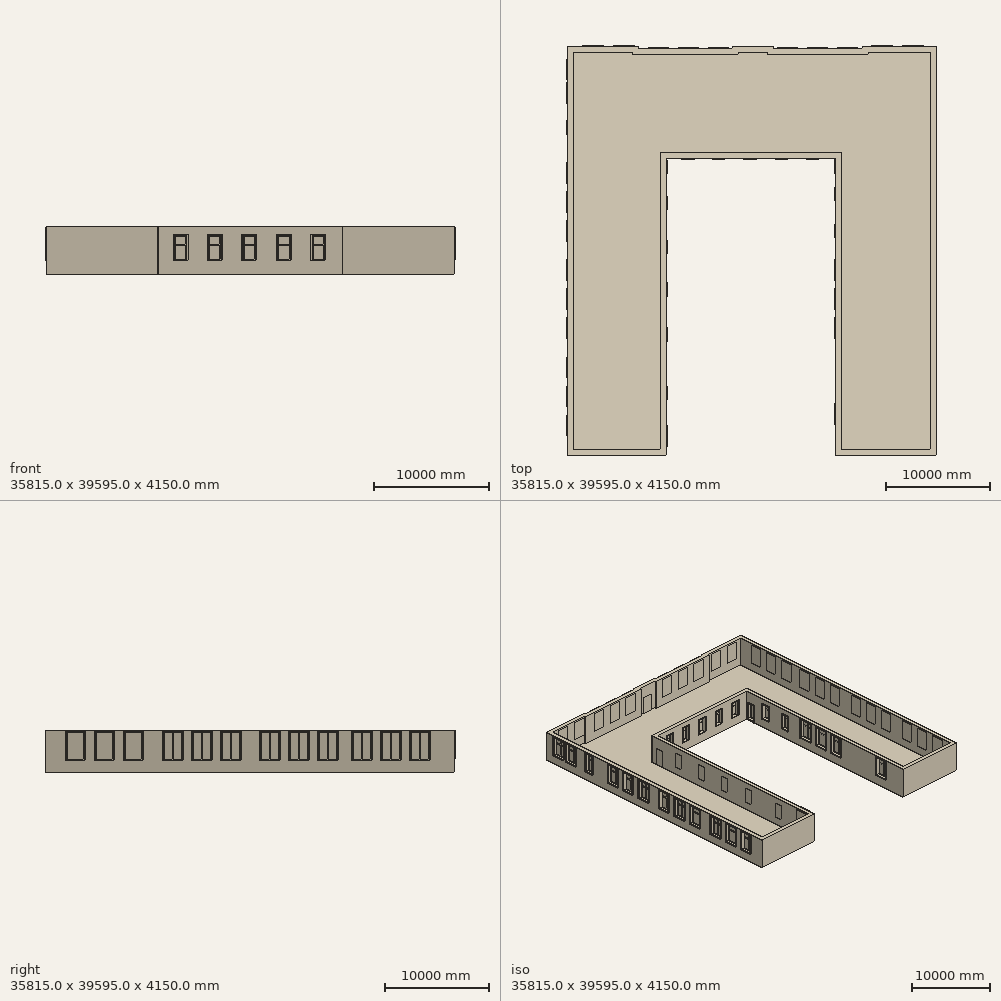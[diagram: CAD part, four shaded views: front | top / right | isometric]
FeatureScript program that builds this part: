
annotation { "Feature Type Name" : "Feature", "Feature Type Description" : "" }
export const myFeature = defineFeature(function(context is Context, id is Id, definition is map)
    precondition{}
    {
        {
            var Q0;
            Q0=qCreatedBy(makeId("Top.planeOp"),FACE);
            var sketch = newSketch(context, id + "F0", { "sketchPlane" : qUnion([Q0])});
            skLineSegment(sketch, "E0", {"start": v(0, 0) * mm, "end": v(0, 39360) * mm});
            skLineSegment(sketch, "E1", {"start": v(0, 39360) * mm, "end": v(-7000, 39360) * mm});
            skLineSegment(sketch, "E2", {"start": v(-7000, 39360) * mm, "end": v(-7000, 39160) * mm});
            skLineSegment(sketch, "E3", {"start": v(-7000, 39160) * mm, "end": v(-15730, 39160) * mm});
            skLineSegment(sketch, "E4", {"start": v(-15730, 39160) * mm, "end": v(-15730, 39360) * mm});
            skLineSegment(sketch, "E5", {"start": v(-15730, 39360) * mm, "end": v(-19480, 39360) * mm});
            skLineSegment(sketch, "E6", {"start": v(-19480, 39360) * mm, "end": v(-19480, 39160) * mm});
            skLineSegment(sketch, "E7", {"start": v(-19480, 39160) * mm, "end": v(-28730, 39160) * mm});
            skLineSegment(sketch, "E8", {"start": v(-28730, 39160) * mm, "end": v(-28730, 39360) * mm});
            skLineSegment(sketch, "E9", {"start": v(-28730, 39360) * mm, "end": v(-35480, 39360) * mm});
            skLineSegment(sketch, "E10", {"start": v(-35480, 39360) * mm, "end": v(-35480, 0) * mm});
            skLineSegment(sketch, "E11", {"start": v(-35480, 0) * mm, "end": v(-26000, 0) * mm});
            skLineSegment(sketch, "E12", {"start": v(-26000, 0) * mm, "end": v(-26000, 28660) * mm});
            skLineSegment(sketch, "E13", {"start": v(-26000, 28660) * mm, "end": v(-9600, 28660) * mm});
            skLineSegment(sketch, "E14", {"start": v(-9600, 28660) * mm, "end": v(-9600, 0) * mm});
            skLineSegment(sketch, "E15", {"start": v(-9600, 0) * mm, "end": v(0, 0) * mm});
            skLineSegment(sketch, "E16.0", {"start": v(-500, 500) * mm, "end": v(-500, 38860) * mm});
            skLineSegment(sketch, "E16.1", {"start": v(-9100, 500) * mm, "end": v(-500, 500) * mm});
            skLineSegment(sketch, "E16.2", {"start": v(-9100, 29160) * mm, "end": v(-9100, 500) * mm});
            skLineSegment(sketch, "E16.3", {"start": v(-26500, 29160) * mm, "end": v(-9100, 29160) * mm});
            skLineSegment(sketch, "E16.4", {"start": v(-26500, 500) * mm, "end": v(-26500, 29160) * mm});
            skLineSegment(sketch, "E16.5", {"start": v(-16230, 38860) * mm, "end": v(-18980, 38860) * mm});
            skLineSegment(sketch, "E16.6", {"start": v(-16230, 38660) * mm, "end": v(-16230, 38860) * mm});
            skLineSegment(sketch, "E16.7", {"start": v(-6500, 38660) * mm, "end": v(-16230, 38660) * mm});
            skLineSegment(sketch, "E16.8", {"start": v(-6500, 38860) * mm, "end": v(-6500, 38660) * mm});
            skLineSegment(sketch, "E16.9", {"start": v(-18980, 38860) * mm, "end": v(-18980, 38660) * mm});
            skLineSegment(sketch, "E16.10", {"start": v(-18980, 38660) * mm, "end": v(-29230, 38660) * mm});
            skLineSegment(sketch, "E16.11", {"start": v(-29230, 38660) * mm, "end": v(-29230, 38860) * mm});
            skLineSegment(sketch, "E16.12", {"start": v(-29230, 38860) * mm, "end": v(-34980, 38860) * mm});
            skLineSegment(sketch, "E16.13", {"start": v(-34980, 38860) * mm, "end": v(-34980, 500) * mm});
            skLineSegment(sketch, "E16.14", {"start": v(-500, 38860) * mm, "end": v(-6500, 38860) * mm});
            skLineSegment(sketch, "E16.15", {"start": v(-34980, 500) * mm, "end": v(-26500, 500) * mm});
            skLineSegment(sketch, "E17.0", {"start": v(-28640, 39250) * mm, "end": v(-28640, 39450) * mm});
            skLineSegment(sketch, "E17.1", {"start": v(-19570, 39250) * mm, "end": v(-28640, 39250) * mm});
            skLineSegment(sketch, "E17.2", {"start": v(-19570, 39450) * mm, "end": v(-19570, 39250) * mm});
            skLineSegment(sketch, "E17.3", {"start": v(-15640, 39450) * mm, "end": v(-19570, 39450) * mm});
            skLineSegment(sketch, "E17.4", {"start": v(-15640, 39250) * mm, "end": v(-15640, 39450) * mm});
            skLineSegment(sketch, "E17.5", {"start": v(-25910, 28570) * mm, "end": v(-9690, 28570) * mm});
            skLineSegment(sketch, "E17.6", {"start": v(-25910, -90) * mm, "end": v(-25910, 28570) * mm});
            skLineSegment(sketch, "E17.7", {"start": v(-35570, -90) * mm, "end": v(-25910, -90) * mm});
            skLineSegment(sketch, "E17.8", {"start": v(-35570, 39450) * mm, "end": v(-35570, -90) * mm});
            skLineSegment(sketch, "E17.9", {"start": v(-9690, 28570) * mm, "end": v(-9690, -90) * mm});
            skLineSegment(sketch, "E17.10", {"start": v(-9690, -90) * mm, "end": v(90, -90) * mm});
            skLineSegment(sketch, "E17.11", {"start": v(90, -90) * mm, "end": v(90, 39450) * mm});
            skLineSegment(sketch, "E17.12", {"start": v(90, 39450) * mm, "end": v(-7090, 39450) * mm});
            skLineSegment(sketch, "E17.13", {"start": v(-7090, 39450) * mm, "end": v(-7090, 39250) * mm});
            skLineSegment(sketch, "E17.14", {"start": v(-28640, 39450) * mm, "end": v(-35570, 39450) * mm});
            skLineSegment(sketch, "E17.15", {"start": v(-7090, 39250) * mm, "end": v(-15640, 39250) * mm});
            skSolve(sketch);
        }
        {
            var Q0;
            Q0=qSketchRegion(id+"F0",true);
            var Q1;
            Q1=makeQuery(id+"F0.imprint","IMPRINT",FACE,{"disambiguationData":[TD([[makeQuery(id+"F0.imprint","IMPRINT",EDGE,{"derivedFrom":sQuery(id+"F0.wireOp",EDGE,"E0")}),1.0]])]});
            extrude(context, id + "F1", {"entities" : qUnion([Q0, Q1]), "depth" : 4000 * mm, "offsetDistance" : 25 * mm});
        }
        {
            var Q0;
            Q0=makeQuery(id+"F1.opExtrude","CAP_FACE",FACE,{"disambiguationData":[OSD([sQuery(id+"F0.wireOp",EDGE,"E16.0"),sQuery(id+"F0.wireOp",EDGE,"E16.1"),sQuery(id+"F0.wireOp",EDGE,"E16.2"),sQuery(id+"F0.wireOp",EDGE,"E16.3"),sQuery(id+"F0.wireOp",EDGE,"E16.4"),sQuery(id+"F0.wireOp",EDGE,"E16.5"),sQuery(id+"F0.wireOp",EDGE,"E16.6"),sQuery(id+"F0.wireOp",EDGE,"E16.7"),sQuery(id+"F0.wireOp",EDGE,"E16.8"),sQuery(id+"F0.wireOp",EDGE,"E16.9"),sQuery(id+"F0.wireOp",EDGE,"E16.10"),sQuery(id+"F0.wireOp",EDGE,"E16.11"),sQuery(id+"F0.wireOp",EDGE,"E16.12"),sQuery(id+"F0.wireOp",EDGE,"E16.13"),sQuery(id+"F0.wireOp",EDGE,"E16.14"),sQuery(id+"F0.wireOp",EDGE,"E16.15"),sQuery(id+"F0.wireOp",EDGE,"E17.0"),sQuery(id+"F0.wireOp",EDGE,"E17.1"),sQuery(id+"F0.wireOp",EDGE,"E17.2"),sQuery(id+"F0.wireOp",EDGE,"E17.3"),sQuery(id+"F0.wireOp",EDGE,"E17.4"),sQuery(id+"F0.wireOp",EDGE,"E17.5"),sQuery(id+"F0.wireOp",EDGE,"E17.6"),sQuery(id+"F0.wireOp",EDGE,"E17.7"),sQuery(id+"F0.wireOp",EDGE,"E17.8"),sQuery(id+"F0.wireOp",EDGE,"E17.9"),sQuery(id+"F0.wireOp",EDGE,"E17.10"),sQuery(id+"F0.wireOp",EDGE,"E17.11"),sQuery(id+"F0.wireOp",EDGE,"E17.12"),sQuery(id+"F0.wireOp",EDGE,"E17.13"),sQuery(id+"F0.wireOp",EDGE,"E17.14"),sQuery(id+"F0.wireOp",EDGE,"E17.15")])],"isStart":false});
            var sketch = newSketch(context, id + "F2", { "sketchPlane" : qUnion([Q0])});
            skLineSegment(sketch, "E18.0.0", {"start": v(-9690, 28570) * mm, "end": v(-9690, -90) * mm});
            skLineSegment(sketch, "E18.0.1", {"start": v(-9690, -90) * mm, "end": v(90, -90) * mm});
            skLineSegment(sketch, "E18.0.2", {"start": v(90, -90) * mm, "end": v(90, 39450) * mm});
            skLineSegment(sketch, "E18.0.3", {"start": v(90, 39450) * mm, "end": v(-7090, 39450) * mm});
            skLineSegment(sketch, "E18.0.4", {"start": v(-7090, 39450) * mm, "end": v(-7090, 39250) * mm});
            skLineSegment(sketch, "E18.0.5", {"start": v(-7090, 39250) * mm, "end": v(-15640, 39250) * mm});
            skLineSegment(sketch, "E18.0.6", {"start": v(-15640, 39250) * mm, "end": v(-15640, 39450) * mm});
            skLineSegment(sketch, "E18.0.7", {"start": v(-15640, 39450) * mm, "end": v(-19570, 39450) * mm});
            skLineSegment(sketch, "E18.0.8", {"start": v(-19570, 39450) * mm, "end": v(-19570, 39250) * mm});
            skLineSegment(sketch, "E18.0.9", {"start": v(-19570, 39250) * mm, "end": v(-28640, 39250) * mm});
            skLineSegment(sketch, "E18.0.10", {"start": v(-28640, 39250) * mm, "end": v(-28640, 39450) * mm});
            skLineSegment(sketch, "E18.0.11", {"start": v(-28640, 39450) * mm, "end": v(-35570, 39450) * mm});
            skLineSegment(sketch, "E18.0.12", {"start": v(-35570, 39450) * mm, "end": v(-35570, -90) * mm});
            skLineSegment(sketch, "E18.0.13", {"start": v(-35570, -90) * mm, "end": v(-25910, -90) * mm});
            skLineSegment(sketch, "E18.0.14", {"start": v(-25910, -90) * mm, "end": v(-25910, 28570) * mm});
            skLineSegment(sketch, "E18.0.15", {"start": v(-25910, 28570) * mm, "end": v(-9690, 28570) * mm});
            skLineSegment(sketch, "E19.0", {"start": v(-19560, 39440) * mm, "end": v(-19560, 39240) * mm});
            skLineSegment(sketch, "E19.1", {"start": v(-15650, 39440) * mm, "end": v(-19560, 39440) * mm});
            skLineSegment(sketch, "E19.2", {"start": v(-15650, 39240) * mm, "end": v(-15650, 39440) * mm});
            skLineSegment(sketch, "E19.3", {"start": v(-7080, 39240) * mm, "end": v(-15650, 39240) * mm});
            skLineSegment(sketch, "E19.4", {"start": v(-7080, 39440) * mm, "end": v(-7080, 39240) * mm});
            skLineSegment(sketch, "E19.5", {"start": v(-35560, -80) * mm, "end": v(-25920, -80) * mm});
            skLineSegment(sketch, "E19.6", {"start": v(-35560, 39440) * mm, "end": v(-35560, -80) * mm});
            skLineSegment(sketch, "E19.7", {"start": v(-28650, 39440) * mm, "end": v(-35560, 39440) * mm});
            skLineSegment(sketch, "E19.8", {"start": v(-28650, 39240) * mm, "end": v(-28650, 39440) * mm});
            skLineSegment(sketch, "E19.9", {"start": v(-25920, -80) * mm, "end": v(-25920, 28580) * mm});
            skLineSegment(sketch, "E19.10", {"start": v(-25920, 28580) * mm, "end": v(-9680, 28580) * mm});
            skLineSegment(sketch, "E19.11", {"start": v(-9680, 28580) * mm, "end": v(-9680, -80) * mm});
            skLineSegment(sketch, "E19.12", {"start": v(-9680, -80) * mm, "end": v(80, -80) * mm});
            skLineSegment(sketch, "E19.13", {"start": v(80, -80) * mm, "end": v(80, 39440) * mm});
            skLineSegment(sketch, "E19.14", {"start": v(-19560, 39240) * mm, "end": v(-28650, 39240) * mm});
            skLineSegment(sketch, "E19.15", {"start": v(80, 39440) * mm, "end": v(-7080, 39440) * mm});
            skSolve(sketch);
        }
        {
            var Q0;
            Q0=qSketchRegion(id+"F2",true);
            var Q1;
            Q1=makeQuery(id+"F1.opExtrude","CAP_VERTEX",VERTEX,{"disambiguationData":[OSD([sQuery(id+"F0.wireOp",EDGE,"E17.8"),sQuery(id+"F0.wireOp",EDGE,"E17.14")])],"isStart":true});
            extrude(context, id + "F3", {"entities" : qUnion([Q0]), "operationType" : NewBodyOperationType.REMOVE, "endBound" : BoundingType.UP_TO_VERTEX, "oppositeDirection" : true, "depth" : 25 * mm, "endBoundEntityVertex" : qUnion([Q1]), "offsetDistance" : 25 * mm});
        }
        {
            var Q0;
            Q0=makeQuery(id+"F1.opExtrude","CAP_FACE",FACE,{"disambiguationData":[OSD([sQuery(id+"F0.wireOp",EDGE,"E0"),sQuery(id+"F0.wireOp",EDGE,"E1"),sQuery(id+"F0.wireOp",EDGE,"E2"),sQuery(id+"F0.wireOp",EDGE,"E3"),sQuery(id+"F0.wireOp",EDGE,"E4"),sQuery(id+"F0.wireOp",EDGE,"E5"),sQuery(id+"F0.wireOp",EDGE,"E6"),sQuery(id+"F0.wireOp",EDGE,"E7"),sQuery(id+"F0.wireOp",EDGE,"E8"),sQuery(id+"F0.wireOp",EDGE,"E9"),sQuery(id+"F0.wireOp",EDGE,"E10"),sQuery(id+"F0.wireOp",EDGE,"E11"),sQuery(id+"F0.wireOp",EDGE,"E12"),sQuery(id+"F0.wireOp",EDGE,"E13"),sQuery(id+"F0.wireOp",EDGE,"E14"),sQuery(id+"F0.wireOp",EDGE,"E15"),sQuery(id+"F0.wireOp",EDGE,"E16.0"),sQuery(id+"F0.wireOp",EDGE,"E16.1"),sQuery(id+"F0.wireOp",EDGE,"E16.2"),sQuery(id+"F0.wireOp",EDGE,"E16.3"),sQuery(id+"F0.wireOp",EDGE,"E16.4"),sQuery(id+"F0.wireOp",EDGE,"E16.5"),sQuery(id+"F0.wireOp",EDGE,"E16.6"),sQuery(id+"F0.wireOp",EDGE,"E16.7"),sQuery(id+"F0.wireOp",EDGE,"E16.8"),sQuery(id+"F0.wireOp",EDGE,"E16.9"),sQuery(id+"F0.wireOp",EDGE,"E16.10"),sQuery(id+"F0.wireOp",EDGE,"E16.11"),sQuery(id+"F0.wireOp",EDGE,"E16.12"),sQuery(id+"F0.wireOp",EDGE,"E16.13"),sQuery(id+"F0.wireOp",EDGE,"E16.14"),sQuery(id+"F0.wireOp",EDGE,"E16.15")])],"isStart":true});
            var sketch = newSketch(context, id + "F4", { "sketchPlane" : qUnion([Q0])});
            skLineSegment(sketch, "E20", {"start": v(-35560, -39440) * mm, "end": v(-35560, 80) * mm});
            skLineSegment(sketch, "E21", {"start": v(-15650, -39440) * mm, "end": v(-19560, -39440) * mm});
            skLineSegment(sketch, "E22", {"start": v(-19560, -39440) * mm, "end": v(-19560, -39240) * mm});
            skLineSegment(sketch, "E23", {"start": v(-19560, -39240) * mm, "end": v(-28650, -39240) * mm});
            skLineSegment(sketch, "E24", {"start": v(-28650, -39240) * mm, "end": v(-28650, -39440) * mm});
            skLineSegment(sketch, "E25", {"start": v(-28650, -39440) * mm, "end": v(-35560, -39440) * mm});
            skLineSegment(sketch, "E26.0", {"start": v(-15650, -39240) * mm, "end": v(-15650, -39440) * mm});
            skLineSegment(sketch, "E27.0", {"start": v(-7080, -39240) * mm, "end": v(-15650, -39240) * mm});
            skLineSegment(sketch, "E28.0", {"start": v(-7080, -39440) * mm, "end": v(-7080, -39240) * mm});
            skLineSegment(sketch, "E29.0", {"start": v(80, -39440) * mm, "end": v(-7080, -39440) * mm});
            skLineSegment(sketch, "E30.0", {"start": v(80, 80) * mm, "end": v(80, -39440) * mm});
            skLineSegment(sketch, "E31.0", {"start": v(-9680, 80) * mm, "end": v(80, 80) * mm});
            skLineSegment(sketch, "E32.0", {"start": v(-9680, -28580) * mm, "end": v(-9680, 80) * mm});
            skLineSegment(sketch, "E33.0", {"start": v(-25920, -28580) * mm, "end": v(-9680, -28580) * mm});
            skLineSegment(sketch, "E34.0", {"start": v(-25920, 80) * mm, "end": v(-25920, -28580) * mm});
            skLineSegment(sketch, "E35.0", {"start": v(-35560, 80) * mm, "end": v(-25920, 80) * mm});
            skSolve(sketch);
        }
        {
            var Q0;
            {var subQ0=makeQuery(id+"F1.opExtrude","CAP_EDGE",EDGE,{"disambiguationData":[OSD([sQuery(id+"F0.wireOp",EDGE,"E16.10")])],"isStart":true});Q0=makeQuery(id+"F4.imprint","IMPRINT",FACE,{"disambiguationData":[TD([[makeQuery(id+"F4.imprint","IMPRINT",EDGE,{"derivedFrom":subQ0}),-1.0]])]});}
            var Q1;
            {var subQ8=sQuery(id+"F4.wireOp",EDGE,"E20");Q1=makeQuery(id+"F4.imprint","IMPRINT",FACE,{"disambiguationData":[TD([[makeQuery(id+"F4.imprint","IMPRINT",EDGE,{"derivedFrom":subQ8}),-1.0]])]});}
            var Q2;
            {var subQ5=sQuery(id+"F4.wireOp",EDGE,"WrZoUcTY-9wdJ-lOnS-oAZQ-S74aqCpjquS9");var subQ6=makeQuery(id+"F4.imprint","INTERSECT",VERTEX,{"derivedFrom":[makeQuery(id+"F1.opExtrude","CAP_EDGE",EDGE,{"disambiguationData":[OSD([sQuery(id+"F0.wireOp",EDGE,"E12")])],"isStart":true}),subQ5]});Q2=makeQuery(id+"F4.imprint","IMPRINT",FACE,{"disambiguationData":[TD([[makeQuery(id+"F4.imprint","IMPRINT",EDGE,{"disambiguationData":[TD([[subQ6,1.0]])],"derivedFrom":subQ5}),-1.0]])]});}
            extrude(context, id + "F5", {"entities" : qUnion([Q0, Q1, Q2]), "operationType" : NewBodyOperationType.ADD, "depth" : 150 * mm, "offsetDistance" : 25 * mm});
        }
        {
            var Q0;
            Q0=makeQuery(id+"F5.boolean.opBoolean","MERGE",FACE,{"derivedFrom":[makeQuery(id+"F1.opExtrude","SWEPT_FACE",FACE,{"disambiguationData":[OSD([sQuery(id+"F0.wireOp",EDGE,"E7")])]}),makeQuery(id+"F5.opExtrude","SWEPT_FACE",FACE,{"disambiguationData":[OSD([sQuery(id+"F4.wireOp",EDGE,"E23")])]})]});
            var sketch = newSketch(context, id + "F6", { "sketchPlane" : qUnion([Q0])});
            skLineSegment(sketch, "E36.bottom", {"start": v(20080, 3800) * mm, "end": v(21780, 3800) * mm});
            skLineSegment(sketch, "E36.top", {"start": v(20080, 1200) * mm, "end": v(21780, 1200) * mm});
            skLineSegment(sketch, "E36.left", {"start": v(20080, 3800) * mm, "end": v(20080, 1200) * mm});
            skLineSegment(sketch, "E36.right", {"start": v(21780, 3800) * mm, "end": v(21780, 1200) * mm});
            skLineSegment(sketch, "E37.bottom", {"start": v(22980, 3800) * mm, "end": v(24680, 3800) * mm});
            skLineSegment(sketch, "E37.top", {"start": v(22980, 1200) * mm, "end": v(24680, 1200) * mm});
            skLineSegment(sketch, "E37.left", {"start": v(22980, 3800) * mm, "end": v(22980, 1200) * mm});
            skLineSegment(sketch, "E37.right", {"start": v(24680, 3800) * mm, "end": v(24680, 1200) * mm});
            skLineSegment(sketch, "E38.bottom", {"start": v(25880, 3800) * mm, "end": v(27580, 3800) * mm});
            skLineSegment(sketch, "E38.top", {"start": v(25880, 1200) * mm, "end": v(27580, 1200) * mm});
            skLineSegment(sketch, "E38.left", {"start": v(25880, 3800) * mm, "end": v(25880, 1200) * mm});
            skLineSegment(sketch, "E38.right", {"start": v(27580, 3800) * mm, "end": v(27580, 1200) * mm});
            skLineSegment(sketch, "E39", {"start": v(17605, -150) * mm, "end": v(17605, 3306.36) * mm, "construction": true});
            skLineSegment(sketch, "E40.MirrorCS", {"start": v(15130, 3800) * mm, "end": v(15130, 1200) * mm});
            skLineSegment(sketch, "E41.MirrorCS", {"start": v(7630, 3800) * mm, "end": v(7630, 1200) * mm});
            skLineSegment(sketch, "E42.MirrorCS", {"start": v(10530, 3800) * mm, "end": v(10530, 1200) * mm});
            skLineSegment(sketch, "E43.MirrorCS", {"start": v(9330, 3800) * mm, "end": v(9330, 1200) * mm});
            skLineSegment(sketch, "E44.MirrorCS", {"start": v(9330, 3800) * mm, "end": v(7630, 3800) * mm});
            skLineSegment(sketch, "E45.MirrorCS", {"start": v(12230, 3800) * mm, "end": v(12230, 1200) * mm});
            skLineSegment(sketch, "E46.MirrorCS", {"start": v(12230, 1200) * mm, "end": v(10530, 1200) * mm});
            skLineSegment(sketch, "E47.MirrorCS", {"start": v(15130, 3800) * mm, "end": v(13430, 3800) * mm});
            skLineSegment(sketch, "E48.MirrorCS", {"start": v(15130, 1200) * mm, "end": v(13430, 1200) * mm});
            skLineSegment(sketch, "E49.MirrorCS", {"start": v(9330, 1200) * mm, "end": v(7630, 1200) * mm});
            skLineSegment(sketch, "E50.MirrorCS", {"start": v(13430, 3800) * mm, "end": v(13430, 1200) * mm});
            skLineSegment(sketch, "E51.MirrorCS", {"start": v(12230, 3800) * mm, "end": v(10530, 3800) * mm});
            skSolve(sketch);
        }
        {
            var Q0;
            Q0=qSketchRegion(id+"F6",true);
            extrude(context, id + "F7", {"entities" : qUnion([Q0]), "operationType" : NewBodyOperationType.REMOVE, "oppositeDirection" : true, "depth" : 590 * mm, "offsetDistance" : 25 * mm});
        }
        {
            var Q0;
            Q0=makeQuery(id+"F1.opExtrude","SWEPT_FACE",FACE,{"disambiguationData":[OSD([sQuery(id+"F0.wireOp",EDGE,"E16.10")])]});
            var sketch = newSketch(context, id + "F8", { "sketchPlane" : qUnion([Q0])});
            skLineSegment(sketch, "E52.0", {"start": v(-20080, 3800) * mm, "end": v(-21780, 3800) * mm});
            skLineSegment(sketch, "E53.0", {"start": v(-20080, 3800) * mm, "end": v(-20080, 1200) * mm});
            skLineSegment(sketch, "E54.0", {"start": v(-20080, 1200) * mm, "end": v(-21780, 1200) * mm});
            skLineSegment(sketch, "E55.0", {"start": v(-21780, 3800) * mm, "end": v(-21780, 1200) * mm});
            skLineSegment(sketch, "E56.0", {"start": v(-22980, 3800) * mm, "end": v(-22980, 1200) * mm});
            skLineSegment(sketch, "E57.0", {"start": v(-22980, 3800) * mm, "end": v(-24680, 3800) * mm});
            skLineSegment(sketch, "E58.0", {"start": v(-24680, 3800) * mm, "end": v(-24680, 1200) * mm});
            skLineSegment(sketch, "E59.0", {"start": v(-22980, 1200) * mm, "end": v(-24680, 1200) * mm});
            skLineSegment(sketch, "E60.0", {"start": v(-25880, 3800) * mm, "end": v(-27580, 3800) * mm});
            skLineSegment(sketch, "E61.0", {"start": v(-27580, 3800) * mm, "end": v(-27580, 1200) * mm});
            skLineSegment(sketch, "E62.0", {"start": v(-25880, 1200) * mm, "end": v(-27580, 1200) * mm});
            skLineSegment(sketch, "E63.0", {"start": v(-25880, 3800) * mm, "end": v(-25880, 1200) * mm});
            skLineSegment(sketch, "E64.0", {"start": v(-9330, 1200) * mm, "end": v(-7630, 1200) * mm});
            skLineSegment(sketch, "E65.0", {"start": v(-7630, 3800) * mm, "end": v(-7630, 1200) * mm});
            skLineSegment(sketch, "E66.0", {"start": v(-9330, 3800) * mm, "end": v(-7630, 3800) * mm});
            skLineSegment(sketch, "E67.0", {"start": v(-9330, 3800) * mm, "end": v(-9330, 1200) * mm});
            skLineSegment(sketch, "E68.0", {"start": v(-12230, 1200) * mm, "end": v(-10530, 1200) * mm});
            skLineSegment(sketch, "E69.0", {"start": v(-10530, 3800) * mm, "end": v(-10530, 1200) * mm});
            skLineSegment(sketch, "E70.0", {"start": v(-12230, 3800) * mm, "end": v(-10530, 3800) * mm});
            skLineSegment(sketch, "E71.0", {"start": v(-12230, 3800) * mm, "end": v(-12230, 1200) * mm});
            skLineSegment(sketch, "E72.0", {"start": v(-15130, 1200) * mm, "end": v(-13430, 1200) * mm});
            skLineSegment(sketch, "E73.0", {"start": v(-13430, 3800) * mm, "end": v(-13430, 1200) * mm});
            skLineSegment(sketch, "E74.0", {"start": v(-15130, 3800) * mm, "end": v(-13430, 3800) * mm});
            skLineSegment(sketch, "E75.0", {"start": v(-15130, 3800) * mm, "end": v(-15130, 1200) * mm});
            skSolve(sketch);
        }
        {
            var Q0;
            Q0=qSketchRegion(id+"F8",true);
            extrude(context, id + "F9", {"entities" : qUnion([Q0]), "oppositeDirection" : true, "depth" : 5 * mm, "offsetDistance" : 25 * mm});
        }
        {
            var Q0;
            Q0=makeQuery(id+"F9.opExtrude","CAP_FACE",FACE,{"disambiguationData":[OSD([sQuery(id+"F8.wireOp",EDGE,"E60.0"),sQuery(id+"F8.wireOp",EDGE,"E61.0"),sQuery(id+"F8.wireOp",EDGE,"E62.0"),sQuery(id+"F8.wireOp",EDGE,"E63.0")])],"isStart":false});
            var sketch = newSketch(context, id + "F10", { "sketchPlane" : qUnion([Q0])});
            skLineSegment(sketch, "E76.0.0", {"start": v(9330, 3800) * mm, "end": v(7630, 3800) * mm});
            skLineSegment(sketch, "E76.0.1", {"start": v(7630, 3800) * mm, "end": v(7630, 1200) * mm});
            skLineSegment(sketch, "E76.0.2", {"start": v(7630, 1200) * mm, "end": v(9330, 1200) * mm});
            skLineSegment(sketch, "E76.0.3", {"start": v(9330, 1200) * mm, "end": v(9330, 3800) * mm});
            skLineSegment(sketch, "E77", {"start": v(8480, 3800) * mm, "end": v(8480, 1200) * mm, "construction": true});
            skLineSegment(sketch, "E78.bottom", {"start": v(7680, 2850) * mm, "end": v(8442.5, 2850) * mm});
            skLineSegment(sketch, "E78.top", {"start": v(7680, 1250) * mm, "end": v(8442.5, 1250) * mm});
            skLineSegment(sketch, "E78.left", {"start": v(7680, 2850) * mm, "end": v(7680, 1250) * mm});
            skLineSegment(sketch, "E78.right", {"start": v(8442.5, 2850) * mm, "end": v(8442.5, 1250) * mm});
            skLineSegment(sketch, "E79.bottom", {"start": v(7680, 2900) * mm, "end": v(8442.5, 2900) * mm});
            skLineSegment(sketch, "E79.top", {"start": v(7680, 3750) * mm, "end": v(8442.5, 3750) * mm});
            skLineSegment(sketch, "E79.left", {"start": v(7680, 2900) * mm, "end": v(7680, 3750) * mm});
            skLineSegment(sketch, "E79.right", {"start": v(8442.5, 2900) * mm, "end": v(8442.5, 3750) * mm});
            skLineSegment(sketch, "E80.MirrorCS", {"start": v(9280, 3750) * mm, "end": v(8517.5, 3750) * mm});
            skLineSegment(sketch, "E81.MirrorCS", {"start": v(9280, 2900) * mm, "end": v(9280, 3750) * mm});
            skLineSegment(sketch, "E82.MirrorCS", {"start": v(8517.5, 2900) * mm, "end": v(8517.5, 3750) * mm});
            skLineSegment(sketch, "E83.MirrorCS", {"start": v(9280, 2900) * mm, "end": v(8517.5, 2900) * mm});
            skLineSegment(sketch, "E84.MirrorCS", {"start": v(9280, 2850) * mm, "end": v(8517.5, 2850) * mm});
            skLineSegment(sketch, "E85.MirrorCS", {"start": v(8517.5, 2850) * mm, "end": v(8517.5, 1250) * mm});
            skLineSegment(sketch, "E86.MirrorCS", {"start": v(9280, 2850) * mm, "end": v(9280, 1250) * mm});
            skLineSegment(sketch, "E87.MirrorCS", {"start": v(9280, 1250) * mm, "end": v(8517.5, 1250) * mm});
            skLineSegment(sketch, "E88.0.0", {"start": v(12229.64, 3800) * mm, "end": v(10529.64, 3800) * mm});
            skLineSegment(sketch, "E88.0.1", {"start": v(10529.64, 3800) * mm, "end": v(10529.64, 1200) * mm});
            skLineSegment(sketch, "E88.0.2", {"start": v(10529.64, 1200) * mm, "end": v(12229.64, 1200) * mm});
            skLineSegment(sketch, "E88.0.3", {"start": v(12229.64, 1200) * mm, "end": v(12229.64, 3800) * mm});
            skLineSegment(sketch, "E89", {"start": v(11379.64, 3800) * mm, "end": v(11379.64, 1200) * mm, "construction": true});
            skLineSegment(sketch, "E90.bottom", {"start": v(10579.64, 2850) * mm, "end": v(11342.14, 2850) * mm});
            skLineSegment(sketch, "E90.top", {"start": v(10579.64, 1250) * mm, "end": v(11342.14, 1250) * mm});
            skLineSegment(sketch, "E90.left", {"start": v(10579.64, 2850) * mm, "end": v(10579.64, 1250) * mm});
            skLineSegment(sketch, "E90.right", {"start": v(11342.14, 2850) * mm, "end": v(11342.14, 1250) * mm});
            skLineSegment(sketch, "E91.bottom", {"start": v(10579.64, 2900) * mm, "end": v(11342.14, 2900) * mm});
            skLineSegment(sketch, "E91.top", {"start": v(10579.64, 3750) * mm, "end": v(11342.14, 3750) * mm});
            skLineSegment(sketch, "E91.left", {"start": v(10579.64, 2900) * mm, "end": v(10579.64, 3750) * mm});
            skLineSegment(sketch, "E91.right", {"start": v(11342.14, 2900) * mm, "end": v(11342.14, 3750) * mm});
            skLineSegment(sketch, "E92.MirrorCS", {"start": v(12179.64, 3750) * mm, "end": v(11417.14, 3750) * mm});
            skLineSegment(sketch, "E93.MirrorCS", {"start": v(12179.64, 2900) * mm, "end": v(12179.64, 3750) * mm});
            skLineSegment(sketch, "E94.MirrorCS", {"start": v(11417.14, 2900) * mm, "end": v(11417.14, 3750) * mm});
            skLineSegment(sketch, "E95.MirrorCS", {"start": v(12179.64, 2900) * mm, "end": v(11417.14, 2900) * mm});
            skLineSegment(sketch, "E96.MirrorCS", {"start": v(12179.64, 2850) * mm, "end": v(11417.14, 2850) * mm});
            skLineSegment(sketch, "E97.MirrorCS", {"start": v(11417.14, 2850) * mm, "end": v(11417.14, 1250) * mm});
            skLineSegment(sketch, "E98.MirrorCS", {"start": v(12179.64, 2850) * mm, "end": v(12179.64, 1250) * mm});
            skLineSegment(sketch, "E99.MirrorCS", {"start": v(12179.64, 1250) * mm, "end": v(11417.14, 1250) * mm});
            skLineSegment(sketch, "E100", {"start": v(17605, -150) * mm, "end": v(17605, 2939.63) * mm, "construction": true});
            skLineSegment(sketch, "E101.MirrorCS", {"start": v(24680.36, 1200) * mm, "end": v(22980.36, 1200) * mm});
            skLineSegment(sketch, "E102.MirrorCS", {"start": v(26767.5, 2900) * mm, "end": v(26767.5, 3750) * mm});
            skLineSegment(sketch, "E103.MirrorCS", {"start": v(23867.86, 2900) * mm, "end": v(23867.86, 3750) * mm});
            skLineSegment(sketch, "E104.MirrorCS", {"start": v(26767.5, 2850) * mm, "end": v(26767.5, 1250) * mm});
            skLineSegment(sketch, "E105.MirrorCS", {"start": v(27580, 1200) * mm, "end": v(25880, 1200) * mm});
            skLineSegment(sketch, "E106.MirrorCS", {"start": v(23867.86, 2850) * mm, "end": v(23867.86, 1250) * mm});
            skLineSegment(sketch, "E107.MirrorCS", {"start": v(23030.36, 1250) * mm, "end": v(23792.86, 1250) * mm});
            skLineSegment(sketch, "E108.MirrorCS", {"start": v(27530, 2850) * mm, "end": v(27530, 1250) * mm});
            skLineSegment(sketch, "E109.MirrorCS", {"start": v(27530, 1250) * mm, "end": v(26767.5, 1250) * mm});
            skLineSegment(sketch, "E110.MirrorCS", {"start": v(23030.36, 2850) * mm, "end": v(23792.86, 2850) * mm});
            skLineSegment(sketch, "E111.MirrorCS", {"start": v(24630.36, 3750) * mm, "end": v(23867.86, 3750) * mm});
            skLineSegment(sketch, "E112.MirrorCS", {"start": v(22980.36, 3800) * mm, "end": v(24680.36, 3800) * mm});
            skLineSegment(sketch, "E113.MirrorCS", {"start": v(23030.36, 2900) * mm, "end": v(23792.86, 2900) * mm});
            skLineSegment(sketch, "E114.MirrorCS", {"start": v(27530, 3750) * mm, "end": v(26767.5, 3750) * mm});
            skLineSegment(sketch, "E115.MirrorCS", {"start": v(22980.36, 1200) * mm, "end": v(22980.36, 3800) * mm});
            skLineSegment(sketch, "E116.MirrorCS", {"start": v(27530, 2850) * mm, "end": v(26767.5, 2850) * mm});
            skLineSegment(sketch, "E117.MirrorCS", {"start": v(23030.36, 2850) * mm, "end": v(23030.36, 1250) * mm});
            skLineSegment(sketch, "E118.MirrorCS", {"start": v(23792.86, 2900) * mm, "end": v(23792.86, 3750) * mm});
            skLineSegment(sketch, "E119.MirrorCS", {"start": v(23830.36, 3800) * mm, "end": v(23830.36, 1200) * mm, "construction": true});
            skLineSegment(sketch, "E120.MirrorCS", {"start": v(26692.5, 2850) * mm, "end": v(26692.5, 1250) * mm});
            skLineSegment(sketch, "E121.MirrorCS", {"start": v(24630.36, 1250) * mm, "end": v(23867.86, 1250) * mm});
            skLineSegment(sketch, "E122.MirrorCS", {"start": v(25930, 2850) * mm, "end": v(25930, 1250) * mm});
            skLineSegment(sketch, "E123.MirrorCS", {"start": v(26692.5, 2900) * mm, "end": v(26692.5, 3750) * mm});
            skLineSegment(sketch, "E124.MirrorCS", {"start": v(27580, 3800) * mm, "end": v(27580, 1200) * mm});
            skLineSegment(sketch, "E125.MirrorCS", {"start": v(25930, 2900) * mm, "end": v(25930, 3750) * mm});
            skLineSegment(sketch, "E126.MirrorCS", {"start": v(25880, 1200) * mm, "end": v(25880, 3800) * mm});
            skLineSegment(sketch, "E127.MirrorCS", {"start": v(23030.36, 2900) * mm, "end": v(23030.36, 3750) * mm});
            skLineSegment(sketch, "E128.MirrorCS", {"start": v(25930, 2900) * mm, "end": v(26692.5, 2900) * mm});
            skLineSegment(sketch, "E129.MirrorCS", {"start": v(25930, 3750) * mm, "end": v(26692.5, 3750) * mm});
            skLineSegment(sketch, "E130.MirrorCS", {"start": v(25930, 2850) * mm, "end": v(26692.5, 2850) * mm});
            skLineSegment(sketch, "E131.MirrorCS", {"start": v(23792.86, 2850) * mm, "end": v(23792.86, 1250) * mm});
            skLineSegment(sketch, "E132.MirrorCS", {"start": v(23030.36, 3750) * mm, "end": v(23792.86, 3750) * mm});
            skLineSegment(sketch, "E133.MirrorCS", {"start": v(24630.36, 2850) * mm, "end": v(23867.86, 2850) * mm});
            skLineSegment(sketch, "E134.MirrorCS", {"start": v(24630.36, 2850) * mm, "end": v(24630.36, 1250) * mm});
            skLineSegment(sketch, "E135.MirrorCS", {"start": v(27530, 2900) * mm, "end": v(26767.5, 2900) * mm});
            skLineSegment(sketch, "E136.MirrorCS", {"start": v(25930, 1250) * mm, "end": v(26692.5, 1250) * mm});
            skLineSegment(sketch, "E137.MirrorCS", {"start": v(25880, 3800) * mm, "end": v(27580, 3800) * mm});
            skLineSegment(sketch, "E138.MirrorCS", {"start": v(24630.36, 2900) * mm, "end": v(23867.86, 2900) * mm});
            skLineSegment(sketch, "E139.MirrorCS", {"start": v(26730, 3800) * mm, "end": v(26730, 1200) * mm, "construction": true});
            skLineSegment(sketch, "E140.MirrorCS", {"start": v(27530, 2900) * mm, "end": v(27530, 3750) * mm});
            skLineSegment(sketch, "E141.MirrorCS", {"start": v(24630.36, 2900) * mm, "end": v(24630.36, 3750) * mm});
            skLineSegment(sketch, "E142.MirrorCS", {"start": v(24680.36, 3800) * mm, "end": v(24680.36, 1200) * mm});
            skPoint(sketch, "E143", {"position": v(20080, 1200) * mm});
            skPoint(sketch, "E144", {"position": v(13430, 1200) * mm});
            skLineSegment(sketch, "E145.0.0", {"start": v(15130, 3800) * mm, "end": v(13430, 3800) * mm});
            skLineSegment(sketch, "E145.0.1", {"start": v(13430, 3800) * mm, "end": v(13430, 1200) * mm});
            skLineSegment(sketch, "E145.0.2", {"start": v(13430, 1200) * mm, "end": v(15130, 1200) * mm});
            skLineSegment(sketch, "E145.0.3", {"start": v(15130, 1200) * mm, "end": v(15130, 3800) * mm});
            skLineSegment(sketch, "E146", {"start": v(14280, 3800) * mm, "end": v(14280, 1200) * mm, "construction": true});
            skLineSegment(sketch, "E147.bottom", {"start": v(13480, 2850) * mm, "end": v(14242.5, 2850) * mm});
            skLineSegment(sketch, "E147.top", {"start": v(13480, 1250) * mm, "end": v(14242.5, 1250) * mm});
            skLineSegment(sketch, "E147.left", {"start": v(13480, 2850) * mm, "end": v(13480, 1250) * mm});
            skLineSegment(sketch, "E147.right", {"start": v(14242.5, 2850) * mm, "end": v(14242.5, 1250) * mm});
            skLineSegment(sketch, "E148.bottom", {"start": v(13480, 2900) * mm, "end": v(14242.5, 2900) * mm});
            skLineSegment(sketch, "E148.top", {"start": v(13480, 3750) * mm, "end": v(14242.5, 3750) * mm});
            skLineSegment(sketch, "E148.left", {"start": v(13480, 2900) * mm, "end": v(13480, 3750) * mm});
            skLineSegment(sketch, "E148.right", {"start": v(14242.5, 2900) * mm, "end": v(14242.5, 3750) * mm});
            skLineSegment(sketch, "E149.MirrorCS", {"start": v(15080, 3750) * mm, "end": v(14317.5, 3750) * mm});
            skLineSegment(sketch, "E150.MirrorCS", {"start": v(15080, 2900) * mm, "end": v(15080, 3750) * mm});
            skLineSegment(sketch, "E151.MirrorCS", {"start": v(14317.5, 2900) * mm, "end": v(14317.5, 3750) * mm});
            skLineSegment(sketch, "E152.MirrorCS", {"start": v(15080, 2900) * mm, "end": v(14317.5, 2900) * mm});
            skLineSegment(sketch, "E153.MirrorCS", {"start": v(15080, 2850) * mm, "end": v(14317.5, 2850) * mm});
            skLineSegment(sketch, "E154.MirrorCS", {"start": v(14317.5, 2850) * mm, "end": v(14317.5, 1250) * mm});
            skLineSegment(sketch, "E155.MirrorCS", {"start": v(15080, 2850) * mm, "end": v(15080, 1250) * mm});
            skLineSegment(sketch, "E156.MirrorCS", {"start": v(15080, 1250) * mm, "end": v(14317.5, 1250) * mm});
            skLineSegment(sketch, "E157.0.0", {"start": v(21780, 3800) * mm, "end": v(20080, 3800) * mm});
            skLineSegment(sketch, "E157.0.1", {"start": v(20080, 3800) * mm, "end": v(20080, 1200) * mm});
            skLineSegment(sketch, "E157.0.2", {"start": v(20080, 1200) * mm, "end": v(21780, 1200) * mm});
            skLineSegment(sketch, "E157.0.3", {"start": v(21780, 1200) * mm, "end": v(21780, 3800) * mm});
            skLineSegment(sketch, "E158", {"start": v(20930, 3800) * mm, "end": v(20930, 1200) * mm, "construction": true});
            skLineSegment(sketch, "E159.bottom", {"start": v(20130, 2850) * mm, "end": v(20892.5, 2850) * mm});
            skLineSegment(sketch, "E159.top", {"start": v(20130, 1250) * mm, "end": v(20892.5, 1250) * mm});
            skLineSegment(sketch, "E159.left", {"start": v(20130, 2850) * mm, "end": v(20130, 1250) * mm});
            skLineSegment(sketch, "E159.right", {"start": v(20892.5, 2850) * mm, "end": v(20892.5, 1250) * mm});
            skLineSegment(sketch, "E160.bottom", {"start": v(20130, 2900) * mm, "end": v(20892.5, 2900) * mm});
            skLineSegment(sketch, "E160.top", {"start": v(20130, 3750) * mm, "end": v(20892.5, 3750) * mm});
            skLineSegment(sketch, "E160.left", {"start": v(20130, 2900) * mm, "end": v(20130, 3750) * mm});
            skLineSegment(sketch, "E160.right", {"start": v(20892.5, 2900) * mm, "end": v(20892.5, 3750) * mm});
            skLineSegment(sketch, "E161.MirrorCS", {"start": v(21730, 3750) * mm, "end": v(20967.5, 3750) * mm});
            skLineSegment(sketch, "E162.MirrorCS", {"start": v(21730, 2900) * mm, "end": v(21730, 3750) * mm});
            skLineSegment(sketch, "E163.MirrorCS", {"start": v(20967.5, 2900) * mm, "end": v(20967.5, 3750) * mm});
            skLineSegment(sketch, "E164.MirrorCS", {"start": v(21730, 2900) * mm, "end": v(20967.5, 2900) * mm});
            skLineSegment(sketch, "E165.MirrorCS", {"start": v(21730, 2850) * mm, "end": v(20967.5, 2850) * mm});
            skLineSegment(sketch, "E166.MirrorCS", {"start": v(20967.5, 2850) * mm, "end": v(20967.5, 1250) * mm});
            skLineSegment(sketch, "E167.MirrorCS", {"start": v(21730, 2850) * mm, "end": v(21730, 1250) * mm});
            skLineSegment(sketch, "E168.MirrorCS", {"start": v(21730, 1250) * mm, "end": v(20967.5, 1250) * mm});
            skSolve(sketch);
        }
        {
            var Q0;
            Q0=qSketchRegion(id+"F10",true);
            extrude(context, id + "F11", {"entities" : qUnion([Q0]), "depth" : 50 * mm, "offsetDistance" : 25 * mm});
        }
        {
            var Q0;
            Q0=makeQuery(id+"F5.boolean.opBoolean","MERGE",FACE,{"derivedFrom":[makeQuery(id+"F3.boolean.opBoolean","COPY",FACE,{"derivedFrom":makeQuery(id+"F3.opExtrude","SWEPT_FACE",FACE,{"disambiguationData":[OSD([sQuery(id+"F2.wireOp",EDGE,"E19.15")])]})}),makeQuery(id+"F5.opExtrude","SWEPT_FACE",FACE,{"disambiguationData":[OSD([sQuery(id+"F4.wireOp",EDGE,"E29.0")])]})]});
            var sketch = newSketch(context, id + "F12", { "sketchPlane" : qUnion([Q0])});
            skLineSegment(sketch, "E169.bottom", {"start": v(1280, 3800) * mm, "end": v(2980, 3800) * mm});
            skLineSegment(sketch, "E169.top", {"start": v(1280, 1200) * mm, "end": v(2980, 1200) * mm});
            skLineSegment(sketch, "E169.left", {"start": v(1280, 3800) * mm, "end": v(1280, 1200) * mm});
            skLineSegment(sketch, "E169.right", {"start": v(2980, 3800) * mm, "end": v(2980, 1200) * mm});
            skLineSegment(sketch, "E170.bottom", {"start": v(4280, 3800) * mm, "end": v(5980, 3800) * mm});
            skLineSegment(sketch, "E170.top", {"start": v(4280, 1200) * mm, "end": v(5980, 1200) * mm});
            skLineSegment(sketch, "E170.left", {"start": v(4280, 3800) * mm, "end": v(4280, 1200) * mm});
            skLineSegment(sketch, "E170.right", {"start": v(5980, 3800) * mm, "end": v(5980, 1200) * mm});
            skLineSegment(sketch, "E171", {"start": v(17605, -150) * mm, "end": v(17605, 2178.63) * mm, "construction": true});
            skLineSegment(sketch, "E172.MirrorCS", {"start": v(33930, 1200) * mm, "end": v(32230, 1200) * mm});
            skLineSegment(sketch, "E173.MirrorCS", {"start": v(33930, 3800) * mm, "end": v(32230, 3800) * mm});
            skLineSegment(sketch, "E174.MirrorCS", {"start": v(33930, 3800) * mm, "end": v(33930, 1200) * mm});
            skLineSegment(sketch, "E175.MirrorCS", {"start": v(32230, 3800) * mm, "end": v(32230, 1200) * mm});
            skLineSegment(sketch, "E176.MirrorCS", {"start": v(30930, 3800) * mm, "end": v(29230, 3800) * mm});
            skLineSegment(sketch, "E177.MirrorCS", {"start": v(30930, 1200) * mm, "end": v(29230, 1200) * mm});
            skLineSegment(sketch, "E178.MirrorCS", {"start": v(30930, 3800) * mm, "end": v(30930, 1200) * mm});
            skLineSegment(sketch, "E179.MirrorCS", {"start": v(29230, 3800) * mm, "end": v(29230, 1200) * mm});
            skSolve(sketch);
        }
        {
            var Q0;
            Q0 = qSketchRegion(id + "F12", true);
            extrude(context, id + "F13", {"entities" : qUnion([Q0]), "operationType" : NewBodyOperationType.REMOVE, "oppositeDirection" : true, "depth" : 600 * mm, "offsetDistance" : 25 * mm});
        }
        {
            var Q0;
            Q0=makeQuery(id+"F1.opExtrude","SWEPT_FACE",FACE,{"disambiguationData":[OSD([sQuery(id+"F0.wireOp",EDGE,"E16.12")])]});
            var sketch = newSketch(context, id + "F14", { "sketchPlane" : qUnion([Q0])});
            skLineSegment(sketch, "E180.0", {"start": v(-1280, 3800) * mm, "end": v(-2980, 3800) * mm});
            skLineSegment(sketch, "E180.1", {"start": v(-1280, 1200) * mm, "end": v(-2980, 1200) * mm});
            skLineSegment(sketch, "E180.2", {"start": v(-1280, 3800) * mm, "end": v(-1280, 1200) * mm});
            skLineSegment(sketch, "E180.3", {"start": v(-2980, 3800) * mm, "end": v(-2980, 1200) * mm});
            skLineSegment(sketch, "E180.4", {"start": v(-4280, 3800) * mm, "end": v(-5980, 3800) * mm});
            skLineSegment(sketch, "E180.5", {"start": v(-4280, 1200) * mm, "end": v(-5980, 1200) * mm});
            skLineSegment(sketch, "E180.6", {"start": v(-4280, 3800) * mm, "end": v(-4280, 1200) * mm});
            skLineSegment(sketch, "E180.7", {"start": v(-5980, 3800) * mm, "end": v(-5980, 1200) * mm});
            skLineSegment(sketch, "E180.8", {"start": v(-17605, -150) * mm, "end": v(-17605, 2178.63) * mm});
            skLineSegment(sketch, "E180.9", {"start": v(-33930, 1200) * mm, "end": v(-32230, 1200) * mm});
            skLineSegment(sketch, "E180.10", {"start": v(-33930, 3800) * mm, "end": v(-32230, 3800) * mm});
            skLineSegment(sketch, "E180.11", {"start": v(-33930, 3800) * mm, "end": v(-33930, 1200) * mm});
            skLineSegment(sketch, "E180.12", {"start": v(-32230, 3800) * mm, "end": v(-32230, 1200) * mm});
            skLineSegment(sketch, "E180.13", {"start": v(-30930, 3800) * mm, "end": v(-29230, 3800) * mm});
            skLineSegment(sketch, "E180.14", {"start": v(-30930, 1200) * mm, "end": v(-29230, 1200) * mm});
            skLineSegment(sketch, "E180.15", {"start": v(-30930, 3800) * mm, "end": v(-30930, 1200) * mm});
            skLineSegment(sketch, "E180.16", {"start": v(-29230, 3800) * mm, "end": v(-29230, 1200) * mm});
            skSolve(sketch);
        }
        {
            var Q0;
            Q0 = qSketchRegion(id + "F14", true);
            extrude(context, id + "F15", {"entities" : qUnion([Q0]), "oppositeDirection" : true, "depth" : 100 * mm, "offsetDistance" : 25 * mm});
        }
        {
            var Q0;
            Q0=makeQuery(id+"F15.opExtrude","CAP_FACE",FACE,{"disambiguationData":[OSD([sQuery(id+"F14.wireOp",EDGE,"E180.0"),sQuery(id+"F14.wireOp",EDGE,"E180.1"),sQuery(id+"F14.wireOp",EDGE,"E180.2"),sQuery(id+"F14.wireOp",EDGE,"E180.3")])],"isStart":false});
            var sketch = newSketch(context, id + "F16", { "sketchPlane" : qUnion([Q0])});
            skPoint(sketch, "E181", {"position": v(1280, 1200) * mm});
            skPoint(sketch, "E182", {"position": v(4280, 1200) * mm});
            skPoint(sketch, "E183", {"position": v(29230, 1200) * mm});
            skPoint(sketch, "E184", {"position": v(32230, 1200) * mm});
            skLineSegment(sketch, "E185.0.0", {"start": v(2980, 3800) * mm, "end": v(1280, 3800) * mm});
            skLineSegment(sketch, "E185.0.1", {"start": v(1280, 3800) * mm, "end": v(1280, 1200) * mm});
            skLineSegment(sketch, "E185.0.2", {"start": v(1280, 1200) * mm, "end": v(2980, 1200) * mm});
            skLineSegment(sketch, "E185.0.3", {"start": v(2980, 1200) * mm, "end": v(2980, 3800) * mm});
            skLineSegment(sketch, "E186", {"start": v(2130, 3800) * mm, "end": v(2130, 1200) * mm, "construction": true});
            skLineSegment(sketch, "E187.bottom", {"start": v(1330, 2850) * mm, "end": v(2092.5, 2850) * mm});
            skLineSegment(sketch, "E187.top", {"start": v(1330, 1250) * mm, "end": v(2092.5, 1250) * mm});
            skLineSegment(sketch, "E187.left", {"start": v(1330, 2850) * mm, "end": v(1330, 1250) * mm});
            skLineSegment(sketch, "E187.right", {"start": v(2092.5, 2850) * mm, "end": v(2092.5, 1250) * mm});
            skLineSegment(sketch, "E188.bottom", {"start": v(1330, 2900) * mm, "end": v(2092.5, 2900) * mm});
            skLineSegment(sketch, "E188.top", {"start": v(1330, 3750) * mm, "end": v(2092.5, 3750) * mm});
            skLineSegment(sketch, "E188.left", {"start": v(1330, 2900) * mm, "end": v(1330, 3750) * mm});
            skLineSegment(sketch, "E188.right", {"start": v(2092.5, 2900) * mm, "end": v(2092.5, 3750) * mm});
            skLineSegment(sketch, "E189.MirrorCS", {"start": v(2930, 3750) * mm, "end": v(2167.5, 3750) * mm});
            skLineSegment(sketch, "E190.MirrorCS", {"start": v(2930, 2900) * mm, "end": v(2930, 3750) * mm});
            skLineSegment(sketch, "E191.MirrorCS", {"start": v(2167.5, 2900) * mm, "end": v(2167.5, 3750) * mm});
            skLineSegment(sketch, "E192.MirrorCS", {"start": v(2930, 2900) * mm, "end": v(2167.5, 2900) * mm});
            skLineSegment(sketch, "E193.MirrorCS", {"start": v(2930, 2850) * mm, "end": v(2167.5, 2850) * mm});
            skLineSegment(sketch, "E194.MirrorCS", {"start": v(2167.5, 2850) * mm, "end": v(2167.5, 1250) * mm});
            skLineSegment(sketch, "E195.MirrorCS", {"start": v(2930, 2850) * mm, "end": v(2930, 1250) * mm});
            skLineSegment(sketch, "E196.MirrorCS", {"start": v(2930, 1250) * mm, "end": v(2167.5, 1250) * mm});
            skLineSegment(sketch, "E197.0.0", {"start": v(5980, 3800) * mm, "end": v(4280, 3800) * mm});
            skLineSegment(sketch, "E197.0.1", {"start": v(4280, 3800) * mm, "end": v(4280, 1200) * mm});
            skLineSegment(sketch, "E197.0.2", {"start": v(4280, 1200) * mm, "end": v(5980, 1200) * mm});
            skLineSegment(sketch, "E197.0.3", {"start": v(5980, 1200) * mm, "end": v(5980, 3800) * mm});
            skLineSegment(sketch, "E198", {"start": v(5130, 3800) * mm, "end": v(5130, 1200) * mm, "construction": true});
            skLineSegment(sketch, "E199.bottom", {"start": v(4330, 2850) * mm, "end": v(5092.5, 2850) * mm});
            skLineSegment(sketch, "E199.top", {"start": v(4330, 1250) * mm, "end": v(5092.5, 1250) * mm});
            skLineSegment(sketch, "E199.left", {"start": v(4330, 2850) * mm, "end": v(4330, 1250) * mm});
            skLineSegment(sketch, "E199.right", {"start": v(5092.5, 2850) * mm, "end": v(5092.5, 1250) * mm});
            skLineSegment(sketch, "E200.bottom", {"start": v(4330, 2900) * mm, "end": v(5092.5, 2900) * mm});
            skLineSegment(sketch, "E200.top", {"start": v(4330, 3750) * mm, "end": v(5092.5, 3750) * mm});
            skLineSegment(sketch, "E200.left", {"start": v(4330, 2900) * mm, "end": v(4330, 3750) * mm});
            skLineSegment(sketch, "E200.right", {"start": v(5092.5, 2900) * mm, "end": v(5092.5, 3750) * mm});
            skLineSegment(sketch, "E201.MirrorCS", {"start": v(5930, 3750) * mm, "end": v(5167.5, 3750) * mm});
            skLineSegment(sketch, "E202.MirrorCS", {"start": v(5930, 2900) * mm, "end": v(5930, 3750) * mm});
            skLineSegment(sketch, "E203.MirrorCS", {"start": v(5167.5, 2900) * mm, "end": v(5167.5, 3750) * mm});
            skLineSegment(sketch, "E204.MirrorCS", {"start": v(5930, 2900) * mm, "end": v(5167.5, 2900) * mm});
            skLineSegment(sketch, "E205.MirrorCS", {"start": v(5930, 2850) * mm, "end": v(5167.5, 2850) * mm});
            skLineSegment(sketch, "E206.MirrorCS", {"start": v(5167.5, 2850) * mm, "end": v(5167.5, 1250) * mm});
            skLineSegment(sketch, "E207.MirrorCS", {"start": v(5930, 2850) * mm, "end": v(5930, 1250) * mm});
            skLineSegment(sketch, "E208.MirrorCS", {"start": v(5930, 1250) * mm, "end": v(5167.5, 1250) * mm});
            skLineSegment(sketch, "E209.0.0", {"start": v(30930, 3800) * mm, "end": v(29230, 3800) * mm});
            skLineSegment(sketch, "E209.0.1", {"start": v(29230, 3800) * mm, "end": v(29230, 1200) * mm});
            skLineSegment(sketch, "E209.0.2", {"start": v(29230, 1200) * mm, "end": v(30930, 1200) * mm});
            skLineSegment(sketch, "E209.0.3", {"start": v(30930, 1200) * mm, "end": v(30930, 3800) * mm});
            skLineSegment(sketch, "E210", {"start": v(30080, 3800) * mm, "end": v(30080, 1200) * mm, "construction": true});
            skLineSegment(sketch, "E211.bottom", {"start": v(29280, 2850) * mm, "end": v(30042.5, 2850) * mm});
            skLineSegment(sketch, "E211.top", {"start": v(29280, 1250) * mm, "end": v(30042.5, 1250) * mm});
            skLineSegment(sketch, "E211.left", {"start": v(29280, 2850) * mm, "end": v(29280, 1250) * mm});
            skLineSegment(sketch, "E211.right", {"start": v(30042.5, 2850) * mm, "end": v(30042.5, 1250) * mm});
            skLineSegment(sketch, "E212.bottom", {"start": v(29280, 2900) * mm, "end": v(30042.5, 2900) * mm});
            skLineSegment(sketch, "E212.top", {"start": v(29280, 3750) * mm, "end": v(30042.5, 3750) * mm});
            skLineSegment(sketch, "E212.left", {"start": v(29280, 2900) * mm, "end": v(29280, 3750) * mm});
            skLineSegment(sketch, "E212.right", {"start": v(30042.5, 2900) * mm, "end": v(30042.5, 3750) * mm});
            skLineSegment(sketch, "E213.MirrorCS", {"start": v(30880, 3750) * mm, "end": v(30117.5, 3750) * mm});
            skLineSegment(sketch, "E214.MirrorCS", {"start": v(30880, 2900) * mm, "end": v(30880, 3750) * mm});
            skLineSegment(sketch, "E215.MirrorCS", {"start": v(30117.5, 2900) * mm, "end": v(30117.5, 3750) * mm});
            skLineSegment(sketch, "E216.MirrorCS", {"start": v(30880, 2900) * mm, "end": v(30117.5, 2900) * mm});
            skLineSegment(sketch, "E217.MirrorCS", {"start": v(30880, 2850) * mm, "end": v(30117.5, 2850) * mm});
            skLineSegment(sketch, "E218.MirrorCS", {"start": v(30117.5, 2850) * mm, "end": v(30117.5, 1250) * mm});
            skLineSegment(sketch, "E219.MirrorCS", {"start": v(30880, 2850) * mm, "end": v(30880, 1250) * mm});
            skLineSegment(sketch, "E220.MirrorCS", {"start": v(30880, 1250) * mm, "end": v(30117.5, 1250) * mm});
            skLineSegment(sketch, "E221.0.0", {"start": v(33930, 3800) * mm, "end": v(32230, 3800) * mm});
            skLineSegment(sketch, "E221.0.1", {"start": v(32230, 3800) * mm, "end": v(32230, 1200) * mm});
            skLineSegment(sketch, "E221.0.2", {"start": v(32230, 1200) * mm, "end": v(33930, 1200) * mm});
            skLineSegment(sketch, "E221.0.3", {"start": v(33930, 1200) * mm, "end": v(33930, 3800) * mm});
            skLineSegment(sketch, "E222", {"start": v(33080, 3800) * mm, "end": v(33080, 1200) * mm, "construction": true});
            skLineSegment(sketch, "E223.bottom", {"start": v(32280, 2850) * mm, "end": v(33042.5, 2850) * mm});
            skLineSegment(sketch, "E223.top", {"start": v(32280, 1250) * mm, "end": v(33042.5, 1250) * mm});
            skLineSegment(sketch, "E223.left", {"start": v(32280, 2850) * mm, "end": v(32280, 1250) * mm});
            skLineSegment(sketch, "E223.right", {"start": v(33042.5, 2850) * mm, "end": v(33042.5, 1250) * mm});
            skLineSegment(sketch, "E224.bottom", {"start": v(32280, 2900) * mm, "end": v(33042.5, 2900) * mm});
            skLineSegment(sketch, "E224.top", {"start": v(32280, 3750) * mm, "end": v(33042.5, 3750) * mm});
            skLineSegment(sketch, "E224.left", {"start": v(32280, 2900) * mm, "end": v(32280, 3750) * mm});
            skLineSegment(sketch, "E224.right", {"start": v(33042.5, 2900) * mm, "end": v(33042.5, 3750) * mm});
            skLineSegment(sketch, "E225.MirrorCS", {"start": v(33880, 3750) * mm, "end": v(33117.5, 3750) * mm});
            skLineSegment(sketch, "E226.MirrorCS", {"start": v(33880, 2900) * mm, "end": v(33880, 3750) * mm});
            skLineSegment(sketch, "E227.MirrorCS", {"start": v(33117.5, 2900) * mm, "end": v(33117.5, 3750) * mm});
            skLineSegment(sketch, "E228.MirrorCS", {"start": v(33880, 2900) * mm, "end": v(33117.5, 2900) * mm});
            skLineSegment(sketch, "E229.MirrorCS", {"start": v(33880, 2850) * mm, "end": v(33117.5, 2850) * mm});
            skLineSegment(sketch, "E230.MirrorCS", {"start": v(33117.5, 2850) * mm, "end": v(33117.5, 1250) * mm});
            skLineSegment(sketch, "E231.MirrorCS", {"start": v(33880, 2850) * mm, "end": v(33880, 1250) * mm});
            skLineSegment(sketch, "E232.MirrorCS", {"start": v(33880, 1250) * mm, "end": v(33117.5, 1250) * mm});
            skSolve(sketch);
        }
        {
            var Q0;
            Q0 = qSketchRegion(id + "F16", true);
            extrude(context, id + "F17", {"entities" : qUnion([Q0]), "depth" : 50 * mm, "offsetDistance" : 25 * mm});
        }
        {
            var Q0;
            Q0=makeQuery(id+"F5.boolean.opBoolean","MERGE",FACE,{"derivedFrom":[makeQuery(id+"F1.opExtrude","SWEPT_FACE",FACE,{"disambiguationData":[OSD([sQuery(id+"F0.wireOp",EDGE,"E17.8")])]}),makeQuery(id+"F5.opExtrude","SWEPT_FACE",FACE,{"disambiguationData":[OSD([sQuery(id+"F4.wireOp",EDGE,"E20")])]})]});
            var sketch = newSketch(context, id + "F18", { "sketchPlane" : qUnion([Q0])});
            skLineSegment(sketch, "E233.bottom", {"start": v(-38060, 3800) * mm, "end": v(-36360, 3800) * mm});
            skLineSegment(sketch, "E233.top", {"start": v(-38060, 1100) * mm, "end": v(-36360, 1100) * mm});
            skLineSegment(sketch, "E233.left", {"start": v(-38060, 3800) * mm, "end": v(-38060, 1100) * mm});
            skLineSegment(sketch, "E233.right", {"start": v(-36360, 3800) * mm, "end": v(-36360, 1100) * mm});
            skLineSegment(sketch, "E234.bottom", {"start": v(-35760, 3800) * mm, "end": v(-34060, 3800) * mm});
            skLineSegment(sketch, "E234.top", {"start": v(-35760, 1100) * mm, "end": v(-34060, 1100) * mm});
            skLineSegment(sketch, "E234.left", {"start": v(-35760, 3800) * mm, "end": v(-35760, 1100) * mm});
            skLineSegment(sketch, "E234.right", {"start": v(-34060, 3800) * mm, "end": v(-34060, 1100) * mm});
            skLineSegment(sketch, "E235.bottom", {"start": v(-32160, 3800) * mm, "end": v(-30460, 3800) * mm});
            skLineSegment(sketch, "E235.top", {"start": v(-32160, 1100) * mm, "end": v(-30460, 1100) * mm});
            skLineSegment(sketch, "E235.left", {"start": v(-32160, 3800) * mm, "end": v(-32160, 1100) * mm});
            skLineSegment(sketch, "E235.right", {"start": v(-30460, 3800) * mm, "end": v(-30460, 1100) * mm});
            skLineSegment(sketch, "E236.bottom", {"start": v(-28060, 3800) * mm, "end": v(-26360, 3800) * mm});
            skLineSegment(sketch, "E236.top", {"start": v(-28060, 1100) * mm, "end": v(-26360, 1100) * mm});
            skLineSegment(sketch, "E236.left", {"start": v(-28060, 3800) * mm, "end": v(-28060, 1100) * mm});
            skLineSegment(sketch, "E236.right", {"start": v(-26360, 3800) * mm, "end": v(-26360, 1100) * mm});
            skLineSegment(sketch, "E237.bottom", {"start": v(-25260, 3800) * mm, "end": v(-23560, 3800) * mm});
            skLineSegment(sketch, "E237.top", {"start": v(-25260, 1100) * mm, "end": v(-23560, 1100) * mm});
            skLineSegment(sketch, "E237.left", {"start": v(-25260, 3800) * mm, "end": v(-25260, 1100) * mm});
            skLineSegment(sketch, "E237.right", {"start": v(-23560, 3800) * mm, "end": v(-23560, 1100) * mm});
            skLineSegment(sketch, "E238.bottom", {"start": v(-22460, 3800) * mm, "end": v(-20760, 3800) * mm});
            skLineSegment(sketch, "E238.top", {"start": v(-22460, 1100) * mm, "end": v(-20760, 1100) * mm});
            skLineSegment(sketch, "E238.left", {"start": v(-22460, 3800) * mm, "end": v(-22460, 1100) * mm});
            skLineSegment(sketch, "E238.right", {"start": v(-20760, 3800) * mm, "end": v(-20760, 1100) * mm});
            skLineSegment(sketch, "E239.1.0.0", {"start": v(-13060, 3800) * mm, "end": v(-11360, 3800) * mm});
            skLineSegment(sketch, "E239.1.0.1", {"start": v(-11360, 3800) * mm, "end": v(-11360, 1100) * mm});
            skLineSegment(sketch, "E239.1.0.2", {"start": v(-15860, 3800) * mm, "end": v(-15860, 1100) * mm});
            skLineSegment(sketch, "E239.1.0.3", {"start": v(-15860, 3800) * mm, "end": v(-14160, 3800) * mm});
            skLineSegment(sketch, "E239.1.0.4", {"start": v(-18660, 3800) * mm, "end": v(-16960, 3800) * mm});
            skLineSegment(sketch, "E239.1.0.5", {"start": v(-18660, 3800) * mm, "end": v(-18660, 1100) * mm});
            skLineSegment(sketch, "E239.1.0.6", {"start": v(-13060, 3800) * mm, "end": v(-13060, 1100) * mm});
            skLineSegment(sketch, "E239.1.0.7", {"start": v(-18660, 1100) * mm, "end": v(-16960, 1100) * mm});
            skLineSegment(sketch, "E239.1.0.8", {"start": v(-15860, 1100) * mm, "end": v(-14160, 1100) * mm});
            skLineSegment(sketch, "E239.1.0.9", {"start": v(-14160, 3800) * mm, "end": v(-14160, 1100) * mm});
            skLineSegment(sketch, "E239.1.0.10", {"start": v(-13060, 1100) * mm, "end": v(-11360, 1100) * mm});
            skLineSegment(sketch, "E239.1.0.11", {"start": v(-16960, 3800) * mm, "end": v(-16960, 1100) * mm});
            skLineSegment(sketch, "E239.2.0.0", {"start": v(-3660, 3800) * mm, "end": v(-1960, 3800) * mm});
            skLineSegment(sketch, "E239.2.0.1", {"start": v(-1960, 3800) * mm, "end": v(-1960, 1100) * mm});
            skLineSegment(sketch, "E239.2.0.2", {"start": v(-6460, 3800) * mm, "end": v(-6460, 1100) * mm});
            skLineSegment(sketch, "E239.2.0.3", {"start": v(-6460, 3800) * mm, "end": v(-4760, 3800) * mm});
            skLineSegment(sketch, "E239.2.0.4", {"start": v(-9260, 3800) * mm, "end": v(-7560, 3800) * mm});
            skLineSegment(sketch, "E239.2.0.5", {"start": v(-9260, 3800) * mm, "end": v(-9260, 1100) * mm});
            skLineSegment(sketch, "E239.2.0.6", {"start": v(-3660, 3800) * mm, "end": v(-3660, 1100) * mm});
            skLineSegment(sketch, "E239.2.0.7", {"start": v(-9260, 1100) * mm, "end": v(-7560, 1100) * mm});
            skLineSegment(sketch, "E239.2.0.8", {"start": v(-6460, 1100) * mm, "end": v(-4760, 1100) * mm});
            skLineSegment(sketch, "E239.2.0.9", {"start": v(-4760, 3800) * mm, "end": v(-4760, 1100) * mm});
            skLineSegment(sketch, "E239.2.0.10", {"start": v(-3660, 1100) * mm, "end": v(-1960, 1100) * mm});
            skLineSegment(sketch, "E239.2.0.11", {"start": v(-7560, 3800) * mm, "end": v(-7560, 1100) * mm});
            skLineSegment(sketch, "E239.direction1", {"start": v(-28060, 1100) * mm, "end": v(-18660, 1100) * mm, "construction": true});
            skSolve(sketch);
        }
        {
            var Q0;
            Q0=qSketchRegion(id+"F18",true);
            extrude(context, id + "F19", {"entities" : qUnion([Q0]), "operationType" : NewBodyOperationType.REMOVE, "oppositeDirection" : true, "depth" : 650 * mm, "offsetDistance" : 25 * mm});
        }
        {
            var Q0;
            Q0=makeQuery(id+"F5.boolean.opBoolean","MERGE",FACE,{"derivedFrom":[makeQuery(id+"F3.boolean.opBoolean","COPY",FACE,{"derivedFrom":makeQuery(id+"F3.opExtrude","SWEPT_FACE",FACE,{"disambiguationData":[OSD([sQuery(id+"F2.wireOp",EDGE,"E19.6")])]})}),makeQuery(id+"F5.opExtrude","SWEPT_FACE",FACE,{"disambiguationData":[OSD([sQuery(id+"F4.wireOp",EDGE,"E20")])]})]});
            var sketch = newSketch(context, id + "F20", { "sketchPlane" : qUnion([Q0])});
            skLineSegment(sketch, "E240.bottom", {"start": v(-31060, 3800) * mm, "end": v(-30460, 3800) * mm});
            skLineSegment(sketch, "E240.top", {"start": v(-31060, 1100) * mm, "end": v(-30460, 1100) * mm});
            skLineSegment(sketch, "E240.left", {"start": v(-31060, 3800) * mm, "end": v(-31060, 1100) * mm});
            skLineSegment(sketch, "E240.right", {"start": v(-30460, 3800) * mm, "end": v(-30460, 1100) * mm});
            skSolve(sketch);
        }
        {
            var Q0;
            Q0 = qSketchRegion(id + "F20", true);
            var Q1;
            Q1=makeQuery(id+"F1.opExtrude","SWEPT_FACE",FACE,{"disambiguationData":[OSD([sQuery(id+"F0.wireOp",EDGE,"E16.13")])]});
            extrude(context, id + "F21", {"entities" : qUnion([Q0]), "operationType" : NewBodyOperationType.ADD, "endBound" : BoundingType.UP_TO_SURFACE, "oppositeDirection" : true, "depth" : 25 * mm, "endBoundEntityFace" : qUnion([Q1]), "offsetDistance" : 25 * mm});
        }
        {
            var Q0;
            Q0=makeQuery(id+"F5.boolean.opBoolean","MERGE",FACE,{"derivedFrom":[makeQuery(id+"F3.boolean.opBoolean","COPY",FACE,{"derivedFrom":makeQuery(id+"F3.opExtrude","SWEPT_FACE",FACE,{"disambiguationData":[OSD([sQuery(id+"F2.wireOp",EDGE,"E19.13")])]})}),makeQuery(id+"F5.opExtrude","SWEPT_FACE",FACE,{"disambiguationData":[OSD([sQuery(id+"F4.wireOp",EDGE,"E30.0")])]})]});
            var sketch = newSketch(context, id + "F22", { "sketchPlane" : qUnion([Q0])});
            skLineSegment(sketch, "E241.12", {"start": v(28060, 3800) * mm, "end": v(26360, 3800) * mm});
            skLineSegment(sketch, "E241.13", {"start": v(28060, 1100) * mm, "end": v(26360, 1100) * mm});
            skLineSegment(sketch, "E241.14", {"start": v(28060, 3800) * mm, "end": v(28060, 1100) * mm});
            skLineSegment(sketch, "E241.15", {"start": v(26360, 3800) * mm, "end": v(26360, 1100) * mm});
            skLineSegment(sketch, "E241.16", {"start": v(25260, 3800) * mm, "end": v(23560, 3800) * mm});
            skLineSegment(sketch, "E241.17", {"start": v(25260, 1100) * mm, "end": v(23560, 1100) * mm});
            skLineSegment(sketch, "E241.18", {"start": v(25260, 3800) * mm, "end": v(25260, 1100) * mm});
            skLineSegment(sketch, "E241.19", {"start": v(23560, 3800) * mm, "end": v(23560, 1100) * mm});
            skLineSegment(sketch, "E241.20", {"start": v(22460, 3800) * mm, "end": v(20760, 3800) * mm});
            skLineSegment(sketch, "E241.21", {"start": v(22460, 1100) * mm, "end": v(20760, 1100) * mm});
            skLineSegment(sketch, "E241.22", {"start": v(22460, 3800) * mm, "end": v(22460, 1100) * mm});
            skLineSegment(sketch, "E241.23", {"start": v(20760, 3800) * mm, "end": v(20760, 1100) * mm});
            skLineSegment(sketch, "E241.24", {"start": v(13060, 3800) * mm, "end": v(11360, 3800) * mm});
            skLineSegment(sketch, "E241.25", {"start": v(11360, 3800) * mm, "end": v(11360, 1100) * mm});
            skLineSegment(sketch, "E241.26", {"start": v(15860, 3800) * mm, "end": v(15860, 1100) * mm});
            skLineSegment(sketch, "E241.27", {"start": v(15860, 3800) * mm, "end": v(14160, 3800) * mm});
            skLineSegment(sketch, "E241.28", {"start": v(18660, 3800) * mm, "end": v(16960, 3800) * mm});
            skLineSegment(sketch, "E241.29", {"start": v(18660, 3800) * mm, "end": v(18660, 1100) * mm});
            skLineSegment(sketch, "E241.30", {"start": v(13060, 3800) * mm, "end": v(13060, 1100) * mm});
            skLineSegment(sketch, "E241.31", {"start": v(18660, 1100) * mm, "end": v(16960, 1100) * mm});
            skLineSegment(sketch, "E241.32", {"start": v(15860, 1100) * mm, "end": v(14160, 1100) * mm});
            skLineSegment(sketch, "E241.33", {"start": v(14160, 3800) * mm, "end": v(14160, 1100) * mm});
            skLineSegment(sketch, "E241.34", {"start": v(13060, 1100) * mm, "end": v(11360, 1100) * mm});
            skLineSegment(sketch, "E241.35", {"start": v(16960, 3800) * mm, "end": v(16960, 1100) * mm});
            skLineSegment(sketch, "E241.36", {"start": v(3660, 3800) * mm, "end": v(1960, 3800) * mm});
            skLineSegment(sketch, "E241.37", {"start": v(1960, 3800) * mm, "end": v(1960, 1100) * mm});
            skLineSegment(sketch, "E241.38", {"start": v(6460, 3800) * mm, "end": v(6460, 1100) * mm});
            skLineSegment(sketch, "E241.39", {"start": v(6460, 3800) * mm, "end": v(4760, 3800) * mm});
            skLineSegment(sketch, "E241.40", {"start": v(9260, 3800) * mm, "end": v(7560, 3800) * mm});
            skLineSegment(sketch, "E241.41", {"start": v(9260, 3800) * mm, "end": v(9260, 1100) * mm});
            skLineSegment(sketch, "E241.42", {"start": v(3660, 3800) * mm, "end": v(3660, 1100) * mm});
            skLineSegment(sketch, "E241.43", {"start": v(9260, 1100) * mm, "end": v(7560, 1100) * mm});
            skLineSegment(sketch, "E241.44", {"start": v(6460, 1100) * mm, "end": v(4760, 1100) * mm});
            skLineSegment(sketch, "E241.45", {"start": v(4760, 3800) * mm, "end": v(4760, 1100) * mm});
            skLineSegment(sketch, "E241.46", {"start": v(3660, 1100) * mm, "end": v(1960, 1100) * mm});
            skLineSegment(sketch, "E241.47", {"start": v(7560, 3800) * mm, "end": v(7560, 1100) * mm});
            skLineSegment(sketch, "E241.48", {"start": v(28060, 1100) * mm, "end": v(18660, 1100) * mm});
            skLineSegment(sketch, "E242.bottom", {"start": v(29660, 3800) * mm, "end": v(31360, 3800) * mm});
            skLineSegment(sketch, "E242.top", {"start": v(29660, 1100) * mm, "end": v(31360, 1100) * mm});
            skLineSegment(sketch, "E242.left", {"start": v(29660, 3800) * mm, "end": v(29660, 1100) * mm});
            skLineSegment(sketch, "E242.right", {"start": v(31360, 3800) * mm, "end": v(31360, 1100) * mm});
            skLineSegment(sketch, "E243.bottom", {"start": v(32460, 3800) * mm, "end": v(34160, 3800) * mm});
            skLineSegment(sketch, "E243.top", {"start": v(32460, 1100) * mm, "end": v(34160, 1100) * mm});
            skLineSegment(sketch, "E243.left", {"start": v(32460, 3800) * mm, "end": v(32460, 1100) * mm});
            skLineSegment(sketch, "E243.right", {"start": v(34160, 3800) * mm, "end": v(34160, 1100) * mm});
            skLineSegment(sketch, "E244.bottom", {"start": v(35260, 3800) * mm, "end": v(36960, 3800) * mm});
            skLineSegment(sketch, "E244.top", {"start": v(35260, 1100) * mm, "end": v(36960, 1100) * mm});
            skLineSegment(sketch, "E244.left", {"start": v(35260, 3800) * mm, "end": v(35260, 1100) * mm});
            skLineSegment(sketch, "E244.right", {"start": v(36960, 3800) * mm, "end": v(36960, 1100) * mm});
            skSolve(sketch);
        }
        {
            var Q0;
            Q0=qSketchRegion(id+"F22",true);
            extrude(context, id + "F23", {"entities" : qUnion([Q0]), "operationType" : NewBodyOperationType.REMOVE, "oppositeDirection" : true, "depth" : 600 * mm, "offsetDistance" : 25 * mm});
        }
        {
            var Q0;
            {var subQ18=sQuery(id+"F0.wireOp",EDGE,"E16.13");var subQ28=sQuery(id+"F0.wireOp",EDGE,"E16.3");Q0=makeQuery(id+"FMK1u3Q9oKXTw7Y_1.boolean.opBoolean","SPLIT",FACE,{"disambiguationData":[TD([makeQuery(id+"F1.opExtrude","SWEPT_FACE",FACE,{"disambiguationData":[OSD([subQ28])]})])],"derivedFrom":makeQuery(id+"F1.opExtrude","SWEPT_FACE",FACE,{"disambiguationData":[OSD([subQ18])]})});}
            var sketch = newSketch(context, id + "F24", { "sketchPlane" : qUnion([Q0])});
            skLineSegment(sketch, "E245.0", {"start": v(38060, 3800) * mm, "end": v(36360, 3800) * mm});
            skLineSegment(sketch, "E245.1", {"start": v(38060, 1100) * mm, "end": v(36360, 1100) * mm});
            skLineSegment(sketch, "E245.2", {"start": v(38060, 3800) * mm, "end": v(38060, 1100) * mm});
            skLineSegment(sketch, "E245.3", {"start": v(36360, 3800) * mm, "end": v(36360, 1100) * mm});
            skLineSegment(sketch, "E245.4", {"start": v(35760, 3800) * mm, "end": v(34060, 3800) * mm});
            skLineSegment(sketch, "E245.5", {"start": v(35760, 1100) * mm, "end": v(34060, 1100) * mm});
            skLineSegment(sketch, "E245.6", {"start": v(35760, 3800) * mm, "end": v(35760, 1100) * mm});
            skLineSegment(sketch, "E245.7", {"start": v(34060, 3800) * mm, "end": v(34060, 1100) * mm});
            skLineSegment(sketch, "E245.12", {"start": v(28060, 3800) * mm, "end": v(26360, 3800) * mm});
            skLineSegment(sketch, "E245.13", {"start": v(28060, 1100) * mm, "end": v(26360, 1100) * mm});
            skLineSegment(sketch, "E245.14", {"start": v(28060, 3800) * mm, "end": v(28060, 1100) * mm});
            skLineSegment(sketch, "E245.15", {"start": v(26360, 3800) * mm, "end": v(26360, 1100) * mm});
            skLineSegment(sketch, "E245.16", {"start": v(25260, 3800) * mm, "end": v(23560, 3800) * mm});
            skLineSegment(sketch, "E245.17", {"start": v(25260, 1100) * mm, "end": v(23560, 1100) * mm});
            skLineSegment(sketch, "E245.18", {"start": v(25260, 3800) * mm, "end": v(25260, 1100) * mm});
            skLineSegment(sketch, "E245.19", {"start": v(23560, 3800) * mm, "end": v(23560, 1100) * mm});
            skLineSegment(sketch, "E245.20", {"start": v(22460, 3800) * mm, "end": v(20760, 3800) * mm});
            skLineSegment(sketch, "E245.21", {"start": v(22460, 1100) * mm, "end": v(20760, 1100) * mm});
            skLineSegment(sketch, "E245.22", {"start": v(22460, 3800) * mm, "end": v(22460, 1100) * mm});
            skLineSegment(sketch, "E245.23", {"start": v(20760, 3800) * mm, "end": v(20760, 1100) * mm});
            skLineSegment(sketch, "E245.24", {"start": v(13060, 3800) * mm, "end": v(11360, 3800) * mm});
            skLineSegment(sketch, "E245.25", {"start": v(11360, 3800) * mm, "end": v(11360, 1100) * mm});
            skLineSegment(sketch, "E245.26", {"start": v(15860, 3800) * mm, "end": v(15860, 1100) * mm});
            skLineSegment(sketch, "E245.27", {"start": v(15860, 3800) * mm, "end": v(14160, 3800) * mm});
            skLineSegment(sketch, "E245.28", {"start": v(18660, 3800) * mm, "end": v(16960, 3800) * mm});
            skLineSegment(sketch, "E245.29", {"start": v(18660, 3800) * mm, "end": v(18660, 1100) * mm});
            skLineSegment(sketch, "E245.30", {"start": v(13060, 3800) * mm, "end": v(13060, 1100) * mm});
            skLineSegment(sketch, "E245.31", {"start": v(18660, 1100) * mm, "end": v(16960, 1100) * mm});
            skLineSegment(sketch, "E245.32", {"start": v(15860, 1100) * mm, "end": v(14160, 1100) * mm});
            skLineSegment(sketch, "E245.33", {"start": v(14160, 3800) * mm, "end": v(14160, 1100) * mm});
            skLineSegment(sketch, "E245.34", {"start": v(13060, 1100) * mm, "end": v(11360, 1100) * mm});
            skLineSegment(sketch, "E245.35", {"start": v(16960, 3800) * mm, "end": v(16960, 1100) * mm});
            skLineSegment(sketch, "E245.36", {"start": v(3660, 3800) * mm, "end": v(1960, 3800) * mm});
            skLineSegment(sketch, "E245.37", {"start": v(1960, 3800) * mm, "end": v(1960, 1100) * mm});
            skLineSegment(sketch, "E245.38", {"start": v(6460, 3800) * mm, "end": v(6460, 1100) * mm});
            skLineSegment(sketch, "E245.39", {"start": v(6460, 3800) * mm, "end": v(4760, 3800) * mm});
            skLineSegment(sketch, "E245.40", {"start": v(9260, 3800) * mm, "end": v(7560, 3800) * mm});
            skLineSegment(sketch, "E245.41", {"start": v(9260, 3800) * mm, "end": v(9260, 1100) * mm});
            skLineSegment(sketch, "E245.42", {"start": v(3660, 3800) * mm, "end": v(3660, 1100) * mm});
            skLineSegment(sketch, "E245.43", {"start": v(9260, 1100) * mm, "end": v(7560, 1100) * mm});
            skLineSegment(sketch, "E245.44", {"start": v(6460, 1100) * mm, "end": v(4760, 1100) * mm});
            skLineSegment(sketch, "E245.45", {"start": v(4760, 3800) * mm, "end": v(4760, 1100) * mm});
            skLineSegment(sketch, "E245.46", {"start": v(3660, 1100) * mm, "end": v(1960, 1100) * mm});
            skLineSegment(sketch, "E245.47", {"start": v(7560, 3800) * mm, "end": v(7560, 1100) * mm});
            skLineSegment(sketch, "E245.48", {"start": v(28060, 1100) * mm, "end": v(18660, 1100) * mm});
            skLineSegment(sketch, "E246.0", {"start": v(31060, 3800) * mm, "end": v(32160, 3800) * mm});
            skLineSegment(sketch, "E247.0", {"start": v(31060, 3800) * mm, "end": v(31060, 1100) * mm});
            skLineSegment(sketch, "E248.0", {"start": v(31060, 1100) * mm, "end": v(32160, 1100) * mm});
            skLineSegment(sketch, "E249.0", {"start": v(32160, 1100) * mm, "end": v(32160, 3800) * mm});
            skSolve(sketch);
        }
        {
            var Q0;
            Q0=qSketchRegion(id+"F24",true);
            extrude(context, id + "F25", {"entities" : qUnion([Q0]), "oppositeDirection" : true, "depth" : 100 * mm, "offsetDistance" : 25 * mm});
        }
        {
            var Q0;
            Q0=makeQuery(id+"F1.opExtrude","SWEPT_FACE",FACE,{"disambiguationData":[OSD([sQuery(id+"F0.wireOp",EDGE,"E16.0")])]});
            var sketch = newSketch(context, id + "F26", { "sketchPlane" : qUnion([Q0])});
            skLineSegment(sketch, "E250.0", {"start": v(-28060, 3800) * mm, "end": v(-26360, 3800) * mm});
            skLineSegment(sketch, "E250.1", {"start": v(-28060, 1100) * mm, "end": v(-26360, 1100) * mm});
            skLineSegment(sketch, "E250.2", {"start": v(-28060, 3800) * mm, "end": v(-28060, 1100) * mm});
            skLineSegment(sketch, "E250.3", {"start": v(-26360, 3800) * mm, "end": v(-26360, 1100) * mm});
            skLineSegment(sketch, "E250.4", {"start": v(-25260, 3800) * mm, "end": v(-23560, 3800) * mm});
            skLineSegment(sketch, "E250.5", {"start": v(-25260, 1100) * mm, "end": v(-23560, 1100) * mm});
            skLineSegment(sketch, "E250.6", {"start": v(-25260, 3800) * mm, "end": v(-25260, 1100) * mm});
            skLineSegment(sketch, "E250.7", {"start": v(-23560, 3800) * mm, "end": v(-23560, 1100) * mm});
            skLineSegment(sketch, "E250.8", {"start": v(-22460, 3800) * mm, "end": v(-20760, 3800) * mm});
            skLineSegment(sketch, "E250.9", {"start": v(-22460, 1100) * mm, "end": v(-20760, 1100) * mm});
            skLineSegment(sketch, "E250.10", {"start": v(-22460, 3800) * mm, "end": v(-22460, 1100) * mm});
            skLineSegment(sketch, "E250.11", {"start": v(-20760, 3800) * mm, "end": v(-20760, 1100) * mm});
            skLineSegment(sketch, "E250.12", {"start": v(-13060, 3800) * mm, "end": v(-11360, 3800) * mm});
            skLineSegment(sketch, "E250.13", {"start": v(-11360, 3800) * mm, "end": v(-11360, 1100) * mm});
            skLineSegment(sketch, "E250.14", {"start": v(-15860, 3800) * mm, "end": v(-15860, 1100) * mm});
            skLineSegment(sketch, "E250.15", {"start": v(-15860, 3800) * mm, "end": v(-14160, 3800) * mm});
            skLineSegment(sketch, "E250.16", {"start": v(-18660, 3800) * mm, "end": v(-16960, 3800) * mm});
            skLineSegment(sketch, "E250.17", {"start": v(-18660, 3800) * mm, "end": v(-18660, 1100) * mm});
            skLineSegment(sketch, "E250.18", {"start": v(-13060, 3800) * mm, "end": v(-13060, 1100) * mm});
            skLineSegment(sketch, "E250.19", {"start": v(-18660, 1100) * mm, "end": v(-16960, 1100) * mm});
            skLineSegment(sketch, "E250.20", {"start": v(-15860, 1100) * mm, "end": v(-14160, 1100) * mm});
            skLineSegment(sketch, "E250.21", {"start": v(-14160, 3800) * mm, "end": v(-14160, 1100) * mm});
            skLineSegment(sketch, "E250.22", {"start": v(-13060, 1100) * mm, "end": v(-11360, 1100) * mm});
            skLineSegment(sketch, "E250.23", {"start": v(-16960, 3800) * mm, "end": v(-16960, 1100) * mm});
            skLineSegment(sketch, "E250.24", {"start": v(-3660, 3800) * mm, "end": v(-1960, 3800) * mm});
            skLineSegment(sketch, "E250.25", {"start": v(-1960, 3800) * mm, "end": v(-1960, 1100) * mm});
            skLineSegment(sketch, "E250.26", {"start": v(-6460, 3800) * mm, "end": v(-6460, 1100) * mm});
            skLineSegment(sketch, "E250.27", {"start": v(-6460, 3800) * mm, "end": v(-4760, 3800) * mm});
            skLineSegment(sketch, "E250.28", {"start": v(-9260, 3800) * mm, "end": v(-7560, 3800) * mm});
            skLineSegment(sketch, "E250.29", {"start": v(-9260, 3800) * mm, "end": v(-9260, 1100) * mm});
            skLineSegment(sketch, "E250.30", {"start": v(-3660, 3800) * mm, "end": v(-3660, 1100) * mm});
            skLineSegment(sketch, "E250.31", {"start": v(-9260, 1100) * mm, "end": v(-7560, 1100) * mm});
            skLineSegment(sketch, "E250.32", {"start": v(-6460, 1100) * mm, "end": v(-4760, 1100) * mm});
            skLineSegment(sketch, "E250.33", {"start": v(-4760, 3800) * mm, "end": v(-4760, 1100) * mm});
            skLineSegment(sketch, "E250.34", {"start": v(-3660, 1100) * mm, "end": v(-1960, 1100) * mm});
            skLineSegment(sketch, "E250.35", {"start": v(-7560, 3800) * mm, "end": v(-7560, 1100) * mm});
            skLineSegment(sketch, "E250.36", {"start": v(-28060, 1100) * mm, "end": v(-18660, 1100) * mm});
            skLineSegment(sketch, "E250.37", {"start": v(-29660, 3800) * mm, "end": v(-31360, 3800) * mm});
            skLineSegment(sketch, "E250.38", {"start": v(-29660, 1100) * mm, "end": v(-31360, 1100) * mm});
            skLineSegment(sketch, "E250.39", {"start": v(-29660, 3800) * mm, "end": v(-29660, 1100) * mm});
            skLineSegment(sketch, "E250.40", {"start": v(-31360, 3800) * mm, "end": v(-31360, 1100) * mm});
            skLineSegment(sketch, "E250.41", {"start": v(-32460, 3800) * mm, "end": v(-34160, 3800) * mm});
            skLineSegment(sketch, "E250.42", {"start": v(-32460, 1100) * mm, "end": v(-34160, 1100) * mm});
            skLineSegment(sketch, "E250.43", {"start": v(-32460, 3800) * mm, "end": v(-32460, 1100) * mm});
            skLineSegment(sketch, "E250.44", {"start": v(-34160, 3800) * mm, "end": v(-34160, 1100) * mm});
            skLineSegment(sketch, "E250.45", {"start": v(-35260, 3800) * mm, "end": v(-36960, 3800) * mm});
            skLineSegment(sketch, "E250.46", {"start": v(-35260, 1100) * mm, "end": v(-36960, 1100) * mm});
            skLineSegment(sketch, "E250.47", {"start": v(-35260, 3800) * mm, "end": v(-35260, 1100) * mm});
            skLineSegment(sketch, "E250.48", {"start": v(-36960, 3800) * mm, "end": v(-36960, 1100) * mm});
            skSolve(sketch);
        }
        {
            var Q0;
            Q0=qSketchRegion(id+"F26",true);
            extrude(context, id + "F27", {"entities" : qUnion([Q0]), "oppositeDirection" : true, "depth" : 100 * mm, "offsetDistance" : 25 * mm});
        }
        {
            var Q0;
            Q0=makeQuery(id+"F25.opExtrude","CAP_FACE",FACE,{"disambiguationData":[OSD([sQuery(id+"F24.wireOp",EDGE,"E245.0"),sQuery(id+"F24.wireOp",EDGE,"E245.1"),sQuery(id+"F24.wireOp",EDGE,"E245.2"),sQuery(id+"F24.wireOp",EDGE,"E245.3")])],"isStart":false});
            var sketch = newSketch(context, id + "F28", { "sketchPlane" : qUnion([Q0])});
            skLineSegment(sketch, "E251.0.0", {"start": v(-38060, 1100) * mm, "end": v(-36360, 1100) * mm});
            skLineSegment(sketch, "E251.0.1", {"start": v(-36360, 1100) * mm, "end": v(-36360, 3800) * mm});
            skLineSegment(sketch, "E251.0.2", {"start": v(-36360, 3800) * mm, "end": v(-38060, 3800) * mm});
            skLineSegment(sketch, "E251.0.3", {"start": v(-38060, 3800) * mm, "end": v(-38060, 1100) * mm});
            skLineSegment(sketch, "E252", {"start": v(-37210, 1100) * mm, "end": v(-37210, 3800) * mm, "construction": true});
            skLineSegment(sketch, "E253.bottom", {"start": v(-38010, 2750) * mm, "end": v(-37247.5, 2750) * mm});
            skLineSegment(sketch, "E253.top", {"start": v(-38010, 1150) * mm, "end": v(-37247.5, 1150) * mm});
            skLineSegment(sketch, "E253.left", {"start": v(-38010, 2750) * mm, "end": v(-38010, 1150) * mm});
            skLineSegment(sketch, "E253.right", {"start": v(-37247.5, 2750) * mm, "end": v(-37247.5, 1150) * mm});
            skLineSegment(sketch, "E254.bottom", {"start": v(-38010, 2800) * mm, "end": v(-37247.5, 2800) * mm});
            skLineSegment(sketch, "E254.top", {"start": v(-38010, 3750) * mm, "end": v(-37247.5, 3750) * mm});
            skLineSegment(sketch, "E254.left", {"start": v(-38010, 2800) * mm, "end": v(-38010, 3750) * mm});
            skLineSegment(sketch, "E254.right", {"start": v(-37247.5, 2800) * mm, "end": v(-37247.5, 3750) * mm});
            skLineSegment(sketch, "E255.MirrorCS", {"start": v(-36410, 3750) * mm, "end": v(-37172.5, 3750) * mm});
            skLineSegment(sketch, "E256.MirrorCS", {"start": v(-37172.5, 2800) * mm, "end": v(-37172.5, 3750) * mm});
            skLineSegment(sketch, "E257.MirrorCS", {"start": v(-36410, 2800) * mm, "end": v(-37172.5, 2800) * mm});
            skLineSegment(sketch, "E258.MirrorCS", {"start": v(-36410, 2800) * mm, "end": v(-36410, 3750) * mm});
            skLineSegment(sketch, "E259.MirrorCS", {"start": v(-36410, 2750) * mm, "end": v(-37172.5, 2750) * mm});
            skLineSegment(sketch, "E260.MirrorCS", {"start": v(-37172.5, 2750) * mm, "end": v(-37172.5, 1150) * mm});
            skLineSegment(sketch, "E261.MirrorCS", {"start": v(-36410, 1150) * mm, "end": v(-37172.5, 1150) * mm});
            skLineSegment(sketch, "E262.MirrorCS", {"start": v(-36410, 2750) * mm, "end": v(-36410, 1150) * mm});
            skPoint(sketch, "E263", {"position": v(-35760, 1100) * mm});
            skPoint(sketch, "E264", {"position": v(-32160, 1100) * mm});
            skLineSegment(sketch, "E265.0.0", {"start": v(-35760, 1100) * mm, "end": v(-34060, 1100) * mm});
            skLineSegment(sketch, "E265.0.1", {"start": v(-34060, 1100) * mm, "end": v(-34060, 3800) * mm});
            skLineSegment(sketch, "E265.0.2", {"start": v(-34060, 3800) * mm, "end": v(-35760, 3800) * mm});
            skLineSegment(sketch, "E265.0.3", {"start": v(-35760, 3800) * mm, "end": v(-35760, 1100) * mm});
            skLineSegment(sketch, "E266", {"start": v(-34910, 1100) * mm, "end": v(-34910, 3700) * mm, "construction": true});
            skLineSegment(sketch, "E267.bottom", {"start": v(-35710, 2750) * mm, "end": v(-34947.5, 2750) * mm});
            skLineSegment(sketch, "E267.top", {"start": v(-35710, 1150) * mm, "end": v(-34947.5, 1150) * mm});
            skLineSegment(sketch, "E267.left", {"start": v(-35710, 2750) * mm, "end": v(-35710, 1150) * mm});
            skLineSegment(sketch, "E267.right", {"start": v(-34947.5, 2750) * mm, "end": v(-34947.5, 1150) * mm});
            skLineSegment(sketch, "E268.bottom", {"start": v(-35710, 2800) * mm, "end": v(-34947.5, 2800) * mm});
            skLineSegment(sketch, "E268.top", {"start": v(-35710, 3750) * mm, "end": v(-34947.5, 3750) * mm});
            skLineSegment(sketch, "E268.left", {"start": v(-35710, 2800) * mm, "end": v(-35710, 3750) * mm});
            skLineSegment(sketch, "E268.right", {"start": v(-34947.5, 2800) * mm, "end": v(-34947.5, 3750) * mm});
            skLineSegment(sketch, "E269.MirrorCS", {"start": v(-34110, 3750) * mm, "end": v(-34872.5, 3750) * mm});
            skLineSegment(sketch, "E270.MirrorCS", {"start": v(-34872.5, 2800) * mm, "end": v(-34872.5, 3750) * mm});
            skLineSegment(sketch, "E271.MirrorCS", {"start": v(-34110, 2800) * mm, "end": v(-34872.5, 2800) * mm});
            skLineSegment(sketch, "E272.MirrorCS", {"start": v(-34110, 2800) * mm, "end": v(-34110, 3750) * mm});
            skLineSegment(sketch, "E273.MirrorCS", {"start": v(-34110, 2750) * mm, "end": v(-34872.5, 2750) * mm});
            skLineSegment(sketch, "E274.MirrorCS", {"start": v(-34872.5, 2750) * mm, "end": v(-34872.5, 1150) * mm});
            skLineSegment(sketch, "E275.MirrorCS", {"start": v(-34110, 1150) * mm, "end": v(-34872.5, 1150) * mm});
            skLineSegment(sketch, "E276.MirrorCS", {"start": v(-34110, 2750) * mm, "end": v(-34110, 1150) * mm});
            skLineSegment(sketch, "E277.0.0", {"start": v(-32160, 1100) * mm, "end": v(-31060, 1100) * mm});
            skLineSegment(sketch, "E277.0.2", {"start": v(-31060, 3800) * mm, "end": v(-32160, 3800) * mm});
            skLineSegment(sketch, "E277.0.3", {"start": v(-32160, 3800) * mm, "end": v(-32160, 1100) * mm});
            skLineSegment(sketch, "E278.bottom", {"start": v(-32110, 2750) * mm, "end": v(-31110, 2750) * mm});
            skLineSegment(sketch, "E278.top", {"start": v(-32110, 1150) * mm, "end": v(-31110, 1150) * mm});
            skLineSegment(sketch, "E278.left", {"start": v(-32110, 2750) * mm, "end": v(-32110, 1150) * mm});
            skLineSegment(sketch, "E278.right", {"start": v(-31110, 2750) * mm, "end": v(-31110, 1150) * mm});
            skLineSegment(sketch, "E279.bottom", {"start": v(-32110, 2800) * mm, "end": v(-31110, 2800) * mm});
            skLineSegment(sketch, "E279.top", {"start": v(-32110, 3750) * mm, "end": v(-31110, 3750) * mm});
            skLineSegment(sketch, "E279.left", {"start": v(-32110, 2800) * mm, "end": v(-32110, 3750) * mm});
            skLineSegment(sketch, "E279.right", {"start": v(-31110, 2800) * mm, "end": v(-31110, 3750) * mm});
            skPoint(sketch, "E280", {"position": v(-28060, 1200) * mm});
            skPoint(sketch, "E281", {"position": v(-25260, 1200) * mm});
            skPoint(sketch, "E282", {"position": v(-22460, 1200) * mm});
            skLineSegment(sketch, "E283.0.0", {"start": v(-28060, 1100) * mm, "end": v(-26363.5, 1100) * mm});
            skLineSegment(sketch, "E283.0.1", {"start": v(-26363.5, 1100) * mm, "end": v(-26363.5, 3800) * mm});
            skLineSegment(sketch, "E283.0.2", {"start": v(-26363.5, 3800) * mm, "end": v(-28060, 3800) * mm});
            skLineSegment(sketch, "E283.0.3", {"start": v(-28060, 3800) * mm, "end": v(-28060, 1100) * mm});
            skLineSegment(sketch, "E284", {"start": v(-27211.75, 1100) * mm, "end": v(-27211.75, 3700) * mm, "construction": true});
            skLineSegment(sketch, "E285.bottom", {"start": v(-28010, 2750) * mm, "end": v(-27249.25, 2750) * mm});
            skLineSegment(sketch, "E285.top", {"start": v(-28010, 1150) * mm, "end": v(-27249.25, 1150) * mm});
            skLineSegment(sketch, "E285.left", {"start": v(-28010, 2750) * mm, "end": v(-28010, 1150) * mm});
            skLineSegment(sketch, "E285.right", {"start": v(-27249.25, 2750) * mm, "end": v(-27249.25, 1150) * mm});
            skLineSegment(sketch, "E286.bottom", {"start": v(-28010, 2800) * mm, "end": v(-27249.25, 2800) * mm});
            skLineSegment(sketch, "E286.top", {"start": v(-28010, 3750) * mm, "end": v(-27249.25, 3750) * mm});
            skLineSegment(sketch, "E286.left", {"start": v(-28010, 2800) * mm, "end": v(-28010, 3750) * mm});
            skLineSegment(sketch, "E286.right", {"start": v(-27249.25, 2800) * mm, "end": v(-27249.25, 3750) * mm});
            skLineSegment(sketch, "E287.MirrorCS", {"start": v(-26413.5, 3750) * mm, "end": v(-27174.25, 3750) * mm});
            skLineSegment(sketch, "E288.MirrorCS", {"start": v(-27174.25, 2800) * mm, "end": v(-27174.25, 3750) * mm});
            skLineSegment(sketch, "E289.MirrorCS", {"start": v(-26413.5, 2800) * mm, "end": v(-27174.25, 2800) * mm});
            skLineSegment(sketch, "E290.MirrorCS", {"start": v(-26413.5, 2800) * mm, "end": v(-26413.5, 3750) * mm});
            skLineSegment(sketch, "E291.MirrorCS", {"start": v(-26413.5, 2750) * mm, "end": v(-27174.25, 2750) * mm});
            skLineSegment(sketch, "E292.MirrorCS", {"start": v(-27174.25, 2750) * mm, "end": v(-27174.25, 1150) * mm});
            skLineSegment(sketch, "E293.MirrorCS", {"start": v(-26413.5, 1150) * mm, "end": v(-27174.25, 1150) * mm});
            skLineSegment(sketch, "E294.MirrorCS", {"start": v(-26413.5, 2750) * mm, "end": v(-26413.5, 1150) * mm});
            skLineSegment(sketch, "E295.0.0", {"start": v(-25260, 1100) * mm, "end": v(-23562.14, 1100) * mm});
            skLineSegment(sketch, "E295.0.1", {"start": v(-23562.14, 1100) * mm, "end": v(-23562.14, 3800) * mm});
            skLineSegment(sketch, "E295.0.2", {"start": v(-23562.14, 3800) * mm, "end": v(-25260, 3800) * mm});
            skLineSegment(sketch, "E295.0.3", {"start": v(-25260, 3800) * mm, "end": v(-25260, 1100) * mm});
            skLineSegment(sketch, "E296", {"start": v(-24411.07, 1100) * mm, "end": v(-24411.07, 3700) * mm, "construction": true});
            skLineSegment(sketch, "E297.bottom", {"start": v(-25210, 2750) * mm, "end": v(-24448.57, 2750) * mm});
            skLineSegment(sketch, "E297.top", {"start": v(-25210, 1150) * mm, "end": v(-24448.57, 1150) * mm});
            skLineSegment(sketch, "E297.left", {"start": v(-25210, 2750) * mm, "end": v(-25210, 1150) * mm});
            skLineSegment(sketch, "E297.right", {"start": v(-24448.57, 2750) * mm, "end": v(-24448.57, 1150) * mm});
            skLineSegment(sketch, "E298.bottom", {"start": v(-25210, 2800) * mm, "end": v(-24448.57, 2800) * mm});
            skLineSegment(sketch, "E298.top", {"start": v(-25210, 3750) * mm, "end": v(-24448.57, 3750) * mm});
            skLineSegment(sketch, "E298.left", {"start": v(-25210, 2800) * mm, "end": v(-25210, 3750) * mm});
            skLineSegment(sketch, "E298.right", {"start": v(-24448.57, 2800) * mm, "end": v(-24448.57, 3750) * mm});
            skLineSegment(sketch, "E299.MirrorCS", {"start": v(-23612.14, 3750) * mm, "end": v(-24373.57, 3750) * mm});
            skLineSegment(sketch, "E300.MirrorCS", {"start": v(-24373.57, 2800) * mm, "end": v(-24373.57, 3750) * mm});
            skLineSegment(sketch, "E301.MirrorCS", {"start": v(-23612.14, 2800) * mm, "end": v(-24373.57, 2800) * mm});
            skLineSegment(sketch, "E302.MirrorCS", {"start": v(-23612.14, 2800) * mm, "end": v(-23612.14, 3750) * mm});
            skLineSegment(sketch, "E303.MirrorCS", {"start": v(-23612.14, 2750) * mm, "end": v(-24373.57, 2750) * mm});
            skLineSegment(sketch, "E304.MirrorCS", {"start": v(-24373.57, 2750) * mm, "end": v(-24373.57, 1150) * mm});
            skLineSegment(sketch, "E305.MirrorCS", {"start": v(-23612.14, 1150) * mm, "end": v(-24373.57, 1150) * mm});
            skLineSegment(sketch, "E306.MirrorCS", {"start": v(-23612.14, 2750) * mm, "end": v(-23612.14, 1150) * mm});
            skLineSegment(sketch, "E307.0.0", {"start": v(-22460, 1100) * mm, "end": v(-20761.44, 1100) * mm});
            skLineSegment(sketch, "E307.0.1", {"start": v(-20761.44, 1100) * mm, "end": v(-20761.44, 3800) * mm});
            skLineSegment(sketch, "E307.0.2", {"start": v(-20761.44, 3800) * mm, "end": v(-22460, 3800) * mm});
            skLineSegment(sketch, "E307.0.3", {"start": v(-22460, 3800) * mm, "end": v(-22460, 1100) * mm});
            skLineSegment(sketch, "E308", {"start": v(-21610.72, 1100) * mm, "end": v(-21610.72, 3700) * mm, "construction": true});
            skLineSegment(sketch, "E309.bottom", {"start": v(-22410, 2750) * mm, "end": v(-21648.22, 2750) * mm});
            skLineSegment(sketch, "E309.top", {"start": v(-22410, 1150) * mm, "end": v(-21648.22, 1150) * mm});
            skLineSegment(sketch, "E309.left", {"start": v(-22410, 2750) * mm, "end": v(-22410, 1150) * mm});
            skLineSegment(sketch, "E309.right", {"start": v(-21648.22, 2750) * mm, "end": v(-21648.22, 1150) * mm});
            skLineSegment(sketch, "E310.bottom", {"start": v(-22410, 2800) * mm, "end": v(-21648.22, 2800) * mm});
            skLineSegment(sketch, "E310.top", {"start": v(-22410, 3750) * mm, "end": v(-21648.22, 3750) * mm});
            skLineSegment(sketch, "E310.left", {"start": v(-22410, 2800) * mm, "end": v(-22410, 3750) * mm});
            skLineSegment(sketch, "E310.right", {"start": v(-21648.22, 2800) * mm, "end": v(-21648.22, 3750) * mm});
            skLineSegment(sketch, "E311.MirrorCS", {"start": v(-20811.44, 3750) * mm, "end": v(-21573.22, 3750) * mm});
            skLineSegment(sketch, "E312.MirrorCS", {"start": v(-21573.22, 2800) * mm, "end": v(-21573.22, 3750) * mm});
            skLineSegment(sketch, "E313.MirrorCS", {"start": v(-20811.44, 2800) * mm, "end": v(-21573.22, 2800) * mm});
            skLineSegment(sketch, "E314.MirrorCS", {"start": v(-20811.44, 2800) * mm, "end": v(-20811.44, 3750) * mm});
            skLineSegment(sketch, "E315.MirrorCS", {"start": v(-20811.44, 2750) * mm, "end": v(-21573.22, 2750) * mm});
            skLineSegment(sketch, "E316.MirrorCS", {"start": v(-21573.22, 2750) * mm, "end": v(-21573.22, 1150) * mm});
            skLineSegment(sketch, "E317.MirrorCS", {"start": v(-20811.44, 1150) * mm, "end": v(-21573.22, 1150) * mm});
            skLineSegment(sketch, "E318.MirrorCS", {"start": v(-20811.44, 2750) * mm, "end": v(-20811.44, 1150) * mm});
            skLineSegment(sketch, "E319.1.0.0", {"start": v(-15810, 2800) * mm, "end": v(-15048.57, 2800) * mm});
            skLineSegment(sketch, "E319.1.0.1", {"start": v(-18610, 2800) * mm, "end": v(-18610, 3750) * mm});
            skLineSegment(sketch, "E319.1.0.2", {"start": v(-11411.44, 2800) * mm, "end": v(-11411.44, 3750) * mm});
            skLineSegment(sketch, "E319.1.0.3", {"start": v(-15810, 2750) * mm, "end": v(-15048.57, 2750) * mm});
            skLineSegment(sketch, "E319.1.0.4", {"start": v(-18610, 3750) * mm, "end": v(-17849.25, 3750) * mm});
            skLineSegment(sketch, "E319.1.0.5", {"start": v(-17013.5, 2750) * mm, "end": v(-17013.5, 1150) * mm});
            skLineSegment(sketch, "E319.1.0.6", {"start": v(-14212.14, 2800) * mm, "end": v(-14973.57, 2800) * mm});
            skLineSegment(sketch, "E319.1.0.7", {"start": v(-18610, 2800) * mm, "end": v(-17849.25, 2800) * mm});
            skLineSegment(sketch, "E319.1.0.8", {"start": v(-13060, 1100) * mm, "end": v(-11361.44, 1100) * mm});
            skPoint(sketch, "E319.1.0.9", {"position": v(-18660, 1200) * mm});
            skLineSegment(sketch, "E319.1.0.10", {"start": v(-13010, 2800) * mm, "end": v(-12248.22, 2800) * mm});
            skLineSegment(sketch, "E319.1.0.11", {"start": v(-13010, 1150) * mm, "end": v(-12248.22, 1150) * mm});
            skLineSegment(sketch, "E319.1.0.12", {"start": v(-18660, 1100) * mm, "end": v(-16963.5, 1100) * mm});
            skLineSegment(sketch, "E319.1.0.13", {"start": v(-17013.5, 2750) * mm, "end": v(-17774.25, 2750) * mm});
            skLineSegment(sketch, "E319.1.0.14", {"start": v(-13010, 2750) * mm, "end": v(-13010, 1150) * mm});
            skLineSegment(sketch, "E319.1.0.15", {"start": v(-18610, 1150) * mm, "end": v(-17849.25, 1150) * mm});
            skLineSegment(sketch, "E319.1.0.16", {"start": v(-15048.57, 2750) * mm, "end": v(-15048.57, 1150) * mm});
            skLineSegment(sketch, "E319.1.0.17", {"start": v(-16963.5, 1100) * mm, "end": v(-16963.5, 3800) * mm});
            skLineSegment(sketch, "E319.1.0.18", {"start": v(-13010, 2750) * mm, "end": v(-12248.22, 2750) * mm});
            skLineSegment(sketch, "E319.1.0.19", {"start": v(-17013.5, 2800) * mm, "end": v(-17774.25, 2800) * mm});
            skLineSegment(sketch, "E319.1.0.20", {"start": v(-15048.57, 2800) * mm, "end": v(-15048.57, 3750) * mm});
            skPoint(sketch, "E319.1.0.21", {"position": v(-15860, 1200) * mm});
            skLineSegment(sketch, "E319.1.0.22", {"start": v(-15810, 2800) * mm, "end": v(-15810, 3750) * mm});
            skLineSegment(sketch, "E319.1.0.23", {"start": v(-11411.44, 2750) * mm, "end": v(-11411.44, 1150) * mm});
            skLineSegment(sketch, "E319.1.0.24", {"start": v(-15810, 2750) * mm, "end": v(-15810, 1150) * mm});
            skLineSegment(sketch, "E319.1.0.25", {"start": v(-11361.44, 3800) * mm, "end": v(-13060, 3800) * mm});
            skLineSegment(sketch, "E319.1.0.26", {"start": v(-17013.5, 1150) * mm, "end": v(-17774.25, 1150) * mm});
            skLineSegment(sketch, "E319.1.0.27", {"start": v(-18610, 2750) * mm, "end": v(-17849.25, 2750) * mm});
            skLineSegment(sketch, "E319.1.0.28", {"start": v(-17013.5, 3750) * mm, "end": v(-17774.25, 3750) * mm});
            skLineSegment(sketch, "E319.1.0.29", {"start": v(-17811.75, 1100) * mm, "end": v(-17811.75, 3700) * mm, "construction": true});
            skLineSegment(sketch, "E319.1.0.30", {"start": v(-14162.14, 1100) * mm, "end": v(-14162.14, 3800) * mm});
            skLineSegment(sketch, "E319.1.0.31", {"start": v(-11411.44, 1150) * mm, "end": v(-12173.22, 1150) * mm});
            skLineSegment(sketch, "E319.1.0.32", {"start": v(-17013.5, 2800) * mm, "end": v(-17013.5, 3750) * mm});
            skPoint(sketch, "E319.1.0.33", {"position": v(-13060, 1200) * mm});
            skLineSegment(sketch, "E319.1.0.34", {"start": v(-13010, 2800) * mm, "end": v(-13010, 3750) * mm});
            skLineSegment(sketch, "E319.1.0.35", {"start": v(-18660, 3800) * mm, "end": v(-18660, 1100) * mm});
            skLineSegment(sketch, "E319.1.0.36", {"start": v(-12210.72, 1100) * mm, "end": v(-12210.72, 3700) * mm, "construction": true});
            skLineSegment(sketch, "E319.1.0.37", {"start": v(-11411.44, 2750) * mm, "end": v(-12173.22, 2750) * mm});
            skLineSegment(sketch, "E319.1.0.38", {"start": v(-15810, 3750) * mm, "end": v(-15048.57, 3750) * mm});
            skLineSegment(sketch, "E319.1.0.39", {"start": v(-15860, 1100) * mm, "end": v(-14162.14, 1100) * mm});
            skLineSegment(sketch, "E319.1.0.40", {"start": v(-13060, 3800) * mm, "end": v(-13060, 1100) * mm});
            skLineSegment(sketch, "E319.1.0.41", {"start": v(-11411.44, 2800) * mm, "end": v(-12173.22, 2800) * mm});
            skLineSegment(sketch, "E319.1.0.42", {"start": v(-14212.14, 1150) * mm, "end": v(-14973.57, 1150) * mm});
            skLineSegment(sketch, "E319.1.0.43", {"start": v(-14162.14, 3800) * mm, "end": v(-15860, 3800) * mm});
            skLineSegment(sketch, "E319.1.0.44", {"start": v(-14212.14, 2750) * mm, "end": v(-14212.14, 1150) * mm});
            skLineSegment(sketch, "E319.1.0.45", {"start": v(-14212.14, 2750) * mm, "end": v(-14973.57, 2750) * mm});
            skLineSegment(sketch, "E319.1.0.46", {"start": v(-11361.44, 1100) * mm, "end": v(-11361.44, 3800) * mm});
            skLineSegment(sketch, "E319.1.0.47", {"start": v(-18610, 2750) * mm, "end": v(-18610, 1150) * mm});
            skLineSegment(sketch, "E319.1.0.48", {"start": v(-15011.07, 1100) * mm, "end": v(-15011.07, 3700) * mm, "construction": true});
            skLineSegment(sketch, "E319.1.0.49", {"start": v(-13010, 3750) * mm, "end": v(-12248.22, 3750) * mm});
            skLineSegment(sketch, "E319.1.0.50", {"start": v(-11411.44, 3750) * mm, "end": v(-12173.22, 3750) * mm});
            skLineSegment(sketch, "E319.1.0.51", {"start": v(-14212.14, 3750) * mm, "end": v(-14973.57, 3750) * mm});
            skLineSegment(sketch, "E319.1.0.52", {"start": v(-16963.5, 3800) * mm, "end": v(-18660, 3800) * mm});
            skLineSegment(sketch, "E319.1.0.53", {"start": v(-14973.57, 2800) * mm, "end": v(-14973.57, 3750) * mm});
            skLineSegment(sketch, "E319.1.0.54", {"start": v(-15810, 1150) * mm, "end": v(-15048.57, 1150) * mm});
            skLineSegment(sketch, "E319.1.0.55", {"start": v(-12173.22, 2750) * mm, "end": v(-12173.22, 1150) * mm});
            skLineSegment(sketch, "E319.1.0.56", {"start": v(-14212.14, 2800) * mm, "end": v(-14212.14, 3750) * mm});
            skLineSegment(sketch, "E319.1.0.57", {"start": v(-15860, 3800) * mm, "end": v(-15860, 1100) * mm});
            skLineSegment(sketch, "E319.1.0.58", {"start": v(-17849.25, 2750) * mm, "end": v(-17849.25, 1150) * mm});
            skLineSegment(sketch, "E319.1.0.59", {"start": v(-12173.22, 2800) * mm, "end": v(-12173.22, 3750) * mm});
            skLineSegment(sketch, "E319.1.0.60", {"start": v(-14973.57, 2750) * mm, "end": v(-14973.57, 1150) * mm});
            skLineSegment(sketch, "E319.1.0.61", {"start": v(-17849.25, 2800) * mm, "end": v(-17849.25, 3750) * mm});
            skLineSegment(sketch, "E319.1.0.62", {"start": v(-17774.25, 2800) * mm, "end": v(-17774.25, 3750) * mm});
            skLineSegment(sketch, "E319.1.0.63", {"start": v(-12248.22, 2800) * mm, "end": v(-12248.22, 3750) * mm});
            skLineSegment(sketch, "E319.1.0.64", {"start": v(-17774.25, 2750) * mm, "end": v(-17774.25, 1150) * mm});
            skLineSegment(sketch, "E319.1.0.65", {"start": v(-12248.22, 2750) * mm, "end": v(-12248.22, 1150) * mm});
            skLineSegment(sketch, "E319.2.0.0", {"start": v(-6410, 2800) * mm, "end": v(-5648.57, 2800) * mm});
            skLineSegment(sketch, "E319.2.0.1", {"start": v(-9210, 2800) * mm, "end": v(-9210, 3750) * mm});
            skLineSegment(sketch, "E319.2.0.2", {"start": v(-2011.44, 2800) * mm, "end": v(-2011.44, 3750) * mm});
            skLineSegment(sketch, "E319.2.0.3", {"start": v(-6410, 2750) * mm, "end": v(-5648.57, 2750) * mm});
            skLineSegment(sketch, "E319.2.0.4", {"start": v(-9210, 3750) * mm, "end": v(-8449.25, 3750) * mm});
            skLineSegment(sketch, "E319.2.0.5", {"start": v(-7613.5, 2750) * mm, "end": v(-7613.5, 1150) * mm});
            skLineSegment(sketch, "E319.2.0.6", {"start": v(-4812.14, 2800) * mm, "end": v(-5573.57, 2800) * mm});
            skLineSegment(sketch, "E319.2.0.7", {"start": v(-9210, 2800) * mm, "end": v(-8449.25, 2800) * mm});
            skLineSegment(sketch, "E319.2.0.8", {"start": v(-3660, 1100) * mm, "end": v(-1961.44, 1100) * mm});
            skPoint(sketch, "E319.2.0.9", {"position": v(-9260, 1200) * mm});
            skLineSegment(sketch, "E319.2.0.10", {"start": v(-3610, 2800) * mm, "end": v(-2848.22, 2800) * mm});
            skLineSegment(sketch, "E319.2.0.11", {"start": v(-3610, 1150) * mm, "end": v(-2848.22, 1150) * mm});
            skLineSegment(sketch, "E319.2.0.12", {"start": v(-9260, 1100) * mm, "end": v(-7563.5, 1100) * mm});
            skLineSegment(sketch, "E319.2.0.13", {"start": v(-7613.5, 2750) * mm, "end": v(-8374.25, 2750) * mm});
            skLineSegment(sketch, "E319.2.0.14", {"start": v(-3610, 2750) * mm, "end": v(-3610, 1150) * mm});
            skLineSegment(sketch, "E319.2.0.15", {"start": v(-9210, 1150) * mm, "end": v(-8449.25, 1150) * mm});
            skLineSegment(sketch, "E319.2.0.16", {"start": v(-5648.57, 2750) * mm, "end": v(-5648.57, 1150) * mm});
            skLineSegment(sketch, "E319.2.0.17", {"start": v(-7563.5, 1100) * mm, "end": v(-7563.5, 3800) * mm});
            skLineSegment(sketch, "E319.2.0.18", {"start": v(-3610, 2750) * mm, "end": v(-2848.22, 2750) * mm});
            skLineSegment(sketch, "E319.2.0.19", {"start": v(-7613.5, 2800) * mm, "end": v(-8374.25, 2800) * mm});
            skLineSegment(sketch, "E319.2.0.20", {"start": v(-5648.57, 2800) * mm, "end": v(-5648.57, 3750) * mm});
            skPoint(sketch, "E319.2.0.21", {"position": v(-6460, 1200) * mm});
            skLineSegment(sketch, "E319.2.0.22", {"start": v(-6410, 2800) * mm, "end": v(-6410, 3750) * mm});
            skLineSegment(sketch, "E319.2.0.23", {"start": v(-2011.44, 2750) * mm, "end": v(-2011.44, 1150) * mm});
            skLineSegment(sketch, "E319.2.0.24", {"start": v(-6410, 2750) * mm, "end": v(-6410, 1150) * mm});
            skLineSegment(sketch, "E319.2.0.25", {"start": v(-1961.44, 3800) * mm, "end": v(-3660, 3800) * mm});
            skLineSegment(sketch, "E319.2.0.26", {"start": v(-7613.5, 1150) * mm, "end": v(-8374.25, 1150) * mm});
            skLineSegment(sketch, "E319.2.0.27", {"start": v(-9210, 2750) * mm, "end": v(-8449.25, 2750) * mm});
            skLineSegment(sketch, "E319.2.0.28", {"start": v(-7613.5, 3750) * mm, "end": v(-8374.25, 3750) * mm});
            skLineSegment(sketch, "E319.2.0.29", {"start": v(-8411.75, 1100) * mm, "end": v(-8411.75, 3700) * mm, "construction": true});
            skLineSegment(sketch, "E319.2.0.30", {"start": v(-4762.14, 1100) * mm, "end": v(-4762.14, 3800) * mm});
            skLineSegment(sketch, "E319.2.0.31", {"start": v(-2011.44, 1150) * mm, "end": v(-2773.22, 1150) * mm});
            skLineSegment(sketch, "E319.2.0.32", {"start": v(-7613.5, 2800) * mm, "end": v(-7613.5, 3750) * mm});
            skPoint(sketch, "E319.2.0.33", {"position": v(-3660, 1200) * mm});
            skLineSegment(sketch, "E319.2.0.34", {"start": v(-3610, 2800) * mm, "end": v(-3610, 3750) * mm});
            skLineSegment(sketch, "E319.2.0.35", {"start": v(-9260, 3800) * mm, "end": v(-9260, 1100) * mm});
            skLineSegment(sketch, "E319.2.0.36", {"start": v(-2810.72, 1100) * mm, "end": v(-2810.72, 3700) * mm, "construction": true});
            skLineSegment(sketch, "E319.2.0.37", {"start": v(-2011.44, 2750) * mm, "end": v(-2773.22, 2750) * mm});
            skLineSegment(sketch, "E319.2.0.38", {"start": v(-6410, 3750) * mm, "end": v(-5648.57, 3750) * mm});
            skLineSegment(sketch, "E319.2.0.39", {"start": v(-6460, 1100) * mm, "end": v(-4762.14, 1100) * mm});
            skLineSegment(sketch, "E319.2.0.40", {"start": v(-3660, 3800) * mm, "end": v(-3660, 1100) * mm});
            skLineSegment(sketch, "E319.2.0.41", {"start": v(-2011.44, 2800) * mm, "end": v(-2773.22, 2800) * mm});
            skLineSegment(sketch, "E319.2.0.42", {"start": v(-4812.14, 1150) * mm, "end": v(-5573.57, 1150) * mm});
            skLineSegment(sketch, "E319.2.0.43", {"start": v(-4762.14, 3800) * mm, "end": v(-6460, 3800) * mm});
            skLineSegment(sketch, "E319.2.0.44", {"start": v(-4812.14, 2750) * mm, "end": v(-4812.14, 1150) * mm});
            skLineSegment(sketch, "E319.2.0.45", {"start": v(-4812.14, 2750) * mm, "end": v(-5573.57, 2750) * mm});
            skLineSegment(sketch, "E319.2.0.46", {"start": v(-1961.44, 1100) * mm, "end": v(-1961.44, 3800) * mm});
            skLineSegment(sketch, "E319.2.0.47", {"start": v(-9210, 2750) * mm, "end": v(-9210, 1150) * mm});
            skLineSegment(sketch, "E319.2.0.48", {"start": v(-5611.07, 1100) * mm, "end": v(-5611.07, 3700) * mm, "construction": true});
            skLineSegment(sketch, "E319.2.0.49", {"start": v(-3610, 3750) * mm, "end": v(-2848.22, 3750) * mm});
            skLineSegment(sketch, "E319.2.0.50", {"start": v(-2011.44, 3750) * mm, "end": v(-2773.22, 3750) * mm});
            skLineSegment(sketch, "E319.2.0.51", {"start": v(-4812.14, 3750) * mm, "end": v(-5573.57, 3750) * mm});
            skLineSegment(sketch, "E319.2.0.52", {"start": v(-7563.5, 3800) * mm, "end": v(-9260, 3800) * mm});
            skLineSegment(sketch, "E319.2.0.53", {"start": v(-5573.57, 2800) * mm, "end": v(-5573.57, 3750) * mm});
            skLineSegment(sketch, "E319.2.0.54", {"start": v(-6410, 1150) * mm, "end": v(-5648.57, 1150) * mm});
            skLineSegment(sketch, "E319.2.0.55", {"start": v(-2773.22, 2750) * mm, "end": v(-2773.22, 1150) * mm});
            skLineSegment(sketch, "E319.2.0.56", {"start": v(-4812.14, 2800) * mm, "end": v(-4812.14, 3750) * mm});
            skLineSegment(sketch, "E319.2.0.57", {"start": v(-6460, 3800) * mm, "end": v(-6460, 1100) * mm});
            skLineSegment(sketch, "E319.2.0.58", {"start": v(-8449.25, 2750) * mm, "end": v(-8449.25, 1150) * mm});
            skLineSegment(sketch, "E319.2.0.59", {"start": v(-2773.22, 2800) * mm, "end": v(-2773.22, 3750) * mm});
            skLineSegment(sketch, "E319.2.0.60", {"start": v(-5573.57, 2750) * mm, "end": v(-5573.57, 1150) * mm});
            skLineSegment(sketch, "E319.2.0.61", {"start": v(-8449.25, 2800) * mm, "end": v(-8449.25, 3750) * mm});
            skLineSegment(sketch, "E319.2.0.62", {"start": v(-8374.25, 2800) * mm, "end": v(-8374.25, 3750) * mm});
            skLineSegment(sketch, "E319.2.0.63", {"start": v(-2848.22, 2800) * mm, "end": v(-2848.22, 3750) * mm});
            skLineSegment(sketch, "E319.2.0.64", {"start": v(-8374.25, 2750) * mm, "end": v(-8374.25, 1150) * mm});
            skLineSegment(sketch, "E319.2.0.65", {"start": v(-2848.22, 2750) * mm, "end": v(-2848.22, 1150) * mm});
            skLineSegment(sketch, "E319.direction1", {"start": v(-28060, 1200) * mm, "end": v(-18660, 1200) * mm, "construction": true});
            skLineSegment(sketch, "E320.0", {"start": v(-31060, 3800) * mm, "end": v(-31060, 1100) * mm});
            skSolve(sketch);
        }
        {
            var Q0;
            Q0=qSketchRegion(id+"F28",true);
            extrude(context, id + "F29", {"entities" : qUnion([Q0]), "depth" : 50 * mm, "offsetDistance" : 25 * mm});
        }
        {
            var Q0;
            Q0=makeQuery(id+"F27.opExtrude","CAP_FACE",FACE,{"disambiguationData":[OSD([sQuery(id+"F26.wireOp",EDGE,"E250.24"),sQuery(id+"F26.wireOp",EDGE,"E250.25"),sQuery(id+"F26.wireOp",EDGE,"E250.30"),sQuery(id+"F26.wireOp",EDGE,"E250.34")])],"isStart":false});
            var sketch = newSketch(context, id + "F30", { "sketchPlane" : qUnion([Q0])});
            skPoint(sketch, "E321.65", {"position": v(28060, 1200) * mm});
            skPoint(sketch, "E321.66", {"position": v(25260, 1200) * mm});
            skPoint(sketch, "E321.67", {"position": v(22460, 1200) * mm});
            skLineSegment(sketch, "E321.68", {"start": v(28060, 1100) * mm, "end": v(26363.5, 1100) * mm});
            skLineSegment(sketch, "E321.69", {"start": v(26363.5, 1100) * mm, "end": v(26363.5, 3800) * mm});
            skLineSegment(sketch, "E321.70", {"start": v(26363.5, 3800) * mm, "end": v(28060, 3800) * mm});
            skLineSegment(sketch, "E321.71", {"start": v(28060, 3800) * mm, "end": v(28060, 1100) * mm});
            skLineSegment(sketch, "E321.72", {"start": v(27211.75, 1100) * mm, "end": v(27211.75, 3700) * mm});
            skLineSegment(sketch, "E321.73", {"start": v(28010, 2750) * mm, "end": v(27249.25, 2750) * mm});
            skLineSegment(sketch, "E321.74", {"start": v(28010, 1150) * mm, "end": v(27249.25, 1150) * mm});
            skLineSegment(sketch, "E321.75", {"start": v(28010, 2750) * mm, "end": v(28010, 1150) * mm});
            skLineSegment(sketch, "E321.76", {"start": v(27249.25, 2750) * mm, "end": v(27249.25, 1150) * mm});
            skLineSegment(sketch, "E321.77", {"start": v(28010, 2800) * mm, "end": v(27249.25, 2800) * mm});
            skLineSegment(sketch, "E321.78", {"start": v(28010, 3750) * mm, "end": v(27249.25, 3750) * mm});
            skLineSegment(sketch, "E321.79", {"start": v(28010, 2800) * mm, "end": v(28010, 3750) * mm});
            skLineSegment(sketch, "E321.80", {"start": v(27249.25, 2800) * mm, "end": v(27249.25, 3750) * mm});
            skLineSegment(sketch, "E321.81", {"start": v(26413.5, 3750) * mm, "end": v(27174.25, 3750) * mm});
            skLineSegment(sketch, "E321.82", {"start": v(27174.25, 2800) * mm, "end": v(27174.25, 3750) * mm});
            skLineSegment(sketch, "E321.83", {"start": v(26413.5, 2800) * mm, "end": v(27174.25, 2800) * mm});
            skLineSegment(sketch, "E321.84", {"start": v(26413.5, 2800) * mm, "end": v(26413.5, 3750) * mm});
            skLineSegment(sketch, "E321.85", {"start": v(26413.5, 2750) * mm, "end": v(27174.25, 2750) * mm});
            skLineSegment(sketch, "E321.86", {"start": v(27174.25, 2750) * mm, "end": v(27174.25, 1150) * mm});
            skLineSegment(sketch, "E321.87", {"start": v(26413.5, 1150) * mm, "end": v(27174.25, 1150) * mm});
            skLineSegment(sketch, "E321.88", {"start": v(26413.5, 2750) * mm, "end": v(26413.5, 1150) * mm});
            skLineSegment(sketch, "E321.89", {"start": v(25260, 1100) * mm, "end": v(23562.14, 1100) * mm});
            skLineSegment(sketch, "E321.90", {"start": v(23562.14, 1100) * mm, "end": v(23562.14, 3800) * mm});
            skLineSegment(sketch, "E321.91", {"start": v(23562.14, 3800) * mm, "end": v(25260, 3800) * mm});
            skLineSegment(sketch, "E321.92", {"start": v(25260, 3800) * mm, "end": v(25260, 1100) * mm});
            skLineSegment(sketch, "E321.93", {"start": v(24411.07, 1100) * mm, "end": v(24411.07, 3700) * mm});
            skLineSegment(sketch, "E321.94", {"start": v(25210, 2750) * mm, "end": v(24448.57, 2750) * mm});
            skLineSegment(sketch, "E321.95", {"start": v(25210, 1150) * mm, "end": v(24448.57, 1150) * mm});
            skLineSegment(sketch, "E321.96", {"start": v(25210, 2750) * mm, "end": v(25210, 1150) * mm});
            skLineSegment(sketch, "E321.97", {"start": v(24448.57, 2750) * mm, "end": v(24448.57, 1150) * mm});
            skLineSegment(sketch, "E321.98", {"start": v(25210, 2800) * mm, "end": v(24448.57, 2800) * mm});
            skLineSegment(sketch, "E321.99", {"start": v(25210, 3750) * mm, "end": v(24448.57, 3750) * mm});
            skLineSegment(sketch, "E321.100", {"start": v(25210, 2800) * mm, "end": v(25210, 3750) * mm});
            skLineSegment(sketch, "E321.101", {"start": v(24448.57, 2800) * mm, "end": v(24448.57, 3750) * mm});
            skLineSegment(sketch, "E321.102", {"start": v(23612.14, 3750) * mm, "end": v(24373.57, 3750) * mm});
            skLineSegment(sketch, "E321.103", {"start": v(24373.57, 2800) * mm, "end": v(24373.57, 3750) * mm});
            skLineSegment(sketch, "E321.104", {"start": v(23612.14, 2800) * mm, "end": v(24373.57, 2800) * mm});
            skLineSegment(sketch, "E321.105", {"start": v(23612.14, 2800) * mm, "end": v(23612.14, 3750) * mm});
            skLineSegment(sketch, "E321.106", {"start": v(23612.14, 2750) * mm, "end": v(24373.57, 2750) * mm});
            skLineSegment(sketch, "E321.107", {"start": v(24373.57, 2750) * mm, "end": v(24373.57, 1150) * mm});
            skLineSegment(sketch, "E321.108", {"start": v(23612.14, 1150) * mm, "end": v(24373.57, 1150) * mm});
            skLineSegment(sketch, "E321.109", {"start": v(23612.14, 2750) * mm, "end": v(23612.14, 1150) * mm});
            skLineSegment(sketch, "E321.110", {"start": v(22460, 1100) * mm, "end": v(20761.44, 1100) * mm});
            skLineSegment(sketch, "E321.111", {"start": v(20761.44, 1100) * mm, "end": v(20761.44, 3800) * mm});
            skLineSegment(sketch, "E321.112", {"start": v(20761.44, 3800) * mm, "end": v(22460, 3800) * mm});
            skLineSegment(sketch, "E321.113", {"start": v(22460, 3800) * mm, "end": v(22460, 1100) * mm});
            skLineSegment(sketch, "E321.114", {"start": v(21610.72, 1100) * mm, "end": v(21610.72, 3700) * mm});
            skLineSegment(sketch, "E321.115", {"start": v(22410, 2750) * mm, "end": v(21648.22, 2750) * mm});
            skLineSegment(sketch, "E321.116", {"start": v(22410, 1150) * mm, "end": v(21648.22, 1150) * mm});
            skLineSegment(sketch, "E321.117", {"start": v(22410, 2750) * mm, "end": v(22410, 1150) * mm});
            skLineSegment(sketch, "E321.118", {"start": v(21648.22, 2750) * mm, "end": v(21648.22, 1150) * mm});
            skLineSegment(sketch, "E321.119", {"start": v(22410, 2800) * mm, "end": v(21648.22, 2800) * mm});
            skLineSegment(sketch, "E321.120", {"start": v(22410, 3750) * mm, "end": v(21648.22, 3750) * mm});
            skLineSegment(sketch, "E321.121", {"start": v(22410, 2800) * mm, "end": v(22410, 3750) * mm});
            skLineSegment(sketch, "E321.122", {"start": v(21648.22, 2800) * mm, "end": v(21648.22, 3750) * mm});
            skLineSegment(sketch, "E321.123", {"start": v(20811.44, 3750) * mm, "end": v(21573.22, 3750) * mm});
            skLineSegment(sketch, "E321.124", {"start": v(21573.22, 2800) * mm, "end": v(21573.22, 3750) * mm});
            skLineSegment(sketch, "E321.125", {"start": v(20811.44, 2800) * mm, "end": v(21573.22, 2800) * mm});
            skLineSegment(sketch, "E321.126", {"start": v(20811.44, 2800) * mm, "end": v(20811.44, 3750) * mm});
            skLineSegment(sketch, "E321.127", {"start": v(20811.44, 2750) * mm, "end": v(21573.22, 2750) * mm});
            skLineSegment(sketch, "E321.128", {"start": v(21573.22, 2750) * mm, "end": v(21573.22, 1150) * mm});
            skLineSegment(sketch, "E321.129", {"start": v(20811.44, 1150) * mm, "end": v(21573.22, 1150) * mm});
            skLineSegment(sketch, "E321.130", {"start": v(20811.44, 2750) * mm, "end": v(20811.44, 1150) * mm});
            skLineSegment(sketch, "E321.131", {"start": v(15810, 2800) * mm, "end": v(15048.57, 2800) * mm});
            skLineSegment(sketch, "E321.132", {"start": v(18610, 2800) * mm, "end": v(18610, 3750) * mm});
            skLineSegment(sketch, "E321.133", {"start": v(11411.44, 2800) * mm, "end": v(11411.44, 3750) * mm});
            skLineSegment(sketch, "E321.134", {"start": v(15810, 2750) * mm, "end": v(15048.57, 2750) * mm});
            skLineSegment(sketch, "E321.135", {"start": v(18610, 3750) * mm, "end": v(17849.25, 3750) * mm});
            skLineSegment(sketch, "E321.136", {"start": v(17013.5, 2750) * mm, "end": v(17013.5, 1150) * mm});
            skLineSegment(sketch, "E321.137", {"start": v(14212.14, 2800) * mm, "end": v(14973.57, 2800) * mm});
            skLineSegment(sketch, "E321.138", {"start": v(18610, 2800) * mm, "end": v(17849.25, 2800) * mm});
            skLineSegment(sketch, "E321.139", {"start": v(13060, 1100) * mm, "end": v(11361.44, 1100) * mm});
            skPoint(sketch, "E321.140", {"position": v(18660, 1200) * mm});
            skLineSegment(sketch, "E321.141", {"start": v(13010, 2800) * mm, "end": v(12248.22, 2800) * mm});
            skLineSegment(sketch, "E321.142", {"start": v(13010, 1150) * mm, "end": v(12248.22, 1150) * mm});
            skLineSegment(sketch, "E321.143", {"start": v(18660, 1100) * mm, "end": v(16963.5, 1100) * mm});
            skLineSegment(sketch, "E321.144", {"start": v(17013.5, 2750) * mm, "end": v(17774.25, 2750) * mm});
            skLineSegment(sketch, "E321.145", {"start": v(13010, 2750) * mm, "end": v(13010, 1150) * mm});
            skLineSegment(sketch, "E321.146", {"start": v(18610, 1150) * mm, "end": v(17849.25, 1150) * mm});
            skLineSegment(sketch, "E321.147", {"start": v(15048.57, 2750) * mm, "end": v(15048.57, 1150) * mm});
            skLineSegment(sketch, "E321.148", {"start": v(16963.5, 1100) * mm, "end": v(16963.5, 3800) * mm});
            skLineSegment(sketch, "E321.149", {"start": v(13010, 2750) * mm, "end": v(12248.22, 2750) * mm});
            skLineSegment(sketch, "E321.150", {"start": v(17013.5, 2800) * mm, "end": v(17774.25, 2800) * mm});
            skLineSegment(sketch, "E321.151", {"start": v(15048.57, 2800) * mm, "end": v(15048.57, 3750) * mm});
            skPoint(sketch, "E321.152", {"position": v(15860, 1200) * mm});
            skLineSegment(sketch, "E321.153", {"start": v(15810, 2800) * mm, "end": v(15810, 3750) * mm});
            skLineSegment(sketch, "E321.154", {"start": v(11411.44, 2750) * mm, "end": v(11411.44, 1150) * mm});
            skLineSegment(sketch, "E321.155", {"start": v(15810, 2750) * mm, "end": v(15810, 1150) * mm});
            skLineSegment(sketch, "E321.156", {"start": v(11361.44, 3800) * mm, "end": v(13060, 3800) * mm});
            skLineSegment(sketch, "E321.157", {"start": v(17013.5, 1150) * mm, "end": v(17774.25, 1150) * mm});
            skLineSegment(sketch, "E321.158", {"start": v(18610, 2750) * mm, "end": v(17849.25, 2750) * mm});
            skLineSegment(sketch, "E321.159", {"start": v(17013.5, 3750) * mm, "end": v(17774.25, 3750) * mm});
            skLineSegment(sketch, "E321.160", {"start": v(17811.75, 1100) * mm, "end": v(17811.75, 3700) * mm});
            skLineSegment(sketch, "E321.161", {"start": v(14162.14, 1100) * mm, "end": v(14162.14, 3800) * mm});
            skLineSegment(sketch, "E321.162", {"start": v(11411.44, 1150) * mm, "end": v(12173.22, 1150) * mm});
            skLineSegment(sketch, "E321.163", {"start": v(17013.5, 2800) * mm, "end": v(17013.5, 3750) * mm});
            skPoint(sketch, "E321.164", {"position": v(13060, 1200) * mm});
            skLineSegment(sketch, "E321.165", {"start": v(13010, 2800) * mm, "end": v(13010, 3750) * mm});
            skLineSegment(sketch, "E321.166", {"start": v(18660, 3800) * mm, "end": v(18660, 1100) * mm});
            skLineSegment(sketch, "E321.167", {"start": v(12210.72, 1100) * mm, "end": v(12210.72, 3700) * mm});
            skLineSegment(sketch, "E321.168", {"start": v(11411.44, 2750) * mm, "end": v(12173.22, 2750) * mm});
            skLineSegment(sketch, "E321.169", {"start": v(15810, 3750) * mm, "end": v(15048.57, 3750) * mm});
            skLineSegment(sketch, "E321.170", {"start": v(15860, 1100) * mm, "end": v(14162.14, 1100) * mm});
            skLineSegment(sketch, "E321.171", {"start": v(13060, 3800) * mm, "end": v(13060, 1100) * mm});
            skLineSegment(sketch, "E321.172", {"start": v(11411.44, 2800) * mm, "end": v(12173.22, 2800) * mm});
            skLineSegment(sketch, "E321.173", {"start": v(14212.14, 1150) * mm, "end": v(14973.57, 1150) * mm});
            skLineSegment(sketch, "E321.174", {"start": v(14162.14, 3800) * mm, "end": v(15860, 3800) * mm});
            skLineSegment(sketch, "E321.175", {"start": v(14212.14, 2750) * mm, "end": v(14212.14, 1150) * mm});
            skLineSegment(sketch, "E321.176", {"start": v(14212.14, 2750) * mm, "end": v(14973.57, 2750) * mm});
            skLineSegment(sketch, "E321.177", {"start": v(11361.44, 1100) * mm, "end": v(11361.44, 3800) * mm});
            skLineSegment(sketch, "E321.178", {"start": v(18610, 2750) * mm, "end": v(18610, 1150) * mm});
            skLineSegment(sketch, "E321.179", {"start": v(15011.07, 1100) * mm, "end": v(15011.07, 3700) * mm});
            skLineSegment(sketch, "E321.180", {"start": v(13010, 3750) * mm, "end": v(12248.22, 3750) * mm});
            skLineSegment(sketch, "E321.181", {"start": v(11411.44, 3750) * mm, "end": v(12173.22, 3750) * mm});
            skLineSegment(sketch, "E321.182", {"start": v(14212.14, 3750) * mm, "end": v(14973.57, 3750) * mm});
            skLineSegment(sketch, "E321.183", {"start": v(16963.5, 3800) * mm, "end": v(18660, 3800) * mm});
            skLineSegment(sketch, "E321.184", {"start": v(14973.57, 2800) * mm, "end": v(14973.57, 3750) * mm});
            skLineSegment(sketch, "E321.185", {"start": v(15810, 1150) * mm, "end": v(15048.57, 1150) * mm});
            skLineSegment(sketch, "E321.186", {"start": v(12173.22, 2750) * mm, "end": v(12173.22, 1150) * mm});
            skLineSegment(sketch, "E321.187", {"start": v(14212.14, 2800) * mm, "end": v(14212.14, 3750) * mm});
            skLineSegment(sketch, "E321.188", {"start": v(15860, 3800) * mm, "end": v(15860, 1100) * mm});
            skLineSegment(sketch, "E321.189", {"start": v(17849.25, 2750) * mm, "end": v(17849.25, 1150) * mm});
            skLineSegment(sketch, "E321.190", {"start": v(12173.22, 2800) * mm, "end": v(12173.22, 3750) * mm});
            skLineSegment(sketch, "E321.191", {"start": v(14973.57, 2750) * mm, "end": v(14973.57, 1150) * mm});
            skLineSegment(sketch, "E321.192", {"start": v(17849.25, 2800) * mm, "end": v(17849.25, 3750) * mm});
            skLineSegment(sketch, "E321.193", {"start": v(17774.25, 2800) * mm, "end": v(17774.25, 3750) * mm});
            skLineSegment(sketch, "E321.194", {"start": v(12248.22, 2800) * mm, "end": v(12248.22, 3750) * mm});
            skLineSegment(sketch, "E321.195", {"start": v(17774.25, 2750) * mm, "end": v(17774.25, 1150) * mm});
            skLineSegment(sketch, "E321.196", {"start": v(12248.22, 2750) * mm, "end": v(12248.22, 1150) * mm});
            skLineSegment(sketch, "E321.197", {"start": v(6410, 2800) * mm, "end": v(5648.57, 2800) * mm});
            skLineSegment(sketch, "E321.198", {"start": v(9210, 2800) * mm, "end": v(9210, 3750) * mm});
            skLineSegment(sketch, "E321.199", {"start": v(2011.44, 2800) * mm, "end": v(2011.44, 3750) * mm});
            skLineSegment(sketch, "E321.200", {"start": v(6410, 2750) * mm, "end": v(5648.57, 2750) * mm});
            skLineSegment(sketch, "E321.201", {"start": v(9210, 3750) * mm, "end": v(8449.25, 3750) * mm});
            skLineSegment(sketch, "E321.202", {"start": v(7613.5, 2750) * mm, "end": v(7613.5, 1150) * mm});
            skLineSegment(sketch, "E321.203", {"start": v(4812.14, 2800) * mm, "end": v(5573.57, 2800) * mm});
            skLineSegment(sketch, "E321.204", {"start": v(9210, 2800) * mm, "end": v(8449.25, 2800) * mm});
            skLineSegment(sketch, "E321.205", {"start": v(3660, 1100) * mm, "end": v(1961.44, 1100) * mm});
            skPoint(sketch, "E321.206", {"position": v(9260, 1200) * mm});
            skLineSegment(sketch, "E321.207", {"start": v(3610, 2800) * mm, "end": v(2848.22, 2800) * mm});
            skLineSegment(sketch, "E321.208", {"start": v(3610, 1150) * mm, "end": v(2848.22, 1150) * mm});
            skLineSegment(sketch, "E321.209", {"start": v(9260, 1100) * mm, "end": v(7563.5, 1100) * mm});
            skLineSegment(sketch, "E321.210", {"start": v(7613.5, 2750) * mm, "end": v(8374.25, 2750) * mm});
            skLineSegment(sketch, "E321.211", {"start": v(3610, 2750) * mm, "end": v(3610, 1150) * mm});
            skLineSegment(sketch, "E321.212", {"start": v(9210, 1150) * mm, "end": v(8449.25, 1150) * mm});
            skLineSegment(sketch, "E321.213", {"start": v(5648.57, 2750) * mm, "end": v(5648.57, 1150) * mm});
            skLineSegment(sketch, "E321.214", {"start": v(7563.5, 1100) * mm, "end": v(7563.5, 3800) * mm});
            skLineSegment(sketch, "E321.215", {"start": v(3610, 2750) * mm, "end": v(2848.22, 2750) * mm});
            skLineSegment(sketch, "E321.216", {"start": v(7613.5, 2800) * mm, "end": v(8374.25, 2800) * mm});
            skLineSegment(sketch, "E321.217", {"start": v(5648.57, 2800) * mm, "end": v(5648.57, 3750) * mm});
            skPoint(sketch, "E321.218", {"position": v(6460, 1200) * mm});
            skLineSegment(sketch, "E321.219", {"start": v(6410, 2800) * mm, "end": v(6410, 3750) * mm});
            skLineSegment(sketch, "E321.220", {"start": v(2011.44, 2750) * mm, "end": v(2011.44, 1150) * mm});
            skLineSegment(sketch, "E321.221", {"start": v(6410, 2750) * mm, "end": v(6410, 1150) * mm});
            skLineSegment(sketch, "E321.222", {"start": v(1961.44, 3800) * mm, "end": v(3660, 3800) * mm});
            skLineSegment(sketch, "E321.223", {"start": v(7613.5, 1150) * mm, "end": v(8374.25, 1150) * mm});
            skLineSegment(sketch, "E321.224", {"start": v(9210, 2750) * mm, "end": v(8449.25, 2750) * mm});
            skLineSegment(sketch, "E321.225", {"start": v(7613.5, 3750) * mm, "end": v(8374.25, 3750) * mm});
            skLineSegment(sketch, "E321.226", {"start": v(8411.75, 1100) * mm, "end": v(8411.75, 3700) * mm});
            skLineSegment(sketch, "E321.227", {"start": v(4762.14, 1100) * mm, "end": v(4762.14, 3800) * mm});
            skLineSegment(sketch, "E321.228", {"start": v(2011.44, 1150) * mm, "end": v(2773.22, 1150) * mm});
            skLineSegment(sketch, "E321.229", {"start": v(7613.5, 2800) * mm, "end": v(7613.5, 3750) * mm});
            skPoint(sketch, "E321.230", {"position": v(3660, 1200) * mm});
            skLineSegment(sketch, "E321.231", {"start": v(3610, 2800) * mm, "end": v(3610, 3750) * mm});
            skLineSegment(sketch, "E321.232", {"start": v(9260, 3800) * mm, "end": v(9260, 1100) * mm});
            skLineSegment(sketch, "E321.233", {"start": v(2810.72, 1100) * mm, "end": v(2810.72, 3700) * mm});
            skLineSegment(sketch, "E321.234", {"start": v(2011.44, 2750) * mm, "end": v(2773.22, 2750) * mm});
            skLineSegment(sketch, "E321.235", {"start": v(6410, 3750) * mm, "end": v(5648.57, 3750) * mm});
            skLineSegment(sketch, "E321.236", {"start": v(6460, 1100) * mm, "end": v(4762.14, 1100) * mm});
            skLineSegment(sketch, "E321.237", {"start": v(3660, 3800) * mm, "end": v(3660, 1100) * mm});
            skLineSegment(sketch, "E321.238", {"start": v(2011.44, 2800) * mm, "end": v(2773.22, 2800) * mm});
            skLineSegment(sketch, "E321.239", {"start": v(4812.14, 1150) * mm, "end": v(5573.57, 1150) * mm});
            skLineSegment(sketch, "E321.240", {"start": v(4762.14, 3800) * mm, "end": v(6460, 3800) * mm});
            skLineSegment(sketch, "E321.241", {"start": v(4812.14, 2750) * mm, "end": v(4812.14, 1150) * mm});
            skLineSegment(sketch, "E321.242", {"start": v(4812.14, 2750) * mm, "end": v(5573.57, 2750) * mm});
            skLineSegment(sketch, "E321.243", {"start": v(1961.44, 1100) * mm, "end": v(1961.44, 3800) * mm});
            skLineSegment(sketch, "E321.244", {"start": v(9210, 2750) * mm, "end": v(9210, 1150) * mm});
            skLineSegment(sketch, "E321.245", {"start": v(5611.07, 1100) * mm, "end": v(5611.07, 3700) * mm});
            skLineSegment(sketch, "E321.246", {"start": v(3610, 3750) * mm, "end": v(2848.22, 3750) * mm});
            skLineSegment(sketch, "E321.247", {"start": v(2011.44, 3750) * mm, "end": v(2773.22, 3750) * mm});
            skLineSegment(sketch, "E321.248", {"start": v(4812.14, 3750) * mm, "end": v(5573.57, 3750) * mm});
            skLineSegment(sketch, "E321.249", {"start": v(7563.5, 3800) * mm, "end": v(9260, 3800) * mm});
            skLineSegment(sketch, "E321.250", {"start": v(5573.57, 2800) * mm, "end": v(5573.57, 3750) * mm});
            skLineSegment(sketch, "E321.251", {"start": v(6410, 1150) * mm, "end": v(5648.57, 1150) * mm});
            skLineSegment(sketch, "E321.252", {"start": v(2773.22, 2750) * mm, "end": v(2773.22, 1150) * mm});
            skLineSegment(sketch, "E321.253", {"start": v(4812.14, 2800) * mm, "end": v(4812.14, 3750) * mm});
            skLineSegment(sketch, "E321.254", {"start": v(6460, 3800) * mm, "end": v(6460, 1100) * mm});
            skLineSegment(sketch, "E321.255", {"start": v(8449.25, 2750) * mm, "end": v(8449.25, 1150) * mm});
            skLineSegment(sketch, "E321.256", {"start": v(2773.22, 2800) * mm, "end": v(2773.22, 3750) * mm});
            skLineSegment(sketch, "E321.257", {"start": v(5573.57, 2750) * mm, "end": v(5573.57, 1150) * mm});
            skLineSegment(sketch, "E321.258", {"start": v(8449.25, 2800) * mm, "end": v(8449.25, 3750) * mm});
            skLineSegment(sketch, "E321.259", {"start": v(8374.25, 2800) * mm, "end": v(8374.25, 3750) * mm});
            skLineSegment(sketch, "E321.260", {"start": v(2848.22, 2800) * mm, "end": v(2848.22, 3750) * mm});
            skLineSegment(sketch, "E321.261", {"start": v(8374.25, 2750) * mm, "end": v(8374.25, 1150) * mm});
            skLineSegment(sketch, "E321.262", {"start": v(2848.22, 2750) * mm, "end": v(2848.22, 1150) * mm});
            skPoint(sketch, "E322", {"position": v(29660, 1100) * mm});
            skPoint(sketch, "E323", {"position": v(32460, 1100) * mm});
            skPoint(sketch, "E324", {"position": v(35260, 1100) * mm});
            skPoint(sketch, "E325.65", {"position": v(31356.5, 1200) * mm});
            skLineSegment(sketch, "E325.68", {"start": v(31356.5, 1100) * mm, "end": v(29660, 1100) * mm});
            skLineSegment(sketch, "E325.69", {"start": v(29660, 1100) * mm, "end": v(29660, 3800) * mm});
            skLineSegment(sketch, "E325.70", {"start": v(29660, 3800) * mm, "end": v(31356.5, 3800) * mm});
            skLineSegment(sketch, "E325.71", {"start": v(31356.5, 3800) * mm, "end": v(31356.5, 1100) * mm});
            skLineSegment(sketch, "E325.72", {"start": v(30508.25, 1100) * mm, "end": v(30508.25, 3700) * mm});
            skLineSegment(sketch, "E325.73", {"start": v(31306.5, 2750) * mm, "end": v(30545.75, 2750) * mm});
            skLineSegment(sketch, "E325.74", {"start": v(31306.5, 1150) * mm, "end": v(30545.75, 1150) * mm});
            skLineSegment(sketch, "E325.75", {"start": v(31306.5, 2750) * mm, "end": v(31306.5, 1150) * mm});
            skLineSegment(sketch, "E325.76", {"start": v(30545.75, 2750) * mm, "end": v(30545.75, 1150) * mm});
            skLineSegment(sketch, "E325.77", {"start": v(31306.5, 2800) * mm, "end": v(30545.75, 2800) * mm});
            skLineSegment(sketch, "E325.78", {"start": v(31306.5, 3750) * mm, "end": v(30545.75, 3750) * mm});
            skLineSegment(sketch, "E325.79", {"start": v(31306.5, 2800) * mm, "end": v(31306.5, 3750) * mm});
            skLineSegment(sketch, "E325.80", {"start": v(30545.75, 2800) * mm, "end": v(30545.75, 3750) * mm});
            skLineSegment(sketch, "E325.81", {"start": v(29710, 3750) * mm, "end": v(30470.75, 3750) * mm});
            skLineSegment(sketch, "E325.82", {"start": v(30470.75, 2800) * mm, "end": v(30470.75, 3750) * mm});
            skLineSegment(sketch, "E325.83", {"start": v(29710, 2800) * mm, "end": v(30470.75, 2800) * mm});
            skLineSegment(sketch, "E325.84", {"start": v(29710, 2800) * mm, "end": v(29710, 3750) * mm});
            skLineSegment(sketch, "E325.85", {"start": v(29710, 2750) * mm, "end": v(30470.75, 2750) * mm});
            skLineSegment(sketch, "E325.86", {"start": v(30470.75, 2750) * mm, "end": v(30470.75, 1150) * mm});
            skLineSegment(sketch, "E325.87", {"start": v(29710, 1150) * mm, "end": v(30470.75, 1150) * mm});
            skLineSegment(sketch, "E325.88", {"start": v(29710, 2750) * mm, "end": v(29710, 1150) * mm});
            skPoint(sketch, "E326.65", {"position": v(34156.5, 1200) * mm});
            skLineSegment(sketch, "E326.68", {"start": v(34156.5, 1100) * mm, "end": v(32460, 1100) * mm});
            skLineSegment(sketch, "E326.69", {"start": v(32460, 1100) * mm, "end": v(32460, 3800) * mm});
            skLineSegment(sketch, "E326.70", {"start": v(32460, 3800) * mm, "end": v(34156.5, 3800) * mm});
            skLineSegment(sketch, "E326.71", {"start": v(34156.5, 3800) * mm, "end": v(34156.5, 1100) * mm});
            skLineSegment(sketch, "E326.72", {"start": v(33308.24, 1100) * mm, "end": v(33308.24, 3700) * mm});
            skLineSegment(sketch, "E326.73", {"start": v(34106.5, 2750) * mm, "end": v(33345.74, 2750) * mm});
            skLineSegment(sketch, "E326.74", {"start": v(34106.5, 1150) * mm, "end": v(33345.74, 1150) * mm});
            skLineSegment(sketch, "E326.75", {"start": v(34106.5, 2750) * mm, "end": v(34106.5, 1150) * mm});
            skLineSegment(sketch, "E326.76", {"start": v(33345.74, 2750) * mm, "end": v(33345.74, 1150) * mm});
            skLineSegment(sketch, "E326.77", {"start": v(34106.5, 2800) * mm, "end": v(33345.74, 2800) * mm});
            skLineSegment(sketch, "E326.78", {"start": v(34106.5, 3750) * mm, "end": v(33345.74, 3750) * mm});
            skLineSegment(sketch, "E326.79", {"start": v(34106.5, 2800) * mm, "end": v(34106.5, 3750) * mm});
            skLineSegment(sketch, "E326.80", {"start": v(33345.74, 2800) * mm, "end": v(33345.74, 3750) * mm});
            skLineSegment(sketch, "E326.81", {"start": v(32510, 3750) * mm, "end": v(33270.74, 3750) * mm});
            skLineSegment(sketch, "E326.82", {"start": v(33270.74, 2800) * mm, "end": v(33270.74, 3750) * mm});
            skLineSegment(sketch, "E326.83", {"start": v(32510, 2800) * mm, "end": v(33270.74, 2800) * mm});
            skLineSegment(sketch, "E326.84", {"start": v(32510, 2800) * mm, "end": v(32510, 3750) * mm});
            skLineSegment(sketch, "E326.85", {"start": v(32510, 2750) * mm, "end": v(33270.74, 2750) * mm});
            skLineSegment(sketch, "E326.86", {"start": v(33270.74, 2750) * mm, "end": v(33270.74, 1150) * mm});
            skLineSegment(sketch, "E326.87", {"start": v(32510, 1150) * mm, "end": v(33270.74, 1150) * mm});
            skLineSegment(sketch, "E326.88", {"start": v(32510, 2750) * mm, "end": v(32510, 1150) * mm});
            skPoint(sketch, "E327.65", {"position": v(36956.5, 1200) * mm});
            skLineSegment(sketch, "E327.68", {"start": v(36956.49, 1100) * mm, "end": v(35260, 1100) * mm});
            skLineSegment(sketch, "E327.69", {"start": v(35260, 1100) * mm, "end": v(35260, 3800) * mm});
            skLineSegment(sketch, "E327.70", {"start": v(35260, 3800) * mm, "end": v(36956.49, 3800) * mm});
            skLineSegment(sketch, "E327.71", {"start": v(36956.49, 3800) * mm, "end": v(36956.49, 1100) * mm});
            skLineSegment(sketch, "E327.72", {"start": v(36108.24, 1100) * mm, "end": v(36108.24, 3700) * mm});
            skLineSegment(sketch, "E327.73", {"start": v(36906.49, 2750) * mm, "end": v(36145.74, 2750) * mm});
            skLineSegment(sketch, "E327.74", {"start": v(36906.49, 1150) * mm, "end": v(36145.74, 1150) * mm});
            skLineSegment(sketch, "E327.75", {"start": v(36906.49, 2750) * mm, "end": v(36906.49, 1150) * mm});
            skLineSegment(sketch, "E327.76", {"start": v(36145.74, 2750) * mm, "end": v(36145.74, 1150) * mm});
            skLineSegment(sketch, "E327.77", {"start": v(36906.49, 2800) * mm, "end": v(36145.74, 2800) * mm});
            skLineSegment(sketch, "E327.78", {"start": v(36906.49, 3750) * mm, "end": v(36145.74, 3750) * mm});
            skLineSegment(sketch, "E327.79", {"start": v(36906.49, 2800) * mm, "end": v(36906.49, 3750) * mm});
            skLineSegment(sketch, "E327.80", {"start": v(36145.74, 2800) * mm, "end": v(36145.74, 3750) * mm});
            skLineSegment(sketch, "E327.81", {"start": v(35310, 3750) * mm, "end": v(36070.74, 3750) * mm});
            skLineSegment(sketch, "E327.82", {"start": v(36070.74, 2800) * mm, "end": v(36070.74, 3750) * mm});
            skLineSegment(sketch, "E327.83", {"start": v(35310, 2800) * mm, "end": v(36070.74, 2800) * mm});
            skLineSegment(sketch, "E327.84", {"start": v(35310, 2800) * mm, "end": v(35310, 3750) * mm});
            skLineSegment(sketch, "E327.85", {"start": v(35310, 2750) * mm, "end": v(36070.74, 2750) * mm});
            skLineSegment(sketch, "E327.86", {"start": v(36070.74, 2750) * mm, "end": v(36070.74, 1150) * mm});
            skLineSegment(sketch, "E327.87", {"start": v(35310, 1150) * mm, "end": v(36070.74, 1150) * mm});
            skLineSegment(sketch, "E327.88", {"start": v(35310, 2750) * mm, "end": v(35310, 1150) * mm});
            skSolve(sketch);
        }
        {
            var Q0;
            Q0=qSketchRegion(id+"F30",true);
            extrude(context, id + "F31", {"entities" : qUnion([Q0]), "depth" : 50 * mm, "offsetDistance" : 25 * mm});
        }
        {
            var Q0;
            Q0=makeQuery(id+"F5.boolean.opBoolean","MERGE",FACE,{"derivedFrom":[makeQuery(id+"F3.boolean.opBoolean","COPY",FACE,{"derivedFrom":makeQuery(id+"F3.opExtrude","SWEPT_FACE",FACE,{"disambiguationData":[OSD([sQuery(id+"F2.wireOp",EDGE,"E19.9")])]})}),makeQuery(id+"F5.opExtrude","SWEPT_FACE",FACE,{"disambiguationData":[OSD([sQuery(id+"F4.wireOp",EDGE,"E34.0")])]})]});
            var sketch = newSketch(context, id + "F32", { "sketchPlane" : qUnion([Q0])});
            skLineSegment(sketch, "E328.bottom", {"start": v(27160, 2400) * mm, "end": v(28260, 2400) * mm});
            skLineSegment(sketch, "E328.top", {"start": v(27160, 0) * mm, "end": v(28260, 0) * mm});
            skLineSegment(sketch, "E328.left", {"start": v(27160, 2400) * mm, "end": v(27160, 0) * mm});
            skLineSegment(sketch, "E328.right", {"start": v(28260, 2400) * mm, "end": v(28260, 0) * mm});
            skLineSegment(sketch, "E329.bottom", {"start": v(23730, 3200) * mm, "end": v(24830, 3200) * mm});
            skLineSegment(sketch, "E329.top", {"start": v(23730, 1100) * mm, "end": v(24830, 1100) * mm});
            skLineSegment(sketch, "E329.left", {"start": v(23730, 3200) * mm, "end": v(23730, 1100) * mm});
            skLineSegment(sketch, "E329.right", {"start": v(24830, 3200) * mm, "end": v(24830, 1100) * mm});
            skLineSegment(sketch, "E330.bottom", {"start": v(20560, 3200) * mm, "end": v(19460, 3200) * mm});
            skLineSegment(sketch, "E330.top", {"start": v(20560, 1100) * mm, "end": v(19460, 1100) * mm});
            skLineSegment(sketch, "E330.left", {"start": v(20560, 3200) * mm, "end": v(20560, 1100) * mm});
            skLineSegment(sketch, "E330.right", {"start": v(19460, 3200) * mm, "end": v(19460, 1100) * mm});
            skLineSegment(sketch, "E331.bottom", {"start": v(16460, 3200) * mm, "end": v(15360, 3200) * mm});
            skLineSegment(sketch, "E331.top", {"start": v(16460, 1100) * mm, "end": v(15360, 1100) * mm});
            skLineSegment(sketch, "E331.left", {"start": v(16460, 3200) * mm, "end": v(16460, 1100) * mm});
            skLineSegment(sketch, "E331.right", {"start": v(15360, 3200) * mm, "end": v(15360, 1100) * mm});
            skLineSegment(sketch, "E332.bottom", {"start": v(12110, 3200) * mm, "end": v(11010, 3200) * mm});
            skLineSegment(sketch, "E332.top", {"start": v(12110, 1100) * mm, "end": v(11010, 1100) * mm});
            skLineSegment(sketch, "E332.left", {"start": v(12110, 3200) * mm, "end": v(12110, 1100) * mm});
            skLineSegment(sketch, "E332.right", {"start": v(11010, 3200) * mm, "end": v(11010, 1100) * mm});
            skLineSegment(sketch, "E333.bottom", {"start": v(6480, 3200) * mm, "end": v(5380, 3200) * mm});
            skLineSegment(sketch, "E333.top", {"start": v(6480, 1100) * mm, "end": v(5380, 1100) * mm});
            skLineSegment(sketch, "E333.left", {"start": v(6480, 3200) * mm, "end": v(6480, 1100) * mm});
            skLineSegment(sketch, "E333.right", {"start": v(5380, 3200) * mm, "end": v(5380, 1100) * mm});
            skLineSegment(sketch, "E334.bottom", {"start": v(860, 3800) * mm, "end": v(2660, 3800) * mm});
            skLineSegment(sketch, "E334.top", {"start": v(860, 1200) * mm, "end": v(2660, 1200) * mm});
            skLineSegment(sketch, "E334.left", {"start": v(860, 3800) * mm, "end": v(860, 1200) * mm});
            skLineSegment(sketch, "E334.right", {"start": v(2660, 3800) * mm, "end": v(2660, 1200) * mm});
            skSolve(sketch);
        }
        {
            var Q0;
            Q0=qSketchRegion(id+"F32",true);
            extrude(context, id + "F33", {"entities" : qUnion([Q0]), "operationType" : NewBodyOperationType.REMOVE, "oppositeDirection" : true, "depth" : 600 * mm, "offsetDistance" : 25 * mm});
        }
        {
            var Q0;
            Q0=makeQuery(id+"F1.opExtrude","SWEPT_FACE",FACE,{"disambiguationData":[OSD([sQuery(id+"F0.wireOp",EDGE,"E16.4")])]});
            var sketch = newSketch(context, id + "F34", { "sketchPlane" : qUnion([Q0])});
            skLineSegment(sketch, "E335.0", {"start": v(-27160, 2400) * mm, "end": v(-28260, 2400) * mm});
            skLineSegment(sketch, "E335.1", {"start": v(-27160, 0) * mm, "end": v(-28260, 0) * mm});
            skLineSegment(sketch, "E335.2", {"start": v(-27160, 2400) * mm, "end": v(-27160, 0) * mm});
            skLineSegment(sketch, "E335.3", {"start": v(-28260, 2400) * mm, "end": v(-28260, 0) * mm});
            skLineSegment(sketch, "E335.4", {"start": v(-23730, 3200) * mm, "end": v(-24830, 3200) * mm});
            skLineSegment(sketch, "E335.5", {"start": v(-23730, 1100) * mm, "end": v(-24830, 1100) * mm});
            skLineSegment(sketch, "E335.6", {"start": v(-23730, 3200) * mm, "end": v(-23730, 1100) * mm});
            skLineSegment(sketch, "E335.7", {"start": v(-24830, 3200) * mm, "end": v(-24830, 1100) * mm});
            skLineSegment(sketch, "E335.8", {"start": v(-20560, 3200) * mm, "end": v(-19460, 3200) * mm});
            skLineSegment(sketch, "E335.9", {"start": v(-20560, 1100) * mm, "end": v(-19460, 1100) * mm});
            skLineSegment(sketch, "E335.10", {"start": v(-20560, 3200) * mm, "end": v(-20560, 1100) * mm});
            skLineSegment(sketch, "E335.11", {"start": v(-19460, 3200) * mm, "end": v(-19460, 1100) * mm});
            skLineSegment(sketch, "E335.12", {"start": v(-16460, 3200) * mm, "end": v(-15360, 3200) * mm});
            skLineSegment(sketch, "E335.13", {"start": v(-16460, 1100) * mm, "end": v(-15360, 1100) * mm});
            skLineSegment(sketch, "E335.14", {"start": v(-16460, 3200) * mm, "end": v(-16460, 1100) * mm});
            skLineSegment(sketch, "E335.15", {"start": v(-15360, 3200) * mm, "end": v(-15360, 1100) * mm});
            skLineSegment(sketch, "E335.16", {"start": v(-12110, 3200) * mm, "end": v(-11010, 3200) * mm});
            skLineSegment(sketch, "E335.17", {"start": v(-12110, 1100) * mm, "end": v(-11010, 1100) * mm});
            skLineSegment(sketch, "E335.18", {"start": v(-12110, 3200) * mm, "end": v(-12110, 1100) * mm});
            skLineSegment(sketch, "E335.19", {"start": v(-11010, 3200) * mm, "end": v(-11010, 1100) * mm});
            skLineSegment(sketch, "E335.20", {"start": v(-6480, 3200) * mm, "end": v(-5380, 3200) * mm});
            skLineSegment(sketch, "E335.21", {"start": v(-6480, 1100) * mm, "end": v(-5380, 1100) * mm});
            skLineSegment(sketch, "E335.22", {"start": v(-6480, 3200) * mm, "end": v(-6480, 1100) * mm});
            skLineSegment(sketch, "E335.23", {"start": v(-5380, 3200) * mm, "end": v(-5380, 1100) * mm});
            skLineSegment(sketch, "E335.24", {"start": v(-860, 3800) * mm, "end": v(-2660, 3800) * mm});
            skLineSegment(sketch, "E335.25", {"start": v(-860, 1200) * mm, "end": v(-2660, 1200) * mm});
            skLineSegment(sketch, "E335.26", {"start": v(-860, 3800) * mm, "end": v(-860, 1200) * mm});
            skLineSegment(sketch, "E335.27", {"start": v(-2660, 3800) * mm, "end": v(-2660, 1200) * mm});
            skSolve(sketch);
        }
        {
            var Q0;
            Q0=qSketchRegion(id+"F34",true);
            extrude(context, id + "F35", {"entities" : qUnion([Q0]), "oppositeDirection" : true, "depth" : 100 * mm, "offsetDistance" : 25 * mm});
        }
        {
            var Q0;
            Q0=makeQuery(id+"F35.opExtrude","CAP_FACE",FACE,{"disambiguationData":[OSD([sQuery(id+"F34.wireOp",EDGE,"E335.0"),sQuery(id+"F34.wireOp",EDGE,"E335.1"),sQuery(id+"F34.wireOp",EDGE,"E335.2"),sQuery(id+"F34.wireOp",EDGE,"E335.3")])],"isStart":false});
            var sketch = newSketch(context, id + "F36", { "sketchPlane" : qUnion([Q0])});
            skLineSegment(sketch, "E336.0.0", {"start": v(27160, 0) * mm, "end": v(28260, 0) * mm});
            skLineSegment(sketch, "E336.0.1", {"start": v(28260, 0) * mm, "end": v(28260, 2400) * mm});
            skLineSegment(sketch, "E336.0.2", {"start": v(28260, 2400) * mm, "end": v(27160, 2400) * mm});
            skLineSegment(sketch, "E336.0.3", {"start": v(27160, 2400) * mm, "end": v(27160, 0) * mm});
            skLineSegment(sketch, "E337.0.0", {"start": v(860, 1200) * mm, "end": v(2660, 1200) * mm});
            skLineSegment(sketch, "E337.0.1", {"start": v(2660, 1200) * mm, "end": v(2660, 3800) * mm});
            skLineSegment(sketch, "E337.0.2", {"start": v(2660, 3800) * mm, "end": v(860, 3800) * mm});
            skLineSegment(sketch, "E337.0.3", {"start": v(860, 3800) * mm, "end": v(860, 1200) * mm});
            skLineSegment(sketch, "E338.0.0", {"start": v(5380, 1100) * mm, "end": v(6480, 1100) * mm});
            skLineSegment(sketch, "E338.0.1", {"start": v(6480, 1100) * mm, "end": v(6480, 3200) * mm});
            skLineSegment(sketch, "E338.0.2", {"start": v(6480, 3200) * mm, "end": v(5380, 3200) * mm});
            skLineSegment(sketch, "E338.0.3", {"start": v(5380, 3200) * mm, "end": v(5380, 1100) * mm});
            skLineSegment(sketch, "E339", {"start": v(1760, 3800) * mm, "end": v(1760, 1200) * mm, "construction": true});
            skLineSegment(sketch, "E340.bottom", {"start": v(910, 2850) * mm, "end": v(1722.5, 2850) * mm});
            skLineSegment(sketch, "E340.top", {"start": v(910, 1250) * mm, "end": v(1722.5, 1250) * mm});
            skLineSegment(sketch, "E340.left", {"start": v(910, 2850) * mm, "end": v(910, 1250) * mm});
            skLineSegment(sketch, "E340.right", {"start": v(1722.5, 2850) * mm, "end": v(1722.5, 1250) * mm});
            skLineSegment(sketch, "E341.bottom", {"start": v(910, 2900) * mm, "end": v(1722.5, 2900) * mm});
            skLineSegment(sketch, "E341.top", {"start": v(910, 3750) * mm, "end": v(1722.5, 3750) * mm});
            skLineSegment(sketch, "E341.left", {"start": v(910, 2900) * mm, "end": v(910, 3750) * mm});
            skLineSegment(sketch, "E341.right", {"start": v(1722.5, 2900) * mm, "end": v(1722.5, 3750) * mm});
            skLineSegment(sketch, "E342.MirrorCS", {"start": v(2610, 2850) * mm, "end": v(1797.5, 2850) * mm});
            skLineSegment(sketch, "E343.MirrorCS", {"start": v(1797.5, 2850) * mm, "end": v(1797.5, 1250) * mm});
            skLineSegment(sketch, "E344.MirrorCS", {"start": v(2610, 2850) * mm, "end": v(2610, 1250) * mm});
            skLineSegment(sketch, "E345.MirrorCS", {"start": v(2610, 1250) * mm, "end": v(1797.5, 1250) * mm});
            skLineSegment(sketch, "E346.MirrorCS", {"start": v(2610, 2900) * mm, "end": v(1797.5, 2900) * mm});
            skLineSegment(sketch, "E347.MirrorCS", {"start": v(1797.5, 2900) * mm, "end": v(1797.5, 3750) * mm});
            skLineSegment(sketch, "E348.MirrorCS", {"start": v(2610, 2900) * mm, "end": v(2610, 3750) * mm});
            skLineSegment(sketch, "E349.MirrorCS", {"start": v(2610, 3750) * mm, "end": v(1797.5, 3750) * mm});
            skLineSegment(sketch, "E350.0", {"start": v(27210, 2350) * mm, "end": v(27210, 50) * mm});
            skLineSegment(sketch, "E350.1", {"start": v(28210, 2350) * mm, "end": v(27210, 2350) * mm});
            skLineSegment(sketch, "E350.2", {"start": v(28210, 50) * mm, "end": v(28210, 2350) * mm});
            skLineSegment(sketch, "E350.3", {"start": v(27210, 50) * mm, "end": v(28210, 50) * mm});
            skLineSegment(sketch, "E351.bottom", {"start": v(5430, 2400) * mm, "end": v(6430, 2400) * mm});
            skLineSegment(sketch, "E351.top", {"start": v(5430, 1150) * mm, "end": v(6430, 1150) * mm});
            skLineSegment(sketch, "E351.left", {"start": v(5430, 2400) * mm, "end": v(5430, 1150) * mm});
            skLineSegment(sketch, "E351.right", {"start": v(6430, 2400) * mm, "end": v(6430, 1150) * mm});
            skLineSegment(sketch, "E352.bottom", {"start": v(5430, 2450) * mm, "end": v(6430, 2450) * mm});
            skLineSegment(sketch, "E352.top", {"start": v(5430, 3150) * mm, "end": v(6430, 3150) * mm});
            skLineSegment(sketch, "E352.left", {"start": v(5430, 2450) * mm, "end": v(5430, 3150) * mm});
            skLineSegment(sketch, "E352.right", {"start": v(6430, 2450) * mm, "end": v(6430, 3150) * mm});
            skPoint(sketch, "E353", {"position": v(10690, 1100) * mm});
            skPoint(sketch, "E354", {"position": v(15160, 1100) * mm});
            skPoint(sketch, "E355", {"position": v(19360, 1100) * mm});
            skPoint(sketch, "E356", {"position": v(23730, 1100) * mm});
            skLineSegment(sketch, "E357.0.0", {"start": v(11010, 1100) * mm, "end": v(12110, 1100) * mm});
            skLineSegment(sketch, "E357.0.1", {"start": v(12110, 1100) * mm, "end": v(12110, 3200) * mm});
            skLineSegment(sketch, "E357.0.2", {"start": v(12110, 3200) * mm, "end": v(11010, 3200) * mm});
            skLineSegment(sketch, "E357.0.3", {"start": v(11010, 3200) * mm, "end": v(11010, 1100) * mm});
            skLineSegment(sketch, "E358.bottom", {"start": v(11060, 2400) * mm, "end": v(12060, 2400) * mm});
            skLineSegment(sketch, "E358.top", {"start": v(11060, 1150) * mm, "end": v(12060, 1150) * mm});
            skLineSegment(sketch, "E358.left", {"start": v(11060, 2400) * mm, "end": v(11060, 1150) * mm});
            skLineSegment(sketch, "E358.right", {"start": v(12060, 2400) * mm, "end": v(12060, 1150) * mm});
            skLineSegment(sketch, "E359.bottom", {"start": v(11060, 2450) * mm, "end": v(12060, 2450) * mm});
            skLineSegment(sketch, "E359.top", {"start": v(11060, 3150) * mm, "end": v(12060, 3150) * mm});
            skLineSegment(sketch, "E359.left", {"start": v(11060, 2450) * mm, "end": v(11060, 3150) * mm});
            skLineSegment(sketch, "E359.right", {"start": v(12060, 2450) * mm, "end": v(12060, 3150) * mm});
            skLineSegment(sketch, "E360.0.0", {"start": v(15360, 1100) * mm, "end": v(16460, 1100) * mm});
            skLineSegment(sketch, "E360.0.1", {"start": v(16460, 1100) * mm, "end": v(16460, 3200) * mm});
            skLineSegment(sketch, "E360.0.2", {"start": v(16460, 3200) * mm, "end": v(15360, 3200) * mm});
            skLineSegment(sketch, "E360.0.3", {"start": v(15360, 3200) * mm, "end": v(15360, 1100) * mm});
            skLineSegment(sketch, "E361.bottom", {"start": v(15410, 2400) * mm, "end": v(16410, 2400) * mm});
            skLineSegment(sketch, "E361.top", {"start": v(15410, 1150) * mm, "end": v(16410, 1150) * mm});
            skLineSegment(sketch, "E361.left", {"start": v(15410, 2400) * mm, "end": v(15410, 1150) * mm});
            skLineSegment(sketch, "E361.right", {"start": v(16410, 2400) * mm, "end": v(16410, 1150) * mm});
            skLineSegment(sketch, "E362.bottom", {"start": v(15410, 2450) * mm, "end": v(16410, 2450) * mm});
            skLineSegment(sketch, "E362.top", {"start": v(15410, 3150) * mm, "end": v(16410, 3150) * mm});
            skLineSegment(sketch, "E362.left", {"start": v(15410, 2450) * mm, "end": v(15410, 3150) * mm});
            skLineSegment(sketch, "E362.right", {"start": v(16410, 2450) * mm, "end": v(16410, 3150) * mm});
            skLineSegment(sketch, "E363.0.0", {"start": v(19460, 1100) * mm, "end": v(20560, 1100) * mm});
            skLineSegment(sketch, "E363.0.1", {"start": v(20560, 1100) * mm, "end": v(20560, 3200) * mm});
            skLineSegment(sketch, "E363.0.2", {"start": v(20560, 3200) * mm, "end": v(19460, 3200) * mm});
            skLineSegment(sketch, "E363.0.3", {"start": v(19460, 3200) * mm, "end": v(19460, 1100) * mm});
            skLineSegment(sketch, "E364.bottom", {"start": v(19510, 2400) * mm, "end": v(20510, 2400) * mm});
            skLineSegment(sketch, "E364.top", {"start": v(19510, 1150) * mm, "end": v(20510, 1150) * mm});
            skLineSegment(sketch, "E364.left", {"start": v(19510, 2400) * mm, "end": v(19510, 1150) * mm});
            skLineSegment(sketch, "E364.right", {"start": v(20510, 2400) * mm, "end": v(20510, 1150) * mm});
            skLineSegment(sketch, "E365.bottom", {"start": v(19510, 2450) * mm, "end": v(20510, 2450) * mm});
            skLineSegment(sketch, "E365.top", {"start": v(19510, 3150) * mm, "end": v(20510, 3150) * mm});
            skLineSegment(sketch, "E365.left", {"start": v(19510, 2450) * mm, "end": v(19510, 3150) * mm});
            skLineSegment(sketch, "E365.right", {"start": v(20510, 2450) * mm, "end": v(20510, 3150) * mm});
            skLineSegment(sketch, "E366.0.0", {"start": v(23730, 1100) * mm, "end": v(24830, 1100) * mm});
            skLineSegment(sketch, "E366.0.1", {"start": v(24830, 1100) * mm, "end": v(24830, 3200) * mm});
            skLineSegment(sketch, "E366.0.2", {"start": v(24830, 3200) * mm, "end": v(23730, 3200) * mm});
            skLineSegment(sketch, "E366.0.3", {"start": v(23730, 3200) * mm, "end": v(23730, 1100) * mm});
            skLineSegment(sketch, "E367.bottom", {"start": v(23780, 2400) * mm, "end": v(24780, 2400) * mm});
            skLineSegment(sketch, "E367.top", {"start": v(23780, 1150) * mm, "end": v(24780, 1150) * mm});
            skLineSegment(sketch, "E367.left", {"start": v(23780, 2400) * mm, "end": v(23780, 1150) * mm});
            skLineSegment(sketch, "E367.right", {"start": v(24780, 2400) * mm, "end": v(24780, 1150) * mm});
            skLineSegment(sketch, "E368.bottom", {"start": v(23780, 2450) * mm, "end": v(24780, 2450) * mm});
            skLineSegment(sketch, "E368.top", {"start": v(23780, 3150) * mm, "end": v(24780, 3150) * mm});
            skLineSegment(sketch, "E368.left", {"start": v(23780, 2450) * mm, "end": v(23780, 3150) * mm});
            skLineSegment(sketch, "E368.right", {"start": v(24780, 2450) * mm, "end": v(24780, 3150) * mm});
            skSolve(sketch);
        }
        {
            var Q0;
            Q0=qSketchRegion(id+"F36",true);
            extrude(context, id + "F37", {"entities" : qUnion([Q0]), "depth" : 50 * mm, "offsetDistance" : 25 * mm});
        }
        {
            var Q0;
            Q0=makeQuery(id+"F5.boolean.opBoolean","MERGE",FACE,{"derivedFrom":[makeQuery(id+"F3.boolean.opBoolean","COPY",FACE,{"derivedFrom":makeQuery(id+"F3.opExtrude","SWEPT_FACE",FACE,{"disambiguationData":[OSD([sQuery(id+"F2.wireOp",EDGE,"E19.10")])]})}),makeQuery(id+"F5.opExtrude","SWEPT_FACE",FACE,{"disambiguationData":[OSD([sQuery(id+"F4.wireOp",EDGE,"E33.0")])]})]});
            var sketch = newSketch(context, id + "F38", { "sketchPlane" : qUnion([Q0])});
            skLineSegment(sketch, "E369.bottom", {"start": v(-24350, 3200) * mm, "end": v(-23350, 3200) * mm});
            skLineSegment(sketch, "E369.top", {"start": v(-24350, 1100) * mm, "end": v(-23350, 1100) * mm});
            skLineSegment(sketch, "E369.left", {"start": v(-24350, 3200) * mm, "end": v(-24350, 1100) * mm});
            skLineSegment(sketch, "E369.right", {"start": v(-23350, 3200) * mm, "end": v(-23350, 1100) * mm});
            skLineSegment(sketch, "E370.bottom", {"start": v(-21370, 3200) * mm, "end": v(-20370, 3200) * mm});
            skLineSegment(sketch, "E370.top", {"start": v(-21370, 1100) * mm, "end": v(-20370, 1100) * mm});
            skLineSegment(sketch, "E370.left", {"start": v(-21370, 3200) * mm, "end": v(-21370, 1100) * mm});
            skLineSegment(sketch, "E370.right", {"start": v(-20370, 3200) * mm, "end": v(-20370, 1100) * mm});
            skLineSegment(sketch, "E371.bottom", {"start": v(-18360, 3200) * mm, "end": v(-17360, 3200) * mm});
            skLineSegment(sketch, "E371.top", {"start": v(-18360, 1100) * mm, "end": v(-17360, 1100) * mm});
            skLineSegment(sketch, "E371.left", {"start": v(-18360, 3200) * mm, "end": v(-18360, 1100) * mm});
            skLineSegment(sketch, "E371.right", {"start": v(-17360, 3200) * mm, "end": v(-17360, 1100) * mm});
            skLineSegment(sketch, "E372.bottom", {"start": v(-15320, 3200) * mm, "end": v(-14320, 3200) * mm});
            skLineSegment(sketch, "E372.top", {"start": v(-15320, 1100) * mm, "end": v(-14320, 1100) * mm});
            skLineSegment(sketch, "E372.left", {"start": v(-15320, 3200) * mm, "end": v(-15320, 1100) * mm});
            skLineSegment(sketch, "E372.right", {"start": v(-14320, 3200) * mm, "end": v(-14320, 1100) * mm});
            skLineSegment(sketch, "E373.bottom", {"start": v(-12330, 3200) * mm, "end": v(-11330, 3200) * mm});
            skLineSegment(sketch, "E373.top", {"start": v(-12330, 1100) * mm, "end": v(-11330, 1100) * mm});
            skLineSegment(sketch, "E373.left", {"start": v(-12330, 3200) * mm, "end": v(-12330, 1100) * mm});
            skLineSegment(sketch, "E373.right", {"start": v(-11330, 3200) * mm, "end": v(-11330, 1100) * mm});
            skSolve(sketch);
        }
        {
            var Q0;
            Q0=qSketchRegion(id+"F38",true);
            extrude(context, id + "F39", {"entities" : qUnion([Q0]), "operationType" : NewBodyOperationType.REMOVE, "oppositeDirection" : true, "depth" : 600 * mm, "offsetDistance" : 25 * mm});
        }
        {
            var Q0;
            Q0=makeQuery(id+"F1.opExtrude","SWEPT_FACE",FACE,{"disambiguationData":[OSD([sQuery(id+"F0.wireOp",EDGE,"E16.3")])]});
            var sketch = newSketch(context, id + "F40", { "sketchPlane" : qUnion([Q0])});
            skLineSegment(sketch, "E374.0", {"start": v(24350, 3200) * mm, "end": v(23350, 3200) * mm});
            skLineSegment(sketch, "E374.1", {"start": v(24350, 1100) * mm, "end": v(23350, 1100) * mm});
            skLineSegment(sketch, "E374.2", {"start": v(24350, 3200) * mm, "end": v(24350, 1100) * mm});
            skLineSegment(sketch, "E374.3", {"start": v(23350, 3200) * mm, "end": v(23350, 1100) * mm});
            skLineSegment(sketch, "E374.4", {"start": v(21370, 3200) * mm, "end": v(20370, 3200) * mm});
            skLineSegment(sketch, "E374.5", {"start": v(21370, 1100) * mm, "end": v(20370, 1100) * mm});
            skLineSegment(sketch, "E374.6", {"start": v(21370, 3200) * mm, "end": v(21370, 1100) * mm});
            skLineSegment(sketch, "E374.7", {"start": v(20370, 3200) * mm, "end": v(20370, 1100) * mm});
            skLineSegment(sketch, "E374.8", {"start": v(18360, 3200) * mm, "end": v(17360, 3200) * mm});
            skLineSegment(sketch, "E374.9", {"start": v(18360, 1100) * mm, "end": v(17360, 1100) * mm});
            skLineSegment(sketch, "E374.10", {"start": v(18360, 3200) * mm, "end": v(18360, 1100) * mm});
            skLineSegment(sketch, "E374.11", {"start": v(17360, 3200) * mm, "end": v(17360, 1100) * mm});
            skLineSegment(sketch, "E374.12", {"start": v(15320, 3200) * mm, "end": v(14320, 3200) * mm});
            skLineSegment(sketch, "E374.13", {"start": v(15320, 1100) * mm, "end": v(14320, 1100) * mm});
            skLineSegment(sketch, "E374.14", {"start": v(15320, 3200) * mm, "end": v(15320, 1100) * mm});
            skLineSegment(sketch, "E374.15", {"start": v(14320, 3200) * mm, "end": v(14320, 1100) * mm});
            skLineSegment(sketch, "E374.16", {"start": v(12330, 3200) * mm, "end": v(11330, 3200) * mm});
            skLineSegment(sketch, "E374.17", {"start": v(12330, 1100) * mm, "end": v(11330, 1100) * mm});
            skLineSegment(sketch, "E374.18", {"start": v(12330, 3200) * mm, "end": v(12330, 1100) * mm});
            skLineSegment(sketch, "E374.19", {"start": v(11330, 3200) * mm, "end": v(11330, 1100) * mm});
            skSolve(sketch);
        }
        {
            var Q0;
            Q0=qSketchRegion(id+"F40",true);
            extrude(context, id + "F41", {"entities" : qUnion([Q0]), "oppositeDirection" : true, "depth" : 100 * mm, "offsetDistance" : 25 * mm});
        }
        {
            var Q0;
            Q0=makeQuery(id+"F41.opExtrude","CAP_FACE",FACE,{"disambiguationData":[OSD([sQuery(id+"F40.wireOp",EDGE,"E374.0"),sQuery(id+"F40.wireOp",EDGE,"E374.1"),sQuery(id+"F40.wireOp",EDGE,"E374.2"),sQuery(id+"F40.wireOp",EDGE,"E374.3")])],"isStart":false});
            var sketch = newSketch(context, id + "F42", { "sketchPlane" : qUnion([Q0])});
            skLineSegment(sketch, "E375.0.0", {"start": v(-24350, 1100) * mm, "end": v(-23350, 1100) * mm});
            skLineSegment(sketch, "E375.0.1", {"start": v(-23350, 1100) * mm, "end": v(-23350, 3200) * mm});
            skLineSegment(sketch, "E375.0.2", {"start": v(-23350, 3200) * mm, "end": v(-24350, 3200) * mm});
            skLineSegment(sketch, "E375.0.3", {"start": v(-24350, 3200) * mm, "end": v(-24350, 1100) * mm});
            skLineSegment(sketch, "E376.bottom", {"start": v(-24300, 2400) * mm, "end": v(-23400, 2400) * mm});
            skLineSegment(sketch, "E376.top", {"start": v(-24300, 1150) * mm, "end": v(-23400, 1150) * mm});
            skLineSegment(sketch, "E376.left", {"start": v(-24300, 2400) * mm, "end": v(-24300, 1150) * mm});
            skLineSegment(sketch, "E376.right", {"start": v(-23400, 2400) * mm, "end": v(-23400, 1150) * mm});
            skLineSegment(sketch, "E377.bottom", {"start": v(-24300, 2450) * mm, "end": v(-23400, 2450) * mm});
            skLineSegment(sketch, "E377.top", {"start": v(-24300, 3150) * mm, "end": v(-23400, 3150) * mm});
            skLineSegment(sketch, "E377.left", {"start": v(-24300, 2450) * mm, "end": v(-24300, 3150) * mm});
            skLineSegment(sketch, "E377.right", {"start": v(-23400, 2450) * mm, "end": v(-23400, 3150) * mm});
            skPoint(sketch, "E378", {"position": v(-24350, 1191.67) * mm});
            skPoint(sketch, "E379", {"position": v(-21370, 1100) * mm});
            skPoint(sketch, "E380", {"position": v(-18360, 1100) * mm});
            skPoint(sketch, "E381", {"position": v(-15320, 1100) * mm});
            skPoint(sketch, "E382", {"position": v(-12330, 1100) * mm});
            skLineSegment(sketch, "E383.0.0", {"start": v(-21370, 1100) * mm, "end": v(-20370, 1100) * mm});
            skLineSegment(sketch, "E383.0.1", {"start": v(-20370, 1100) * mm, "end": v(-20370, 3200) * mm});
            skLineSegment(sketch, "E383.0.2", {"start": v(-20370, 3200) * mm, "end": v(-21370, 3200) * mm});
            skLineSegment(sketch, "E383.0.3", {"start": v(-21370, 3200) * mm, "end": v(-21370, 1100) * mm});
            skLineSegment(sketch, "E384.bottom", {"start": v(-21320, 2400) * mm, "end": v(-20420, 2400) * mm});
            skLineSegment(sketch, "E384.top", {"start": v(-21320, 1150) * mm, "end": v(-20420, 1150) * mm});
            skLineSegment(sketch, "E384.left", {"start": v(-21320, 2400) * mm, "end": v(-21320, 1150) * mm});
            skLineSegment(sketch, "E384.right", {"start": v(-20420, 2400) * mm, "end": v(-20420, 1150) * mm});
            skLineSegment(sketch, "E385.bottom", {"start": v(-21320, 2450) * mm, "end": v(-20420, 2450) * mm});
            skLineSegment(sketch, "E385.top", {"start": v(-21320, 3150) * mm, "end": v(-20420, 3150) * mm});
            skLineSegment(sketch, "E385.left", {"start": v(-21320, 2450) * mm, "end": v(-21320, 3150) * mm});
            skLineSegment(sketch, "E385.right", {"start": v(-20420, 2450) * mm, "end": v(-20420, 3150) * mm});
            skLineSegment(sketch, "E386.0.0", {"start": v(-18360, 1100) * mm, "end": v(-17360, 1100) * mm});
            skLineSegment(sketch, "E386.0.1", {"start": v(-17360, 1100) * mm, "end": v(-17360, 3200) * mm});
            skLineSegment(sketch, "E386.0.2", {"start": v(-17360, 3200) * mm, "end": v(-18360, 3200) * mm});
            skLineSegment(sketch, "E386.0.3", {"start": v(-18360, 3200) * mm, "end": v(-18360, 1100) * mm});
            skLineSegment(sketch, "E387.bottom", {"start": v(-18310, 2400) * mm, "end": v(-17410, 2400) * mm});
            skLineSegment(sketch, "E387.top", {"start": v(-18310, 1150) * mm, "end": v(-17410, 1150) * mm});
            skLineSegment(sketch, "E387.left", {"start": v(-18310, 2400) * mm, "end": v(-18310, 1150) * mm});
            skLineSegment(sketch, "E387.right", {"start": v(-17410, 2400) * mm, "end": v(-17410, 1150) * mm});
            skLineSegment(sketch, "E388.bottom", {"start": v(-18310, 2450) * mm, "end": v(-17410, 2450) * mm});
            skLineSegment(sketch, "E388.top", {"start": v(-18310, 3150) * mm, "end": v(-17410, 3150) * mm});
            skLineSegment(sketch, "E388.left", {"start": v(-18310, 2450) * mm, "end": v(-18310, 3150) * mm});
            skLineSegment(sketch, "E388.right", {"start": v(-17410, 2450) * mm, "end": v(-17410, 3150) * mm});
            skLineSegment(sketch, "E389.0.0", {"start": v(-15320, 1100) * mm, "end": v(-14320, 1100) * mm});
            skLineSegment(sketch, "E389.0.1", {"start": v(-14320, 1100) * mm, "end": v(-14320, 3200) * mm});
            skLineSegment(sketch, "E389.0.2", {"start": v(-14320, 3200) * mm, "end": v(-15320, 3200) * mm});
            skLineSegment(sketch, "E389.0.3", {"start": v(-15320, 3200) * mm, "end": v(-15320, 1100) * mm});
            skLineSegment(sketch, "E390.bottom", {"start": v(-15270, 2400) * mm, "end": v(-14370, 2400) * mm});
            skLineSegment(sketch, "E390.top", {"start": v(-15270, 1150) * mm, "end": v(-14370, 1150) * mm});
            skLineSegment(sketch, "E390.left", {"start": v(-15270, 2400) * mm, "end": v(-15270, 1150) * mm});
            skLineSegment(sketch, "E390.right", {"start": v(-14370, 2400) * mm, "end": v(-14370, 1150) * mm});
            skLineSegment(sketch, "E391.bottom", {"start": v(-15270, 2450) * mm, "end": v(-14370, 2450) * mm});
            skLineSegment(sketch, "E391.top", {"start": v(-15270, 3150) * mm, "end": v(-14370, 3150) * mm});
            skLineSegment(sketch, "E391.left", {"start": v(-15270, 2450) * mm, "end": v(-15270, 3150) * mm});
            skLineSegment(sketch, "E391.right", {"start": v(-14370, 2450) * mm, "end": v(-14370, 3150) * mm});
            skLineSegment(sketch, "E392.0.0", {"start": v(-12330, 1100) * mm, "end": v(-11330, 1100) * mm});
            skLineSegment(sketch, "E392.0.1", {"start": v(-11330, 1100) * mm, "end": v(-11330, 3200) * mm});
            skLineSegment(sketch, "E392.0.2", {"start": v(-11330, 3200) * mm, "end": v(-12330, 3200) * mm});
            skLineSegment(sketch, "E392.0.3", {"start": v(-12330, 3200) * mm, "end": v(-12330, 1100) * mm});
            skLineSegment(sketch, "E393.bottom", {"start": v(-12280, 2400) * mm, "end": v(-11380, 2400) * mm});
            skLineSegment(sketch, "E393.top", {"start": v(-12280, 1150) * mm, "end": v(-11380, 1150) * mm});
            skLineSegment(sketch, "E393.left", {"start": v(-12280, 2400) * mm, "end": v(-12280, 1150) * mm});
            skLineSegment(sketch, "E393.right", {"start": v(-11380, 2400) * mm, "end": v(-11380, 1150) * mm});
            skLineSegment(sketch, "E394.bottom", {"start": v(-12280, 2450) * mm, "end": v(-11380, 2450) * mm});
            skLineSegment(sketch, "E394.top", {"start": v(-12280, 3150) * mm, "end": v(-11380, 3150) * mm});
            skLineSegment(sketch, "E394.left", {"start": v(-12280, 2450) * mm, "end": v(-12280, 3150) * mm});
            skLineSegment(sketch, "E394.right", {"start": v(-11380, 2450) * mm, "end": v(-11380, 3150) * mm});
            skSolve(sketch);
        }
        {
            var Q0;
            Q0=qSketchRegion(id+"F42",true);
            extrude(context, id + "F43", {"entities" : qUnion([Q0]), "depth" : 50 * mm, "offsetDistance" : 25 * mm});
        }
        {
            var Q0;
            Q0=makeQuery(id+"F5.boolean.opBoolean","MERGE",FACE,{"derivedFrom":[makeQuery(id+"F3.boolean.opBoolean","COPY",FACE,{"derivedFrom":makeQuery(id+"F3.opExtrude","SWEPT_FACE",FACE,{"disambiguationData":[OSD([sQuery(id+"F2.wireOp",EDGE,"E19.11")])]})}),makeQuery(id+"F5.opExtrude","SWEPT_FACE",FACE,{"disambiguationData":[OSD([sQuery(id+"F4.wireOp",EDGE,"E32.0")])]})]});
            var sketch = newSketch(context, id + "F44", { "sketchPlane" : qUnion([Q0])});
            skLineSegment(sketch, "E395.bottom", {"start": v(-28360, 2300) * mm, "end": v(-27260, 2300) * mm});
            skLineSegment(sketch, "E395.top", {"start": v(-28360, 0) * mm, "end": v(-27260, 0) * mm});
            skLineSegment(sketch, "E395.left", {"start": v(-28360, 2300) * mm, "end": v(-28360, 0) * mm});
            skLineSegment(sketch, "E395.right", {"start": v(-27260, 2300) * mm, "end": v(-27260, 0) * mm});
            skLineSegment(sketch, "E396.bottom", {"start": v(-25660, 3200) * mm, "end": v(-24660, 3200) * mm});
            skLineSegment(sketch, "E396.top", {"start": v(-25660, 1100) * mm, "end": v(-24660, 1100) * mm});
            skLineSegment(sketch, "E396.left", {"start": v(-25660, 3200) * mm, "end": v(-25660, 1100) * mm});
            skLineSegment(sketch, "E396.right", {"start": v(-24660, 3200) * mm, "end": v(-24660, 1100) * mm});
            skLineSegment(sketch, "E397.bottom", {"start": v(-22100, 3200) * mm, "end": v(-21100, 3200) * mm});
            skLineSegment(sketch, "E397.top", {"start": v(-22100, 1100) * mm, "end": v(-21100, 1100) * mm});
            skLineSegment(sketch, "E397.left", {"start": v(-22100, 3200) * mm, "end": v(-22100, 1100) * mm});
            skLineSegment(sketch, "E397.right", {"start": v(-21100, 3200) * mm, "end": v(-21100, 1100) * mm});
            skLineSegment(sketch, "E398.0", {"start": v(-16960, 3800) * mm, "end": v(-18660, 3800) * mm});
            skLineSegment(sketch, "E399.0", {"start": v(-16960, 1100) * mm, "end": v(-16960, 3800) * mm});
            skLineSegment(sketch, "E400.0", {"start": v(-16960, 1100) * mm, "end": v(-18660, 1100) * mm});
            skLineSegment(sketch, "E401.0", {"start": v(-18660, 1100) * mm, "end": v(-18660, 3800) * mm});
            skLineSegment(sketch, "E402.0", {"start": v(-14160, 3800) * mm, "end": v(-15860, 3800) * mm});
            skLineSegment(sketch, "E403.0", {"start": v(-14160, 1100) * mm, "end": v(-14160, 3800) * mm});
            skLineSegment(sketch, "E404.0", {"start": v(-14160, 1100) * mm, "end": v(-15860, 1100) * mm});
            skLineSegment(sketch, "E405.0", {"start": v(-15860, 1100) * mm, "end": v(-15860, 3800) * mm});
            skLineSegment(sketch, "E406.0", {"start": v(-11360, 3800) * mm, "end": v(-13060, 3800) * mm});
            skLineSegment(sketch, "E407.0", {"start": v(-11360, 1100) * mm, "end": v(-11360, 3800) * mm});
            skLineSegment(sketch, "E408.0", {"start": v(-11360, 1100) * mm, "end": v(-13060, 1100) * mm});
            skLineSegment(sketch, "E409.0", {"start": v(-13060, 1100) * mm, "end": v(-13060, 3800) * mm});
            skLineSegment(sketch, "E410.bottom", {"start": v(-4770, 3800) * mm, "end": v(-3070, 3800) * mm});
            skLineSegment(sketch, "E410.top", {"start": v(-4770, 1200) * mm, "end": v(-3070, 1200) * mm});
            skLineSegment(sketch, "E410.left", {"start": v(-4770, 3800) * mm, "end": v(-4770, 1200) * mm});
            skLineSegment(sketch, "E410.right", {"start": v(-3070, 3800) * mm, "end": v(-3070, 1200) * mm});
            skSolve(sketch);
        }
        {
            var Q0;
            Q0=qSketchRegion(id+"F44",true);
            extrude(context, id + "F45", {"entities" : qUnion([Q0]), "operationType" : NewBodyOperationType.REMOVE, "oppositeDirection" : true, "depth" : 600 * mm, "offsetDistance" : 25 * mm});
        }
        {
            var Q0;
            Q0=makeQuery(id+"F1.opExtrude","SWEPT_FACE",FACE,{"disambiguationData":[OSD([sQuery(id+"F0.wireOp",EDGE,"E16.2")])]});
            var sketch = newSketch(context, id + "F46", { "sketchPlane" : qUnion([Q0])});
            skLineSegment(sketch, "E411.0", {"start": v(28360, 2300) * mm, "end": v(27260, 2300) * mm});
            skLineSegment(sketch, "E411.1", {"start": v(28360, 0) * mm, "end": v(27260, 0) * mm});
            skLineSegment(sketch, "E411.2", {"start": v(28360, 2300) * mm, "end": v(28360, 0) * mm});
            skLineSegment(sketch, "E411.3", {"start": v(27260, 2300) * mm, "end": v(27260, 0) * mm});
            skLineSegment(sketch, "E411.4", {"start": v(25660, 3200) * mm, "end": v(24660, 3200) * mm});
            skLineSegment(sketch, "E411.5", {"start": v(25660, 1100) * mm, "end": v(24660, 1100) * mm});
            skLineSegment(sketch, "E411.6", {"start": v(25660, 3200) * mm, "end": v(25660, 1100) * mm});
            skLineSegment(sketch, "E411.7", {"start": v(24660, 3200) * mm, "end": v(24660, 1100) * mm});
            skLineSegment(sketch, "E411.8", {"start": v(22100, 3200) * mm, "end": v(21100, 3200) * mm});
            skLineSegment(sketch, "E411.9", {"start": v(22100, 1100) * mm, "end": v(21100, 1100) * mm});
            skLineSegment(sketch, "E411.10", {"start": v(22100, 3200) * mm, "end": v(22100, 1100) * mm});
            skLineSegment(sketch, "E411.11", {"start": v(21100, 3200) * mm, "end": v(21100, 1100) * mm});
            skLineSegment(sketch, "E411.12", {"start": v(16960, 3800) * mm, "end": v(18660, 3800) * mm});
            skLineSegment(sketch, "E411.13", {"start": v(16960, 1100) * mm, "end": v(16960, 3800) * mm});
            skLineSegment(sketch, "E411.14", {"start": v(16960, 1100) * mm, "end": v(18660, 1100) * mm});
            skLineSegment(sketch, "E411.15", {"start": v(18660, 1100) * mm, "end": v(18660, 3800) * mm});
            skLineSegment(sketch, "E411.16", {"start": v(14160, 3800) * mm, "end": v(15860, 3800) * mm});
            skLineSegment(sketch, "E411.17", {"start": v(14160, 1100) * mm, "end": v(14160, 3800) * mm});
            skLineSegment(sketch, "E411.18", {"start": v(14160, 1100) * mm, "end": v(15860, 1100) * mm});
            skLineSegment(sketch, "E411.19", {"start": v(15860, 1100) * mm, "end": v(15860, 3800) * mm});
            skLineSegment(sketch, "E411.20", {"start": v(11360, 3800) * mm, "end": v(13060, 3800) * mm});
            skLineSegment(sketch, "E411.21", {"start": v(11360, 1100) * mm, "end": v(11360, 3800) * mm});
            skLineSegment(sketch, "E411.22", {"start": v(11360, 1100) * mm, "end": v(13060, 1100) * mm});
            skLineSegment(sketch, "E411.23", {"start": v(13060, 1100) * mm, "end": v(13060, 3800) * mm});
            skLineSegment(sketch, "E411.28", {"start": v(4770, 3800) * mm, "end": v(3070, 3800) * mm});
            skLineSegment(sketch, "E411.29", {"start": v(4770, 1200) * mm, "end": v(3070, 1200) * mm});
            skLineSegment(sketch, "E411.30", {"start": v(4770, 3800) * mm, "end": v(4770, 1200) * mm});
            skLineSegment(sketch, "E411.31", {"start": v(3070, 3800) * mm, "end": v(3070, 1200) * mm});
            skSolve(sketch);
        }
        {
            var Q0;
            Q0=qSketchRegion(id+"F46",true);
            extrude(context, id + "F47", {"entities" : qUnion([Q0]), "oppositeDirection" : true, "depth" : 100 * mm, "offsetDistance" : 25 * mm});
        }
        {
            var Q0;
            Q0=makeQuery(id+"F47.opExtrude","CAP_FACE",FACE,{"disambiguationData":[OSD([sQuery(id+"F46.wireOp",EDGE,"E411.4"),sQuery(id+"F46.wireOp",EDGE,"E411.5"),sQuery(id+"F46.wireOp",EDGE,"E411.6"),sQuery(id+"F46.wireOp",EDGE,"E411.7")])],"isStart":false});
            var sketch = newSketch(context, id + "F48", { "sketchPlane" : qUnion([Q0])});
            skLineSegment(sketch, "E412.0.0", {"start": v(-25660, 1100) * mm, "end": v(-24660, 1100) * mm});
            skLineSegment(sketch, "E412.0.1", {"start": v(-24660, 1100) * mm, "end": v(-24660, 3200) * mm});
            skLineSegment(sketch, "E412.0.2", {"start": v(-24660, 3200) * mm, "end": v(-25660, 3200) * mm});
            skLineSegment(sketch, "E412.0.3", {"start": v(-25660, 3200) * mm, "end": v(-25660, 1100) * mm});
            skLineSegment(sketch, "E413.bottom", {"start": v(-25610, 2400) * mm, "end": v(-24710, 2400) * mm});
            skLineSegment(sketch, "E413.top", {"start": v(-25610, 1150) * mm, "end": v(-24710, 1150) * mm});
            skLineSegment(sketch, "E413.left", {"start": v(-25610, 2400) * mm, "end": v(-25610, 1150) * mm});
            skLineSegment(sketch, "E413.right", {"start": v(-24710, 2400) * mm, "end": v(-24710, 1150) * mm});
            skLineSegment(sketch, "E414.bottom", {"start": v(-25610, 2450) * mm, "end": v(-24710, 2450) * mm});
            skLineSegment(sketch, "E414.top", {"start": v(-25610, 3150) * mm, "end": v(-24710, 3150) * mm});
            skLineSegment(sketch, "E414.left", {"start": v(-25610, 2450) * mm, "end": v(-25610, 3150) * mm});
            skLineSegment(sketch, "E414.right", {"start": v(-24710, 2450) * mm, "end": v(-24710, 3150) * mm});
            skLineSegment(sketch, "E415.0.0", {"start": v(-22100, 1100) * mm, "end": v(-21100, 1100) * mm});
            skLineSegment(sketch, "E415.0.1", {"start": v(-21100, 1100) * mm, "end": v(-21100, 3200) * mm});
            skLineSegment(sketch, "E415.0.2", {"start": v(-21100, 3200) * mm, "end": v(-22100, 3200) * mm});
            skLineSegment(sketch, "E415.0.3", {"start": v(-22100, 3200) * mm, "end": v(-22100, 1100) * mm});
            skLineSegment(sketch, "E416.bottom", {"start": v(-22050, 2400) * mm, "end": v(-21150, 2400) * mm});
            skLineSegment(sketch, "E416.top", {"start": v(-22050, 1150) * mm, "end": v(-21150, 1150) * mm});
            skLineSegment(sketch, "E416.left", {"start": v(-22050, 2400) * mm, "end": v(-22050, 1150) * mm});
            skLineSegment(sketch, "E416.right", {"start": v(-21150, 2400) * mm, "end": v(-21150, 1150) * mm});
            skLineSegment(sketch, "E417.bottom", {"start": v(-22050, 2450) * mm, "end": v(-21150, 2450) * mm});
            skLineSegment(sketch, "E417.top", {"start": v(-22050, 3150) * mm, "end": v(-21150, 3150) * mm});
            skLineSegment(sketch, "E417.left", {"start": v(-22050, 2450) * mm, "end": v(-22050, 3150) * mm});
            skLineSegment(sketch, "E417.right", {"start": v(-21150, 2450) * mm, "end": v(-21150, 3150) * mm});
            skPoint(sketch, "E418", {"position": v(-22100, 1100) * mm});
            skLineSegment(sketch, "E419.0.0", {"start": v(-28360, 0) * mm, "end": v(-27260, 0) * mm});
            skLineSegment(sketch, "E419.0.1", {"start": v(-27260, 0) * mm, "end": v(-27260, 2300) * mm});
            skLineSegment(sketch, "E419.0.2", {"start": v(-27260, 2300) * mm, "end": v(-28360, 2300) * mm});
            skLineSegment(sketch, "E419.0.3", {"start": v(-28360, 2300) * mm, "end": v(-28360, 0) * mm});
            skLineSegment(sketch, "E420.0", {"start": v(-28310, 50) * mm, "end": v(-27310, 50) * mm});
            skLineSegment(sketch, "E420.1", {"start": v(-28310, 2250) * mm, "end": v(-28310, 50) * mm});
            skLineSegment(sketch, "E420.2", {"start": v(-27310, 2250) * mm, "end": v(-28310, 2250) * mm});
            skLineSegment(sketch, "E420.3", {"start": v(-27310, 50) * mm, "end": v(-27310, 2250) * mm});
            skPoint(sketch, "E421", {"position": v(-18660, 1100) * mm});
            skLineSegment(sketch, "E422.2.0.2", {"start": v(-17010, 2900) * mm, "end": v(-17010, 3750) * mm});
            skLineSegment(sketch, "E422.2.0.8", {"start": v(-18660, 1100) * mm, "end": v(-16960, 1100) * mm});
            skLineSegment(sketch, "E422.2.0.10", {"start": v(-18610, 2900) * mm, "end": v(-17847.5, 2900) * mm});
            skLineSegment(sketch, "E422.2.0.11", {"start": v(-18610, 1150) * mm, "end": v(-17847.5, 1150) * mm});
            skLineSegment(sketch, "E422.2.0.14", {"start": v(-18610, 2850) * mm, "end": v(-18610, 1150) * mm});
            skLineSegment(sketch, "E422.2.0.18", {"start": v(-18610, 2850) * mm, "end": v(-17847.5, 2850) * mm});
            skLineSegment(sketch, "E422.2.0.23", {"start": v(-17010, 2850) * mm, "end": v(-17010, 1150) * mm});
            skLineSegment(sketch, "E422.2.0.25", {"start": v(-16960, 3800) * mm, "end": v(-18660, 3800) * mm});
            skLineSegment(sketch, "E422.2.0.31", {"start": v(-17010, 1150) * mm, "end": v(-17772.5, 1150) * mm});
            skLineSegment(sketch, "E422.2.0.34", {"start": v(-18610, 2900) * mm, "end": v(-18610, 3750) * mm});
            skLineSegment(sketch, "E422.2.0.36", {"start": v(-17810, 1200) * mm, "end": v(-17810, 3800) * mm, "construction": true});
            skLineSegment(sketch, "E422.2.0.37", {"start": v(-17010, 2850) * mm, "end": v(-17772.5, 2850) * mm});
            skLineSegment(sketch, "E422.2.0.40", {"start": v(-18660, 3800) * mm, "end": v(-18660, 1100) * mm});
            skLineSegment(sketch, "E422.2.0.41", {"start": v(-17010, 2900) * mm, "end": v(-17772.5, 2900) * mm});
            skLineSegment(sketch, "E422.2.0.46", {"start": v(-16960, 1100) * mm, "end": v(-16960, 3800) * mm});
            skLineSegment(sketch, "E422.2.0.49", {"start": v(-18610, 3750) * mm, "end": v(-17847.5, 3750) * mm});
            skLineSegment(sketch, "E422.2.0.50", {"start": v(-17010, 3750) * mm, "end": v(-17772.5, 3750) * mm});
            skLineSegment(sketch, "E422.2.0.55", {"start": v(-17772.5, 2850) * mm, "end": v(-17772.5, 1150) * mm});
            skLineSegment(sketch, "E422.2.0.59", {"start": v(-17772.5, 2900) * mm, "end": v(-17772.5, 3750) * mm});
            skLineSegment(sketch, "E422.2.0.63", {"start": v(-17847.5, 2900) * mm, "end": v(-17847.5, 3750) * mm});
            skLineSegment(sketch, "E422.2.0.65", {"start": v(-17847.5, 2850) * mm, "end": v(-17847.5, 1150) * mm});
            skPoint(sketch, "E423", {"position": v(-4920, 1200) * mm});
            skLineSegment(sketch, "E424.2.0.2", {"start": v(-3120, 2900) * mm, "end": v(-3120, 3750) * mm});
            skLineSegment(sketch, "E424.2.0.8", {"start": v(-4770, 1200) * mm, "end": v(-3070, 1200) * mm});
            skLineSegment(sketch, "E424.2.0.10", {"start": v(-4720, 2900) * mm, "end": v(-3957.5, 2900) * mm});
            skLineSegment(sketch, "E424.2.0.11", {"start": v(-4720, 1250) * mm, "end": v(-3957.5, 1250) * mm});
            skLineSegment(sketch, "E424.2.0.14", {"start": v(-4720, 2850) * mm, "end": v(-4720, 1250) * mm});
            skLineSegment(sketch, "E424.2.0.18", {"start": v(-4720, 2850) * mm, "end": v(-3957.5, 2850) * mm});
            skLineSegment(sketch, "E424.2.0.23", {"start": v(-3120, 2850) * mm, "end": v(-3120, 1250) * mm});
            skLineSegment(sketch, "E424.2.0.25", {"start": v(-3070, 3800) * mm, "end": v(-4770, 3800) * mm});
            skLineSegment(sketch, "E424.2.0.31", {"start": v(-3120, 1250) * mm, "end": v(-3882.5, 1250) * mm});
            skPoint(sketch, "E424.2.0.33", {"position": v(-4770, 1100) * mm});
            skLineSegment(sketch, "E424.2.0.34", {"start": v(-4720, 2900) * mm, "end": v(-4720, 3750) * mm});
            skLineSegment(sketch, "E424.2.0.36", {"start": v(-3920, 1200) * mm, "end": v(-3920, 3800) * mm, "construction": true});
            skLineSegment(sketch, "E424.2.0.37", {"start": v(-3120, 2850) * mm, "end": v(-3882.5, 2850) * mm});
            skLineSegment(sketch, "E424.2.0.40", {"start": v(-4770, 3800) * mm, "end": v(-4770, 1200) * mm});
            skLineSegment(sketch, "E424.2.0.41", {"start": v(-3120, 2900) * mm, "end": v(-3882.5, 2900) * mm});
            skLineSegment(sketch, "E424.2.0.46", {"start": v(-3070, 1200) * mm, "end": v(-3070, 3800) * mm});
            skLineSegment(sketch, "E424.2.0.49", {"start": v(-4720, 3750) * mm, "end": v(-3957.5, 3750) * mm});
            skLineSegment(sketch, "E424.2.0.50", {"start": v(-3120, 3750) * mm, "end": v(-3882.5, 3750) * mm});
            skLineSegment(sketch, "E424.2.0.55", {"start": v(-3882.5, 2850) * mm, "end": v(-3882.5, 1250) * mm});
            skLineSegment(sketch, "E424.2.0.59", {"start": v(-3882.5, 2900) * mm, "end": v(-3882.5, 3750) * mm});
            skLineSegment(sketch, "E424.2.0.63", {"start": v(-3957.5, 2900) * mm, "end": v(-3957.5, 3750) * mm});
            skLineSegment(sketch, "E424.2.0.65", {"start": v(-3957.5, 2850) * mm, "end": v(-3957.5, 1250) * mm});
            skPoint(sketch, "E425", {"position": v(-15860, 1100) * mm});
            skPoint(sketch, "E426", {"position": v(-13060, 1100) * mm});
            skLineSegment(sketch, "E427.2.0.2", {"start": v(-14210, 2900) * mm, "end": v(-14210, 3750) * mm});
            skLineSegment(sketch, "E427.2.0.8", {"start": v(-15860, 1100) * mm, "end": v(-14160, 1100) * mm});
            skLineSegment(sketch, "E427.2.0.10", {"start": v(-15810, 2900) * mm, "end": v(-15047.5, 2900) * mm});
            skLineSegment(sketch, "E427.2.0.11", {"start": v(-15810, 1150) * mm, "end": v(-15047.5, 1150) * mm});
            skLineSegment(sketch, "E427.2.0.14", {"start": v(-15810, 2850) * mm, "end": v(-15810, 1150) * mm});
            skLineSegment(sketch, "E427.2.0.18", {"start": v(-15810, 2850) * mm, "end": v(-15047.5, 2850) * mm});
            skLineSegment(sketch, "E427.2.0.23", {"start": v(-14210, 2850) * mm, "end": v(-14210, 1150) * mm});
            skLineSegment(sketch, "E427.2.0.25", {"start": v(-14160, 3800) * mm, "end": v(-15860, 3800) * mm});
            skLineSegment(sketch, "E427.2.0.31", {"start": v(-14210, 1150) * mm, "end": v(-14972.5, 1150) * mm});
            skLineSegment(sketch, "E427.2.0.34", {"start": v(-15810, 2900) * mm, "end": v(-15810, 3750) * mm});
            skLineSegment(sketch, "E427.2.0.36", {"start": v(-15010, 1200) * mm, "end": v(-15010, 3800) * mm, "construction": true});
            skLineSegment(sketch, "E427.2.0.37", {"start": v(-14210, 2850) * mm, "end": v(-14972.5, 2850) * mm});
            skLineSegment(sketch, "E427.2.0.40", {"start": v(-15860, 3800) * mm, "end": v(-15860, 1100) * mm});
            skLineSegment(sketch, "E427.2.0.41", {"start": v(-14210, 2900) * mm, "end": v(-14972.5, 2900) * mm});
            skLineSegment(sketch, "E427.2.0.46", {"start": v(-14160, 1100) * mm, "end": v(-14160, 3800) * mm});
            skLineSegment(sketch, "E427.2.0.49", {"start": v(-15810, 3750) * mm, "end": v(-15047.5, 3750) * mm});
            skLineSegment(sketch, "E427.2.0.50", {"start": v(-14210, 3750) * mm, "end": v(-14972.5, 3750) * mm});
            skLineSegment(sketch, "E427.2.0.55", {"start": v(-14972.5, 2850) * mm, "end": v(-14972.5, 1150) * mm});
            skLineSegment(sketch, "E427.2.0.59", {"start": v(-14972.5, 2900) * mm, "end": v(-14972.5, 3750) * mm});
            skLineSegment(sketch, "E427.2.0.63", {"start": v(-15047.5, 2900) * mm, "end": v(-15047.5, 3750) * mm});
            skLineSegment(sketch, "E427.2.0.65", {"start": v(-15047.5, 2850) * mm, "end": v(-15047.5, 1150) * mm});
            skPoint(sketch, "E428", {"position": v(-13052.92, 1100) * mm});
            skLineSegment(sketch, "E429.2.0.2", {"start": v(-11410, 2900) * mm, "end": v(-11410, 3750) * mm});
            skLineSegment(sketch, "E429.2.0.8", {"start": v(-13060, 1100) * mm, "end": v(-11360, 1100) * mm});
            skLineSegment(sketch, "E429.2.0.10", {"start": v(-13010, 2900) * mm, "end": v(-12247.5, 2900) * mm});
            skLineSegment(sketch, "E429.2.0.11", {"start": v(-13010, 1150) * mm, "end": v(-12247.5, 1150) * mm});
            skLineSegment(sketch, "E429.2.0.14", {"start": v(-13010, 2850) * mm, "end": v(-13010, 1150) * mm});
            skLineSegment(sketch, "E429.2.0.18", {"start": v(-13010, 2850) * mm, "end": v(-12247.5, 2850) * mm});
            skLineSegment(sketch, "E429.2.0.23", {"start": v(-11410, 2850) * mm, "end": v(-11410, 1150) * mm});
            skLineSegment(sketch, "E429.2.0.25", {"start": v(-11360, 3800) * mm, "end": v(-13060, 3800) * mm});
            skLineSegment(sketch, "E429.2.0.31", {"start": v(-11410, 1150) * mm, "end": v(-12172.5, 1150) * mm});
            skLineSegment(sketch, "E429.2.0.34", {"start": v(-13010, 2900) * mm, "end": v(-13010, 3750) * mm});
            skLineSegment(sketch, "E429.2.0.36", {"start": v(-12210, 1200) * mm, "end": v(-12210, 3800) * mm, "construction": true});
            skLineSegment(sketch, "E429.2.0.40", {"start": v(-13060, 3800) * mm, "end": v(-13060, 1100) * mm});
            skLineSegment(sketch, "E429.2.0.41", {"start": v(-11410, 2900) * mm, "end": v(-12165.42, 2900) * mm});
            skLineSegment(sketch, "E429.2.0.46", {"start": v(-11360, 1100) * mm, "end": v(-11360, 3800) * mm});
            skLineSegment(sketch, "E429.2.0.49", {"start": v(-13010, 3750) * mm, "end": v(-12247.5, 3750) * mm});
            skLineSegment(sketch, "E429.2.0.50", {"start": v(-11410, 3750) * mm, "end": v(-12172.5, 3750) * mm});
            skLineSegment(sketch, "E429.2.0.55", {"start": v(-12172.5, 2850) * mm, "end": v(-12172.5, 1150) * mm});
            skLineSegment(sketch, "E429.2.0.59", {"start": v(-12165.42, 2900) * mm, "end": v(-12165.42, 3750) * mm});
            skLineSegment(sketch, "E429.2.0.63", {"start": v(-12247.5, 2900) * mm, "end": v(-12247.5, 3750) * mm});
            skLineSegment(sketch, "E429.2.0.65", {"start": v(-12247.5, 2850) * mm, "end": v(-12247.5, 1150) * mm});
            skLineSegment(sketch, "E430", {"start": v(-11410, 2850) * mm, "end": v(-12172.5, 2850) * mm});
            skSolve(sketch);
        }
        {
            var Q0;
            Q0=qSketchRegion(id+"F48",true);
            extrude(context, id + "F49", {"entities" : qUnion([Q0]), "depth" : 50 * mm, "offsetDistance" : 25 * mm});
        }
        {
            var Q0;
            Q0=makeQuery(id+"F5.boolean.opBoolean","MERGE",FACE,{"derivedFrom":[makeQuery(id+"F3.boolean.opBoolean","COPY",FACE,{"derivedFrom":makeQuery(id+"F3.opExtrude","SWEPT_FACE",FACE,{"disambiguationData":[OSD([sQuery(id+"F2.wireOp",EDGE,"E19.1")])]})}),makeQuery(id+"F5.opExtrude","SWEPT_FACE",FACE,{"disambiguationData":[OSD([sQuery(id+"F4.wireOp",EDGE,"E21")])]})]});
            var sketch = newSketch(context, id + "F50", { "sketchPlane" : qUnion([Q0])});
            skLineSegment(sketch, "E431.bottom", {"start": v(16840, -150) * mm, "end": v(18440, -150) * mm});
            skLineSegment(sketch, "E431.top", {"start": v(16840, 2370) * mm, "end": v(18440, 2370) * mm});
            skLineSegment(sketch, "E431.left", {"start": v(16840, -150) * mm, "end": v(16840, 2370) * mm});
            skLineSegment(sketch, "E431.right", {"start": v(18440, -150) * mm, "end": v(18440, 2370) * mm});
            skSolve(sketch);
        }
        {
            var Q0;
            Q0=qSketchRegion(id+"F50",true);
            extrude(context, id + "F51", {"entities" : qUnion([Q0]), "operationType" : NewBodyOperationType.REMOVE, "oppositeDirection" : true, "depth" : 600 * mm, "offsetDistance" : 25 * mm});
        }
        {
            var Q0;
            {var subQ26=sQuery(id+"F0.wireOp",EDGE,"E16.5");Q0=makeQuery(id+"F2hi8GqezRywkeN_40.boolean.opBoolean","SPLIT",FACE,{"disambiguationData":[TD([makeQuery(id+"F2x6o0qxNZTSrfC_40.boolean.opBoolean","COPY",FACE,{"derivedFrom":makeQuery(id+"F2x6o0qxNZTSrfC_40.opExtrude","SWEPT_FACE",FACE,{"disambiguationData":[OSD([sQuery(id+"F7vcSyRpF9JMD3K_40.wireOp",EDGE,"hXnOyaqm-xlU2-VTCc-7dql-qga7E96rzK4p.right")])]})})])],"derivedFrom":makeQuery(id+"F1.opExtrude","SWEPT_FACE",FACE,{"disambiguationData":[OSD([subQ26])]})});}
            var sketch = newSketch(context, id + "F52", { "sketchPlane" : qUnion([Q0])});
            skLineSegment(sketch, "E432.0", {"start": v(-16840, -150) * mm, "end": v(-16840, 2370) * mm});
            skLineSegment(sketch, "E433.0", {"start": v(-16840, 2370) * mm, "end": v(-18440, 2370) * mm});
            skLineSegment(sketch, "E434.0", {"start": v(-18440, -150) * mm, "end": v(-18440, 2370) * mm});
            skLineSegment(sketch, "E435.0", {"start": v(-16840, -150) * mm, "end": v(-18440, -150) * mm});
            skSolve(sketch);
        }
        {
            var Q0;
            Q0=qSketchRegion(id+"F52",true);
            extrude(context, id + "F53", {"entities" : qUnion([Q0]), "oppositeDirection" : true, "depth" : 200 * mm, "offsetDistance" : 25 * mm});
        }
        {
            var Q0;
            Q0=makeQuery(id+"F53.opExtrude","CAP_FACE",FACE,{"disambiguationData":[OSD([sQuery(id+"F52.wireOp",EDGE,"E432.0"),sQuery(id+"F52.wireOp",EDGE,"E433.0"),sQuery(id+"F52.wireOp",EDGE,"E434.0"),sQuery(id+"F52.wireOp",EDGE,"E435.0")])],"isStart":false});
            var sketch = newSketch(context, id + "F54", { "sketchPlane" : qUnion([Q0])});
            skLineSegment(sketch, "E436", {"start": v(17640, 2370) * mm, "end": v(17640, -150) * mm, "construction": true});
            skLineSegment(sketch, "E437.0.0", {"start": v(18440, 2370) * mm, "end": v(18440, -150) * mm});
            skLineSegment(sketch, "E437.0.6", {"start": v(16840, -150) * mm, "end": v(16840, 2370) * mm});
            skLineSegment(sketch, "E437.0.7", {"start": v(16840, 2370) * mm, "end": v(18440, 2370) * mm});
            skLineSegment(sketch, "E438", {"start": v(16890, -150) * mm, "end": v(16890, 1050) * mm});
            skLineSegment(sketch, "E439", {"start": v(16890, 1050) * mm, "end": v(17590, 1050) * mm});
            skLineSegment(sketch, "E440", {"start": v(17590, 1050) * mm, "end": v(17590, -150) * mm});
            skLineSegment(sketch, "E441", {"start": v(17590, -150) * mm, "end": v(17640, -150) * mm});
            skLineSegment(sketch, "E442", {"start": v(16890, -150) * mm, "end": v(16840, -150) * mm});
            skLineSegment(sketch, "E443", {"start": v(17640, 2320) * mm, "end": v(16890, 2320) * mm});
            skLineSegment(sketch, "E444", {"start": v(16890, 2320) * mm, "end": v(16890, 1100) * mm});
            skLineSegment(sketch, "E445", {"start": v(16890, 1100) * mm, "end": v(17640, 1100) * mm});
            skLineSegment(sketch, "E446.MirrorCS", {"start": v(17640, 2320) * mm, "end": v(18390, 2320) * mm});
            skLineSegment(sketch, "E447.MirrorCS", {"start": v(18390, 2320) * mm, "end": v(18390, 1100) * mm});
            skLineSegment(sketch, "E448.MirrorCS", {"start": v(18390, 1100) * mm, "end": v(17640, 1100) * mm});
            skLineSegment(sketch, "E449.MirrorCS", {"start": v(18390, 1050) * mm, "end": v(17690, 1050) * mm});
            skLineSegment(sketch, "E450.MirrorCS", {"start": v(17690, 1050) * mm, "end": v(17690, -150) * mm});
            skLineSegment(sketch, "E451.MirrorCS", {"start": v(18390, -150) * mm, "end": v(18390, 1050) * mm});
            skLineSegment(sketch, "E452.MirrorCS", {"start": v(18390, -150) * mm, "end": v(18440, -150) * mm});
            skLineSegment(sketch, "E453.MirrorCS", {"start": v(17690, -150) * mm, "end": v(17640, -150) * mm});
            skSolve(sketch);
        }
        {
            var Q0;
            Q0=qSketchRegion(id+"F54",true);
            extrude(context, id + "F55", {"entities" : qUnion([Q0]), "depth" : 50 * mm, "offsetDistance" : 25 * mm});
        }
        {
            var Q0;
            Q0=makeQuery(id+"F5.boolean.opBoolean","MERGE",FACE,{"derivedFrom":[makeQuery(id+"F3.boolean.opBoolean","COPY",FACE,{"derivedFrom":makeQuery(id+"F3.opExtrude","SWEPT_FACE",FACE,{"disambiguationData":[OSD([sQuery(id+"F2.wireOp",EDGE,"E19.3")])]})}),makeQuery(id+"F5.opExtrude","SWEPT_FACE",FACE,{"disambiguationData":[OSD([sQuery(id+"F4.wireOp",EDGE,"E27.0")])]})]});
            var sketch = newSketch(context, id + "F56", { "sketchPlane" : qUnion([Q0])});
            skLineSegment(sketch, "E454.0", {"start": v(9330, 3800) * mm, "end": v(7630, 3800) * mm});
            skLineSegment(sketch, "E455.0", {"start": v(9330, 3800) * mm, "end": v(9330, 1200) * mm});
            skLineSegment(sketch, "E456.0", {"start": v(7630, 3800) * mm, "end": v(7630, 1200) * mm});
            skLineSegment(sketch, "E457.0", {"start": v(9330, 1200) * mm, "end": v(7630, 1200) * mm});
            skLineSegment(sketch, "E458.bottom", {"start": v(7480, 3950) * mm, "end": v(9480, 3950) * mm});
            skLineSegment(sketch, "E458.top", {"start": v(7480, 1150) * mm, "end": v(9480, 1150) * mm});
            skLineSegment(sketch, "E458.left", {"start": v(7480, 3950) * mm, "end": v(7480, 1150) * mm});
            skLineSegment(sketch, "E458.right", {"start": v(9480, 3950) * mm, "end": v(9480, 1150) * mm});
            skLineSegment(sketch, "E459.0", {"start": v(12230, 3800) * mm, "end": v(10530, 3800) * mm});
            skLineSegment(sketch, "E460.0", {"start": v(12230, 3800) * mm, "end": v(12230, 1200) * mm});
            skLineSegment(sketch, "E461.0", {"start": v(10530, 3800) * mm, "end": v(10530, 1200) * mm});
            skLineSegment(sketch, "E462.0", {"start": v(12230, 1200) * mm, "end": v(10530, 1200) * mm});
            skLineSegment(sketch, "E463.bottom", {"start": v(10380, 3950) * mm, "end": v(12380, 3950) * mm});
            skLineSegment(sketch, "E463.top", {"start": v(10380, 1150) * mm, "end": v(12380, 1150) * mm});
            skLineSegment(sketch, "E463.left", {"start": v(10380, 3950) * mm, "end": v(10380, 1150) * mm});
            skLineSegment(sketch, "E463.right", {"start": v(12380, 3950) * mm, "end": v(12380, 1150) * mm});
            skLineSegment(sketch, "E464.0", {"start": v(15130, 3800) * mm, "end": v(13430, 3800) * mm});
            skLineSegment(sketch, "E465.0", {"start": v(15130, 3800) * mm, "end": v(15130, 1200) * mm});
            skLineSegment(sketch, "E466.0", {"start": v(13430, 3800) * mm, "end": v(13430, 1200) * mm});
            skLineSegment(sketch, "E467.0", {"start": v(15130, 1200) * mm, "end": v(13430, 1200) * mm});
            skLineSegment(sketch, "E468.bottom", {"start": v(13280, 3950) * mm, "end": v(15280, 3950) * mm});
            skLineSegment(sketch, "E468.top", {"start": v(13280, 1150) * mm, "end": v(15280, 1150) * mm});
            skLineSegment(sketch, "E468.left", {"start": v(13280, 3950) * mm, "end": v(13280, 1150) * mm});
            skLineSegment(sketch, "E468.right", {"start": v(15280, 3950) * mm, "end": v(15280, 1150) * mm});
            skLineSegment(sketch, "E469", {"start": v(17605, 4000) * mm, "end": v(17605, 2909.1) * mm, "construction": true});
            skLineSegment(sketch, "E470.MirrorCS", {"start": v(24830, 1150) * mm, "end": v(22830, 1150) * mm});
            skLineSegment(sketch, "E471.MirrorCS", {"start": v(25880, 1200) * mm, "end": v(27580, 1200) * mm});
            skLineSegment(sketch, "E472.MirrorCS", {"start": v(20080, 1200) * mm, "end": v(21780, 1200) * mm});
            skLineSegment(sketch, "E473.MirrorCS", {"start": v(27730, 1150) * mm, "end": v(25730, 1150) * mm});
            skLineSegment(sketch, "E474.MirrorCS", {"start": v(27730, 3950) * mm, "end": v(25730, 3950) * mm});
            skLineSegment(sketch, "E475.MirrorCS", {"start": v(22980, 3800) * mm, "end": v(24680, 3800) * mm});
            skLineSegment(sketch, "E476.MirrorCS", {"start": v(25730, 3950) * mm, "end": v(25730, 1150) * mm});
            skLineSegment(sketch, "E477.MirrorCS", {"start": v(21780, 3800) * mm, "end": v(21780, 1200) * mm});
            skLineSegment(sketch, "E478.MirrorCS", {"start": v(24680, 3800) * mm, "end": v(24680, 1200) * mm});
            skLineSegment(sketch, "E479.MirrorCS", {"start": v(21930, 3950) * mm, "end": v(19930, 3950) * mm});
            skLineSegment(sketch, "E480.MirrorCS", {"start": v(22830, 3950) * mm, "end": v(22830, 1150) * mm});
            skLineSegment(sketch, "E481.MirrorCS", {"start": v(24830, 3950) * mm, "end": v(24830, 1150) * mm});
            skLineSegment(sketch, "E482.MirrorCS", {"start": v(19930, 3950) * mm, "end": v(19930, 1150) * mm});
            skLineSegment(sketch, "E483.MirrorCS", {"start": v(25880, 3800) * mm, "end": v(25880, 1200) * mm});
            skLineSegment(sketch, "E484.MirrorCS", {"start": v(25880, 3800) * mm, "end": v(27580, 3800) * mm});
            skLineSegment(sketch, "E485.MirrorCS", {"start": v(21930, 1150) * mm, "end": v(19930, 1150) * mm});
            skLineSegment(sketch, "E486.MirrorCS", {"start": v(27580, 3800) * mm, "end": v(27580, 1200) * mm});
            skLineSegment(sketch, "E487.MirrorCS", {"start": v(24830, 3950) * mm, "end": v(22830, 3950) * mm});
            skLineSegment(sketch, "E488.MirrorCS", {"start": v(20080, 3800) * mm, "end": v(20080, 1200) * mm});
            skLineSegment(sketch, "E489.MirrorCS", {"start": v(22980, 1200) * mm, "end": v(24680, 1200) * mm});
            skLineSegment(sketch, "E490.MirrorCS", {"start": v(21930, 3950) * mm, "end": v(21930, 1150) * mm});
            skLineSegment(sketch, "E491.MirrorCS", {"start": v(20080, 3800) * mm, "end": v(21780, 3800) * mm});
            skLineSegment(sketch, "E492.MirrorCS", {"start": v(22980, 3800) * mm, "end": v(22980, 1200) * mm});
            skLineSegment(sketch, "E493.MirrorCS", {"start": v(27730, 3950) * mm, "end": v(27730, 1150) * mm});
            skSolve(sketch);
        }
        {
            var Q0;
            Q0=qSketchRegion(id+"F56",true);
            extrude(context, id + "F57", {"entities" : qUnion([Q0]), "depth" : 50 * mm, "offsetDistance" : 25 * mm});
        }
        {
            var Q0;
            Q0=makeQuery(id+"F5.boolean.opBoolean","MERGE",FACE,{"derivedFrom":[makeQuery(id+"F3.boolean.opBoolean","COPY",FACE,{"derivedFrom":makeQuery(id+"F3.opExtrude","SWEPT_FACE",FACE,{"disambiguationData":[OSD([sQuery(id+"F2.wireOp",EDGE,"E19.15")])]})}),makeQuery(id+"F5.opExtrude","SWEPT_FACE",FACE,{"disambiguationData":[OSD([sQuery(id+"F4.wireOp",EDGE,"E29.0")])]})]});
            var sketch = newSketch(context, id + "F58", { "sketchPlane" : qUnion([Q0])});
            skPoint(sketch, "E494", {"position": v(1280, 1200) * mm});
            skPoint(sketch, "E495", {"position": v(4280, 1200) * mm});
            skPoint(sketch, "E496", {"position": v(29230, 1200) * mm});
            skPoint(sketch, "E497", {"position": v(32230, 1200) * mm});
            skLineSegment(sketch, "E498.0", {"start": v(2980, 3800) * mm, "end": v(1280, 3800) * mm});
            skLineSegment(sketch, "E499.0", {"start": v(2980, 3800) * mm, "end": v(2980, 1200) * mm});
            skLineSegment(sketch, "E500.0", {"start": v(1280, 3800) * mm, "end": v(1280, 1200) * mm});
            skLineSegment(sketch, "E501.0", {"start": v(2980, 1200) * mm, "end": v(1280, 1200) * mm});
            skLineSegment(sketch, "E502.bottom", {"start": v(1130, 3950) * mm, "end": v(3130, 3950) * mm});
            skLineSegment(sketch, "E502.top", {"start": v(1130, 1150) * mm, "end": v(3130, 1150) * mm});
            skLineSegment(sketch, "E502.left", {"start": v(1130, 3950) * mm, "end": v(1130, 1150) * mm});
            skLineSegment(sketch, "E502.right", {"start": v(3130, 3950) * mm, "end": v(3130, 1150) * mm});
            skLineSegment(sketch, "E503.0", {"start": v(5980, 3800) * mm, "end": v(4280, 3800) * mm});
            skLineSegment(sketch, "E504.0", {"start": v(5980, 3800) * mm, "end": v(5980, 1200) * mm});
            skLineSegment(sketch, "E505.0", {"start": v(4280, 3800) * mm, "end": v(4280, 1200) * mm});
            skLineSegment(sketch, "E506.0", {"start": v(5980, 1200) * mm, "end": v(4280, 1200) * mm});
            skLineSegment(sketch, "E507.bottom", {"start": v(4130, 3950) * mm, "end": v(6130, 3950) * mm});
            skLineSegment(sketch, "E507.top", {"start": v(4130, 1150) * mm, "end": v(6130, 1150) * mm});
            skLineSegment(sketch, "E507.left", {"start": v(4130, 3950) * mm, "end": v(4130, 1150) * mm});
            skLineSegment(sketch, "E507.right", {"start": v(6130, 3950) * mm, "end": v(6130, 1150) * mm});
            skLineSegment(sketch, "E508.0", {"start": v(30930, 3800) * mm, "end": v(29230, 3800) * mm});
            skLineSegment(sketch, "E509.0", {"start": v(30930, 3800) * mm, "end": v(30930, 1200) * mm});
            skLineSegment(sketch, "E510.0", {"start": v(29230, 3800) * mm, "end": v(29230, 1200) * mm});
            skLineSegment(sketch, "E511.0", {"start": v(30930, 1200) * mm, "end": v(29230, 1200) * mm});
            skLineSegment(sketch, "E512.bottom", {"start": v(29080, 3950) * mm, "end": v(31080, 3950) * mm});
            skLineSegment(sketch, "E512.top", {"start": v(29080, 1150) * mm, "end": v(31080, 1150) * mm});
            skLineSegment(sketch, "E512.left", {"start": v(29080, 3950) * mm, "end": v(29080, 1150) * mm});
            skLineSegment(sketch, "E512.right", {"start": v(31080, 3950) * mm, "end": v(31080, 1150) * mm});
            skLineSegment(sketch, "E513.0", {"start": v(33930, 3800) * mm, "end": v(32230, 3800) * mm});
            skLineSegment(sketch, "E514.0", {"start": v(33930, 3800) * mm, "end": v(33930, 1200) * mm});
            skLineSegment(sketch, "E515.0", {"start": v(32230, 3800) * mm, "end": v(32230, 1200) * mm});
            skLineSegment(sketch, "E516.0", {"start": v(33930, 1200) * mm, "end": v(32230, 1200) * mm});
            skLineSegment(sketch, "E517.bottom", {"start": v(32080, 3950) * mm, "end": v(34080, 3950) * mm});
            skLineSegment(sketch, "E517.top", {"start": v(32080, 1150) * mm, "end": v(34080, 1150) * mm});
            skLineSegment(sketch, "E517.left", {"start": v(32080, 3950) * mm, "end": v(32080, 1150) * mm});
            skLineSegment(sketch, "E517.right", {"start": v(34080, 3950) * mm, "end": v(34080, 1150) * mm});
            skSolve(sketch);
        }
        {
            var Q0;
            Q0 = qSketchRegion(id + "F58", true);
            extrude(context, id + "F59", {"entities" : qUnion([Q0]), "depth" : 50 * mm, "offsetDistance" : 25 * mm});
        }
        {
            var Q0;
            Q0=makeQuery(id+"F57.opExtrude","CAP_FACE",FACE,{"disambiguationData":[OSD([sQuery(id+"F56.wireOp",EDGE,"E454.0"),sQuery(id+"F56.wireOp",EDGE,"E455.0"),sQuery(id+"F56.wireOp",EDGE,"E456.0"),sQuery(id+"F56.wireOp",EDGE,"E457.0"),sQuery(id+"F56.wireOp",EDGE,"E458.bottom"),sQuery(id+"F56.wireOp",EDGE,"E458.top"),sQuery(id+"F56.wireOp",EDGE,"E458.left"),sQuery(id+"F56.wireOp",EDGE,"E458.right")])],"isStart":false});
            var sketch = newSketch(context, id + "F60", { "sketchPlane" : qUnion([Q0])});
            skLineSegment(sketch, "E518.24", {"start": v(17605, 4000) * mm, "end": v(17605, 2909.1) * mm, "construction": true});
            skLineSegment(sketch, "E519.0", {"start": v(7480, 3950) * mm, "end": v(7480, 1150) * mm});
            skLineSegment(sketch, "E519.1", {"start": v(9480, 1150) * mm, "end": v(9480, 3950) * mm});
            skLineSegment(sketch, "E519.2", {"start": v(9480, 3950) * mm, "end": v(7480, 3950) * mm});
            skLineSegment(sketch, "E519.3", {"start": v(7580, 3850) * mm, "end": v(7580, 1150) * mm});
            skLineSegment(sketch, "E519.4", {"start": v(9380, 3850) * mm, "end": v(7580, 3850) * mm});
            skLineSegment(sketch, "E519.5", {"start": v(9380, 1150) * mm, "end": v(9380, 3850) * mm});
            skLineSegment(sketch, "E519.6", {"start": v(7480, 1150) * mm, "end": v(7580, 1150) * mm});
            skLineSegment(sketch, "E519.7", {"start": v(9380, 1150) * mm, "end": v(9480, 1150) * mm});
            skLineSegment(sketch, "E519.8", {"start": v(9480, 1150) * mm, "end": v(7480, 1150) * mm});
            skLineSegment(sketch, "E519.9", {"start": v(7630, 3800) * mm, "end": v(9330, 3800) * mm});
            skLineSegment(sketch, "E519.10", {"start": v(9330, 3800) * mm, "end": v(9330, 1200) * mm});
            skLineSegment(sketch, "E519.11", {"start": v(7480, 3950) * mm, "end": v(7480, 1150) * mm});
            skLineSegment(sketch, "E519.12", {"start": v(9480, 3950) * mm, "end": v(9480, 1150) * mm});
            skLineSegment(sketch, "E519.13", {"start": v(9480, 3950) * mm, "end": v(7480, 3950) * mm});
            skLineSegment(sketch, "E519.14", {"start": v(7630, 1200) * mm, "end": v(9330, 1200) * mm});
            skLineSegment(sketch, "E519.15", {"start": v(7630, 3800) * mm, "end": v(7630, 1200) * mm});
            skPoint(sketch, "E520", {"position": v(10380, 1150) * mm});
            skPoint(sketch, "E521", {"position": v(13280, 1150) * mm});
            skPoint(sketch, "E522", {"position": v(19930, 1150) * mm});
            skPoint(sketch, "E523", {"position": v(22830, 1150) * mm});
            skPoint(sketch, "E524", {"position": v(25730, 1150) * mm});
            skLineSegment(sketch, "E525.0", {"start": v(10380, 3950) * mm, "end": v(10380, 1150) * mm});
            skLineSegment(sketch, "E525.1", {"start": v(12380, 1150) * mm, "end": v(12380, 3950) * mm});
            skLineSegment(sketch, "E525.2", {"start": v(12380, 3950) * mm, "end": v(10380, 3950) * mm});
            skLineSegment(sketch, "E525.3", {"start": v(10480, 3850) * mm, "end": v(10480, 1150) * mm});
            skLineSegment(sketch, "E525.4", {"start": v(12280, 3850) * mm, "end": v(10480, 3850) * mm});
            skLineSegment(sketch, "E525.5", {"start": v(12280, 1150) * mm, "end": v(12280, 3850) * mm});
            skLineSegment(sketch, "E525.6", {"start": v(10380, 1150) * mm, "end": v(10480, 1150) * mm});
            skLineSegment(sketch, "E525.7", {"start": v(12280, 1150) * mm, "end": v(12380, 1150) * mm});
            skLineSegment(sketch, "E525.8", {"start": v(12380, 1150) * mm, "end": v(10380, 1150) * mm});
            skLineSegment(sketch, "E525.9", {"start": v(10530, 3800) * mm, "end": v(12230, 3800) * mm});
            skLineSegment(sketch, "E525.10", {"start": v(12230, 3800) * mm, "end": v(12230, 1200) * mm});
            skLineSegment(sketch, "E525.11", {"start": v(10380, 3950) * mm, "end": v(10380, 1150) * mm});
            skLineSegment(sketch, "E525.12", {"start": v(12380, 3950) * mm, "end": v(12380, 1150) * mm});
            skLineSegment(sketch, "E525.13", {"start": v(12380, 3950) * mm, "end": v(10380, 3950) * mm});
            skLineSegment(sketch, "E525.14", {"start": v(10530, 1200) * mm, "end": v(12230, 1200) * mm});
            skLineSegment(sketch, "E525.15", {"start": v(10530, 3800) * mm, "end": v(10530, 1200) * mm});
            skLineSegment(sketch, "E526.0", {"start": v(13280, 3950) * mm, "end": v(13280, 1150) * mm});
            skLineSegment(sketch, "E526.1", {"start": v(15280, 1150) * mm, "end": v(15280, 3950) * mm});
            skLineSegment(sketch, "E526.2", {"start": v(15280, 3950) * mm, "end": v(13280, 3950) * mm});
            skLineSegment(sketch, "E526.3", {"start": v(13380, 3850) * mm, "end": v(13380, 1150) * mm});
            skLineSegment(sketch, "E526.4", {"start": v(15180, 3850) * mm, "end": v(13380, 3850) * mm});
            skLineSegment(sketch, "E526.5", {"start": v(15180, 1150) * mm, "end": v(15180, 3850) * mm});
            skLineSegment(sketch, "E526.6", {"start": v(13280, 1150) * mm, "end": v(13380, 1150) * mm});
            skLineSegment(sketch, "E526.7", {"start": v(15180, 1150) * mm, "end": v(15280, 1150) * mm});
            skLineSegment(sketch, "E526.8", {"start": v(15280, 1150) * mm, "end": v(13280, 1150) * mm});
            skLineSegment(sketch, "E526.9", {"start": v(13430, 3800) * mm, "end": v(15130, 3800) * mm});
            skLineSegment(sketch, "E526.10", {"start": v(15130, 3800) * mm, "end": v(15130, 1200) * mm});
            skLineSegment(sketch, "E526.11", {"start": v(13280, 3950) * mm, "end": v(13280, 1150) * mm});
            skLineSegment(sketch, "E526.12", {"start": v(15280, 3950) * mm, "end": v(15280, 1150) * mm});
            skLineSegment(sketch, "E526.13", {"start": v(15280, 3950) * mm, "end": v(13280, 3950) * mm});
            skLineSegment(sketch, "E526.14", {"start": v(13430, 1200) * mm, "end": v(15130, 1200) * mm});
            skLineSegment(sketch, "E526.15", {"start": v(13430, 3800) * mm, "end": v(13430, 1200) * mm});
            skLineSegment(sketch, "E527.0", {"start": v(19930, 3950) * mm, "end": v(19930, 1150) * mm});
            skLineSegment(sketch, "E527.1", {"start": v(21930, 1150) * mm, "end": v(21930, 3950) * mm});
            skLineSegment(sketch, "E527.2", {"start": v(21930, 3950) * mm, "end": v(19930, 3950) * mm});
            skLineSegment(sketch, "E527.3", {"start": v(20030, 3850) * mm, "end": v(20030, 1150) * mm});
            skLineSegment(sketch, "E527.4", {"start": v(21830, 3850) * mm, "end": v(20030, 3850) * mm});
            skLineSegment(sketch, "E527.5", {"start": v(21830, 1150) * mm, "end": v(21830, 3850) * mm});
            skLineSegment(sketch, "E527.6", {"start": v(19930, 1150) * mm, "end": v(20030, 1150) * mm});
            skLineSegment(sketch, "E527.7", {"start": v(21830, 1150) * mm, "end": v(21930, 1150) * mm});
            skLineSegment(sketch, "E527.8", {"start": v(21930, 1150) * mm, "end": v(19930, 1150) * mm});
            skLineSegment(sketch, "E527.9", {"start": v(20080, 3800) * mm, "end": v(21780, 3800) * mm});
            skLineSegment(sketch, "E527.10", {"start": v(21780, 3800) * mm, "end": v(21780, 1200) * mm});
            skLineSegment(sketch, "E527.11", {"start": v(19930, 3950) * mm, "end": v(19930, 1150) * mm});
            skLineSegment(sketch, "E527.12", {"start": v(21930, 3950) * mm, "end": v(21930, 1150) * mm});
            skLineSegment(sketch, "E527.13", {"start": v(21930, 3950) * mm, "end": v(19930, 3950) * mm});
            skLineSegment(sketch, "E527.14", {"start": v(20080, 1200) * mm, "end": v(21780, 1200) * mm});
            skLineSegment(sketch, "E527.15", {"start": v(20080, 3800) * mm, "end": v(20080, 1200) * mm});
            skLineSegment(sketch, "E528.0", {"start": v(22830, 3950) * mm, "end": v(22830, 1150) * mm});
            skLineSegment(sketch, "E528.1", {"start": v(24830, 1150) * mm, "end": v(24830, 3950) * mm});
            skLineSegment(sketch, "E528.2", {"start": v(24830, 3950) * mm, "end": v(22830, 3950) * mm});
            skLineSegment(sketch, "E528.3", {"start": v(22930, 3850) * mm, "end": v(22930, 1150) * mm});
            skLineSegment(sketch, "E528.4", {"start": v(24730, 3850) * mm, "end": v(22930, 3850) * mm});
            skLineSegment(sketch, "E528.5", {"start": v(24730, 1150) * mm, "end": v(24730, 3850) * mm});
            skLineSegment(sketch, "E528.6", {"start": v(22830, 1150) * mm, "end": v(22930, 1150) * mm});
            skLineSegment(sketch, "E528.7", {"start": v(24730, 1150) * mm, "end": v(24830, 1150) * mm});
            skLineSegment(sketch, "E528.8", {"start": v(24830, 1150) * mm, "end": v(22830, 1150) * mm});
            skLineSegment(sketch, "E528.9", {"start": v(22980, 3800) * mm, "end": v(24680, 3800) * mm});
            skLineSegment(sketch, "E528.10", {"start": v(24680, 3800) * mm, "end": v(24680, 1200) * mm});
            skLineSegment(sketch, "E528.11", {"start": v(22830, 3950) * mm, "end": v(22830, 1150) * mm});
            skLineSegment(sketch, "E528.12", {"start": v(24830, 3950) * mm, "end": v(24830, 1150) * mm});
            skLineSegment(sketch, "E528.13", {"start": v(24830, 3950) * mm, "end": v(22830, 3950) * mm});
            skLineSegment(sketch, "E528.14", {"start": v(22980, 1200) * mm, "end": v(24680, 1200) * mm});
            skLineSegment(sketch, "E528.15", {"start": v(22980, 3800) * mm, "end": v(22980, 1200) * mm});
            skLineSegment(sketch, "E529.0", {"start": v(25730, 3950) * mm, "end": v(25730, 1150) * mm});
            skLineSegment(sketch, "E529.1", {"start": v(27730, 1150) * mm, "end": v(27730, 3950) * mm});
            skLineSegment(sketch, "E529.2", {"start": v(27730, 3950) * mm, "end": v(25730, 3950) * mm});
            skLineSegment(sketch, "E529.3", {"start": v(25830, 3850) * mm, "end": v(25830, 1150) * mm});
            skLineSegment(sketch, "E529.4", {"start": v(27630, 3850) * mm, "end": v(25830, 3850) * mm});
            skLineSegment(sketch, "E529.5", {"start": v(27630, 1150) * mm, "end": v(27630, 3850) * mm});
            skLineSegment(sketch, "E529.6", {"start": v(25730, 1150) * mm, "end": v(25830, 1150) * mm});
            skLineSegment(sketch, "E529.7", {"start": v(27630, 1150) * mm, "end": v(27730, 1150) * mm});
            skLineSegment(sketch, "E529.8", {"start": v(27730, 1150) * mm, "end": v(25730, 1150) * mm});
            skLineSegment(sketch, "E529.9", {"start": v(25880, 3800) * mm, "end": v(27580, 3800) * mm});
            skLineSegment(sketch, "E529.10", {"start": v(27580, 3800) * mm, "end": v(27580, 1200) * mm});
            skLineSegment(sketch, "E529.11", {"start": v(25730, 3950) * mm, "end": v(25730, 1150) * mm});
            skLineSegment(sketch, "E529.12", {"start": v(27730, 3950) * mm, "end": v(27730, 1150) * mm});
            skLineSegment(sketch, "E529.13", {"start": v(27730, 3950) * mm, "end": v(25730, 3950) * mm});
            skLineSegment(sketch, "E529.14", {"start": v(25880, 1200) * mm, "end": v(27580, 1200) * mm});
            skLineSegment(sketch, "E529.15", {"start": v(25880, 3800) * mm, "end": v(25880, 1200) * mm});
            skSolve(sketch);
        }
        {
            var Q0;
            {var subQ3=sQuery(id+"F60.wireOp",EDGE,"E519.1");Q0=makeQuery(id+"F60.imprint","IMPRINT",FACE,{"disambiguationData":[TD([[makeQuery(id+"F60.imprint","IMPRINT",EDGE,{"derivedFrom":subQ3}),1.0]])]});}
            var Q1;
            {var subQ2=sQuery(id+"F60.wireOp",EDGE,"E525.1");Q1=makeQuery(id+"F60.imprint","IMPRINT",FACE,{"disambiguationData":[TD([[makeQuery(id+"F60.imprint","IMPRINT",EDGE,{"derivedFrom":subQ2}),1.0]])]});}
            var Q2;
            {var subQ2=sQuery(id+"F60.wireOp",EDGE,"E526.1");Q2=makeQuery(id+"F60.imprint","IMPRINT",FACE,{"disambiguationData":[TD([[makeQuery(id+"F60.imprint","IMPRINT",EDGE,{"derivedFrom":subQ2}),1.0]])]});}
            var Q3;
            {var subQ2=sQuery(id+"F60.wireOp",EDGE,"E527.1");Q3=makeQuery(id+"F60.imprint","IMPRINT",FACE,{"disambiguationData":[TD([[makeQuery(id+"F60.imprint","IMPRINT",EDGE,{"derivedFrom":subQ2}),1.0]])]});}
            var Q4;
            {var subQ2=sQuery(id+"F60.wireOp",EDGE,"E528.1");Q4=makeQuery(id+"F60.imprint","IMPRINT",FACE,{"disambiguationData":[TD([[makeQuery(id+"F60.imprint","IMPRINT",EDGE,{"derivedFrom":subQ2}),1.0]])]});}
            var Q5;
            {var subQ2=sQuery(id+"F60.wireOp",EDGE,"E529.1");Q5=makeQuery(id+"F60.imprint","IMPRINT",FACE,{"disambiguationData":[TD([[makeQuery(id+"F60.imprint","IMPRINT",EDGE,{"derivedFrom":subQ2}),1.0]])]});}
            extrude(context, id + "F61", {"entities" : qUnion([Q0, Q1, Q2, Q3, Q4, Q5]), "operationType" : NewBodyOperationType.ADD, "depth" : 50 * mm, "offsetDistance" : 25 * mm});
        }
        {
            var Q0;
            Q0=makeQuery(id+"F59.opExtrude","CAP_FACE",FACE,{"disambiguationData":[OSD([sQuery(id+"F58.wireOp",EDGE,"E498.0"),sQuery(id+"F58.wireOp",EDGE,"E499.0"),sQuery(id+"F58.wireOp",EDGE,"E500.0"),sQuery(id+"F58.wireOp",EDGE,"E501.0"),sQuery(id+"F58.wireOp",EDGE,"E502.bottom"),sQuery(id+"F58.wireOp",EDGE,"E502.top"),sQuery(id+"F58.wireOp",EDGE,"E502.left"),sQuery(id+"F58.wireOp",EDGE,"E502.right")])],"isStart":false});
            var sketch = newSketch(context, id + "F62", { "sketchPlane" : qUnion([Q0])});
            skPoint(sketch, "E530", {"position": v(1130, 1150) * mm});
            skPoint(sketch, "E531", {"position": v(4130, 1150) * mm});
            skPoint(sketch, "E532", {"position": v(29080, 1150) * mm});
            skPoint(sketch, "E533", {"position": v(32080, 1150) * mm});
            skLineSegment(sketch, "E534.0", {"start": v(1130, 3950) * mm, "end": v(1130, 1150) * mm});
            skLineSegment(sketch, "E534.1", {"start": v(3130, 1150) * mm, "end": v(3130, 3950) * mm});
            skLineSegment(sketch, "E534.2", {"start": v(3130, 3950) * mm, "end": v(1130, 3950) * mm});
            skLineSegment(sketch, "E534.3", {"start": v(1230, 3850) * mm, "end": v(1230, 1150) * mm});
            skLineSegment(sketch, "E534.4", {"start": v(3030, 3850) * mm, "end": v(1230, 3850) * mm});
            skLineSegment(sketch, "E534.5", {"start": v(3030, 1150) * mm, "end": v(3030, 3850) * mm});
            skLineSegment(sketch, "E534.6", {"start": v(1130, 1150) * mm, "end": v(1230, 1150) * mm});
            skLineSegment(sketch, "E534.7", {"start": v(3030, 1150) * mm, "end": v(3130, 1150) * mm});
            skLineSegment(sketch, "E534.8", {"start": v(3130, 1150) * mm, "end": v(1130, 1150) * mm});
            skLineSegment(sketch, "E534.9", {"start": v(1280, 3800) * mm, "end": v(2980, 3800) * mm});
            skLineSegment(sketch, "E534.10", {"start": v(2980, 3800) * mm, "end": v(2980, 1200) * mm});
            skLineSegment(sketch, "E534.11", {"start": v(1130, 3950) * mm, "end": v(1130, 1150) * mm});
            skLineSegment(sketch, "E534.12", {"start": v(3130, 3950) * mm, "end": v(3130, 1150) * mm});
            skLineSegment(sketch, "E534.13", {"start": v(3130, 3950) * mm, "end": v(1130, 3950) * mm});
            skLineSegment(sketch, "E534.14", {"start": v(1280, 1200) * mm, "end": v(2980, 1200) * mm});
            skLineSegment(sketch, "E534.15", {"start": v(1280, 3800) * mm, "end": v(1280, 1200) * mm});
            skLineSegment(sketch, "E535.0", {"start": v(4130, 3950) * mm, "end": v(4130, 1150) * mm});
            skLineSegment(sketch, "E535.1", {"start": v(6130, 1150) * mm, "end": v(6130, 3950) * mm});
            skLineSegment(sketch, "E535.2", {"start": v(6130, 3950) * mm, "end": v(4130, 3950) * mm});
            skLineSegment(sketch, "E535.3", {"start": v(4230, 3850) * mm, "end": v(4230, 1150) * mm});
            skLineSegment(sketch, "E535.4", {"start": v(6030, 3850) * mm, "end": v(4230, 3850) * mm});
            skLineSegment(sketch, "E535.5", {"start": v(6030, 1150) * mm, "end": v(6030, 3850) * mm});
            skLineSegment(sketch, "E535.6", {"start": v(4130, 1150) * mm, "end": v(4230, 1150) * mm});
            skLineSegment(sketch, "E535.7", {"start": v(6030, 1150) * mm, "end": v(6130, 1150) * mm});
            skLineSegment(sketch, "E535.8", {"start": v(6130, 1150) * mm, "end": v(4130, 1150) * mm});
            skLineSegment(sketch, "E535.9", {"start": v(4280, 3800) * mm, "end": v(5980, 3800) * mm});
            skLineSegment(sketch, "E535.10", {"start": v(5980, 3800) * mm, "end": v(5980, 1200) * mm});
            skLineSegment(sketch, "E535.11", {"start": v(4130, 3950) * mm, "end": v(4130, 1150) * mm});
            skLineSegment(sketch, "E535.12", {"start": v(6130, 3950) * mm, "end": v(6130, 1150) * mm});
            skLineSegment(sketch, "E535.13", {"start": v(6130, 3950) * mm, "end": v(4130, 3950) * mm});
            skLineSegment(sketch, "E535.14", {"start": v(4280, 1200) * mm, "end": v(5980, 1200) * mm});
            skLineSegment(sketch, "E535.15", {"start": v(4280, 3800) * mm, "end": v(4280, 1200) * mm});
            skLineSegment(sketch, "E536.0", {"start": v(29080, 3950) * mm, "end": v(29080, 1150) * mm});
            skLineSegment(sketch, "E536.1", {"start": v(31080, 1150) * mm, "end": v(31080, 3950) * mm});
            skLineSegment(sketch, "E536.2", {"start": v(31080, 3950) * mm, "end": v(29080, 3950) * mm});
            skLineSegment(sketch, "E536.3", {"start": v(29180, 3850) * mm, "end": v(29180, 1150) * mm});
            skLineSegment(sketch, "E536.4", {"start": v(30980, 3850) * mm, "end": v(29180, 3850) * mm});
            skLineSegment(sketch, "E536.5", {"start": v(30980, 1150) * mm, "end": v(30980, 3850) * mm});
            skLineSegment(sketch, "E536.6", {"start": v(29080, 1150) * mm, "end": v(29180, 1150) * mm});
            skLineSegment(sketch, "E536.7", {"start": v(30980, 1150) * mm, "end": v(31080, 1150) * mm});
            skLineSegment(sketch, "E536.8", {"start": v(31080, 1150) * mm, "end": v(29080, 1150) * mm});
            skLineSegment(sketch, "E536.9", {"start": v(29230, 3800) * mm, "end": v(30930, 3800) * mm});
            skLineSegment(sketch, "E536.10", {"start": v(30930, 3800) * mm, "end": v(30930, 1200) * mm});
            skLineSegment(sketch, "E536.11", {"start": v(29080, 3950) * mm, "end": v(29080, 1150) * mm});
            skLineSegment(sketch, "E536.12", {"start": v(31080, 3950) * mm, "end": v(31080, 1150) * mm});
            skLineSegment(sketch, "E536.13", {"start": v(31080, 3950) * mm, "end": v(29080, 3950) * mm});
            skLineSegment(sketch, "E536.14", {"start": v(29230, 1200) * mm, "end": v(30930, 1200) * mm});
            skLineSegment(sketch, "E536.15", {"start": v(29230, 3800) * mm, "end": v(29230, 1200) * mm});
            skLineSegment(sketch, "E537.0", {"start": v(32080, 3950) * mm, "end": v(32080, 1150) * mm});
            skLineSegment(sketch, "E537.1", {"start": v(34080, 1150) * mm, "end": v(34080, 3950) * mm});
            skLineSegment(sketch, "E537.2", {"start": v(34080, 3950) * mm, "end": v(32080, 3950) * mm});
            skLineSegment(sketch, "E537.3", {"start": v(32180, 3850) * mm, "end": v(32180, 1150) * mm});
            skLineSegment(sketch, "E537.4", {"start": v(33980, 3850) * mm, "end": v(32180, 3850) * mm});
            skLineSegment(sketch, "E537.5", {"start": v(33980, 1150) * mm, "end": v(33980, 3850) * mm});
            skLineSegment(sketch, "E537.6", {"start": v(32080, 1150) * mm, "end": v(32180, 1150) * mm});
            skLineSegment(sketch, "E537.7", {"start": v(33980, 1150) * mm, "end": v(34080, 1150) * mm});
            skLineSegment(sketch, "E537.8", {"start": v(34080, 1150) * mm, "end": v(32080, 1150) * mm});
            skLineSegment(sketch, "E537.9", {"start": v(32230, 3800) * mm, "end": v(33930, 3800) * mm});
            skLineSegment(sketch, "E537.10", {"start": v(33930, 3800) * mm, "end": v(33930, 1200) * mm});
            skLineSegment(sketch, "E537.11", {"start": v(32080, 3950) * mm, "end": v(32080, 1150) * mm});
            skLineSegment(sketch, "E537.12", {"start": v(34080, 3950) * mm, "end": v(34080, 1150) * mm});
            skLineSegment(sketch, "E537.13", {"start": v(34080, 3950) * mm, "end": v(32080, 3950) * mm});
            skLineSegment(sketch, "E537.14", {"start": v(32230, 1200) * mm, "end": v(33930, 1200) * mm});
            skLineSegment(sketch, "E537.15", {"start": v(32230, 3800) * mm, "end": v(32230, 1200) * mm});
            skSolve(sketch);
        }
        {
            var Q0;
            {var subQ2=sQuery(id+"F62.wireOp",EDGE,"E537.1");Q0=makeQuery(id+"F62.imprint","IMPRINT",FACE,{"disambiguationData":[TD([[makeQuery(id+"F62.imprint","IMPRINT",EDGE,{"derivedFrom":subQ2}),1.0]])]});}
            var Q1;
            {var subQ2=sQuery(id+"F62.wireOp",EDGE,"E536.1");Q1=makeQuery(id+"F62.imprint","IMPRINT",FACE,{"disambiguationData":[TD([[makeQuery(id+"F62.imprint","IMPRINT",EDGE,{"derivedFrom":subQ2}),1.0]])]});}
            var Q2;
            {var subQ2=sQuery(id+"F62.wireOp",EDGE,"E534.3");Q2=makeQuery(id+"F62.imprint","IMPRINT",FACE,{"disambiguationData":[TD([[makeQuery(id+"F62.imprint","IMPRINT",EDGE,{"derivedFrom":subQ2}),-1.0]])]});}
            var Q3;
            {var subQ2=sQuery(id+"F62.wireOp",EDGE,"E535.1");Q3=makeQuery(id+"F62.imprint","IMPRINT",FACE,{"disambiguationData":[TD([[makeQuery(id+"F62.imprint","IMPRINT",EDGE,{"derivedFrom":subQ2}),1.0]])]});}
            extrude(context, id + "F63", {"entities" : qUnion([Q0, Q1, Q2, Q3]), "operationType" : NewBodyOperationType.ADD, "depth" : 25 * mm, "offsetDistance" : 25 * mm});
        }
        {
            var Q0;
            Q0=makeQuery(id+"F21.boolean.opBoolean","MERGE",FACE,{"derivedFrom":[makeQuery(id+"F5.boolean.opBoolean","MERGE",FACE,{"derivedFrom":[makeQuery(id+"F3.boolean.opBoolean","COPY",FACE,{"derivedFrom":makeQuery(id+"F3.opExtrude","SWEPT_FACE",FACE,{"disambiguationData":[OSD([sQuery(id+"F2.wireOp",EDGE,"E19.6")])]})}),makeQuery(id+"F5.opExtrude","SWEPT_FACE",FACE,{"disambiguationData":[OSD([sQuery(id+"F4.wireOp",EDGE,"E20")])]})]}),makeQuery(id+"F21.opExtrude","CAP_FACE",FACE,{"disambiguationData":[OSD([sQuery(id+"F20.wireOp",EDGE,"E240.bottom"),sQuery(id+"F20.wireOp",EDGE,"E240.top"),sQuery(id+"F20.wireOp",EDGE,"E240.left"),sQuery(id+"F20.wireOp",EDGE,"E240.right")])],"isStart":true})]});
            var sketch = newSketch(context, id + "F64", { "sketchPlane" : qUnion([Q0])});
            skPoint(sketch, "E538", {"position": v(-38060, 1100) * mm});
            skPoint(sketch, "E539", {"position": v(-35760, 1100) * mm});
            skPoint(sketch, "E540", {"position": v(-25260, 1100) * mm});
            skPoint(sketch, "E541", {"position": v(-22460, 1100) * mm});
            skPoint(sketch, "E542", {"position": v(-28060, 1100) * mm});
            skLineSegment(sketch, "E543.0", {"start": v(-38210, 3850) * mm, "end": v(-38210, 1050) * mm});
            skLineSegment(sketch, "E543.1", {"start": v(-36210, 1050) * mm, "end": v(-36210, 3850) * mm});
            skLineSegment(sketch, "E543.2", {"start": v(-36310, 3850) * mm, "end": v(-38110, 3850) * mm});
            skLineSegment(sketch, "E543.3", {"start": v(-38110, 3850) * mm, "end": v(-38110, 1050) * mm});
            skLineSegment(sketch, "E543.4", {"start": v(-36310, 3850) * mm, "end": v(-38110, 3850) * mm});
            skLineSegment(sketch, "E543.5", {"start": v(-36310, 1050) * mm, "end": v(-36310, 3850) * mm});
            skLineSegment(sketch, "E543.6", {"start": v(-38210, 1050) * mm, "end": v(-38110, 1050) * mm});
            skLineSegment(sketch, "E543.7", {"start": v(-36310, 1050) * mm, "end": v(-36210, 1050) * mm});
            skLineSegment(sketch, "E543.8", {"start": v(-36210, 1050) * mm, "end": v(-38210, 1050) * mm});
            skLineSegment(sketch, "E543.9", {"start": v(-38060, 3800) * mm, "end": v(-36360, 3800) * mm});
            skLineSegment(sketch, "E543.10", {"start": v(-36360, 3800) * mm, "end": v(-36360, 1100) * mm});
            skLineSegment(sketch, "E543.11", {"start": v(-38210, 3950) * mm, "end": v(-38210, 1050) * mm});
            skLineSegment(sketch, "E543.12", {"start": v(-36210, 3950) * mm, "end": v(-36210, 1050) * mm});
            skLineSegment(sketch, "E543.13", {"start": v(-36210, 3950) * mm, "end": v(-38210, 3950) * mm});
            skLineSegment(sketch, "E543.14", {"start": v(-38060, 1100) * mm, "end": v(-36360, 1100) * mm});
            skLineSegment(sketch, "E543.15", {"start": v(-38060, 3800) * mm, "end": v(-38060, 1100) * mm});
            skLineSegment(sketch, "E544.trimOffspring", {"start": v(-38210, 3850) * mm, "end": v(-38210, 3850) * mm});
            skLineSegment(sketch, "E545.0", {"start": v(-35910, 3850) * mm, "end": v(-35910, 1050) * mm});
            skLineSegment(sketch, "E545.1", {"start": v(-33910, 1050) * mm, "end": v(-33910, 3850) * mm});
            skLineSegment(sketch, "E545.2", {"start": v(-34010, 3850) * mm, "end": v(-35810, 3850) * mm});
            skLineSegment(sketch, "E545.3", {"start": v(-35810, 3850) * mm, "end": v(-35810, 1050) * mm});
            skLineSegment(sketch, "E545.4", {"start": v(-34010, 3850) * mm, "end": v(-35810, 3850) * mm});
            skLineSegment(sketch, "E545.5", {"start": v(-34010, 1050) * mm, "end": v(-34010, 3850) * mm});
            skLineSegment(sketch, "E545.6", {"start": v(-35910, 1050) * mm, "end": v(-35810, 1050) * mm});
            skLineSegment(sketch, "E545.7", {"start": v(-34010, 1050) * mm, "end": v(-33910, 1050) * mm});
            skLineSegment(sketch, "E545.8", {"start": v(-33910, 1050) * mm, "end": v(-35910, 1050) * mm});
            skLineSegment(sketch, "E545.9", {"start": v(-35760, 3800) * mm, "end": v(-34060, 3800) * mm});
            skLineSegment(sketch, "E545.10", {"start": v(-34060, 3800) * mm, "end": v(-34060, 1100) * mm});
            skLineSegment(sketch, "E545.11", {"start": v(-35910, 3950) * mm, "end": v(-35910, 1050) * mm});
            skLineSegment(sketch, "E545.12", {"start": v(-33910, 3950) * mm, "end": v(-33910, 1050) * mm});
            skLineSegment(sketch, "E545.13", {"start": v(-33910, 3950) * mm, "end": v(-35910, 3950) * mm});
            skLineSegment(sketch, "E545.14", {"start": v(-35760, 1100) * mm, "end": v(-34060, 1100) * mm});
            skLineSegment(sketch, "E545.15", {"start": v(-35760, 3800) * mm, "end": v(-35760, 1100) * mm});
            skLineSegment(sketch, "E546.trimOffspring", {"start": v(-35910, 3850) * mm, "end": v(-35910, 3850) * mm});
            skLineSegment(sketch, "E547.0", {"start": v(-28210, 3850) * mm, "end": v(-28210, 1050) * mm});
            skLineSegment(sketch, "E547.1", {"start": v(-26210, 1050) * mm, "end": v(-26210, 3850) * mm});
            skLineSegment(sketch, "E547.2", {"start": v(-26310, 3850) * mm, "end": v(-28110, 3850) * mm});
            skLineSegment(sketch, "E547.3", {"start": v(-28110, 3850) * mm, "end": v(-28110, 1050) * mm});
            skLineSegment(sketch, "E547.4", {"start": v(-26310, 3850) * mm, "end": v(-28110, 3850) * mm});
            skLineSegment(sketch, "E547.5", {"start": v(-26310, 1050) * mm, "end": v(-26310, 3850) * mm});
            skLineSegment(sketch, "E547.6", {"start": v(-28210, 1050) * mm, "end": v(-28110, 1050) * mm});
            skLineSegment(sketch, "E547.7", {"start": v(-26310, 1050) * mm, "end": v(-26210, 1050) * mm});
            skLineSegment(sketch, "E547.8", {"start": v(-26210, 1050) * mm, "end": v(-28210, 1050) * mm});
            skLineSegment(sketch, "E547.9", {"start": v(-28060, 3800) * mm, "end": v(-26360, 3800) * mm});
            skLineSegment(sketch, "E547.10", {"start": v(-26360, 3800) * mm, "end": v(-26360, 1100) * mm});
            skLineSegment(sketch, "E547.11", {"start": v(-28210, 3950) * mm, "end": v(-28210, 1050) * mm});
            skLineSegment(sketch, "E547.12", {"start": v(-26210, 3950) * mm, "end": v(-26210, 1050) * mm});
            skLineSegment(sketch, "E547.13", {"start": v(-26210, 3950) * mm, "end": v(-28210, 3950) * mm});
            skLineSegment(sketch, "E547.14", {"start": v(-28060, 1100) * mm, "end": v(-26360, 1100) * mm});
            skLineSegment(sketch, "E547.15", {"start": v(-28060, 3800) * mm, "end": v(-28060, 1100) * mm});
            skLineSegment(sketch, "E548.trimOffspring", {"start": v(-28210, 3850) * mm, "end": v(-28210, 3850) * mm});
            skLineSegment(sketch, "E549.0", {"start": v(-25410, 3850) * mm, "end": v(-25410, 1050) * mm});
            skLineSegment(sketch, "E549.1", {"start": v(-23410, 1050) * mm, "end": v(-23410, 3850) * mm});
            skLineSegment(sketch, "E549.2", {"start": v(-23510, 3850) * mm, "end": v(-25310, 3850) * mm});
            skLineSegment(sketch, "E549.3", {"start": v(-25310, 3850) * mm, "end": v(-25310, 1050) * mm});
            skLineSegment(sketch, "E549.4", {"start": v(-23510, 3850) * mm, "end": v(-25310, 3850) * mm});
            skLineSegment(sketch, "E549.5", {"start": v(-23510, 1050) * mm, "end": v(-23510, 3850) * mm});
            skLineSegment(sketch, "E549.6", {"start": v(-25410, 1050) * mm, "end": v(-25310, 1050) * mm});
            skLineSegment(sketch, "E549.7", {"start": v(-23510, 1050) * mm, "end": v(-23410, 1050) * mm});
            skLineSegment(sketch, "E549.8", {"start": v(-23410, 1050) * mm, "end": v(-25410, 1050) * mm});
            skLineSegment(sketch, "E549.9", {"start": v(-25260, 3800) * mm, "end": v(-23560, 3800) * mm});
            skLineSegment(sketch, "E549.10", {"start": v(-23560, 3800) * mm, "end": v(-23560, 1100) * mm});
            skLineSegment(sketch, "E549.11", {"start": v(-25410, 3950) * mm, "end": v(-25410, 1050) * mm});
            skLineSegment(sketch, "E549.12", {"start": v(-23410, 3950) * mm, "end": v(-23410, 1050) * mm});
            skLineSegment(sketch, "E549.13", {"start": v(-23410, 3950) * mm, "end": v(-25410, 3950) * mm});
            skLineSegment(sketch, "E549.14", {"start": v(-25260, 1100) * mm, "end": v(-23560, 1100) * mm});
            skLineSegment(sketch, "E549.15", {"start": v(-25260, 3800) * mm, "end": v(-25260, 1100) * mm});
            skLineSegment(sketch, "E550.trimOffspring", {"start": v(-25410, 3850) * mm, "end": v(-25410, 3850) * mm});
            skLineSegment(sketch, "E551.0", {"start": v(-22610, 3850) * mm, "end": v(-22610, 1050) * mm});
            skLineSegment(sketch, "E551.1", {"start": v(-20610, 1050) * mm, "end": v(-20610, 3850) * mm});
            skLineSegment(sketch, "E551.2", {"start": v(-20710, 3850) * mm, "end": v(-22510, 3850) * mm});
            skLineSegment(sketch, "E551.3", {"start": v(-22510, 3850) * mm, "end": v(-22510, 1050) * mm});
            skLineSegment(sketch, "E551.4", {"start": v(-20710, 3850) * mm, "end": v(-22510, 3850) * mm});
            skLineSegment(sketch, "E551.5", {"start": v(-20710, 1050) * mm, "end": v(-20710, 3850) * mm});
            skLineSegment(sketch, "E551.6", {"start": v(-22610, 1050) * mm, "end": v(-22510, 1050) * mm});
            skLineSegment(sketch, "E551.7", {"start": v(-20710, 1050) * mm, "end": v(-20610, 1050) * mm});
            skLineSegment(sketch, "E551.8", {"start": v(-20610, 1050) * mm, "end": v(-22610, 1050) * mm});
            skLineSegment(sketch, "E551.9", {"start": v(-22460, 3800) * mm, "end": v(-20760, 3800) * mm});
            skLineSegment(sketch, "E551.10", {"start": v(-20760, 3800) * mm, "end": v(-20760, 1100) * mm});
            skLineSegment(sketch, "E551.11", {"start": v(-22610, 3950) * mm, "end": v(-22610, 1050) * mm});
            skLineSegment(sketch, "E551.12", {"start": v(-20610, 3950) * mm, "end": v(-20610, 1050) * mm});
            skLineSegment(sketch, "E551.13", {"start": v(-20610, 3950) * mm, "end": v(-22610, 3950) * mm});
            skLineSegment(sketch, "E551.14", {"start": v(-22460, 1100) * mm, "end": v(-20760, 1100) * mm});
            skLineSegment(sketch, "E551.15", {"start": v(-22460, 3800) * mm, "end": v(-22460, 1100) * mm});
            skLineSegment(sketch, "E552.trimOffspring", {"start": v(-22610, 3850) * mm, "end": v(-22610, 3850) * mm});
            skLineSegment(sketch, "E553.1.0.0", {"start": v(-14010, 3950) * mm, "end": v(-16010, 3950) * mm});
            skPoint(sketch, "E553.1.0.1", {"position": v(-15860, 1100) * mm});
            skLineSegment(sketch, "E553.1.0.2", {"start": v(-18660, 1100) * mm, "end": v(-16960, 1100) * mm});
            skLineSegment(sketch, "E553.1.0.3", {"start": v(-13060, 1100) * mm, "end": v(-11360, 1100) * mm});
            skLineSegment(sketch, "E553.1.0.4", {"start": v(-15860, 3800) * mm, "end": v(-15860, 1100) * mm});
            skLineSegment(sketch, "E553.1.0.5", {"start": v(-11210, 3950) * mm, "end": v(-13210, 3950) * mm});
            skPoint(sketch, "E553.1.0.6", {"position": v(-18660, 1100) * mm});
            skLineSegment(sketch, "E553.1.0.7", {"start": v(-18660, 3800) * mm, "end": v(-16960, 3800) * mm});
            skLineSegment(sketch, "E553.1.0.8", {"start": v(-14010, 1050) * mm, "end": v(-16010, 1050) * mm});
            skLineSegment(sketch, "E553.1.0.9", {"start": v(-14160, 3800) * mm, "end": v(-14160, 1100) * mm});
            skLineSegment(sketch, "E553.1.0.10", {"start": v(-13060, 3800) * mm, "end": v(-11360, 3800) * mm});
            skLineSegment(sketch, "E553.1.0.11", {"start": v(-18810, 3950) * mm, "end": v(-18810, 1050) * mm});
            skLineSegment(sketch, "E553.1.0.12", {"start": v(-16810, 1050) * mm, "end": v(-18810, 1050) * mm});
            skPoint(sketch, "E553.1.0.13", {"position": v(-13060, 1100) * mm});
            skLineSegment(sketch, "E553.1.0.14", {"start": v(-18660, 3800) * mm, "end": v(-18660, 1100) * mm});
            skLineSegment(sketch, "E553.1.0.15", {"start": v(-16810, 3950) * mm, "end": v(-18810, 3950) * mm});
            skLineSegment(sketch, "E553.1.0.16", {"start": v(-11310, 3850) * mm, "end": v(-13110, 3850) * mm});
            skLineSegment(sketch, "E553.1.0.17", {"start": v(-14010, 3950) * mm, "end": v(-14010, 1050) * mm});
            skLineSegment(sketch, "E553.1.0.18", {"start": v(-13210, 3950) * mm, "end": v(-13210, 1050) * mm});
            skLineSegment(sketch, "E553.1.0.19", {"start": v(-16960, 3800) * mm, "end": v(-16960, 1100) * mm});
            skLineSegment(sketch, "E553.1.0.20", {"start": v(-13060, 3800) * mm, "end": v(-13060, 1100) * mm});
            skLineSegment(sketch, "E553.1.0.21", {"start": v(-15860, 3800) * mm, "end": v(-14160, 3800) * mm});
            skLineSegment(sketch, "E553.1.0.22", {"start": v(-14110, 3850) * mm, "end": v(-15910, 3850) * mm});
            skLineSegment(sketch, "E553.1.0.23", {"start": v(-18710, 3850) * mm, "end": v(-18710, 1050) * mm});
            skLineSegment(sketch, "E553.1.0.24", {"start": v(-16810, 3950) * mm, "end": v(-16810, 1050) * mm});
            skLineSegment(sketch, "E553.1.0.25", {"start": v(-16010, 3950) * mm, "end": v(-16010, 1050) * mm});
            skLineSegment(sketch, "E553.1.0.26", {"start": v(-11210, 1050) * mm, "end": v(-11210, 3850) * mm});
            skLineSegment(sketch, "E553.1.0.27", {"start": v(-11360, 3800) * mm, "end": v(-11360, 1100) * mm});
            skLineSegment(sketch, "E553.1.0.28", {"start": v(-16910, 3850) * mm, "end": v(-18710, 3850) * mm});
            skLineSegment(sketch, "E553.1.0.29", {"start": v(-15860, 1100) * mm, "end": v(-14160, 1100) * mm});
            skLineSegment(sketch, "E553.1.0.30", {"start": v(-11210, 1050) * mm, "end": v(-13210, 1050) * mm});
            skLineSegment(sketch, "E553.1.0.31", {"start": v(-11310, 1050) * mm, "end": v(-11310, 3850) * mm});
            skLineSegment(sketch, "E553.1.0.32", {"start": v(-13110, 3850) * mm, "end": v(-13110, 1050) * mm});
            skLineSegment(sketch, "E553.1.0.33", {"start": v(-14110, 3850) * mm, "end": v(-15910, 3850) * mm});
            skLineSegment(sketch, "E553.1.0.34", {"start": v(-16910, 1050) * mm, "end": v(-16910, 3850) * mm});
            skLineSegment(sketch, "E553.1.0.35", {"start": v(-11210, 3950) * mm, "end": v(-11210, 1050) * mm});
            skLineSegment(sketch, "E553.1.0.36", {"start": v(-14110, 1050) * mm, "end": v(-14110, 3850) * mm});
            skLineSegment(sketch, "E553.1.0.37", {"start": v(-11310, 3850) * mm, "end": v(-13110, 3850) * mm});
            skPoint(sketch, "E553.1.0.38", {"position": v(-15860, 1100) * mm});
            skLineSegment(sketch, "E553.1.0.39", {"start": v(-13210, 3850) * mm, "end": v(-13210, 1050) * mm});
            skLineSegment(sketch, "E553.1.0.40", {"start": v(-16910, 3850) * mm, "end": v(-18710, 3850) * mm});
            skLineSegment(sketch, "E553.1.0.41", {"start": v(-14010, 1050) * mm, "end": v(-14010, 3850) * mm});
            skLineSegment(sketch, "E553.1.0.42", {"start": v(-16810, 1050) * mm, "end": v(-16810, 3850) * mm});
            skLineSegment(sketch, "E553.1.0.43", {"start": v(-15910, 3850) * mm, "end": v(-15910, 1050) * mm});
            skPoint(sketch, "E553.1.0.44", {"position": v(-13060, 1100) * mm});
            skLineSegment(sketch, "E553.1.0.45", {"start": v(-18810, 3850) * mm, "end": v(-18810, 1050) * mm});
            skPoint(sketch, "E553.1.0.46", {"position": v(-18660, 1100) * mm});
            skLineSegment(sketch, "E553.1.0.47", {"start": v(-16010, 3850) * mm, "end": v(-16010, 1050) * mm});
            skLineSegment(sketch, "E553.1.0.48", {"start": v(-16910, 1050) * mm, "end": v(-16810, 1050) * mm});
            skLineSegment(sketch, "E553.1.0.49", {"start": v(-18810, 1050) * mm, "end": v(-18710, 1050) * mm});
            skLineSegment(sketch, "E553.1.0.50", {"start": v(-11310, 1050) * mm, "end": v(-11210, 1050) * mm});
            skLineSegment(sketch, "E553.1.0.51", {"start": v(-13210, 3850) * mm, "end": v(-13210, 3850) * mm});
            skLineSegment(sketch, "E553.1.0.52", {"start": v(-14110, 1050) * mm, "end": v(-14010, 1050) * mm});
            skLineSegment(sketch, "E553.1.0.53", {"start": v(-18810, 3850) * mm, "end": v(-18810, 3850) * mm});
            skLineSegment(sketch, "E553.1.0.54", {"start": v(-13210, 1050) * mm, "end": v(-13110, 1050) * mm});
            skLineSegment(sketch, "E553.1.0.55", {"start": v(-16010, 3850) * mm, "end": v(-16010, 3850) * mm});
            skLineSegment(sketch, "E553.1.0.56", {"start": v(-16010, 1050) * mm, "end": v(-15910, 1050) * mm});
            skLineSegment(sketch, "E553.2.0.0", {"start": v(-4610, 3950) * mm, "end": v(-6610, 3950) * mm});
            skPoint(sketch, "E553.2.0.1", {"position": v(-6460, 1100) * mm});
            skLineSegment(sketch, "E553.2.0.2", {"start": v(-9260, 1100) * mm, "end": v(-7560, 1100) * mm});
            skLineSegment(sketch, "E553.2.0.3", {"start": v(-3660, 1100) * mm, "end": v(-1960, 1100) * mm});
            skLineSegment(sketch, "E553.2.0.4", {"start": v(-6460, 3800) * mm, "end": v(-6460, 1100) * mm});
            skLineSegment(sketch, "E553.2.0.5", {"start": v(-1810, 3950) * mm, "end": v(-3810, 3950) * mm});
            skPoint(sketch, "E553.2.0.6", {"position": v(-9260, 1100) * mm});
            skLineSegment(sketch, "E553.2.0.7", {"start": v(-9260, 3800) * mm, "end": v(-7560, 3800) * mm});
            skLineSegment(sketch, "E553.2.0.8", {"start": v(-4610, 1050) * mm, "end": v(-6610, 1050) * mm});
            skLineSegment(sketch, "E553.2.0.9", {"start": v(-4760, 3800) * mm, "end": v(-4760, 1100) * mm});
            skLineSegment(sketch, "E553.2.0.10", {"start": v(-3660, 3800) * mm, "end": v(-1960, 3800) * mm});
            skLineSegment(sketch, "E553.2.0.11", {"start": v(-9410, 3950) * mm, "end": v(-9410, 1050) * mm});
            skLineSegment(sketch, "E553.2.0.12", {"start": v(-7410, 1050) * mm, "end": v(-9410, 1050) * mm});
            skPoint(sketch, "E553.2.0.13", {"position": v(-3660, 1100) * mm});
            skLineSegment(sketch, "E553.2.0.14", {"start": v(-9260, 3800) * mm, "end": v(-9260, 1100) * mm});
            skLineSegment(sketch, "E553.2.0.15", {"start": v(-7410, 3950) * mm, "end": v(-9410, 3950) * mm});
            skLineSegment(sketch, "E553.2.0.16", {"start": v(-1910, 3850) * mm, "end": v(-3710, 3850) * mm});
            skLineSegment(sketch, "E553.2.0.17", {"start": v(-4610, 3950) * mm, "end": v(-4610, 1050) * mm});
            skLineSegment(sketch, "E553.2.0.18", {"start": v(-3810, 3950) * mm, "end": v(-3810, 1050) * mm});
            skLineSegment(sketch, "E553.2.0.19", {"start": v(-7560, 3800) * mm, "end": v(-7560, 1100) * mm});
            skLineSegment(sketch, "E553.2.0.20", {"start": v(-3660, 3800) * mm, "end": v(-3660, 1100) * mm});
            skLineSegment(sketch, "E553.2.0.21", {"start": v(-6460, 3800) * mm, "end": v(-4760, 3800) * mm});
            skLineSegment(sketch, "E553.2.0.22", {"start": v(-4710, 3850) * mm, "end": v(-6510, 3850) * mm});
            skLineSegment(sketch, "E553.2.0.23", {"start": v(-9310, 3850) * mm, "end": v(-9310, 1050) * mm});
            skLineSegment(sketch, "E553.2.0.24", {"start": v(-7410, 3950) * mm, "end": v(-7410, 1050) * mm});
            skLineSegment(sketch, "E553.2.0.25", {"start": v(-6610, 3950) * mm, "end": v(-6610, 1050) * mm});
            skLineSegment(sketch, "E553.2.0.26", {"start": v(-1810, 1050) * mm, "end": v(-1810, 3850) * mm});
            skLineSegment(sketch, "E553.2.0.27", {"start": v(-1960, 3800) * mm, "end": v(-1960, 1100) * mm});
            skLineSegment(sketch, "E553.2.0.28", {"start": v(-7510, 3850) * mm, "end": v(-9310, 3850) * mm});
            skLineSegment(sketch, "E553.2.0.29", {"start": v(-6460, 1100) * mm, "end": v(-4760, 1100) * mm});
            skLineSegment(sketch, "E553.2.0.30", {"start": v(-1810, 1050) * mm, "end": v(-3810, 1050) * mm});
            skLineSegment(sketch, "E553.2.0.31", {"start": v(-1910, 1050) * mm, "end": v(-1910, 3850) * mm});
            skLineSegment(sketch, "E553.2.0.32", {"start": v(-3710, 3850) * mm, "end": v(-3710, 1050) * mm});
            skLineSegment(sketch, "E553.2.0.33", {"start": v(-4710, 3850) * mm, "end": v(-6510, 3850) * mm});
            skLineSegment(sketch, "E553.2.0.34", {"start": v(-7510, 1050) * mm, "end": v(-7510, 3850) * mm});
            skLineSegment(sketch, "E553.2.0.35", {"start": v(-1810, 3950) * mm, "end": v(-1810, 1050) * mm});
            skLineSegment(sketch, "E553.2.0.36", {"start": v(-4710, 1050) * mm, "end": v(-4710, 3850) * mm});
            skLineSegment(sketch, "E553.2.0.37", {"start": v(-1910, 3850) * mm, "end": v(-3710, 3850) * mm});
            skPoint(sketch, "E553.2.0.38", {"position": v(-6460, 1100) * mm});
            skLineSegment(sketch, "E553.2.0.39", {"start": v(-3810, 3850) * mm, "end": v(-3810, 1050) * mm});
            skLineSegment(sketch, "E553.2.0.40", {"start": v(-7510, 3850) * mm, "end": v(-9310, 3850) * mm});
            skLineSegment(sketch, "E553.2.0.41", {"start": v(-4610, 1050) * mm, "end": v(-4610, 3850) * mm});
            skLineSegment(sketch, "E553.2.0.42", {"start": v(-7410, 1050) * mm, "end": v(-7410, 3850) * mm});
            skLineSegment(sketch, "E553.2.0.43", {"start": v(-6510, 3850) * mm, "end": v(-6510, 1050) * mm});
            skPoint(sketch, "E553.2.0.44", {"position": v(-3660, 1100) * mm});
            skLineSegment(sketch, "E553.2.0.45", {"start": v(-9410, 3850) * mm, "end": v(-9410, 1050) * mm});
            skPoint(sketch, "E553.2.0.46", {"position": v(-9260, 1100) * mm});
            skLineSegment(sketch, "E553.2.0.47", {"start": v(-6610, 3850) * mm, "end": v(-6610, 1050) * mm});
            skLineSegment(sketch, "E553.2.0.48", {"start": v(-7510, 1050) * mm, "end": v(-7410, 1050) * mm});
            skLineSegment(sketch, "E553.2.0.49", {"start": v(-9410, 1050) * mm, "end": v(-9310, 1050) * mm});
            skLineSegment(sketch, "E553.2.0.50", {"start": v(-1910, 1050) * mm, "end": v(-1810, 1050) * mm});
            skLineSegment(sketch, "E553.2.0.51", {"start": v(-3810, 3850) * mm, "end": v(-3810, 3850) * mm});
            skLineSegment(sketch, "E553.2.0.52", {"start": v(-4710, 1050) * mm, "end": v(-4610, 1050) * mm});
            skLineSegment(sketch, "E553.2.0.53", {"start": v(-9410, 3850) * mm, "end": v(-9410, 3850) * mm});
            skLineSegment(sketch, "E553.2.0.54", {"start": v(-3810, 1050) * mm, "end": v(-3710, 1050) * mm});
            skLineSegment(sketch, "E553.2.0.55", {"start": v(-6610, 3850) * mm, "end": v(-6610, 3850) * mm});
            skLineSegment(sketch, "E553.2.0.56", {"start": v(-6610, 1050) * mm, "end": v(-6510, 1050) * mm});
            skLineSegment(sketch, "E553.direction1", {"start": v(-28210, 1050) * mm, "end": v(-18810, 1050) * mm, "construction": true});
            skLineSegment(sketch, "E554.0.0", {"start": v(-31060, 1100) * mm, "end": v(-31060, 3800) * mm});
            skLineSegment(sketch, "E554.0.2", {"start": v(-32160, 3800) * mm, "end": v(-32160, 1100) * mm});
            skLineSegment(sketch, "E554.0.3", {"start": v(-32160, 1100) * mm, "end": v(-31060, 1100) * mm});
            skLineSegment(sketch, "E555.bottom", {"start": v(-32310, 3950) * mm, "end": v(-30910, 3950) * mm});
            skLineSegment(sketch, "E555.top", {"start": v(-32310, 1050) * mm, "end": v(-30910, 1050) * mm});
            skLineSegment(sketch, "E555.left", {"start": v(-32310, 3950) * mm, "end": v(-32310, 1050) * mm});
            skLineSegment(sketch, "E555.right", {"start": v(-30910, 3950) * mm, "end": v(-30910, 1050) * mm});
            skLineSegment(sketch, "E556", {"start": v(-32210, 1050) * mm, "end": v(-32210, 3850) * mm});
            skLineSegment(sketch, "E557", {"start": v(-32210, 3850) * mm, "end": v(-31010, 3850) * mm});
            skLineSegment(sketch, "E558", {"start": v(-31010, 3850) * mm, "end": v(-31010, 1050) * mm});
            skLineSegment(sketch, "E559", {"start": v(-32160, 3800) * mm, "end": v(-31060, 3800) * mm});
            skSolve(sketch);
        }
        {
            var Q0;
            {var subQ11=sQuery(id+"F64.wireOp",EDGE,"E543.3");Q0=makeQuery(id+"F64.imprint","IMPRINT",FACE,{"disambiguationData":[TD([[makeQuery(id+"F64.imprint","IMPRINT",EDGE,{"derivedFrom":subQ11}),1.0]])]});}
            var Q1;
            {var subQ5=sQuery(id+"F64.wireOp",EDGE,"E543.3");Q1=makeQuery(id+"F64.imprint","IMPRINT",FACE,{"disambiguationData":[TD([[makeQuery(id+"F64.imprint","IMPRINT",EDGE,{"derivedFrom":subQ5}),-1.0]])]});}
            var Q2;
            {var subQ5=sQuery(id+"F64.wireOp",EDGE,"E545.3");Q2=makeQuery(id+"F64.imprint","IMPRINT",FACE,{"disambiguationData":[TD([[makeQuery(id+"F64.imprint","IMPRINT",EDGE,{"derivedFrom":subQ5}),-1.0]])]});}
            var Q3;
            {var subQ10=sQuery(id+"F64.wireOp",EDGE,"E545.3");Q3=makeQuery(id+"F64.imprint","IMPRINT",FACE,{"disambiguationData":[TD([[makeQuery(id+"F64.imprint","IMPRINT",EDGE,{"derivedFrom":subQ10}),1.0]])]});}
            var Q4;
            Q4=makeQuery(id+"F64.imprint","IMPRINT",FACE,{"disambiguationData":[TD([[makeQuery(id+"F64.imprint","IMPRINT",EDGE,{"derivedFrom":sQuery(id+"F64.wireOp",EDGE,"E555.bottom")}),-1.0]])]});
            var Q5;
            Q5=makeQuery(id+"F64.imprint","IMPRINT",FACE,{"disambiguationData":[TD([[makeQuery(id+"F64.imprint","IMPRINT",EDGE,{"derivedFrom":sQuery(id+"F64.wireOp",EDGE,"E554.0.0")}),1.0]])]});
            var Q6;
            {var subQ7=sQuery(id+"F64.wireOp",EDGE,"E547.3");Q6=makeQuery(id+"F64.imprint","IMPRINT",FACE,{"disambiguationData":[TD([[makeQuery(id+"F64.imprint","IMPRINT",EDGE,{"derivedFrom":subQ7}),-1.0]])]});}
            var Q7;
            {var subQ14=sQuery(id+"F64.wireOp",EDGE,"E547.3");Q7=makeQuery(id+"F64.imprint","IMPRINT",FACE,{"disambiguationData":[TD([[makeQuery(id+"F64.imprint","IMPRINT",EDGE,{"derivedFrom":subQ14}),1.0]])]});}
            var Q8;
            {var subQ7=sQuery(id+"F64.wireOp",EDGE,"E549.3");Q8=makeQuery(id+"F64.imprint","IMPRINT",FACE,{"disambiguationData":[TD([[makeQuery(id+"F64.imprint","IMPRINT",EDGE,{"derivedFrom":subQ7}),-1.0]])]});}
            var Q9;
            {var subQ13=sQuery(id+"F64.wireOp",EDGE,"E549.3");Q9=makeQuery(id+"F64.imprint","IMPRINT",FACE,{"disambiguationData":[TD([[makeQuery(id+"F64.imprint","IMPRINT",EDGE,{"derivedFrom":subQ13}),1.0]])]});}
            var Q10;
            {var subQ7=sQuery(id+"F64.wireOp",EDGE,"E551.3");Q10=makeQuery(id+"F64.imprint","IMPRINT",FACE,{"disambiguationData":[TD([[makeQuery(id+"F64.imprint","IMPRINT",EDGE,{"derivedFrom":subQ7}),-1.0]])]});}
            var Q11;
            {var subQ18=sQuery(id+"F64.wireOp",EDGE,"E551.3");Q11=makeQuery(id+"F64.imprint","IMPRINT",FACE,{"disambiguationData":[TD([[makeQuery(id+"F64.imprint","IMPRINT",EDGE,{"derivedFrom":subQ18}),1.0]])]});}
            var Q12;
            {var subQ3=sQuery(id+"F64.wireOp",EDGE,"E553.1.0.15");Q12=makeQuery(id+"F64.imprint","IMPRINT",FACE,{"disambiguationData":[TD([[makeQuery(id+"F64.imprint","IMPRINT",EDGE,{"derivedFrom":subQ3}),1.0]])]});}
            var Q13;
            {var subQ5=sQuery(id+"F64.wireOp",EDGE,"E553.1.0.23");Q13=makeQuery(id+"F64.imprint","IMPRINT",FACE,{"disambiguationData":[TD([[makeQuery(id+"F64.imprint","IMPRINT",EDGE,{"derivedFrom":subQ5}),1.0]])]});}
            var Q14;
            {var subQ1=sQuery(id+"F64.wireOp",EDGE,"E553.1.0.0");Q14=makeQuery(id+"F64.imprint","IMPRINT",FACE,{"disambiguationData":[TD([[makeQuery(id+"F64.imprint","IMPRINT",EDGE,{"derivedFrom":subQ1}),1.0]])]});}
            var Q15;
            {var subQ4=sQuery(id+"F64.wireOp",EDGE,"E553.1.0.4");Q15=makeQuery(id+"F64.imprint","IMPRINT",FACE,{"disambiguationData":[TD([[makeQuery(id+"F64.imprint","IMPRINT",EDGE,{"derivedFrom":subQ4}),-1.0]])]});}
            var Q16;
            {var subQ4=sQuery(id+"F64.wireOp",EDGE,"E553.1.0.5");Q16=makeQuery(id+"F64.imprint","IMPRINT",FACE,{"disambiguationData":[TD([[makeQuery(id+"F64.imprint","IMPRINT",EDGE,{"derivedFrom":subQ4}),1.0]])]});}
            var Q17;
            {var subQ1=sQuery(id+"F64.wireOp",EDGE,"E553.1.0.31");Q17=makeQuery(id+"F64.imprint","IMPRINT",FACE,{"disambiguationData":[TD([[makeQuery(id+"F64.imprint","IMPRINT",EDGE,{"derivedFrom":subQ1}),1.0]])]});}
            var Q18;
            {var subQ3=sQuery(id+"F64.wireOp",EDGE,"E553.2.0.15");Q18=makeQuery(id+"F64.imprint","IMPRINT",FACE,{"disambiguationData":[TD([[makeQuery(id+"F64.imprint","IMPRINT",EDGE,{"derivedFrom":subQ3}),1.0]])]});}
            var Q19;
            {var subQ5=sQuery(id+"F64.wireOp",EDGE,"E553.2.0.23");Q19=makeQuery(id+"F64.imprint","IMPRINT",FACE,{"disambiguationData":[TD([[makeQuery(id+"F64.imprint","IMPRINT",EDGE,{"derivedFrom":subQ5}),1.0]])]});}
            var Q20;
            {var subQ1=sQuery(id+"F64.wireOp",EDGE,"E553.2.0.0");Q20=makeQuery(id+"F64.imprint","IMPRINT",FACE,{"disambiguationData":[TD([[makeQuery(id+"F64.imprint","IMPRINT",EDGE,{"derivedFrom":subQ1}),1.0]])]});}
            var Q21;
            {var subQ4=sQuery(id+"F64.wireOp",EDGE,"E553.2.0.4");Q21=makeQuery(id+"F64.imprint","IMPRINT",FACE,{"disambiguationData":[TD([[makeQuery(id+"F64.imprint","IMPRINT",EDGE,{"derivedFrom":subQ4}),-1.0]])]});}
            var Q22;
            {var subQ4=sQuery(id+"F64.wireOp",EDGE,"E553.2.0.5");Q22=makeQuery(id+"F64.imprint","IMPRINT",FACE,{"disambiguationData":[TD([[makeQuery(id+"F64.imprint","IMPRINT",EDGE,{"derivedFrom":subQ4}),1.0]])]});}
            var Q23;
            {var subQ1=sQuery(id+"F64.wireOp",EDGE,"E553.2.0.31");Q23=makeQuery(id+"F64.imprint","IMPRINT",FACE,{"disambiguationData":[TD([[makeQuery(id+"F64.imprint","IMPRINT",EDGE,{"derivedFrom":subQ1}),1.0]])]});}
            extrude(context, id + "F65", {"entities" : qUnion([Q0, Q1, Q2, Q3, Q4, Q5, Q6, Q7, Q8, Q9, Q10, Q11, Q12, Q13, Q14, Q15, Q16, Q17, Q18, Q19, Q20, Q21, Q22, Q23]), "depth" : 50 * mm, "offsetDistance" : 25 * mm});
        }
        {
            var Q0;
            Q0=makeQuery(id+"F65.opExtrude","CAP_FACE",FACE,{"disambiguationData":[OSD([sQuery(id+"F18.wireOp",EDGE,"E233.bottom"),sQuery(id+"F18.wireOp",EDGE,"E233.top"),sQuery(id+"F18.wireOp",EDGE,"E233.right"),sQuery(id+"F64.wireOp",EDGE,"E543.8"),sQuery(id+"F64.wireOp",EDGE,"E543.9"),sQuery(id+"F64.wireOp",EDGE,"E543.11"),sQuery(id+"F64.wireOp",EDGE,"E543.12"),sQuery(id+"F64.wireOp",EDGE,"E543.13"),sQuery(id+"F64.wireOp",EDGE,"E543.14"),sQuery(id+"F64.wireOp",EDGE,"E543.15")])],"isStart":false});
            var sketch = newSketch(context, id + "F66", { "sketchPlane" : qUnion([Q0])});
            skPoint(sketch, "E560.0", {"position": v(-38060, 1100) * mm});
            skPoint(sketch, "E560.1", {"position": v(-35760, 1100) * mm});
            skPoint(sketch, "E560.2", {"position": v(-35760, 1100) * mm});
            skPoint(sketch, "E560.3", {"position": v(-25260, 1100) * mm});
            skPoint(sketch, "E560.4", {"position": v(-22460, 1100) * mm});
            skPoint(sketch, "E560.5", {"position": v(-28060, 1100) * mm});
            skLineSegment(sketch, "E560.6", {"start": v(-38210, 3850) * mm, "end": v(-38210, 1050) * mm});
            skLineSegment(sketch, "E560.7", {"start": v(-36210, 1050) * mm, "end": v(-36210, 3850) * mm});
            skLineSegment(sketch, "E560.8", {"start": v(-36310, 3850) * mm, "end": v(-38110, 3850) * mm});
            skLineSegment(sketch, "E560.9", {"start": v(-38110, 3850) * mm, "end": v(-38110, 1050) * mm});
            skLineSegment(sketch, "E560.10", {"start": v(-36310, 3850) * mm, "end": v(-38110, 3850) * mm});
            skLineSegment(sketch, "E560.11", {"start": v(-36310, 1050) * mm, "end": v(-36310, 3850) * mm});
            skLineSegment(sketch, "E560.12", {"start": v(-38210, 1050) * mm, "end": v(-38110, 1050) * mm});
            skLineSegment(sketch, "E560.13", {"start": v(-36310, 1050) * mm, "end": v(-36210, 1050) * mm});
            skLineSegment(sketch, "E560.14", {"start": v(-36210, 1050) * mm, "end": v(-38210, 1050) * mm});
            skLineSegment(sketch, "E560.15", {"start": v(-38060, 3800) * mm, "end": v(-36360, 3800) * mm});
            skLineSegment(sketch, "E560.16", {"start": v(-36360, 3800) * mm, "end": v(-36360, 1100) * mm});
            skLineSegment(sketch, "E560.17", {"start": v(-38210, 3950) * mm, "end": v(-38210, 1050) * mm});
            skLineSegment(sketch, "E560.18", {"start": v(-36210, 3950) * mm, "end": v(-36210, 1050) * mm});
            skLineSegment(sketch, "E560.19", {"start": v(-36210, 3950) * mm, "end": v(-38210, 3950) * mm});
            skLineSegment(sketch, "E560.20", {"start": v(-38060, 1100) * mm, "end": v(-36360, 1100) * mm});
            skLineSegment(sketch, "E560.21", {"start": v(-38060, 3800) * mm, "end": v(-38060, 1100) * mm});
            skLineSegment(sketch, "E560.22", {"start": v(-38210, 3850) * mm, "end": v(-38210, 3850) * mm});
            skPoint(sketch, "E560.23", {"position": v(-35760, 1100) * mm});
            skLineSegment(sketch, "E560.24", {"start": v(-35910, 3850) * mm, "end": v(-35910, 1050) * mm});
            skLineSegment(sketch, "E560.25", {"start": v(-33910, 1050) * mm, "end": v(-33910, 3850) * mm});
            skLineSegment(sketch, "E560.26", {"start": v(-34010, 3850) * mm, "end": v(-35810, 3850) * mm});
            skLineSegment(sketch, "E560.27", {"start": v(-35810, 3850) * mm, "end": v(-35810, 1050) * mm});
            skLineSegment(sketch, "E560.28", {"start": v(-34010, 3850) * mm, "end": v(-35810, 3850) * mm});
            skLineSegment(sketch, "E560.29", {"start": v(-34010, 1050) * mm, "end": v(-34010, 3850) * mm});
            skLineSegment(sketch, "E560.30", {"start": v(-35910, 1050) * mm, "end": v(-35810, 1050) * mm});
            skLineSegment(sketch, "E560.31", {"start": v(-34010, 1050) * mm, "end": v(-33910, 1050) * mm});
            skLineSegment(sketch, "E560.32", {"start": v(-33910, 1050) * mm, "end": v(-35910, 1050) * mm});
            skLineSegment(sketch, "E560.33", {"start": v(-35760, 3800) * mm, "end": v(-34060, 3800) * mm});
            skLineSegment(sketch, "E560.34", {"start": v(-34060, 3800) * mm, "end": v(-34060, 1100) * mm});
            skLineSegment(sketch, "E560.35", {"start": v(-35910, 3950) * mm, "end": v(-35910, 1050) * mm});
            skLineSegment(sketch, "E560.36", {"start": v(-33910, 3950) * mm, "end": v(-33910, 1050) * mm});
            skLineSegment(sketch, "E560.37", {"start": v(-33910, 3950) * mm, "end": v(-35910, 3950) * mm});
            skLineSegment(sketch, "E560.38", {"start": v(-35760, 1100) * mm, "end": v(-34060, 1100) * mm});
            skLineSegment(sketch, "E560.39", {"start": v(-35760, 3800) * mm, "end": v(-35760, 1100) * mm});
            skLineSegment(sketch, "E560.40", {"start": v(-35910, 3850) * mm, "end": v(-35910, 3850) * mm});
            skPoint(sketch, "E560.41", {"position": v(-28060, 1100) * mm});
            skLineSegment(sketch, "E560.42", {"start": v(-28210, 3850) * mm, "end": v(-28210, 1050) * mm});
            skLineSegment(sketch, "E560.43", {"start": v(-26210, 1050) * mm, "end": v(-26210, 3850) * mm});
            skLineSegment(sketch, "E560.44", {"start": v(-26310, 3850) * mm, "end": v(-28110, 3850) * mm});
            skLineSegment(sketch, "E560.45", {"start": v(-28110, 3850) * mm, "end": v(-28110, 1050) * mm});
            skLineSegment(sketch, "E560.46", {"start": v(-26310, 3850) * mm, "end": v(-28110, 3850) * mm});
            skLineSegment(sketch, "E560.47", {"start": v(-26310, 1050) * mm, "end": v(-26310, 3850) * mm});
            skLineSegment(sketch, "E560.48", {"start": v(-28210, 1050) * mm, "end": v(-28110, 1050) * mm});
            skLineSegment(sketch, "E560.49", {"start": v(-26310, 1050) * mm, "end": v(-26210, 1050) * mm});
            skLineSegment(sketch, "E560.50", {"start": v(-26210, 1050) * mm, "end": v(-28210, 1050) * mm});
            skLineSegment(sketch, "E560.51", {"start": v(-28060, 3800) * mm, "end": v(-26360, 3800) * mm});
            skLineSegment(sketch, "E560.52", {"start": v(-26360, 3800) * mm, "end": v(-26360, 1100) * mm});
            skLineSegment(sketch, "E560.53", {"start": v(-28210, 3950) * mm, "end": v(-28210, 1050) * mm});
            skLineSegment(sketch, "E560.54", {"start": v(-26210, 3950) * mm, "end": v(-26210, 1050) * mm});
            skLineSegment(sketch, "E560.55", {"start": v(-26210, 3950) * mm, "end": v(-28210, 3950) * mm});
            skLineSegment(sketch, "E560.56", {"start": v(-28060, 1100) * mm, "end": v(-26360, 1100) * mm});
            skLineSegment(sketch, "E560.57", {"start": v(-28060, 3800) * mm, "end": v(-28060, 1100) * mm});
            skLineSegment(sketch, "E560.58", {"start": v(-28210, 3850) * mm, "end": v(-28210, 3850) * mm});
            skPoint(sketch, "E560.59", {"position": v(-25260, 1100) * mm});
            skLineSegment(sketch, "E560.60", {"start": v(-25410, 3850) * mm, "end": v(-25410, 1050) * mm});
            skLineSegment(sketch, "E560.61", {"start": v(-23410, 1050) * mm, "end": v(-23410, 3850) * mm});
            skLineSegment(sketch, "E560.62", {"start": v(-23510, 3850) * mm, "end": v(-25310, 3850) * mm});
            skLineSegment(sketch, "E560.63", {"start": v(-25310, 3850) * mm, "end": v(-25310, 1050) * mm});
            skLineSegment(sketch, "E560.64", {"start": v(-23510, 3850) * mm, "end": v(-25310, 3850) * mm});
            skLineSegment(sketch, "E560.65", {"start": v(-23510, 1050) * mm, "end": v(-23510, 3850) * mm});
            skLineSegment(sketch, "E560.66", {"start": v(-25410, 1050) * mm, "end": v(-25310, 1050) * mm});
            skLineSegment(sketch, "E560.67", {"start": v(-23510, 1050) * mm, "end": v(-23410, 1050) * mm});
            skLineSegment(sketch, "E560.68", {"start": v(-23410, 1050) * mm, "end": v(-25410, 1050) * mm});
            skLineSegment(sketch, "E560.69", {"start": v(-25260, 3800) * mm, "end": v(-23560, 3800) * mm});
            skLineSegment(sketch, "E560.70", {"start": v(-23560, 3800) * mm, "end": v(-23560, 1100) * mm});
            skLineSegment(sketch, "E560.71", {"start": v(-25410, 3950) * mm, "end": v(-25410, 1050) * mm});
            skLineSegment(sketch, "E560.72", {"start": v(-23410, 3950) * mm, "end": v(-23410, 1050) * mm});
            skLineSegment(sketch, "E560.73", {"start": v(-23410, 3950) * mm, "end": v(-25410, 3950) * mm});
            skLineSegment(sketch, "E560.74", {"start": v(-25260, 1100) * mm, "end": v(-23560, 1100) * mm});
            skLineSegment(sketch, "E560.75", {"start": v(-25260, 3800) * mm, "end": v(-25260, 1100) * mm});
            skLineSegment(sketch, "E560.76", {"start": v(-25410, 3850) * mm, "end": v(-25410, 3850) * mm});
            skPoint(sketch, "E560.77", {"position": v(-22460, 1100) * mm});
            skLineSegment(sketch, "E560.78", {"start": v(-22610, 3850) * mm, "end": v(-22610, 1050) * mm});
            skLineSegment(sketch, "E560.79", {"start": v(-20610, 1050) * mm, "end": v(-20610, 3850) * mm});
            skLineSegment(sketch, "E560.80", {"start": v(-20710, 3850) * mm, "end": v(-22510, 3850) * mm});
            skLineSegment(sketch, "E560.81", {"start": v(-22510, 3850) * mm, "end": v(-22510, 1050) * mm});
            skLineSegment(sketch, "E560.82", {"start": v(-20710, 3850) * mm, "end": v(-22510, 3850) * mm});
            skLineSegment(sketch, "E560.83", {"start": v(-20710, 1050) * mm, "end": v(-20710, 3850) * mm});
            skLineSegment(sketch, "E560.84", {"start": v(-22610, 1050) * mm, "end": v(-22510, 1050) * mm});
            skLineSegment(sketch, "E560.85", {"start": v(-20710, 1050) * mm, "end": v(-20610, 1050) * mm});
            skLineSegment(sketch, "E560.86", {"start": v(-20610, 1050) * mm, "end": v(-22610, 1050) * mm});
            skLineSegment(sketch, "E560.87", {"start": v(-22460, 3800) * mm, "end": v(-20760, 3800) * mm});
            skLineSegment(sketch, "E560.88", {"start": v(-20760, 3800) * mm, "end": v(-20760, 1100) * mm});
            skLineSegment(sketch, "E560.89", {"start": v(-22610, 3950) * mm, "end": v(-22610, 1050) * mm});
            skLineSegment(sketch, "E560.90", {"start": v(-20610, 3950) * mm, "end": v(-20610, 1050) * mm});
            skLineSegment(sketch, "E560.91", {"start": v(-20610, 3950) * mm, "end": v(-22610, 3950) * mm});
            skLineSegment(sketch, "E560.92", {"start": v(-22460, 1100) * mm, "end": v(-20760, 1100) * mm});
            skLineSegment(sketch, "E560.93", {"start": v(-22460, 3800) * mm, "end": v(-22460, 1100) * mm});
            skLineSegment(sketch, "E560.94", {"start": v(-22610, 3850) * mm, "end": v(-22610, 3850) * mm});
            skLineSegment(sketch, "E560.95", {"start": v(-14010, 3950) * mm, "end": v(-16010, 3950) * mm});
            skPoint(sketch, "E560.96", {"position": v(-15860, 1100) * mm});
            skLineSegment(sketch, "E560.97", {"start": v(-18660, 1100) * mm, "end": v(-16960, 1100) * mm});
            skLineSegment(sketch, "E560.98", {"start": v(-13060, 1100) * mm, "end": v(-11360, 1100) * mm});
            skLineSegment(sketch, "E560.99", {"start": v(-15860, 3800) * mm, "end": v(-15860, 1100) * mm});
            skLineSegment(sketch, "E560.100", {"start": v(-11210, 3950) * mm, "end": v(-13210, 3950) * mm});
            skPoint(sketch, "E560.101", {"position": v(-18660, 1100) * mm});
            skLineSegment(sketch, "E560.102", {"start": v(-18660, 3800) * mm, "end": v(-16960, 3800) * mm});
            skLineSegment(sketch, "E560.103", {"start": v(-14010, 1050) * mm, "end": v(-16010, 1050) * mm});
            skLineSegment(sketch, "E560.104", {"start": v(-14160, 3800) * mm, "end": v(-14160, 1100) * mm});
            skLineSegment(sketch, "E560.105", {"start": v(-13060, 3800) * mm, "end": v(-11360, 3800) * mm});
            skLineSegment(sketch, "E560.106", {"start": v(-18810, 3950) * mm, "end": v(-18810, 1050) * mm});
            skLineSegment(sketch, "E560.107", {"start": v(-16810, 1050) * mm, "end": v(-18810, 1050) * mm});
            skPoint(sketch, "E560.108", {"position": v(-13060, 1100) * mm});
            skLineSegment(sketch, "E560.109", {"start": v(-18660, 3800) * mm, "end": v(-18660, 1100) * mm});
            skLineSegment(sketch, "E560.110", {"start": v(-16810, 3950) * mm, "end": v(-18810, 3950) * mm});
            skLineSegment(sketch, "E560.111", {"start": v(-11310, 3850) * mm, "end": v(-13110, 3850) * mm});
            skLineSegment(sketch, "E560.112", {"start": v(-14010, 3950) * mm, "end": v(-14010, 1050) * mm});
            skLineSegment(sketch, "E560.113", {"start": v(-13210, 3950) * mm, "end": v(-13210, 1050) * mm});
            skLineSegment(sketch, "E560.114", {"start": v(-16960, 3800) * mm, "end": v(-16960, 1100) * mm});
            skLineSegment(sketch, "E560.115", {"start": v(-13060, 3800) * mm, "end": v(-13060, 1100) * mm});
            skLineSegment(sketch, "E560.116", {"start": v(-15860, 3800) * mm, "end": v(-14160, 3800) * mm});
            skLineSegment(sketch, "E560.117", {"start": v(-14110, 3850) * mm, "end": v(-15910, 3850) * mm});
            skLineSegment(sketch, "E560.118", {"start": v(-18710, 3850) * mm, "end": v(-18710, 1050) * mm});
            skLineSegment(sketch, "E560.119", {"start": v(-16810, 3950) * mm, "end": v(-16810, 1050) * mm});
            skLineSegment(sketch, "E560.120", {"start": v(-16010, 3950) * mm, "end": v(-16010, 1050) * mm});
            skLineSegment(sketch, "E560.121", {"start": v(-11210, 1050) * mm, "end": v(-11210, 3850) * mm});
            skLineSegment(sketch, "E560.122", {"start": v(-11360, 3800) * mm, "end": v(-11360, 1100) * mm});
            skLineSegment(sketch, "E560.123", {"start": v(-16910, 3850) * mm, "end": v(-18710, 3850) * mm});
            skLineSegment(sketch, "E560.124", {"start": v(-15860, 1100) * mm, "end": v(-14160, 1100) * mm});
            skLineSegment(sketch, "E560.125", {"start": v(-11210, 1050) * mm, "end": v(-13210, 1050) * mm});
            skLineSegment(sketch, "E560.126", {"start": v(-11310, 1050) * mm, "end": v(-11310, 3850) * mm});
            skLineSegment(sketch, "E560.127", {"start": v(-13110, 3850) * mm, "end": v(-13110, 1050) * mm});
            skLineSegment(sketch, "E560.128", {"start": v(-14110, 3850) * mm, "end": v(-15910, 3850) * mm});
            skLineSegment(sketch, "E560.129", {"start": v(-16910, 1050) * mm, "end": v(-16910, 3850) * mm});
            skLineSegment(sketch, "E560.130", {"start": v(-11210, 3950) * mm, "end": v(-11210, 1050) * mm});
            skLineSegment(sketch, "E560.131", {"start": v(-14110, 1050) * mm, "end": v(-14110, 3850) * mm});
            skLineSegment(sketch, "E560.132", {"start": v(-11310, 3850) * mm, "end": v(-13110, 3850) * mm});
            skPoint(sketch, "E560.133", {"position": v(-15860, 1100) * mm});
            skLineSegment(sketch, "E560.134", {"start": v(-13210, 3850) * mm, "end": v(-13210, 1050) * mm});
            skLineSegment(sketch, "E560.135", {"start": v(-16910, 3850) * mm, "end": v(-18710, 3850) * mm});
            skLineSegment(sketch, "E560.136", {"start": v(-14010, 1050) * mm, "end": v(-14010, 3850) * mm});
            skLineSegment(sketch, "E560.137", {"start": v(-16810, 1050) * mm, "end": v(-16810, 3850) * mm});
            skLineSegment(sketch, "E560.138", {"start": v(-15910, 3850) * mm, "end": v(-15910, 1050) * mm});
            skPoint(sketch, "E560.139", {"position": v(-13060, 1100) * mm});
            skLineSegment(sketch, "E560.140", {"start": v(-18810, 3850) * mm, "end": v(-18810, 1050) * mm});
            skPoint(sketch, "E560.141", {"position": v(-18660, 1100) * mm});
            skLineSegment(sketch, "E560.142", {"start": v(-16010, 3850) * mm, "end": v(-16010, 1050) * mm});
            skLineSegment(sketch, "E560.143", {"start": v(-16910, 1050) * mm, "end": v(-16810, 1050) * mm});
            skLineSegment(sketch, "E560.144", {"start": v(-18810, 1050) * mm, "end": v(-18710, 1050) * mm});
            skLineSegment(sketch, "E560.145", {"start": v(-11310, 1050) * mm, "end": v(-11210, 1050) * mm});
            skLineSegment(sketch, "E560.146", {"start": v(-13210, 3850) * mm, "end": v(-13210, 3850) * mm});
            skLineSegment(sketch, "E560.147", {"start": v(-14110, 1050) * mm, "end": v(-14010, 1050) * mm});
            skLineSegment(sketch, "E560.148", {"start": v(-18810, 3850) * mm, "end": v(-18810, 3850) * mm});
            skLineSegment(sketch, "E560.149", {"start": v(-13210, 1050) * mm, "end": v(-13110, 1050) * mm});
            skLineSegment(sketch, "E560.150", {"start": v(-16010, 3850) * mm, "end": v(-16010, 3850) * mm});
            skLineSegment(sketch, "E560.151", {"start": v(-16010, 1050) * mm, "end": v(-15910, 1050) * mm});
            skLineSegment(sketch, "E560.152", {"start": v(-4610, 3950) * mm, "end": v(-6610, 3950) * mm});
            skPoint(sketch, "E560.153", {"position": v(-6460, 1100) * mm});
            skLineSegment(sketch, "E560.154", {"start": v(-9260, 1100) * mm, "end": v(-7560, 1100) * mm});
            skLineSegment(sketch, "E560.155", {"start": v(-3660, 1100) * mm, "end": v(-1960, 1100) * mm});
            skLineSegment(sketch, "E560.156", {"start": v(-6460, 3800) * mm, "end": v(-6460, 1100) * mm});
            skLineSegment(sketch, "E560.157", {"start": v(-1810, 3950) * mm, "end": v(-3810, 3950) * mm});
            skPoint(sketch, "E560.158", {"position": v(-9260, 1100) * mm});
            skLineSegment(sketch, "E560.159", {"start": v(-9260, 3800) * mm, "end": v(-7560, 3800) * mm});
            skLineSegment(sketch, "E560.160", {"start": v(-4610, 1050) * mm, "end": v(-6610, 1050) * mm});
            skLineSegment(sketch, "E560.161", {"start": v(-4760, 3800) * mm, "end": v(-4760, 1100) * mm});
            skLineSegment(sketch, "E560.162", {"start": v(-3660, 3800) * mm, "end": v(-1960, 3800) * mm});
            skLineSegment(sketch, "E560.163", {"start": v(-9410, 3950) * mm, "end": v(-9410, 1050) * mm});
            skLineSegment(sketch, "E560.164", {"start": v(-7410, 1050) * mm, "end": v(-9410, 1050) * mm});
            skPoint(sketch, "E560.165", {"position": v(-3660, 1100) * mm});
            skLineSegment(sketch, "E560.166", {"start": v(-9260, 3800) * mm, "end": v(-9260, 1100) * mm});
            skLineSegment(sketch, "E560.167", {"start": v(-7410, 3950) * mm, "end": v(-9410, 3950) * mm});
            skLineSegment(sketch, "E560.168", {"start": v(-1910, 3850) * mm, "end": v(-3710, 3850) * mm});
            skLineSegment(sketch, "E560.169", {"start": v(-4610, 3950) * mm, "end": v(-4610, 1050) * mm});
            skLineSegment(sketch, "E560.170", {"start": v(-3810, 3950) * mm, "end": v(-3810, 1050) * mm});
            skLineSegment(sketch, "E560.171", {"start": v(-7560, 3800) * mm, "end": v(-7560, 1100) * mm});
            skLineSegment(sketch, "E560.172", {"start": v(-3660, 3800) * mm, "end": v(-3660, 1100) * mm});
            skLineSegment(sketch, "E560.173", {"start": v(-6460, 3800) * mm, "end": v(-4760, 3800) * mm});
            skLineSegment(sketch, "E560.174", {"start": v(-4710, 3850) * mm, "end": v(-6510, 3850) * mm});
            skLineSegment(sketch, "E560.175", {"start": v(-9310, 3850) * mm, "end": v(-9310, 1050) * mm});
            skLineSegment(sketch, "E560.176", {"start": v(-7410, 3950) * mm, "end": v(-7410, 1050) * mm});
            skLineSegment(sketch, "E560.177", {"start": v(-6610, 3950) * mm, "end": v(-6610, 1050) * mm});
            skLineSegment(sketch, "E560.178", {"start": v(-1810, 1050) * mm, "end": v(-1810, 3850) * mm});
            skLineSegment(sketch, "E560.179", {"start": v(-1960, 3800) * mm, "end": v(-1960, 1100) * mm});
            skLineSegment(sketch, "E560.180", {"start": v(-7510, 3850) * mm, "end": v(-9310, 3850) * mm});
            skLineSegment(sketch, "E560.181", {"start": v(-6460, 1100) * mm, "end": v(-4760, 1100) * mm});
            skLineSegment(sketch, "E560.182", {"start": v(-1810, 1050) * mm, "end": v(-3810, 1050) * mm});
            skLineSegment(sketch, "E560.183", {"start": v(-1910, 1050) * mm, "end": v(-1910, 3850) * mm});
            skLineSegment(sketch, "E560.184", {"start": v(-3710, 3850) * mm, "end": v(-3710, 1050) * mm});
            skLineSegment(sketch, "E560.185", {"start": v(-4710, 3850) * mm, "end": v(-6510, 3850) * mm});
            skLineSegment(sketch, "E560.186", {"start": v(-7510, 1050) * mm, "end": v(-7510, 3850) * mm});
            skLineSegment(sketch, "E560.187", {"start": v(-1810, 3950) * mm, "end": v(-1810, 1050) * mm});
            skLineSegment(sketch, "E560.188", {"start": v(-4710, 1050) * mm, "end": v(-4710, 3850) * mm});
            skLineSegment(sketch, "E560.189", {"start": v(-1910, 3850) * mm, "end": v(-3710, 3850) * mm});
            skPoint(sketch, "E560.190", {"position": v(-6460, 1100) * mm});
            skLineSegment(sketch, "E560.191", {"start": v(-3810, 3850) * mm, "end": v(-3810, 1050) * mm});
            skLineSegment(sketch, "E560.192", {"start": v(-7510, 3850) * mm, "end": v(-9310, 3850) * mm});
            skLineSegment(sketch, "E560.193", {"start": v(-4610, 1050) * mm, "end": v(-4610, 3850) * mm});
            skLineSegment(sketch, "E560.194", {"start": v(-7410, 1050) * mm, "end": v(-7410, 3850) * mm});
            skLineSegment(sketch, "E560.195", {"start": v(-6510, 3850) * mm, "end": v(-6510, 1050) * mm});
            skPoint(sketch, "E560.196", {"position": v(-3660, 1100) * mm});
            skLineSegment(sketch, "E560.197", {"start": v(-9410, 3850) * mm, "end": v(-9410, 1050) * mm});
            skPoint(sketch, "E560.198", {"position": v(-9260, 1100) * mm});
            skLineSegment(sketch, "E560.199", {"start": v(-6610, 3850) * mm, "end": v(-6610, 1050) * mm});
            skLineSegment(sketch, "E560.200", {"start": v(-7510, 1050) * mm, "end": v(-7410, 1050) * mm});
            skLineSegment(sketch, "E560.201", {"start": v(-9410, 1050) * mm, "end": v(-9310, 1050) * mm});
            skLineSegment(sketch, "E560.202", {"start": v(-1910, 1050) * mm, "end": v(-1810, 1050) * mm});
            skLineSegment(sketch, "E560.203", {"start": v(-3810, 3850) * mm, "end": v(-3810, 3850) * mm});
            skLineSegment(sketch, "E560.204", {"start": v(-4710, 1050) * mm, "end": v(-4610, 1050) * mm});
            skLineSegment(sketch, "E560.205", {"start": v(-9410, 3850) * mm, "end": v(-9410, 3850) * mm});
            skLineSegment(sketch, "E560.206", {"start": v(-3810, 1050) * mm, "end": v(-3710, 1050) * mm});
            skLineSegment(sketch, "E560.207", {"start": v(-6610, 3850) * mm, "end": v(-6610, 3850) * mm});
            skLineSegment(sketch, "E560.208", {"start": v(-6610, 1050) * mm, "end": v(-6510, 1050) * mm});
            skLineSegment(sketch, "E560.209", {"start": v(-28210, 1050) * mm, "end": v(-18810, 1050) * mm});
            skLineSegment(sketch, "E560.210", {"start": v(-31060, 1100) * mm, "end": v(-31060, 3800) * mm});
            skLineSegment(sketch, "E560.211", {"start": v(-32160, 3800) * mm, "end": v(-32160, 1100) * mm});
            skLineSegment(sketch, "E560.212", {"start": v(-32160, 1100) * mm, "end": v(-31060, 1100) * mm});
            skLineSegment(sketch, "E560.213", {"start": v(-32310, 3950) * mm, "end": v(-30910, 3950) * mm});
            skLineSegment(sketch, "E560.214", {"start": v(-32310, 1050) * mm, "end": v(-30910, 1050) * mm});
            skLineSegment(sketch, "E560.215", {"start": v(-32310, 3950) * mm, "end": v(-32310, 1050) * mm});
            skLineSegment(sketch, "E560.216", {"start": v(-30910, 3950) * mm, "end": v(-30910, 1050) * mm});
            skLineSegment(sketch, "E560.217", {"start": v(-32210, 1050) * mm, "end": v(-32210, 3850) * mm});
            skLineSegment(sketch, "E560.218", {"start": v(-32210, 3850) * mm, "end": v(-31010, 3850) * mm});
            skLineSegment(sketch, "E560.219", {"start": v(-31010, 3850) * mm, "end": v(-31010, 1050) * mm});
            skLineSegment(sketch, "E560.220", {"start": v(-32160, 3800) * mm, "end": v(-31060, 3800) * mm});
            skSolve(sketch);
        }
        {
            var Q0;
            {var subQ5=sQuery(id+"F66.wireOp",EDGE,"E560.9");Q0=makeQuery(id+"F66.imprint","IMPRINT",FACE,{"disambiguationData":[TD([[makeQuery(id+"F66.imprint","IMPRINT",EDGE,{"derivedFrom":subQ5}),-1.0]])]});}
            var Q1;
            {var subQ4=sQuery(id+"F66.wireOp",EDGE,"E560.27");Q1=makeQuery(id+"F66.imprint","IMPRINT",FACE,{"disambiguationData":[TD([[makeQuery(id+"F66.imprint","IMPRINT",EDGE,{"derivedFrom":subQ4}),-1.0]])]});}
            var Q2;
            Q2=makeQuery(id+"F66.imprint","IMPRINT",FACE,{"disambiguationData":[TD([[makeQuery(id+"F66.imprint","IMPRINT",EDGE,{"derivedFrom":sQuery(id+"F66.wireOp",EDGE,"E560.213")}),-1.0]])]});
            var Q3;
            {var subQ6=sQuery(id+"F66.wireOp",EDGE,"E560.45");Q3=makeQuery(id+"F66.imprint","IMPRINT",FACE,{"disambiguationData":[TD([[makeQuery(id+"F66.imprint","IMPRINT",EDGE,{"derivedFrom":subQ6}),-1.0]])]});}
            var Q4;
            {var subQ4=sQuery(id+"F66.wireOp",EDGE,"E560.63");Q4=makeQuery(id+"F66.imprint","IMPRINT",FACE,{"disambiguationData":[TD([[makeQuery(id+"F66.imprint","IMPRINT",EDGE,{"derivedFrom":subQ4}),-1.0]])]});}
            var Q5;
            {var subQ4=sQuery(id+"F66.wireOp",EDGE,"E560.81");Q5=makeQuery(id+"F66.imprint","IMPRINT",FACE,{"disambiguationData":[TD([[makeQuery(id+"F66.imprint","IMPRINT",EDGE,{"derivedFrom":subQ4}),-1.0]])]});}
            var Q6;
            {var subQ0=sQuery(id+"F66.wireOp",EDGE,"E560.110");Q6=makeQuery(id+"F66.imprint","IMPRINT",FACE,{"disambiguationData":[TD([[makeQuery(id+"F66.imprint","IMPRINT",EDGE,{"derivedFrom":subQ0}),1.0]])]});}
            var Q7;
            {var subQ1=sQuery(id+"F66.wireOp",EDGE,"E560.95");Q7=makeQuery(id+"F66.imprint","IMPRINT",FACE,{"disambiguationData":[TD([[makeQuery(id+"F66.imprint","IMPRINT",EDGE,{"derivedFrom":subQ1}),1.0]])]});}
            var Q8;
            {var subQ1=sQuery(id+"F66.wireOp",EDGE,"E560.100");Q8=makeQuery(id+"F66.imprint","IMPRINT",FACE,{"disambiguationData":[TD([[makeQuery(id+"F66.imprint","IMPRINT",EDGE,{"derivedFrom":subQ1}),1.0]])]});}
            var Q9;
            {var subQ0=sQuery(id+"F66.wireOp",EDGE,"E560.167");Q9=makeQuery(id+"F66.imprint","IMPRINT",FACE,{"disambiguationData":[TD([[makeQuery(id+"F66.imprint","IMPRINT",EDGE,{"derivedFrom":subQ0}),1.0]])]});}
            var Q10;
            {var subQ1=sQuery(id+"F66.wireOp",EDGE,"E560.152");Q10=makeQuery(id+"F66.imprint","IMPRINT",FACE,{"disambiguationData":[TD([[makeQuery(id+"F66.imprint","IMPRINT",EDGE,{"derivedFrom":subQ1}),1.0]])]});}
            var Q11;
            {var subQ1=sQuery(id+"F66.wireOp",EDGE,"E560.157");Q11=makeQuery(id+"F66.imprint","IMPRINT",FACE,{"disambiguationData":[TD([[makeQuery(id+"F66.imprint","IMPRINT",EDGE,{"derivedFrom":subQ1}),1.0]])]});}
            extrude(context, id + "F67", {"entities" : qUnion([Q0, Q1, Q2, Q3, Q4, Q5, Q6, Q7, Q8, Q9, Q10, Q11]), "operationType" : NewBodyOperationType.ADD, "depth" : 50 * mm, "offsetDistance" : 25 * mm});
        }
        {
            var Q0;
            Q0=makeQuery(id+"F5.boolean.opBoolean","MERGE",FACE,{"derivedFrom":[makeQuery(id+"F3.boolean.opBoolean","COPY",FACE,{"derivedFrom":makeQuery(id+"F3.opExtrude","SWEPT_FACE",FACE,{"disambiguationData":[OSD([sQuery(id+"F2.wireOp",EDGE,"E19.13")])]})}),makeQuery(id+"F5.opExtrude","SWEPT_FACE",FACE,{"disambiguationData":[OSD([sQuery(id+"F4.wireOp",EDGE,"E30.0")])]})]});
            var sketch = newSketch(context, id + "F68", { "sketchPlane" : qUnion([Q0])});
            skPoint(sketch, "E561.3", {"position": v(25260, 1100) * mm});
            skPoint(sketch, "E561.4", {"position": v(22460, 1100) * mm});
            skPoint(sketch, "E561.5", {"position": v(28060, 1100) * mm});
            skPoint(sketch, "E561.41", {"position": v(28060, 1100) * mm});
            skLineSegment(sketch, "E561.42", {"start": v(28210, 3850) * mm, "end": v(28210, 1050) * mm});
            skLineSegment(sketch, "E561.43", {"start": v(26210, 1050) * mm, "end": v(26210, 3850) * mm});
            skLineSegment(sketch, "E561.44", {"start": v(26310, 3850) * mm, "end": v(28110, 3850) * mm});
            skLineSegment(sketch, "E561.45", {"start": v(28110, 3850) * mm, "end": v(28110, 1050) * mm});
            skLineSegment(sketch, "E561.46", {"start": v(26310, 3850) * mm, "end": v(28110, 3850) * mm});
            skLineSegment(sketch, "E561.47", {"start": v(26310, 1050) * mm, "end": v(26310, 3850) * mm});
            skLineSegment(sketch, "E561.48", {"start": v(28210, 1050) * mm, "end": v(28110, 1050) * mm});
            skLineSegment(sketch, "E561.49", {"start": v(26310, 1050) * mm, "end": v(26210, 1050) * mm});
            skLineSegment(sketch, "E561.50", {"start": v(26210, 1050) * mm, "end": v(28210, 1050) * mm});
            skLineSegment(sketch, "E561.51", {"start": v(28060, 3800) * mm, "end": v(26360, 3800) * mm});
            skLineSegment(sketch, "E561.52", {"start": v(26360, 3800) * mm, "end": v(26360, 1100) * mm});
            skLineSegment(sketch, "E561.53", {"start": v(28210, 3950) * mm, "end": v(28210, 1050) * mm});
            skLineSegment(sketch, "E561.54", {"start": v(26210, 3950) * mm, "end": v(26210, 1050) * mm});
            skLineSegment(sketch, "E561.55", {"start": v(26210, 3950) * mm, "end": v(28210, 3950) * mm});
            skLineSegment(sketch, "E561.56", {"start": v(28060, 1100) * mm, "end": v(26360, 1100) * mm});
            skLineSegment(sketch, "E561.57", {"start": v(28060, 3800) * mm, "end": v(28060, 1100) * mm});
            skLineSegment(sketch, "E561.58", {"start": v(28210, 3850) * mm, "end": v(28210, 3850) * mm});
            skPoint(sketch, "E561.59", {"position": v(25260, 1100) * mm});
            skLineSegment(sketch, "E561.60", {"start": v(25410, 3850) * mm, "end": v(25410, 1050) * mm});
            skLineSegment(sketch, "E561.61", {"start": v(23410, 1050) * mm, "end": v(23410, 3850) * mm});
            skLineSegment(sketch, "E561.62", {"start": v(23510, 3850) * mm, "end": v(25310, 3850) * mm});
            skLineSegment(sketch, "E561.63", {"start": v(25310, 3850) * mm, "end": v(25310, 1050) * mm});
            skLineSegment(sketch, "E561.64", {"start": v(23510, 3850) * mm, "end": v(25310, 3850) * mm});
            skLineSegment(sketch, "E561.65", {"start": v(23510, 1050) * mm, "end": v(23510, 3850) * mm});
            skLineSegment(sketch, "E561.66", {"start": v(25410, 1050) * mm, "end": v(25310, 1050) * mm});
            skLineSegment(sketch, "E561.67", {"start": v(23510, 1050) * mm, "end": v(23410, 1050) * mm});
            skLineSegment(sketch, "E561.68", {"start": v(23410, 1050) * mm, "end": v(25410, 1050) * mm});
            skLineSegment(sketch, "E561.69", {"start": v(25260, 3800) * mm, "end": v(23560, 3800) * mm});
            skLineSegment(sketch, "E561.70", {"start": v(23560, 3800) * mm, "end": v(23560, 1100) * mm});
            skLineSegment(sketch, "E561.71", {"start": v(25410, 3950) * mm, "end": v(25410, 1050) * mm});
            skLineSegment(sketch, "E561.72", {"start": v(23410, 3950) * mm, "end": v(23410, 1050) * mm});
            skLineSegment(sketch, "E561.73", {"start": v(23410, 3950) * mm, "end": v(25410, 3950) * mm});
            skLineSegment(sketch, "E561.74", {"start": v(25260, 1100) * mm, "end": v(23560, 1100) * mm});
            skLineSegment(sketch, "E561.75", {"start": v(25260, 3800) * mm, "end": v(25260, 1100) * mm});
            skLineSegment(sketch, "E561.76", {"start": v(25410, 3850) * mm, "end": v(25410, 3850) * mm});
            skPoint(sketch, "E561.77", {"position": v(22460, 1100) * mm});
            skLineSegment(sketch, "E561.78", {"start": v(22610, 3850) * mm, "end": v(22610, 1050) * mm});
            skLineSegment(sketch, "E561.79", {"start": v(20610, 1050) * mm, "end": v(20610, 3850) * mm});
            skLineSegment(sketch, "E561.80", {"start": v(20710, 3850) * mm, "end": v(22510, 3850) * mm});
            skLineSegment(sketch, "E561.81", {"start": v(22510, 3850) * mm, "end": v(22510, 1050) * mm});
            skLineSegment(sketch, "E561.82", {"start": v(20710, 3850) * mm, "end": v(22510, 3850) * mm});
            skLineSegment(sketch, "E561.83", {"start": v(20710, 1050) * mm, "end": v(20710, 3850) * mm});
            skLineSegment(sketch, "E561.84", {"start": v(22610, 1050) * mm, "end": v(22510, 1050) * mm});
            skLineSegment(sketch, "E561.85", {"start": v(20710, 1050) * mm, "end": v(20610, 1050) * mm});
            skLineSegment(sketch, "E561.86", {"start": v(20610, 1050) * mm, "end": v(22610, 1050) * mm});
            skLineSegment(sketch, "E561.87", {"start": v(22460, 3800) * mm, "end": v(20760, 3800) * mm});
            skLineSegment(sketch, "E561.88", {"start": v(20760, 3800) * mm, "end": v(20760, 1100) * mm});
            skLineSegment(sketch, "E561.89", {"start": v(22610, 3950) * mm, "end": v(22610, 1050) * mm});
            skLineSegment(sketch, "E561.90", {"start": v(20610, 3950) * mm, "end": v(20610, 1050) * mm});
            skLineSegment(sketch, "E561.91", {"start": v(20610, 3950) * mm, "end": v(22610, 3950) * mm});
            skLineSegment(sketch, "E561.92", {"start": v(22460, 1100) * mm, "end": v(20760, 1100) * mm});
            skLineSegment(sketch, "E561.93", {"start": v(22460, 3800) * mm, "end": v(22460, 1100) * mm});
            skLineSegment(sketch, "E561.94", {"start": v(22610, 3850) * mm, "end": v(22610, 3850) * mm});
            skLineSegment(sketch, "E561.95", {"start": v(14010, 3950) * mm, "end": v(16010, 3950) * mm});
            skPoint(sketch, "E561.96", {"position": v(15860, 1100) * mm});
            skLineSegment(sketch, "E561.97", {"start": v(18660, 1100) * mm, "end": v(16960, 1100) * mm});
            skLineSegment(sketch, "E561.98", {"start": v(13060, 1100) * mm, "end": v(11360, 1100) * mm});
            skLineSegment(sketch, "E561.99", {"start": v(15860, 3800) * mm, "end": v(15860, 1100) * mm});
            skLineSegment(sketch, "E561.100", {"start": v(11210, 3950) * mm, "end": v(13210, 3950) * mm});
            skPoint(sketch, "E561.101", {"position": v(18660, 1100) * mm});
            skLineSegment(sketch, "E561.102", {"start": v(18660, 3800) * mm, "end": v(16960, 3800) * mm});
            skLineSegment(sketch, "E561.103", {"start": v(14010, 1050) * mm, "end": v(16010, 1050) * mm});
            skLineSegment(sketch, "E561.104", {"start": v(14160, 3800) * mm, "end": v(14160, 1100) * mm});
            skLineSegment(sketch, "E561.105", {"start": v(13060, 3800) * mm, "end": v(11360, 3800) * mm});
            skLineSegment(sketch, "E561.106", {"start": v(18810, 3950) * mm, "end": v(18810, 1050) * mm});
            skLineSegment(sketch, "E561.107", {"start": v(16810, 1050) * mm, "end": v(18810, 1050) * mm});
            skPoint(sketch, "E561.108", {"position": v(13060, 1100) * mm});
            skLineSegment(sketch, "E561.109", {"start": v(18660, 3800) * mm, "end": v(18660, 1100) * mm});
            skLineSegment(sketch, "E561.110", {"start": v(16810, 3950) * mm, "end": v(18810, 3950) * mm});
            skLineSegment(sketch, "E561.111", {"start": v(11310, 3850) * mm, "end": v(13110, 3850) * mm});
            skLineSegment(sketch, "E561.112", {"start": v(14010, 3950) * mm, "end": v(14010, 1050) * mm});
            skLineSegment(sketch, "E561.113", {"start": v(13210, 3950) * mm, "end": v(13210, 1050) * mm});
            skLineSegment(sketch, "E561.114", {"start": v(16960, 3800) * mm, "end": v(16960, 1100) * mm});
            skLineSegment(sketch, "E561.115", {"start": v(13060, 3800) * mm, "end": v(13060, 1100) * mm});
            skLineSegment(sketch, "E561.116", {"start": v(15860, 3800) * mm, "end": v(14160, 3800) * mm});
            skLineSegment(sketch, "E561.117", {"start": v(14110, 3850) * mm, "end": v(15910, 3850) * mm});
            skLineSegment(sketch, "E561.118", {"start": v(18710, 3850) * mm, "end": v(18710, 1050) * mm});
            skLineSegment(sketch, "E561.119", {"start": v(16810, 3950) * mm, "end": v(16810, 1050) * mm});
            skLineSegment(sketch, "E561.120", {"start": v(16010, 3950) * mm, "end": v(16010, 1050) * mm});
            skLineSegment(sketch, "E561.121", {"start": v(11210, 1050) * mm, "end": v(11210, 3850) * mm});
            skLineSegment(sketch, "E561.122", {"start": v(11360, 3800) * mm, "end": v(11360, 1100) * mm});
            skLineSegment(sketch, "E561.123", {"start": v(16910, 3850) * mm, "end": v(18710, 3850) * mm});
            skLineSegment(sketch, "E561.124", {"start": v(15860, 1100) * mm, "end": v(14160, 1100) * mm});
            skLineSegment(sketch, "E561.125", {"start": v(11210, 1050) * mm, "end": v(13210, 1050) * mm});
            skLineSegment(sketch, "E561.126", {"start": v(11310, 1050) * mm, "end": v(11310, 3850) * mm});
            skLineSegment(sketch, "E561.127", {"start": v(13110, 3850) * mm, "end": v(13110, 1050) * mm});
            skLineSegment(sketch, "E561.128", {"start": v(14110, 3850) * mm, "end": v(15910, 3850) * mm});
            skLineSegment(sketch, "E561.129", {"start": v(16910, 1050) * mm, "end": v(16910, 3850) * mm});
            skLineSegment(sketch, "E561.130", {"start": v(11210, 3950) * mm, "end": v(11210, 1050) * mm});
            skLineSegment(sketch, "E561.131", {"start": v(14110, 1050) * mm, "end": v(14110, 3850) * mm});
            skLineSegment(sketch, "E561.132", {"start": v(11310, 3850) * mm, "end": v(13110, 3850) * mm});
            skPoint(sketch, "E561.133", {"position": v(15860, 1100) * mm});
            skLineSegment(sketch, "E561.134", {"start": v(13210, 3850) * mm, "end": v(13210, 1050) * mm});
            skLineSegment(sketch, "E561.135", {"start": v(16910, 3850) * mm, "end": v(18710, 3850) * mm});
            skLineSegment(sketch, "E561.136", {"start": v(14010, 1050) * mm, "end": v(14010, 3850) * mm});
            skLineSegment(sketch, "E561.137", {"start": v(16810, 1050) * mm, "end": v(16810, 3850) * mm});
            skLineSegment(sketch, "E561.138", {"start": v(15910, 3850) * mm, "end": v(15910, 1050) * mm});
            skPoint(sketch, "E561.139", {"position": v(13060, 1100) * mm});
            skLineSegment(sketch, "E561.140", {"start": v(18810, 3850) * mm, "end": v(18810, 1050) * mm});
            skPoint(sketch, "E561.141", {"position": v(18660, 1100) * mm});
            skLineSegment(sketch, "E561.142", {"start": v(16010, 3850) * mm, "end": v(16010, 1050) * mm});
            skLineSegment(sketch, "E561.143", {"start": v(16910, 1050) * mm, "end": v(16810, 1050) * mm});
            skLineSegment(sketch, "E561.144", {"start": v(18810, 1050) * mm, "end": v(18710, 1050) * mm});
            skLineSegment(sketch, "E561.145", {"start": v(11310, 1050) * mm, "end": v(11210, 1050) * mm});
            skLineSegment(sketch, "E561.146", {"start": v(13210, 3850) * mm, "end": v(13210, 3850) * mm});
            skLineSegment(sketch, "E561.147", {"start": v(14110, 1050) * mm, "end": v(14010, 1050) * mm});
            skLineSegment(sketch, "E561.148", {"start": v(18810, 3850) * mm, "end": v(18810, 3850) * mm});
            skLineSegment(sketch, "E561.149", {"start": v(13210, 1050) * mm, "end": v(13110, 1050) * mm});
            skLineSegment(sketch, "E561.150", {"start": v(16010, 3850) * mm, "end": v(16010, 3850) * mm});
            skLineSegment(sketch, "E561.151", {"start": v(16010, 1050) * mm, "end": v(15910, 1050) * mm});
            skLineSegment(sketch, "E561.152", {"start": v(4610, 3950) * mm, "end": v(6610, 3950) * mm});
            skPoint(sketch, "E561.153", {"position": v(6460, 1100) * mm});
            skLineSegment(sketch, "E561.154", {"start": v(9260, 1100) * mm, "end": v(7560, 1100) * mm});
            skLineSegment(sketch, "E561.155", {"start": v(3660, 1100) * mm, "end": v(1960, 1100) * mm});
            skLineSegment(sketch, "E561.156", {"start": v(6460, 3800) * mm, "end": v(6460, 1100) * mm});
            skLineSegment(sketch, "E561.157", {"start": v(1810, 3950) * mm, "end": v(3810, 3950) * mm});
            skPoint(sketch, "E561.158", {"position": v(9260, 1100) * mm});
            skLineSegment(sketch, "E561.159", {"start": v(9260, 3800) * mm, "end": v(7560, 3800) * mm});
            skLineSegment(sketch, "E561.160", {"start": v(4610, 1050) * mm, "end": v(6610, 1050) * mm});
            skLineSegment(sketch, "E561.161", {"start": v(4760, 3800) * mm, "end": v(4760, 1100) * mm});
            skLineSegment(sketch, "E561.162", {"start": v(3660, 3800) * mm, "end": v(1960, 3800) * mm});
            skLineSegment(sketch, "E561.163", {"start": v(9410, 3950) * mm, "end": v(9410, 1050) * mm});
            skLineSegment(sketch, "E561.164", {"start": v(7410, 1050) * mm, "end": v(9410, 1050) * mm});
            skPoint(sketch, "E561.165", {"position": v(3660, 1100) * mm});
            skLineSegment(sketch, "E561.166", {"start": v(9260, 3800) * mm, "end": v(9260, 1100) * mm});
            skLineSegment(sketch, "E561.167", {"start": v(7410, 3950) * mm, "end": v(9410, 3950) * mm});
            skLineSegment(sketch, "E561.168", {"start": v(1910, 3850) * mm, "end": v(3710, 3850) * mm});
            skLineSegment(sketch, "E561.169", {"start": v(4610, 3950) * mm, "end": v(4610, 1050) * mm});
            skLineSegment(sketch, "E561.170", {"start": v(3810, 3950) * mm, "end": v(3810, 1050) * mm});
            skLineSegment(sketch, "E561.171", {"start": v(7560, 3800) * mm, "end": v(7560, 1100) * mm});
            skLineSegment(sketch, "E561.172", {"start": v(3660, 3800) * mm, "end": v(3660, 1100) * mm});
            skLineSegment(sketch, "E561.173", {"start": v(6460, 3800) * mm, "end": v(4760, 3800) * mm});
            skLineSegment(sketch, "E561.174", {"start": v(4710, 3850) * mm, "end": v(6510, 3850) * mm});
            skLineSegment(sketch, "E561.175", {"start": v(9310, 3850) * mm, "end": v(9310, 1050) * mm});
            skLineSegment(sketch, "E561.176", {"start": v(7410, 3950) * mm, "end": v(7410, 1050) * mm});
            skLineSegment(sketch, "E561.177", {"start": v(6610, 3950) * mm, "end": v(6610, 1050) * mm});
            skLineSegment(sketch, "E561.178", {"start": v(1810, 1050) * mm, "end": v(1810, 3850) * mm});
            skLineSegment(sketch, "E561.179", {"start": v(1960, 3800) * mm, "end": v(1960, 1100) * mm});
            skLineSegment(sketch, "E561.180", {"start": v(7510, 3850) * mm, "end": v(9310, 3850) * mm});
            skLineSegment(sketch, "E561.181", {"start": v(6460, 1100) * mm, "end": v(4760, 1100) * mm});
            skLineSegment(sketch, "E561.182", {"start": v(1810, 1050) * mm, "end": v(3810, 1050) * mm});
            skLineSegment(sketch, "E561.183", {"start": v(1910, 1050) * mm, "end": v(1910, 3850) * mm});
            skLineSegment(sketch, "E561.184", {"start": v(3710, 3850) * mm, "end": v(3710, 1050) * mm});
            skLineSegment(sketch, "E561.185", {"start": v(4710, 3850) * mm, "end": v(6510, 3850) * mm});
            skLineSegment(sketch, "E561.186", {"start": v(7510, 1050) * mm, "end": v(7510, 3850) * mm});
            skLineSegment(sketch, "E561.187", {"start": v(1810, 3950) * mm, "end": v(1810, 1050) * mm});
            skLineSegment(sketch, "E561.188", {"start": v(4710, 1050) * mm, "end": v(4710, 3850) * mm});
            skLineSegment(sketch, "E561.189", {"start": v(1910, 3850) * mm, "end": v(3710, 3850) * mm});
            skPoint(sketch, "E561.190", {"position": v(6460, 1100) * mm});
            skLineSegment(sketch, "E561.191", {"start": v(3810, 3850) * mm, "end": v(3810, 1050) * mm});
            skLineSegment(sketch, "E561.192", {"start": v(7510, 3850) * mm, "end": v(9310, 3850) * mm});
            skLineSegment(sketch, "E561.193", {"start": v(4610, 1050) * mm, "end": v(4610, 3850) * mm});
            skLineSegment(sketch, "E561.194", {"start": v(7410, 1050) * mm, "end": v(7410, 3850) * mm});
            skLineSegment(sketch, "E561.195", {"start": v(6510, 3850) * mm, "end": v(6510, 1050) * mm});
            skPoint(sketch, "E561.196", {"position": v(3660, 1100) * mm});
            skLineSegment(sketch, "E561.197", {"start": v(9410, 3850) * mm, "end": v(9410, 1050) * mm});
            skPoint(sketch, "E561.198", {"position": v(9260, 1100) * mm});
            skLineSegment(sketch, "E561.199", {"start": v(6610, 3850) * mm, "end": v(6610, 1050) * mm});
            skLineSegment(sketch, "E561.200", {"start": v(7510, 1050) * mm, "end": v(7410, 1050) * mm});
            skLineSegment(sketch, "E561.201", {"start": v(9410, 1050) * mm, "end": v(9310, 1050) * mm});
            skLineSegment(sketch, "E561.202", {"start": v(1910, 1050) * mm, "end": v(1810, 1050) * mm});
            skLineSegment(sketch, "E561.203", {"start": v(3810, 3850) * mm, "end": v(3810, 3850) * mm});
            skLineSegment(sketch, "E561.204", {"start": v(4710, 1050) * mm, "end": v(4610, 1050) * mm});
            skLineSegment(sketch, "E561.205", {"start": v(9410, 3850) * mm, "end": v(9410, 3850) * mm});
            skLineSegment(sketch, "E561.206", {"start": v(3810, 1050) * mm, "end": v(3710, 1050) * mm});
            skLineSegment(sketch, "E561.207", {"start": v(6610, 3850) * mm, "end": v(6610, 3850) * mm});
            skLineSegment(sketch, "E561.208", {"start": v(6610, 1050) * mm, "end": v(6510, 1050) * mm});
            skLineSegment(sketch, "E561.209", {"start": v(28210, 1050) * mm, "end": v(18810, 1050) * mm});
            skPoint(sketch, "E562", {"position": v(29660, 1100) * mm});
            skPoint(sketch, "E563", {"position": v(32460, 1100) * mm});
            skPoint(sketch, "E564", {"position": v(35260, 1100) * mm});
            skPoint(sketch, "E565.4", {"position": v(31360, 1100) * mm});
            skPoint(sketch, "E565.77", {"position": v(31360, 1100) * mm});
            skLineSegment(sketch, "E565.78", {"start": v(31510, 3850) * mm, "end": v(31510, 1050) * mm});
            skLineSegment(sketch, "E565.79", {"start": v(29510, 1050) * mm, "end": v(29510, 3850) * mm});
            skLineSegment(sketch, "E565.80", {"start": v(29610, 3850) * mm, "end": v(31410, 3850) * mm});
            skLineSegment(sketch, "E565.81", {"start": v(31410, 3850) * mm, "end": v(31410, 1050) * mm});
            skLineSegment(sketch, "E565.82", {"start": v(29610, 3850) * mm, "end": v(31410, 3850) * mm});
            skLineSegment(sketch, "E565.83", {"start": v(29610, 1050) * mm, "end": v(29610, 3850) * mm});
            skLineSegment(sketch, "E565.84", {"start": v(31510, 1050) * mm, "end": v(31410, 1050) * mm});
            skLineSegment(sketch, "E565.85", {"start": v(29610, 1050) * mm, "end": v(29510, 1050) * mm});
            skLineSegment(sketch, "E565.86", {"start": v(29510, 1050) * mm, "end": v(31510, 1050) * mm});
            skLineSegment(sketch, "E565.87", {"start": v(31360, 3800) * mm, "end": v(29660, 3800) * mm});
            skLineSegment(sketch, "E565.88", {"start": v(29660, 3800) * mm, "end": v(29660, 1100) * mm});
            skLineSegment(sketch, "E565.89", {"start": v(31510, 3950) * mm, "end": v(31510, 1050) * mm});
            skLineSegment(sketch, "E565.90", {"start": v(29510, 3950) * mm, "end": v(29510, 1050) * mm});
            skLineSegment(sketch, "E565.91", {"start": v(29510, 3950) * mm, "end": v(31510, 3950) * mm});
            skLineSegment(sketch, "E565.92", {"start": v(31360, 1100) * mm, "end": v(29660, 1100) * mm});
            skLineSegment(sketch, "E565.93", {"start": v(31360, 3800) * mm, "end": v(31360, 1100) * mm});
            skLineSegment(sketch, "E565.94", {"start": v(31510, 3850) * mm, "end": v(31510, 3850) * mm});
            skPoint(sketch, "E566.4", {"position": v(34160, 1100) * mm});
            skPoint(sketch, "E566.77", {"position": v(34160, 1100) * mm});
            skLineSegment(sketch, "E566.78", {"start": v(34310, 3850) * mm, "end": v(34310, 1050) * mm});
            skLineSegment(sketch, "E566.79", {"start": v(32310, 1050) * mm, "end": v(32310, 3850) * mm});
            skLineSegment(sketch, "E566.80", {"start": v(32410, 3850) * mm, "end": v(34210, 3850) * mm});
            skLineSegment(sketch, "E566.81", {"start": v(34210, 3850) * mm, "end": v(34210, 1050) * mm});
            skLineSegment(sketch, "E566.82", {"start": v(32410, 3850) * mm, "end": v(34210, 3850) * mm});
            skLineSegment(sketch, "E566.83", {"start": v(32410, 1050) * mm, "end": v(32410, 3850) * mm});
            skLineSegment(sketch, "E566.84", {"start": v(34310, 1050) * mm, "end": v(34210, 1050) * mm});
            skLineSegment(sketch, "E566.85", {"start": v(32410, 1050) * mm, "end": v(32310, 1050) * mm});
            skLineSegment(sketch, "E566.86", {"start": v(32310, 1050) * mm, "end": v(34310, 1050) * mm});
            skLineSegment(sketch, "E566.87", {"start": v(34160, 3800) * mm, "end": v(32460, 3800) * mm});
            skLineSegment(sketch, "E566.88", {"start": v(32460, 3800) * mm, "end": v(32460, 1100) * mm});
            skLineSegment(sketch, "E566.89", {"start": v(34310, 3950) * mm, "end": v(34310, 1050) * mm});
            skLineSegment(sketch, "E566.90", {"start": v(32310, 3950) * mm, "end": v(32310, 1050) * mm});
            skLineSegment(sketch, "E566.91", {"start": v(32310, 3950) * mm, "end": v(34310, 3950) * mm});
            skLineSegment(sketch, "E566.92", {"start": v(34160, 1100) * mm, "end": v(32460, 1100) * mm});
            skLineSegment(sketch, "E566.93", {"start": v(34160, 3800) * mm, "end": v(34160, 1100) * mm});
            skLineSegment(sketch, "E566.94", {"start": v(34310, 3850) * mm, "end": v(34310, 3850) * mm});
            skPoint(sketch, "E567.4", {"position": v(36960, 1100) * mm});
            skPoint(sketch, "E567.77", {"position": v(36960, 1100) * mm});
            skLineSegment(sketch, "E567.78", {"start": v(37110, 3850) * mm, "end": v(37110, 1050) * mm});
            skLineSegment(sketch, "E567.79", {"start": v(35110, 1050) * mm, "end": v(35110, 3850) * mm});
            skLineSegment(sketch, "E567.80", {"start": v(35210, 3850) * mm, "end": v(37010, 3850) * mm});
            skLineSegment(sketch, "E567.81", {"start": v(37010, 3850) * mm, "end": v(37010, 1050) * mm});
            skLineSegment(sketch, "E567.82", {"start": v(35210, 3850) * mm, "end": v(37010, 3850) * mm});
            skLineSegment(sketch, "E567.83", {"start": v(35210, 1050) * mm, "end": v(35210, 3850) * mm});
            skLineSegment(sketch, "E567.84", {"start": v(37110, 1050) * mm, "end": v(37010, 1050) * mm});
            skLineSegment(sketch, "E567.85", {"start": v(35210, 1050) * mm, "end": v(35110, 1050) * mm});
            skLineSegment(sketch, "E567.86", {"start": v(35110, 1050) * mm, "end": v(37110, 1050) * mm});
            skLineSegment(sketch, "E567.87", {"start": v(36960, 3800) * mm, "end": v(35260, 3800) * mm});
            skLineSegment(sketch, "E567.88", {"start": v(35260, 3800) * mm, "end": v(35260, 1100) * mm});
            skLineSegment(sketch, "E567.89", {"start": v(37110, 3950) * mm, "end": v(37110, 1050) * mm});
            skLineSegment(sketch, "E567.90", {"start": v(35110, 3950) * mm, "end": v(35110, 1050) * mm});
            skLineSegment(sketch, "E567.91", {"start": v(35110, 3950) * mm, "end": v(37110, 3950) * mm});
            skLineSegment(sketch, "E567.92", {"start": v(36960, 1100) * mm, "end": v(35260, 1100) * mm});
            skLineSegment(sketch, "E567.93", {"start": v(36960, 3800) * mm, "end": v(36960, 1100) * mm});
            skLineSegment(sketch, "E567.94", {"start": v(37110, 3850) * mm, "end": v(37110, 3850) * mm});
            skSolve(sketch);
        }
        {
            var Q0;
            {var subQ4=sQuery(id+"F68.wireOp",EDGE,"E561.157");Q0=makeQuery(id+"F68.imprint","IMPRINT",FACE,{"disambiguationData":[TD([[makeQuery(id+"F68.imprint","IMPRINT",EDGE,{"derivedFrom":subQ4}),-1.0]])]});}
            var Q1;
            {var subQ1=sQuery(id+"F68.wireOp",EDGE,"E561.183");Q1=makeQuery(id+"F68.imprint","IMPRINT",FACE,{"disambiguationData":[TD([[makeQuery(id+"F68.imprint","IMPRINT",EDGE,{"derivedFrom":subQ1}),-1.0]])]});}
            var Q2;
            {var subQ1=sQuery(id+"F68.wireOp",EDGE,"E561.152");Q2=makeQuery(id+"F68.imprint","IMPRINT",FACE,{"disambiguationData":[TD([[makeQuery(id+"F68.imprint","IMPRINT",EDGE,{"derivedFrom":subQ1}),-1.0]])]});}
            var Q3;
            {var subQ8=sQuery(id+"F68.wireOp",EDGE,"E561.156");Q3=makeQuery(id+"F68.imprint","IMPRINT",FACE,{"disambiguationData":[TD([[makeQuery(id+"F68.imprint","IMPRINT",EDGE,{"derivedFrom":subQ8}),1.0]])]});}
            var Q4;
            {var subQ3=sQuery(id+"F68.wireOp",EDGE,"E561.167");Q4=makeQuery(id+"F68.imprint","IMPRINT",FACE,{"disambiguationData":[TD([[makeQuery(id+"F68.imprint","IMPRINT",EDGE,{"derivedFrom":subQ3}),-1.0]])]});}
            var Q5;
            {var subQ5=sQuery(id+"F68.wireOp",EDGE,"E561.175");Q5=makeQuery(id+"F68.imprint","IMPRINT",FACE,{"disambiguationData":[TD([[makeQuery(id+"F68.imprint","IMPRINT",EDGE,{"derivedFrom":subQ5}),-1.0]])]});}
            var Q6;
            {var subQ4=sQuery(id+"F68.wireOp",EDGE,"E561.100");Q6=makeQuery(id+"F68.imprint","IMPRINT",FACE,{"disambiguationData":[TD([[makeQuery(id+"F68.imprint","IMPRINT",EDGE,{"derivedFrom":subQ4}),-1.0]])]});}
            var Q7;
            {var subQ6=sQuery(id+"F68.wireOp",EDGE,"E561.126");Q7=makeQuery(id+"F68.imprint","IMPRINT",FACE,{"disambiguationData":[TD([[makeQuery(id+"F68.imprint","IMPRINT",EDGE,{"derivedFrom":subQ6}),-1.0]])]});}
            var Q8;
            {var subQ1=sQuery(id+"F68.wireOp",EDGE,"E561.95");Q8=makeQuery(id+"F68.imprint","IMPRINT",FACE,{"disambiguationData":[TD([[makeQuery(id+"F68.imprint","IMPRINT",EDGE,{"derivedFrom":subQ1}),-1.0]])]});}
            var Q9;
            {var subQ8=sQuery(id+"F68.wireOp",EDGE,"E561.99");Q9=makeQuery(id+"F68.imprint","IMPRINT",FACE,{"disambiguationData":[TD([[makeQuery(id+"F68.imprint","IMPRINT",EDGE,{"derivedFrom":subQ8}),1.0]])]});}
            var Q10;
            {var subQ3=sQuery(id+"F68.wireOp",EDGE,"E561.110");Q10=makeQuery(id+"F68.imprint","IMPRINT",FACE,{"disambiguationData":[TD([[makeQuery(id+"F68.imprint","IMPRINT",EDGE,{"derivedFrom":subQ3}),-1.0]])]});}
            var Q11;
            {var subQ14=sQuery(id+"F68.wireOp",EDGE,"E561.118");Q11=makeQuery(id+"F68.imprint","IMPRINT",FACE,{"disambiguationData":[TD([[makeQuery(id+"F68.imprint","IMPRINT",EDGE,{"derivedFrom":subQ14}),-1.0]])]});}
            var Q12;
            {var subQ4=sQuery(id+"F68.wireOp",EDGE,"E561.81");Q12=makeQuery(id+"F68.imprint","IMPRINT",FACE,{"disambiguationData":[TD([[makeQuery(id+"F68.imprint","IMPRINT",EDGE,{"derivedFrom":subQ4}),1.0]])]});}
            var Q13;
            {var subQ7=sQuery(id+"F68.wireOp",EDGE,"E561.81");Q13=makeQuery(id+"F68.imprint","IMPRINT",FACE,{"disambiguationData":[TD([[makeQuery(id+"F68.imprint","IMPRINT",EDGE,{"derivedFrom":subQ7}),-1.0]])]});}
            var Q14;
            {var subQ5=sQuery(id+"F68.wireOp",EDGE,"E561.63");Q14=makeQuery(id+"F68.imprint","IMPRINT",FACE,{"disambiguationData":[TD([[makeQuery(id+"F68.imprint","IMPRINT",EDGE,{"derivedFrom":subQ5}),1.0]])]});}
            var Q15;
            {var subQ3=sQuery(id+"F68.wireOp",EDGE,"E561.63");Q15=makeQuery(id+"F68.imprint","IMPRINT",FACE,{"disambiguationData":[TD([[makeQuery(id+"F68.imprint","IMPRINT",EDGE,{"derivedFrom":subQ3}),-1.0]])]});}
            var Q16;
            {var subQ5=sQuery(id+"F68.wireOp",EDGE,"E561.45");Q16=makeQuery(id+"F68.imprint","IMPRINT",FACE,{"disambiguationData":[TD([[makeQuery(id+"F68.imprint","IMPRINT",EDGE,{"derivedFrom":subQ5}),1.0]])]});}
            var Q17;
            {var subQ1=sQuery(id+"F68.wireOp",EDGE,"E561.45");Q17=makeQuery(id+"F68.imprint","IMPRINT",FACE,{"disambiguationData":[TD([[makeQuery(id+"F68.imprint","IMPRINT",EDGE,{"derivedFrom":subQ1}),-1.0]])]});}
            var Q18;
            {var subQ5=sQuery(id+"F68.wireOp",EDGE,"E565.81");Q18=makeQuery(id+"F68.imprint","IMPRINT",FACE,{"disambiguationData":[TD([[makeQuery(id+"F68.imprint","IMPRINT",EDGE,{"derivedFrom":subQ5}),1.0]])]});}
            var Q19;
            {var subQ10=sQuery(id+"F68.wireOp",EDGE,"E565.81");Q19=makeQuery(id+"F68.imprint","IMPRINT",FACE,{"disambiguationData":[TD([[makeQuery(id+"F68.imprint","IMPRINT",EDGE,{"derivedFrom":subQ10}),-1.0]])]});}
            var Q20;
            {var subQ5=sQuery(id+"F68.wireOp",EDGE,"E566.81");Q20=makeQuery(id+"F68.imprint","IMPRINT",FACE,{"disambiguationData":[TD([[makeQuery(id+"F68.imprint","IMPRINT",EDGE,{"derivedFrom":subQ5}),1.0]])]});}
            var Q21;
            {var subQ10=sQuery(id+"F68.wireOp",EDGE,"E566.81");Q21=makeQuery(id+"F68.imprint","IMPRINT",FACE,{"disambiguationData":[TD([[makeQuery(id+"F68.imprint","IMPRINT",EDGE,{"derivedFrom":subQ10}),-1.0]])]});}
            var Q22;
            {var subQ5=sQuery(id+"F68.wireOp",EDGE,"E567.81");Q22=makeQuery(id+"F68.imprint","IMPRINT",FACE,{"disambiguationData":[TD([[makeQuery(id+"F68.imprint","IMPRINT",EDGE,{"derivedFrom":subQ5}),1.0]])]});}
            var Q23;
            {var subQ11=sQuery(id+"F68.wireOp",EDGE,"E567.81");Q23=makeQuery(id+"F68.imprint","IMPRINT",FACE,{"disambiguationData":[TD([[makeQuery(id+"F68.imprint","IMPRINT",EDGE,{"derivedFrom":subQ11}),-1.0]])]});}
            extrude(context, id + "F69", {"entities" : qUnion([Q0, Q1, Q2, Q3, Q4, Q5, Q6, Q7, Q8, Q9, Q10, Q11, Q12, Q13, Q14, Q15, Q16, Q17, Q18, Q19, Q20, Q21, Q22, Q23]), "depth" : 50 * mm, "offsetDistance" : 25 * mm});
        }
        {
            var Q0;
            Q0=makeQuery(id+"F69.opExtrude","CAP_FACE",FACE,{"disambiguationData":[OSD([sQuery(id+"F22.wireOp",EDGE,"E241.36"),sQuery(id+"F22.wireOp",EDGE,"E241.37"),sQuery(id+"F22.wireOp",EDGE,"E241.42"),sQuery(id+"F22.wireOp",EDGE,"E241.46"),sQuery(id+"F68.wireOp",EDGE,"E561.155"),sQuery(id+"F68.wireOp",EDGE,"E561.157"),sQuery(id+"F68.wireOp",EDGE,"E561.162"),sQuery(id+"F68.wireOp",EDGE,"E561.170"),sQuery(id+"F68.wireOp",EDGE,"E561.172"),sQuery(id+"F68.wireOp",EDGE,"E561.182"),sQuery(id+"F68.wireOp",EDGE,"E561.187"),sQuery(id+"F68.wireOp",EDGE,"E561.202"),sQuery(id+"F68.wireOp",EDGE,"E561.206")])],"isStart":false});
            var sketch = newSketch(context, id + "F70", { "sketchPlane" : qUnion([Q0])});
            skPoint(sketch, "E568.0", {"position": v(25260, 1100) * mm});
            skPoint(sketch, "E568.1", {"position": v(22460, 1100) * mm});
            skPoint(sketch, "E568.2", {"position": v(28060, 1100) * mm});
            skPoint(sketch, "E568.3", {"position": v(28060, 1100) * mm});
            skLineSegment(sketch, "E568.4", {"start": v(28210, 3850) * mm, "end": v(28210, 1050) * mm});
            skLineSegment(sketch, "E568.5", {"start": v(26210, 1050) * mm, "end": v(26210, 3850) * mm});
            skLineSegment(sketch, "E568.6", {"start": v(26310, 3850) * mm, "end": v(28110, 3850) * mm});
            skLineSegment(sketch, "E568.7", {"start": v(28110, 3850) * mm, "end": v(28110, 1050) * mm});
            skLineSegment(sketch, "E568.8", {"start": v(26310, 3850) * mm, "end": v(28110, 3850) * mm});
            skLineSegment(sketch, "E568.9", {"start": v(26310, 1050) * mm, "end": v(26310, 3850) * mm});
            skLineSegment(sketch, "E568.10", {"start": v(28210, 1050) * mm, "end": v(28110, 1050) * mm});
            skLineSegment(sketch, "E568.11", {"start": v(26310, 1050) * mm, "end": v(26210, 1050) * mm});
            skLineSegment(sketch, "E568.12", {"start": v(26210, 1050) * mm, "end": v(28210, 1050) * mm});
            skLineSegment(sketch, "E568.13", {"start": v(28060, 3800) * mm, "end": v(26360, 3800) * mm});
            skLineSegment(sketch, "E568.14", {"start": v(26360, 3800) * mm, "end": v(26360, 1100) * mm});
            skLineSegment(sketch, "E568.15", {"start": v(28210, 3950) * mm, "end": v(28210, 1050) * mm});
            skLineSegment(sketch, "E568.16", {"start": v(26210, 3950) * mm, "end": v(26210, 1050) * mm});
            skLineSegment(sketch, "E568.17", {"start": v(26210, 3950) * mm, "end": v(28210, 3950) * mm});
            skLineSegment(sketch, "E568.18", {"start": v(28060, 1100) * mm, "end": v(26360, 1100) * mm});
            skLineSegment(sketch, "E568.19", {"start": v(28060, 3800) * mm, "end": v(28060, 1100) * mm});
            skLineSegment(sketch, "E568.20", {"start": v(28210, 3850) * mm, "end": v(28210, 3850) * mm});
            skPoint(sketch, "E568.21", {"position": v(25260, 1100) * mm});
            skLineSegment(sketch, "E568.22", {"start": v(25410, 3850) * mm, "end": v(25410, 1050) * mm});
            skLineSegment(sketch, "E568.23", {"start": v(23410, 1050) * mm, "end": v(23410, 3850) * mm});
            skLineSegment(sketch, "E568.24", {"start": v(23510, 3850) * mm, "end": v(25310, 3850) * mm});
            skLineSegment(sketch, "E568.25", {"start": v(25310, 3850) * mm, "end": v(25310, 1050) * mm});
            skLineSegment(sketch, "E568.26", {"start": v(23510, 3850) * mm, "end": v(25310, 3850) * mm});
            skLineSegment(sketch, "E568.27", {"start": v(23510, 1050) * mm, "end": v(23510, 3850) * mm});
            skLineSegment(sketch, "E568.28", {"start": v(25410, 1050) * mm, "end": v(25310, 1050) * mm});
            skLineSegment(sketch, "E568.29", {"start": v(23510, 1050) * mm, "end": v(23410, 1050) * mm});
            skLineSegment(sketch, "E568.30", {"start": v(23410, 1050) * mm, "end": v(25410, 1050) * mm});
            skLineSegment(sketch, "E568.31", {"start": v(25260, 3800) * mm, "end": v(23560, 3800) * mm});
            skLineSegment(sketch, "E568.32", {"start": v(23560, 3800) * mm, "end": v(23560, 1100) * mm});
            skLineSegment(sketch, "E568.33", {"start": v(25410, 3950) * mm, "end": v(25410, 1050) * mm});
            skLineSegment(sketch, "E568.34", {"start": v(23410, 3950) * mm, "end": v(23410, 1050) * mm});
            skLineSegment(sketch, "E568.35", {"start": v(23410, 3950) * mm, "end": v(25410, 3950) * mm});
            skLineSegment(sketch, "E568.36", {"start": v(25260, 1100) * mm, "end": v(23560, 1100) * mm});
            skLineSegment(sketch, "E568.37", {"start": v(25260, 3800) * mm, "end": v(25260, 1100) * mm});
            skLineSegment(sketch, "E568.38", {"start": v(25410, 3850) * mm, "end": v(25410, 3850) * mm});
            skPoint(sketch, "E568.39", {"position": v(22460, 1100) * mm});
            skLineSegment(sketch, "E568.40", {"start": v(22610, 3850) * mm, "end": v(22610, 1050) * mm});
            skLineSegment(sketch, "E568.41", {"start": v(20610, 1050) * mm, "end": v(20610, 3850) * mm});
            skLineSegment(sketch, "E568.42", {"start": v(20710, 3850) * mm, "end": v(22510, 3850) * mm});
            skLineSegment(sketch, "E568.43", {"start": v(22510, 3850) * mm, "end": v(22510, 1050) * mm});
            skLineSegment(sketch, "E568.44", {"start": v(20710, 3850) * mm, "end": v(22510, 3850) * mm});
            skLineSegment(sketch, "E568.45", {"start": v(20710, 1050) * mm, "end": v(20710, 3850) * mm});
            skLineSegment(sketch, "E568.46", {"start": v(22610, 1050) * mm, "end": v(22510, 1050) * mm});
            skLineSegment(sketch, "E568.47", {"start": v(20710, 1050) * mm, "end": v(20610, 1050) * mm});
            skLineSegment(sketch, "E568.48", {"start": v(20610, 1050) * mm, "end": v(22610, 1050) * mm});
            skLineSegment(sketch, "E568.49", {"start": v(22460, 3800) * mm, "end": v(20760, 3800) * mm});
            skLineSegment(sketch, "E568.50", {"start": v(20760, 3800) * mm, "end": v(20760, 1100) * mm});
            skLineSegment(sketch, "E568.51", {"start": v(22610, 3950) * mm, "end": v(22610, 1050) * mm});
            skLineSegment(sketch, "E568.52", {"start": v(20610, 3950) * mm, "end": v(20610, 1050) * mm});
            skLineSegment(sketch, "E568.53", {"start": v(20610, 3950) * mm, "end": v(22610, 3950) * mm});
            skLineSegment(sketch, "E568.54", {"start": v(22460, 1100) * mm, "end": v(20760, 1100) * mm});
            skLineSegment(sketch, "E568.55", {"start": v(22460, 3800) * mm, "end": v(22460, 1100) * mm});
            skLineSegment(sketch, "E568.56", {"start": v(22610, 3850) * mm, "end": v(22610, 3850) * mm});
            skLineSegment(sketch, "E568.57", {"start": v(14010, 3950) * mm, "end": v(16010, 3950) * mm});
            skPoint(sketch, "E568.58", {"position": v(15860, 1100) * mm});
            skLineSegment(sketch, "E568.59", {"start": v(18660, 1100) * mm, "end": v(16960, 1100) * mm});
            skLineSegment(sketch, "E568.60", {"start": v(13060, 1100) * mm, "end": v(11360, 1100) * mm});
            skLineSegment(sketch, "E568.61", {"start": v(15860, 3800) * mm, "end": v(15860, 1100) * mm});
            skLineSegment(sketch, "E568.62", {"start": v(11210, 3950) * mm, "end": v(13210, 3950) * mm});
            skPoint(sketch, "E568.63", {"position": v(18660, 1100) * mm});
            skLineSegment(sketch, "E568.64", {"start": v(18660, 3800) * mm, "end": v(16960, 3800) * mm});
            skLineSegment(sketch, "E568.65", {"start": v(14010, 1050) * mm, "end": v(16010, 1050) * mm});
            skLineSegment(sketch, "E568.66", {"start": v(14160, 3800) * mm, "end": v(14160, 1100) * mm});
            skLineSegment(sketch, "E568.67", {"start": v(13060, 3800) * mm, "end": v(11360, 3800) * mm});
            skLineSegment(sketch, "E568.68", {"start": v(18810, 3950) * mm, "end": v(18810, 1050) * mm});
            skLineSegment(sketch, "E568.69", {"start": v(16810, 1050) * mm, "end": v(18810, 1050) * mm});
            skPoint(sketch, "E568.70", {"position": v(13060, 1100) * mm});
            skLineSegment(sketch, "E568.71", {"start": v(18660, 3800) * mm, "end": v(18660, 1100) * mm});
            skLineSegment(sketch, "E568.72", {"start": v(16810, 3950) * mm, "end": v(18810, 3950) * mm});
            skLineSegment(sketch, "E568.73", {"start": v(11310, 3850) * mm, "end": v(13110, 3850) * mm});
            skLineSegment(sketch, "E568.74", {"start": v(14010, 3950) * mm, "end": v(14010, 1050) * mm});
            skLineSegment(sketch, "E568.75", {"start": v(13210, 3950) * mm, "end": v(13210, 1050) * mm});
            skLineSegment(sketch, "E568.76", {"start": v(16960, 3800) * mm, "end": v(16960, 1100) * mm});
            skLineSegment(sketch, "E568.77", {"start": v(13060, 3800) * mm, "end": v(13060, 1100) * mm});
            skLineSegment(sketch, "E568.78", {"start": v(15860, 3800) * mm, "end": v(14160, 3800) * mm});
            skLineSegment(sketch, "E568.79", {"start": v(14110, 3850) * mm, "end": v(15910, 3850) * mm});
            skLineSegment(sketch, "E568.80", {"start": v(18710, 3850) * mm, "end": v(18710, 1050) * mm});
            skLineSegment(sketch, "E568.81", {"start": v(16810, 3950) * mm, "end": v(16810, 1050) * mm});
            skLineSegment(sketch, "E568.82", {"start": v(16010, 3950) * mm, "end": v(16010, 1050) * mm});
            skLineSegment(sketch, "E568.83", {"start": v(11210, 1050) * mm, "end": v(11210, 3850) * mm});
            skLineSegment(sketch, "E568.84", {"start": v(11360, 3800) * mm, "end": v(11360, 1100) * mm});
            skLineSegment(sketch, "E568.85", {"start": v(16910, 3850) * mm, "end": v(18710, 3850) * mm});
            skLineSegment(sketch, "E568.86", {"start": v(15860, 1100) * mm, "end": v(14160, 1100) * mm});
            skLineSegment(sketch, "E568.87", {"start": v(11210, 1050) * mm, "end": v(13210, 1050) * mm});
            skLineSegment(sketch, "E568.88", {"start": v(11310, 1050) * mm, "end": v(11310, 3850) * mm});
            skLineSegment(sketch, "E568.89", {"start": v(13110, 3850) * mm, "end": v(13110, 1050) * mm});
            skLineSegment(sketch, "E568.90", {"start": v(14110, 3850) * mm, "end": v(15910, 3850) * mm});
            skLineSegment(sketch, "E568.91", {"start": v(16910, 1050) * mm, "end": v(16910, 3850) * mm});
            skLineSegment(sketch, "E568.92", {"start": v(11210, 3950) * mm, "end": v(11210, 1050) * mm});
            skLineSegment(sketch, "E568.93", {"start": v(14110, 1050) * mm, "end": v(14110, 3850) * mm});
            skLineSegment(sketch, "E568.94", {"start": v(11310, 3850) * mm, "end": v(13110, 3850) * mm});
            skPoint(sketch, "E568.95", {"position": v(15860, 1100) * mm});
            skLineSegment(sketch, "E568.96", {"start": v(13210, 3850) * mm, "end": v(13210, 1050) * mm});
            skLineSegment(sketch, "E568.97", {"start": v(16910, 3850) * mm, "end": v(18710, 3850) * mm});
            skLineSegment(sketch, "E568.98", {"start": v(14010, 1050) * mm, "end": v(14010, 3850) * mm});
            skLineSegment(sketch, "E568.99", {"start": v(16810, 1050) * mm, "end": v(16810, 3850) * mm});
            skLineSegment(sketch, "E568.100", {"start": v(15910, 3850) * mm, "end": v(15910, 1050) * mm});
            skPoint(sketch, "E568.101", {"position": v(13060, 1100) * mm});
            skLineSegment(sketch, "E568.102", {"start": v(18810, 3850) * mm, "end": v(18810, 1050) * mm});
            skPoint(sketch, "E568.103", {"position": v(18660, 1100) * mm});
            skLineSegment(sketch, "E568.104", {"start": v(16010, 3850) * mm, "end": v(16010, 1050) * mm});
            skLineSegment(sketch, "E568.105", {"start": v(16910, 1050) * mm, "end": v(16810, 1050) * mm});
            skLineSegment(sketch, "E568.106", {"start": v(18810, 1050) * mm, "end": v(18710, 1050) * mm});
            skLineSegment(sketch, "E568.107", {"start": v(11310, 1050) * mm, "end": v(11210, 1050) * mm});
            skLineSegment(sketch, "E568.108", {"start": v(13210, 3850) * mm, "end": v(13210, 3850) * mm});
            skLineSegment(sketch, "E568.109", {"start": v(14110, 1050) * mm, "end": v(14010, 1050) * mm});
            skLineSegment(sketch, "E568.110", {"start": v(18810, 3850) * mm, "end": v(18810, 3850) * mm});
            skLineSegment(sketch, "E568.111", {"start": v(13210, 1050) * mm, "end": v(13110, 1050) * mm});
            skLineSegment(sketch, "E568.112", {"start": v(16010, 3850) * mm, "end": v(16010, 3850) * mm});
            skLineSegment(sketch, "E568.113", {"start": v(16010, 1050) * mm, "end": v(15910, 1050) * mm});
            skLineSegment(sketch, "E568.114", {"start": v(4610, 3950) * mm, "end": v(6610, 3950) * mm});
            skPoint(sketch, "E568.115", {"position": v(6460, 1100) * mm});
            skLineSegment(sketch, "E568.116", {"start": v(9260, 1100) * mm, "end": v(7560, 1100) * mm});
            skLineSegment(sketch, "E568.117", {"start": v(3660, 1100) * mm, "end": v(1960, 1100) * mm});
            skLineSegment(sketch, "E568.118", {"start": v(6460, 3800) * mm, "end": v(6460, 1100) * mm});
            skLineSegment(sketch, "E568.119", {"start": v(1810, 3950) * mm, "end": v(3810, 3950) * mm});
            skPoint(sketch, "E568.120", {"position": v(9260, 1100) * mm});
            skLineSegment(sketch, "E568.121", {"start": v(9260, 3800) * mm, "end": v(7560, 3800) * mm});
            skLineSegment(sketch, "E568.122", {"start": v(4610, 1050) * mm, "end": v(6610, 1050) * mm});
            skLineSegment(sketch, "E568.123", {"start": v(4760, 3800) * mm, "end": v(4760, 1100) * mm});
            skLineSegment(sketch, "E568.124", {"start": v(3660, 3800) * mm, "end": v(1960, 3800) * mm});
            skLineSegment(sketch, "E568.125", {"start": v(9410, 3950) * mm, "end": v(9410, 1050) * mm});
            skLineSegment(sketch, "E568.126", {"start": v(7410, 1050) * mm, "end": v(9410, 1050) * mm});
            skPoint(sketch, "E568.127", {"position": v(3660, 1100) * mm});
            skLineSegment(sketch, "E568.128", {"start": v(9260, 3800) * mm, "end": v(9260, 1100) * mm});
            skLineSegment(sketch, "E568.129", {"start": v(7410, 3950) * mm, "end": v(9410, 3950) * mm});
            skLineSegment(sketch, "E568.130", {"start": v(1910, 3850) * mm, "end": v(3710, 3850) * mm});
            skLineSegment(sketch, "E568.131", {"start": v(4610, 3950) * mm, "end": v(4610, 1050) * mm});
            skLineSegment(sketch, "E568.132", {"start": v(3810, 3950) * mm, "end": v(3810, 1050) * mm});
            skLineSegment(sketch, "E568.133", {"start": v(7560, 3800) * mm, "end": v(7560, 1100) * mm});
            skLineSegment(sketch, "E568.134", {"start": v(3660, 3800) * mm, "end": v(3660, 1100) * mm});
            skLineSegment(sketch, "E568.135", {"start": v(6460, 3800) * mm, "end": v(4760, 3800) * mm});
            skLineSegment(sketch, "E568.136", {"start": v(4710, 3850) * mm, "end": v(6510, 3850) * mm});
            skLineSegment(sketch, "E568.137", {"start": v(9310, 3850) * mm, "end": v(9310, 1050) * mm});
            skLineSegment(sketch, "E568.138", {"start": v(7410, 3950) * mm, "end": v(7410, 1050) * mm});
            skLineSegment(sketch, "E568.139", {"start": v(6610, 3950) * mm, "end": v(6610, 1050) * mm});
            skLineSegment(sketch, "E568.140", {"start": v(1810, 1050) * mm, "end": v(1810, 3850) * mm});
            skLineSegment(sketch, "E568.141", {"start": v(1960, 3800) * mm, "end": v(1960, 1100) * mm});
            skLineSegment(sketch, "E568.142", {"start": v(7510, 3850) * mm, "end": v(9310, 3850) * mm});
            skLineSegment(sketch, "E568.143", {"start": v(6460, 1100) * mm, "end": v(4760, 1100) * mm});
            skLineSegment(sketch, "E568.144", {"start": v(1810, 1050) * mm, "end": v(3810, 1050) * mm});
            skLineSegment(sketch, "E568.145", {"start": v(1910, 1050) * mm, "end": v(1910, 3850) * mm});
            skLineSegment(sketch, "E568.146", {"start": v(3710, 3850) * mm, "end": v(3710, 1050) * mm});
            skLineSegment(sketch, "E568.147", {"start": v(4710, 3850) * mm, "end": v(6510, 3850) * mm});
            skLineSegment(sketch, "E568.148", {"start": v(7510, 1050) * mm, "end": v(7510, 3850) * mm});
            skLineSegment(sketch, "E568.149", {"start": v(1810, 3950) * mm, "end": v(1810, 1050) * mm});
            skLineSegment(sketch, "E568.150", {"start": v(4710, 1050) * mm, "end": v(4710, 3850) * mm});
            skLineSegment(sketch, "E568.151", {"start": v(1910, 3850) * mm, "end": v(3710, 3850) * mm});
            skPoint(sketch, "E568.152", {"position": v(6460, 1100) * mm});
            skLineSegment(sketch, "E568.153", {"start": v(3810, 3850) * mm, "end": v(3810, 1050) * mm});
            skLineSegment(sketch, "E568.154", {"start": v(7510, 3850) * mm, "end": v(9310, 3850) * mm});
            skLineSegment(sketch, "E568.155", {"start": v(4610, 1050) * mm, "end": v(4610, 3850) * mm});
            skLineSegment(sketch, "E568.156", {"start": v(7410, 1050) * mm, "end": v(7410, 3850) * mm});
            skLineSegment(sketch, "E568.157", {"start": v(6510, 3850) * mm, "end": v(6510, 1050) * mm});
            skPoint(sketch, "E568.158", {"position": v(3660, 1100) * mm});
            skLineSegment(sketch, "E568.159", {"start": v(9410, 3850) * mm, "end": v(9410, 1050) * mm});
            skPoint(sketch, "E568.160", {"position": v(9260, 1100) * mm});
            skLineSegment(sketch, "E568.161", {"start": v(6610, 3850) * mm, "end": v(6610, 1050) * mm});
            skLineSegment(sketch, "E568.162", {"start": v(7510, 1050) * mm, "end": v(7410, 1050) * mm});
            skLineSegment(sketch, "E568.163", {"start": v(9410, 1050) * mm, "end": v(9310, 1050) * mm});
            skLineSegment(sketch, "E568.164", {"start": v(1910, 1050) * mm, "end": v(1810, 1050) * mm});
            skLineSegment(sketch, "E568.165", {"start": v(3810, 3850) * mm, "end": v(3810, 3850) * mm});
            skLineSegment(sketch, "E568.166", {"start": v(4710, 1050) * mm, "end": v(4610, 1050) * mm});
            skLineSegment(sketch, "E568.167", {"start": v(9410, 3850) * mm, "end": v(9410, 3850) * mm});
            skLineSegment(sketch, "E568.168", {"start": v(3810, 1050) * mm, "end": v(3710, 1050) * mm});
            skLineSegment(sketch, "E568.169", {"start": v(6610, 3850) * mm, "end": v(6610, 3850) * mm});
            skLineSegment(sketch, "E568.170", {"start": v(6610, 1050) * mm, "end": v(6510, 1050) * mm});
            skLineSegment(sketch, "E568.171", {"start": v(28210, 1050) * mm, "end": v(18810, 1050) * mm});
            skPoint(sketch, "E568.172", {"position": v(29660, 1100) * mm});
            skPoint(sketch, "E568.173", {"position": v(32460, 1100) * mm});
            skPoint(sketch, "E568.174", {"position": v(35260, 1100) * mm});
            skPoint(sketch, "E568.175", {"position": v(31360, 1100) * mm});
            skPoint(sketch, "E568.176", {"position": v(31360, 1100) * mm});
            skLineSegment(sketch, "E568.177", {"start": v(31510, 3850) * mm, "end": v(31510, 1050) * mm});
            skLineSegment(sketch, "E568.178", {"start": v(29510, 1050) * mm, "end": v(29510, 3850) * mm});
            skLineSegment(sketch, "E568.179", {"start": v(29610, 3850) * mm, "end": v(31410, 3850) * mm});
            skLineSegment(sketch, "E568.180", {"start": v(31410, 3850) * mm, "end": v(31410, 1050) * mm});
            skLineSegment(sketch, "E568.181", {"start": v(29610, 3850) * mm, "end": v(31410, 3850) * mm});
            skLineSegment(sketch, "E568.182", {"start": v(29610, 1050) * mm, "end": v(29610, 3850) * mm});
            skLineSegment(sketch, "E568.183", {"start": v(31510, 1050) * mm, "end": v(31410, 1050) * mm});
            skLineSegment(sketch, "E568.184", {"start": v(29610, 1050) * mm, "end": v(29510, 1050) * mm});
            skLineSegment(sketch, "E568.185", {"start": v(29510, 1050) * mm, "end": v(31510, 1050) * mm});
            skLineSegment(sketch, "E568.186", {"start": v(31360, 3800) * mm, "end": v(29660, 3800) * mm});
            skLineSegment(sketch, "E568.187", {"start": v(29660, 3800) * mm, "end": v(29660, 1100) * mm});
            skLineSegment(sketch, "E568.188", {"start": v(31510, 3950) * mm, "end": v(31510, 1050) * mm});
            skLineSegment(sketch, "E568.189", {"start": v(29510, 3950) * mm, "end": v(29510, 1050) * mm});
            skLineSegment(sketch, "E568.190", {"start": v(29510, 3950) * mm, "end": v(31510, 3950) * mm});
            skLineSegment(sketch, "E568.191", {"start": v(31360, 1100) * mm, "end": v(29660, 1100) * mm});
            skLineSegment(sketch, "E568.192", {"start": v(31360, 3800) * mm, "end": v(31360, 1100) * mm});
            skLineSegment(sketch, "E568.193", {"start": v(31510, 3850) * mm, "end": v(31510, 3850) * mm});
            skPoint(sketch, "E568.194", {"position": v(34160, 1100) * mm});
            skPoint(sketch, "E568.195", {"position": v(34160, 1100) * mm});
            skLineSegment(sketch, "E568.196", {"start": v(34310, 3850) * mm, "end": v(34310, 1050) * mm});
            skLineSegment(sketch, "E568.197", {"start": v(32310, 1050) * mm, "end": v(32310, 3850) * mm});
            skLineSegment(sketch, "E568.198", {"start": v(32410, 3850) * mm, "end": v(34210, 3850) * mm});
            skLineSegment(sketch, "E568.199", {"start": v(34210, 3850) * mm, "end": v(34210, 1050) * mm});
            skLineSegment(sketch, "E568.200", {"start": v(32410, 3850) * mm, "end": v(34210, 3850) * mm});
            skLineSegment(sketch, "E568.201", {"start": v(32410, 1050) * mm, "end": v(32410, 3850) * mm});
            skLineSegment(sketch, "E568.202", {"start": v(34310, 1050) * mm, "end": v(34210, 1050) * mm});
            skLineSegment(sketch, "E568.203", {"start": v(32410, 1050) * mm, "end": v(32310, 1050) * mm});
            skLineSegment(sketch, "E568.204", {"start": v(32310, 1050) * mm, "end": v(34310, 1050) * mm});
            skLineSegment(sketch, "E568.205", {"start": v(34160, 3800) * mm, "end": v(32460, 3800) * mm});
            skLineSegment(sketch, "E568.206", {"start": v(32460, 3800) * mm, "end": v(32460, 1100) * mm});
            skLineSegment(sketch, "E568.207", {"start": v(34310, 3950) * mm, "end": v(34310, 1050) * mm});
            skLineSegment(sketch, "E568.208", {"start": v(32310, 3950) * mm, "end": v(32310, 1050) * mm});
            skLineSegment(sketch, "E568.209", {"start": v(32310, 3950) * mm, "end": v(34310, 3950) * mm});
            skLineSegment(sketch, "E568.210", {"start": v(34160, 1100) * mm, "end": v(32460, 1100) * mm});
            skLineSegment(sketch, "E568.211", {"start": v(34160, 3800) * mm, "end": v(34160, 1100) * mm});
            skLineSegment(sketch, "E568.212", {"start": v(34310, 3850) * mm, "end": v(34310, 3850) * mm});
            skPoint(sketch, "E568.213", {"position": v(36960, 1100) * mm});
            skPoint(sketch, "E568.214", {"position": v(36960, 1100) * mm});
            skLineSegment(sketch, "E568.215", {"start": v(37110, 3850) * mm, "end": v(37110, 1050) * mm});
            skLineSegment(sketch, "E568.216", {"start": v(35110, 1050) * mm, "end": v(35110, 3850) * mm});
            skLineSegment(sketch, "E568.217", {"start": v(35210, 3850) * mm, "end": v(37010, 3850) * mm});
            skLineSegment(sketch, "E568.218", {"start": v(37010, 3850) * mm, "end": v(37010, 1050) * mm});
            skLineSegment(sketch, "E568.219", {"start": v(35210, 3850) * mm, "end": v(37010, 3850) * mm});
            skLineSegment(sketch, "E568.220", {"start": v(35210, 1050) * mm, "end": v(35210, 3850) * mm});
            skLineSegment(sketch, "E568.221", {"start": v(37110, 1050) * mm, "end": v(37010, 1050) * mm});
            skLineSegment(sketch, "E568.222", {"start": v(35210, 1050) * mm, "end": v(35110, 1050) * mm});
            skLineSegment(sketch, "E568.223", {"start": v(35110, 1050) * mm, "end": v(37110, 1050) * mm});
            skLineSegment(sketch, "E568.224", {"start": v(36960, 3800) * mm, "end": v(35260, 3800) * mm});
            skLineSegment(sketch, "E568.225", {"start": v(35260, 3800) * mm, "end": v(35260, 1100) * mm});
            skLineSegment(sketch, "E568.226", {"start": v(37110, 3950) * mm, "end": v(37110, 1050) * mm});
            skLineSegment(sketch, "E568.227", {"start": v(35110, 3950) * mm, "end": v(35110, 1050) * mm});
            skLineSegment(sketch, "E568.228", {"start": v(35110, 3950) * mm, "end": v(37110, 3950) * mm});
            skLineSegment(sketch, "E568.229", {"start": v(36960, 1100) * mm, "end": v(35260, 1100) * mm});
            skLineSegment(sketch, "E568.230", {"start": v(36960, 3800) * mm, "end": v(36960, 1100) * mm});
            skLineSegment(sketch, "E568.231", {"start": v(37110, 3850) * mm, "end": v(37110, 3850) * mm});
            skSolve(sketch);
        }
        {
            var Q0;
            {var subQ8=sQuery(id+"F70.wireOp",EDGE,"E568.119");Q0=makeQuery(id+"F70.imprint","IMPRINT",FACE,{"disambiguationData":[TD([[makeQuery(id+"F70.imprint","IMPRINT",EDGE,{"derivedFrom":subQ8}),-1.0]])]});}
            var Q1;
            {var subQ1=sQuery(id+"F70.wireOp",EDGE,"E568.114");Q1=makeQuery(id+"F70.imprint","IMPRINT",FACE,{"disambiguationData":[TD([[makeQuery(id+"F70.imprint","IMPRINT",EDGE,{"derivedFrom":subQ1}),-1.0]])]});}
            var Q2;
            {var subQ0=sQuery(id+"F70.wireOp",EDGE,"E568.129");Q2=makeQuery(id+"F70.imprint","IMPRINT",FACE,{"disambiguationData":[TD([[makeQuery(id+"F70.imprint","IMPRINT",EDGE,{"derivedFrom":subQ0}),-1.0]])]});}
            var Q3;
            {var subQ1=sQuery(id+"F70.wireOp",EDGE,"E568.62");Q3=makeQuery(id+"F70.imprint","IMPRINT",FACE,{"disambiguationData":[TD([[makeQuery(id+"F70.imprint","IMPRINT",EDGE,{"derivedFrom":subQ1}),-1.0]])]});}
            var Q4;
            {var subQ1=sQuery(id+"F70.wireOp",EDGE,"E568.57");Q4=makeQuery(id+"F70.imprint","IMPRINT",FACE,{"disambiguationData":[TD([[makeQuery(id+"F70.imprint","IMPRINT",EDGE,{"derivedFrom":subQ1}),-1.0]])]});}
            var Q5;
            {var subQ0=sQuery(id+"F70.wireOp",EDGE,"E568.72");Q5=makeQuery(id+"F70.imprint","IMPRINT",FACE,{"disambiguationData":[TD([[makeQuery(id+"F70.imprint","IMPRINT",EDGE,{"derivedFrom":subQ0}),-1.0]])]});}
            var Q6;
            {var subQ7=sQuery(id+"F70.wireOp",EDGE,"E568.43");Q6=makeQuery(id+"F70.imprint","IMPRINT",FACE,{"disambiguationData":[TD([[makeQuery(id+"F70.imprint","IMPRINT",EDGE,{"derivedFrom":subQ7}),1.0]])]});}
            var Q7;
            {var subQ4=sQuery(id+"F70.wireOp",EDGE,"E568.25");Q7=makeQuery(id+"F70.imprint","IMPRINT",FACE,{"disambiguationData":[TD([[makeQuery(id+"F70.imprint","IMPRINT",EDGE,{"derivedFrom":subQ4}),1.0]])]});}
            var Q8;
            {var subQ4=sQuery(id+"F70.wireOp",EDGE,"E568.7");Q8=makeQuery(id+"F70.imprint","IMPRINT",FACE,{"disambiguationData":[TD([[makeQuery(id+"F70.imprint","IMPRINT",EDGE,{"derivedFrom":subQ4}),1.0]])]});}
            var Q9;
            {var subQ4=sQuery(id+"F70.wireOp",EDGE,"E568.180");Q9=makeQuery(id+"F70.imprint","IMPRINT",FACE,{"disambiguationData":[TD([[makeQuery(id+"F70.imprint","IMPRINT",EDGE,{"derivedFrom":subQ4}),1.0]])]});}
            var Q10;
            {var subQ4=sQuery(id+"F70.wireOp",EDGE,"E568.199");Q10=makeQuery(id+"F70.imprint","IMPRINT",FACE,{"disambiguationData":[TD([[makeQuery(id+"F70.imprint","IMPRINT",EDGE,{"derivedFrom":subQ4}),1.0]])]});}
            var Q11;
            {var subQ4=sQuery(id+"F70.wireOp",EDGE,"E568.218");Q11=makeQuery(id+"F70.imprint","IMPRINT",FACE,{"disambiguationData":[TD([[makeQuery(id+"F70.imprint","IMPRINT",EDGE,{"derivedFrom":subQ4}),1.0]])]});}
            extrude(context, id + "F71", {"entities" : qUnion([Q0, Q1, Q2, Q3, Q4, Q5, Q6, Q7, Q8, Q9, Q10, Q11]), "operationType" : NewBodyOperationType.ADD, "depth" : 25 * mm, "offsetDistance" : 25 * mm});
        }
        {
            var Q0;
            Q0=makeQuery(id+"F5.boolean.opBoolean","MERGE",FACE,{"derivedFrom":[makeQuery(id+"F3.boolean.opBoolean","COPY",FACE,{"derivedFrom":makeQuery(id+"F3.opExtrude","SWEPT_FACE",FACE,{"disambiguationData":[OSD([sQuery(id+"F2.wireOp",EDGE,"E19.9")])]})}),makeQuery(id+"F5.opExtrude","SWEPT_FACE",FACE,{"disambiguationData":[OSD([sQuery(id+"F4.wireOp",EDGE,"E34.0")])]})]});
            var sketch = newSketch(context, id + "F72", { "sketchPlane" : qUnion([Q0])});
            skLineSegment(sketch, "E569.bottom", {"start": v(5230, 3350) * mm, "end": v(6630, 3350) * mm});
            skLineSegment(sketch, "E569.top", {"start": v(5230, 1050) * mm, "end": v(6630, 1050) * mm});
            skLineSegment(sketch, "E569.left", {"start": v(5230, 3350) * mm, "end": v(5230, 1050) * mm});
            skLineSegment(sketch, "E569.right", {"start": v(6630, 3350) * mm, "end": v(6630, 1050) * mm});
            skLineSegment(sketch, "E570", {"start": v(5330, 1050) * mm, "end": v(5330, 3250) * mm});
            skLineSegment(sketch, "E571", {"start": v(5330, 3250) * mm, "end": v(6530, 3250) * mm});
            skLineSegment(sketch, "E572", {"start": v(6530, 3250) * mm, "end": v(6530, 1050) * mm});
            skPoint(sketch, "E573", {"position": v(10690, 1100) * mm});
            skPoint(sketch, "E574", {"position": v(15160, 1100) * mm});
            skPoint(sketch, "E575", {"position": v(19360, 1100) * mm});
            skPoint(sketch, "E576", {"position": v(23730, 1100) * mm});
            skLineSegment(sketch, "E577.0", {"start": v(6480, 3200) * mm, "end": v(6480, 1100) * mm});
            skLineSegment(sketch, "E578.0", {"start": v(6480, 3200) * mm, "end": v(5380, 3200) * mm});
            skLineSegment(sketch, "E579.0", {"start": v(5380, 3200) * mm, "end": v(5380, 1100) * mm});
            skLineSegment(sketch, "E580.0", {"start": v(6480, 1100) * mm, "end": v(5380, 1100) * mm});
            skLineSegment(sketch, "E581.bottom", {"start": v(10860, 3350) * mm, "end": v(12260, 3350) * mm});
            skLineSegment(sketch, "E581.top", {"start": v(10860, 1050) * mm, "end": v(12260, 1050) * mm});
            skLineSegment(sketch, "E581.left", {"start": v(10860, 3350) * mm, "end": v(10860, 1050) * mm});
            skLineSegment(sketch, "E581.right", {"start": v(12260, 3350) * mm, "end": v(12260, 1050) * mm});
            skLineSegment(sketch, "E582", {"start": v(10960, 1050) * mm, "end": v(10960, 3250) * mm});
            skLineSegment(sketch, "E583", {"start": v(10960, 3250) * mm, "end": v(12160, 3250) * mm});
            skLineSegment(sketch, "E584", {"start": v(12160, 3250) * mm, "end": v(12160, 1050) * mm});
            skLineSegment(sketch, "E585.0", {"start": v(12110, 3200) * mm, "end": v(12110, 1100) * mm});
            skLineSegment(sketch, "E586.0", {"start": v(12110, 3200) * mm, "end": v(11010, 3200) * mm});
            skLineSegment(sketch, "E587.0", {"start": v(11010, 3200) * mm, "end": v(11010, 1100) * mm});
            skLineSegment(sketch, "E588.0", {"start": v(12110, 1100) * mm, "end": v(11010, 1100) * mm});
            skLineSegment(sketch, "E589.bottom", {"start": v(15210, 3350) * mm, "end": v(16610, 3350) * mm});
            skLineSegment(sketch, "E589.top", {"start": v(15210, 1050) * mm, "end": v(16610, 1050) * mm});
            skLineSegment(sketch, "E589.left", {"start": v(15210, 3350) * mm, "end": v(15210, 1050) * mm});
            skLineSegment(sketch, "E589.right", {"start": v(16610, 3350) * mm, "end": v(16610, 1050) * mm});
            skLineSegment(sketch, "E590", {"start": v(15310, 1050) * mm, "end": v(15310, 3250) * mm});
            skLineSegment(sketch, "E591", {"start": v(15310, 3250) * mm, "end": v(16510, 3250) * mm});
            skLineSegment(sketch, "E592", {"start": v(16510, 3250) * mm, "end": v(16510, 1050) * mm});
            skLineSegment(sketch, "E593.0", {"start": v(16460, 3200) * mm, "end": v(16460, 1100) * mm});
            skLineSegment(sketch, "E594.0", {"start": v(16460, 3200) * mm, "end": v(15360, 3200) * mm});
            skLineSegment(sketch, "E595.0", {"start": v(15360, 3200) * mm, "end": v(15360, 1100) * mm});
            skLineSegment(sketch, "E596.0", {"start": v(16460, 1100) * mm, "end": v(15360, 1100) * mm});
            skLineSegment(sketch, "E597.bottom", {"start": v(19310, 3350) * mm, "end": v(20710, 3350) * mm});
            skLineSegment(sketch, "E597.top", {"start": v(19310, 1050) * mm, "end": v(20710, 1050) * mm});
            skLineSegment(sketch, "E597.left", {"start": v(19310, 3350) * mm, "end": v(19310, 1050) * mm});
            skLineSegment(sketch, "E597.right", {"start": v(20710, 3350) * mm, "end": v(20710, 1050) * mm});
            skLineSegment(sketch, "E598", {"start": v(19410, 1050) * mm, "end": v(19410, 3250) * mm});
            skLineSegment(sketch, "E599", {"start": v(19410, 3250) * mm, "end": v(20610, 3250) * mm});
            skLineSegment(sketch, "E600", {"start": v(20610, 3250) * mm, "end": v(20610, 1050) * mm});
            skLineSegment(sketch, "E601.0", {"start": v(20560, 3200) * mm, "end": v(20560, 1100) * mm});
            skLineSegment(sketch, "E602.0", {"start": v(20560, 3200) * mm, "end": v(19460, 3200) * mm});
            skLineSegment(sketch, "E603.0", {"start": v(19460, 3200) * mm, "end": v(19460, 1100) * mm});
            skLineSegment(sketch, "E604.0", {"start": v(20560, 1100) * mm, "end": v(19460, 1100) * mm});
            skLineSegment(sketch, "E605.bottom", {"start": v(23580, 3350) * mm, "end": v(24980, 3350) * mm});
            skLineSegment(sketch, "E605.top", {"start": v(23580, 1050) * mm, "end": v(24980, 1050) * mm});
            skLineSegment(sketch, "E605.left", {"start": v(23580, 3350) * mm, "end": v(23580, 1050) * mm});
            skLineSegment(sketch, "E605.right", {"start": v(24980, 3350) * mm, "end": v(24980, 1050) * mm});
            skLineSegment(sketch, "E606", {"start": v(23680, 1050) * mm, "end": v(23680, 3250) * mm});
            skLineSegment(sketch, "E607", {"start": v(23680, 3250) * mm, "end": v(24880, 3250) * mm});
            skLineSegment(sketch, "E608", {"start": v(24880, 3250) * mm, "end": v(24880, 1050) * mm});
            skLineSegment(sketch, "E609.0", {"start": v(24830, 3200) * mm, "end": v(24830, 1100) * mm});
            skLineSegment(sketch, "E610.0", {"start": v(24830, 3200) * mm, "end": v(23730, 3200) * mm});
            skLineSegment(sketch, "E611.0", {"start": v(23730, 3200) * mm, "end": v(23730, 1100) * mm});
            skLineSegment(sketch, "E612.0", {"start": v(24830, 1100) * mm, "end": v(23730, 1100) * mm});
            skLineSegment(sketch, "E613.0.0", {"start": v(27160, 0) * mm, "end": v(28260, 0) * mm});
            skLineSegment(sketch, "E613.0.1", {"start": v(28260, 0) * mm, "end": v(28260, 2400) * mm});
            skLineSegment(sketch, "E613.0.2", {"start": v(28260, 2400) * mm, "end": v(27160, 2400) * mm});
            skLineSegment(sketch, "E613.0.3", {"start": v(27160, 2400) * mm, "end": v(27160, 0) * mm});
            skLineSegment(sketch, "E614.bottom", {"start": v(27010, 2550) * mm, "end": v(28410, 2550) * mm});
            skLineSegment(sketch, "E614.left", {"start": v(27010, 2550) * mm, "end": v(27010, -150) * mm});
            skLineSegment(sketch, "E614.right", {"start": v(28410, 2550) * mm, "end": v(28410, -150) * mm});
            skLineSegment(sketch, "E615", {"start": v(27110, -150) * mm, "end": v(27110, 2450) * mm});
            skLineSegment(sketch, "E616", {"start": v(27110, 2450) * mm, "end": v(28310, 2450) * mm});
            skLineSegment(sketch, "E617", {"start": v(28310, 2450) * mm, "end": v(28310, -150) * mm});
            skLineSegment(sketch, "E618", {"start": v(27010, -150) * mm, "end": v(28410, -150) * mm});
            skLineSegment(sketch, "E619.0.0", {"start": v(860, 1200) * mm, "end": v(2660, 1200) * mm});
            skLineSegment(sketch, "E619.0.1", {"start": v(2660, 1200) * mm, "end": v(2660, 3800) * mm});
            skLineSegment(sketch, "E619.0.2", {"start": v(2660, 3800) * mm, "end": v(860, 3800) * mm});
            skLineSegment(sketch, "E619.0.3", {"start": v(860, 3800) * mm, "end": v(860, 1200) * mm});
            skLineSegment(sketch, "E620.bottom", {"start": v(710, 3950) * mm, "end": v(2810, 3950) * mm});
            skLineSegment(sketch, "E620.top", {"start": v(710, 1150) * mm, "end": v(2810, 1150) * mm});
            skLineSegment(sketch, "E620.left", {"start": v(710, 3950) * mm, "end": v(710, 1150) * mm});
            skLineSegment(sketch, "E620.right", {"start": v(2810, 3950) * mm, "end": v(2810, 1150) * mm});
            skLineSegment(sketch, "E621", {"start": v(810, 1150) * mm, "end": v(810, 3850) * mm});
            skLineSegment(sketch, "E622", {"start": v(810, 3850) * mm, "end": v(2710, 3850) * mm});
            skLineSegment(sketch, "E623", {"start": v(2710, 3850) * mm, "end": v(2710, 1150) * mm});
            skSolve(sketch);
        }
        {
            var Q0;
            Q0=qSketchRegion(id+"F72",true);
            var Q1;
            Q1=makeQuery(id+"F72.imprint","IMPRINT",FACE,{"disambiguationData":[TD([[makeQuery(id+"F72.imprint","IMPRINT",EDGE,{"derivedFrom":sQuery(id+"F72.wireOp",EDGE,"c3fbda2f-6199-4c6e-8e92-29b24fa35490.152")}),-1.0]])]});
            extrude(context, id + "F73", {"entities" : qUnion([Q0, Q1]), "depth" : 50 * mm, "offsetDistance" : 25 * mm});
        }
        {
            var Q0;
            Q0=makeQuery(id+"F73.opExtrude","CAP_FACE",FACE,{"disambiguationData":[OSD([sQuery(id+"F72.wireOp",EDGE,"E619.0.0"),sQuery(id+"F72.wireOp",EDGE,"E619.0.1"),sQuery(id+"F72.wireOp",EDGE,"E619.0.2"),sQuery(id+"F72.wireOp",EDGE,"E619.0.3"),sQuery(id+"F72.wireOp",EDGE,"E620.bottom"),sQuery(id+"F72.wireOp",EDGE,"E620.top"),sQuery(id+"F72.wireOp",EDGE,"E620.left"),sQuery(id+"F72.wireOp",EDGE,"E620.right")])],"isStart":false});
            var sketch = newSketch(context, id + "F74", { "sketchPlane" : qUnion([Q0])});
            skLineSegment(sketch, "E624.0", {"start": v(5230, 3350) * mm, "end": v(6630, 3350) * mm});
            skLineSegment(sketch, "E624.1", {"start": v(5230, 1050) * mm, "end": v(6630, 1050) * mm});
            skLineSegment(sketch, "E624.2", {"start": v(5230, 3350) * mm, "end": v(5230, 1050) * mm});
            skLineSegment(sketch, "E624.3", {"start": v(6630, 3350) * mm, "end": v(6630, 1050) * mm});
            skLineSegment(sketch, "E624.4", {"start": v(5330, 1050) * mm, "end": v(5330, 3250) * mm});
            skLineSegment(sketch, "E624.5", {"start": v(5330, 3250) * mm, "end": v(6530, 3250) * mm});
            skLineSegment(sketch, "E624.6", {"start": v(6530, 3250) * mm, "end": v(6530, 1050) * mm});
            skPoint(sketch, "E624.7", {"position": v(10690, 1100) * mm});
            skPoint(sketch, "E624.8", {"position": v(15160, 1100) * mm});
            skPoint(sketch, "E624.9", {"position": v(19360, 1100) * mm});
            skPoint(sketch, "E624.10", {"position": v(23730, 1100) * mm});
            skLineSegment(sketch, "E624.11", {"start": v(6480, 3200) * mm, "end": v(6480, 1100) * mm});
            skLineSegment(sketch, "E624.12", {"start": v(6480, 3200) * mm, "end": v(5380, 3200) * mm});
            skLineSegment(sketch, "E624.13", {"start": v(5380, 3200) * mm, "end": v(5380, 1100) * mm});
            skLineSegment(sketch, "E624.14", {"start": v(6480, 1100) * mm, "end": v(5380, 1100) * mm});
            skLineSegment(sketch, "E624.15", {"start": v(10860, 3350) * mm, "end": v(12260, 3350) * mm});
            skLineSegment(sketch, "E624.16", {"start": v(10860, 1050) * mm, "end": v(12260, 1050) * mm});
            skLineSegment(sketch, "E624.17", {"start": v(10860, 3350) * mm, "end": v(10860, 1050) * mm});
            skLineSegment(sketch, "E624.18", {"start": v(12260, 3350) * mm, "end": v(12260, 1050) * mm});
            skLineSegment(sketch, "E624.19", {"start": v(10960, 1050) * mm, "end": v(10960, 3250) * mm});
            skLineSegment(sketch, "E624.20", {"start": v(10960, 3250) * mm, "end": v(12160, 3250) * mm});
            skLineSegment(sketch, "E624.21", {"start": v(12160, 3250) * mm, "end": v(12160, 1050) * mm});
            skLineSegment(sketch, "E624.22", {"start": v(12110, 3200) * mm, "end": v(12110, 1100) * mm});
            skLineSegment(sketch, "E624.23", {"start": v(12110, 3200) * mm, "end": v(11010, 3200) * mm});
            skLineSegment(sketch, "E624.24", {"start": v(11010, 3200) * mm, "end": v(11010, 1100) * mm});
            skLineSegment(sketch, "E624.25", {"start": v(12110, 1100) * mm, "end": v(11010, 1100) * mm});
            skLineSegment(sketch, "E624.26", {"start": v(15210, 3350) * mm, "end": v(16610, 3350) * mm});
            skLineSegment(sketch, "E624.27", {"start": v(15210, 1050) * mm, "end": v(16610, 1050) * mm});
            skLineSegment(sketch, "E624.28", {"start": v(15210, 3350) * mm, "end": v(15210, 1050) * mm});
            skLineSegment(sketch, "E624.29", {"start": v(16610, 3350) * mm, "end": v(16610, 1050) * mm});
            skLineSegment(sketch, "E624.30", {"start": v(15310, 1050) * mm, "end": v(15310, 3250) * mm});
            skLineSegment(sketch, "E624.31", {"start": v(15310, 3250) * mm, "end": v(16510, 3250) * mm});
            skLineSegment(sketch, "E624.32", {"start": v(16510, 3250) * mm, "end": v(16510, 1050) * mm});
            skLineSegment(sketch, "E624.33", {"start": v(16460, 3200) * mm, "end": v(16460, 1100) * mm});
            skLineSegment(sketch, "E624.34", {"start": v(16460, 3200) * mm, "end": v(15360, 3200) * mm});
            skLineSegment(sketch, "E624.35", {"start": v(15360, 3200) * mm, "end": v(15360, 1100) * mm});
            skLineSegment(sketch, "E624.36", {"start": v(16460, 1100) * mm, "end": v(15360, 1100) * mm});
            skLineSegment(sketch, "E624.37", {"start": v(19310, 3350) * mm, "end": v(20710, 3350) * mm});
            skLineSegment(sketch, "E624.38", {"start": v(19310, 1050) * mm, "end": v(20710, 1050) * mm});
            skLineSegment(sketch, "E624.39", {"start": v(19310, 3350) * mm, "end": v(19310, 1050) * mm});
            skLineSegment(sketch, "E624.40", {"start": v(20710, 3350) * mm, "end": v(20710, 1050) * mm});
            skLineSegment(sketch, "E624.41", {"start": v(19410, 1050) * mm, "end": v(19410, 3250) * mm});
            skLineSegment(sketch, "E624.42", {"start": v(19410, 3250) * mm, "end": v(20610, 3250) * mm});
            skLineSegment(sketch, "E624.43", {"start": v(20610, 3250) * mm, "end": v(20610, 1050) * mm});
            skLineSegment(sketch, "E624.44", {"start": v(20560, 3200) * mm, "end": v(20560, 1100) * mm});
            skLineSegment(sketch, "E624.45", {"start": v(20560, 3200) * mm, "end": v(19460, 3200) * mm});
            skLineSegment(sketch, "E624.46", {"start": v(19460, 3200) * mm, "end": v(19460, 1100) * mm});
            skLineSegment(sketch, "E624.47", {"start": v(20560, 1100) * mm, "end": v(19460, 1100) * mm});
            skLineSegment(sketch, "E624.48", {"start": v(23580, 3350) * mm, "end": v(24980, 3350) * mm});
            skLineSegment(sketch, "E624.49", {"start": v(23580, 1050) * mm, "end": v(24980, 1050) * mm});
            skLineSegment(sketch, "E624.50", {"start": v(23580, 3350) * mm, "end": v(23580, 1050) * mm});
            skLineSegment(sketch, "E624.51", {"start": v(24980, 3350) * mm, "end": v(24980, 1050) * mm});
            skLineSegment(sketch, "E624.52", {"start": v(23680, 1050) * mm, "end": v(23680, 3250) * mm});
            skLineSegment(sketch, "E624.53", {"start": v(23680, 3250) * mm, "end": v(24880, 3250) * mm});
            skLineSegment(sketch, "E624.54", {"start": v(24880, 3250) * mm, "end": v(24880, 1050) * mm});
            skLineSegment(sketch, "E624.55", {"start": v(24830, 3200) * mm, "end": v(24830, 1100) * mm});
            skLineSegment(sketch, "E624.56", {"start": v(24830, 3200) * mm, "end": v(23730, 3200) * mm});
            skLineSegment(sketch, "E624.57", {"start": v(23730, 3200) * mm, "end": v(23730, 1100) * mm});
            skLineSegment(sketch, "E624.58", {"start": v(24830, 1100) * mm, "end": v(23730, 1100) * mm});
            skLineSegment(sketch, "E624.59", {"start": v(27160, 0) * mm, "end": v(28260, 0) * mm});
            skLineSegment(sketch, "E624.60", {"start": v(28260, 0) * mm, "end": v(28260, 2400) * mm});
            skLineSegment(sketch, "E624.61", {"start": v(28260, 2400) * mm, "end": v(27160, 2400) * mm});
            skLineSegment(sketch, "E624.62", {"start": v(27160, 2400) * mm, "end": v(27160, 0) * mm});
            skLineSegment(sketch, "E624.63", {"start": v(27010, 2550) * mm, "end": v(28410, 2550) * mm});
            skLineSegment(sketch, "E624.64", {"start": v(27010, 2550) * mm, "end": v(27010, -150) * mm});
            skLineSegment(sketch, "E624.65", {"start": v(28410, 2550) * mm, "end": v(28410, -150) * mm});
            skLineSegment(sketch, "E624.66", {"start": v(27110, -150) * mm, "end": v(27110, 2450) * mm});
            skLineSegment(sketch, "E624.67", {"start": v(27110, 2450) * mm, "end": v(28310, 2450) * mm});
            skLineSegment(sketch, "E624.68", {"start": v(28310, 2450) * mm, "end": v(28310, -150) * mm});
            skLineSegment(sketch, "E624.69", {"start": v(27010, -150) * mm, "end": v(28410, -150) * mm});
            skLineSegment(sketch, "E624.70", {"start": v(860, 1200) * mm, "end": v(2660, 1200) * mm});
            skLineSegment(sketch, "E624.71", {"start": v(2660, 1200) * mm, "end": v(2660, 3800) * mm});
            skLineSegment(sketch, "E624.72", {"start": v(2660, 3800) * mm, "end": v(860, 3800) * mm});
            skLineSegment(sketch, "E624.73", {"start": v(860, 3800) * mm, "end": v(860, 1200) * mm});
            skLineSegment(sketch, "E624.74", {"start": v(710, 3950) * mm, "end": v(2810, 3950) * mm});
            skLineSegment(sketch, "E624.75", {"start": v(710, 1150) * mm, "end": v(2810, 1150) * mm});
            skLineSegment(sketch, "E624.76", {"start": v(710, 3950) * mm, "end": v(710, 1150) * mm});
            skLineSegment(sketch, "E624.77", {"start": v(2810, 3950) * mm, "end": v(2810, 1150) * mm});
            skLineSegment(sketch, "E624.78", {"start": v(810, 1150) * mm, "end": v(810, 3850) * mm});
            skLineSegment(sketch, "E624.79", {"start": v(810, 3850) * mm, "end": v(2710, 3850) * mm});
            skLineSegment(sketch, "E624.80", {"start": v(2710, 3850) * mm, "end": v(2710, 1150) * mm});
            skSolve(sketch);
        }
        {
            var Q0;
            Q0=makeQuery(id+"F74.imprint","IMPRINT",FACE,{"disambiguationData":[TD([[makeQuery(id+"F74.imprint","IMPRINT",EDGE,{"derivedFrom":sQuery(id+"F74.wireOp",EDGE,"E624.74")}),-1.0]])]});
            var Q1;
            Q1=makeQuery(id+"F74.imprint","IMPRINT",FACE,{"disambiguationData":[TD([[makeQuery(id+"F74.imprint","IMPRINT",EDGE,{"derivedFrom":sQuery(id+"F74.wireOp",EDGE,"E624.0")}),-1.0]])]});
            var Q2;
            Q2=makeQuery(id+"F74.imprint","IMPRINT",FACE,{"disambiguationData":[TD([[makeQuery(id+"F74.imprint","IMPRINT",EDGE,{"derivedFrom":sQuery(id+"F74.wireOp",EDGE,"E624.15")}),-1.0]])]});
            var Q3;
            Q3=makeQuery(id+"F74.imprint","IMPRINT",FACE,{"disambiguationData":[TD([[makeQuery(id+"F74.imprint","IMPRINT",EDGE,{"derivedFrom":sQuery(id+"F74.wireOp",EDGE,"E624.26")}),-1.0]])]});
            var Q4;
            Q4=makeQuery(id+"F74.imprint","IMPRINT",FACE,{"disambiguationData":[TD([[makeQuery(id+"F74.imprint","IMPRINT",EDGE,{"derivedFrom":sQuery(id+"F74.wireOp",EDGE,"E624.37")}),-1.0]])]});
            var Q5;
            Q5=makeQuery(id+"F74.imprint","IMPRINT",FACE,{"disambiguationData":[TD([[makeQuery(id+"F74.imprint","IMPRINT",EDGE,{"derivedFrom":sQuery(id+"F74.wireOp",EDGE,"E624.48")}),-1.0]])]});
            var Q6;
            Q6=makeQuery(id+"F74.imprint","IMPRINT",FACE,{"disambiguationData":[TD([[makeQuery(id+"F74.imprint","IMPRINT",EDGE,{"derivedFrom":sQuery(id+"F74.wireOp",EDGE,"E624.63")}),-1.0]])]});
            extrude(context, id + "F75", {"entities" : qUnion([Q0, Q1, Q2, Q3, Q4, Q5, Q6]), "operationType" : NewBodyOperationType.ADD, "depth" : 50 * mm, "offsetDistance" : 25 * mm});
        }
        {
            var Q0;
            Q0=makeQuery(id+"F5.boolean.opBoolean","MERGE",FACE,{"derivedFrom":[makeQuery(id+"F3.boolean.opBoolean","COPY",FACE,{"derivedFrom":makeQuery(id+"F3.opExtrude","SWEPT_FACE",FACE,{"disambiguationData":[OSD([sQuery(id+"F2.wireOp",EDGE,"E19.10")])]})}),makeQuery(id+"F5.opExtrude","SWEPT_FACE",FACE,{"disambiguationData":[OSD([sQuery(id+"F4.wireOp",EDGE,"E33.0")])]})]});
            var sketch = newSketch(context, id + "F76", { "sketchPlane" : qUnion([Q0])});
            skPoint(sketch, "E625.26", {"position": v(-24350, 1100) * mm});
            skLineSegment(sketch, "E625.44", {"start": v(-24500, 3350) * mm, "end": v(-23200, 3350) * mm});
            skLineSegment(sketch, "E625.45", {"start": v(-24500, 1050) * mm, "end": v(-23200, 1050) * mm});
            skLineSegment(sketch, "E625.46", {"start": v(-24500, 3350) * mm, "end": v(-24500, 1050) * mm});
            skLineSegment(sketch, "E625.47", {"start": v(-23200, 3350) * mm, "end": v(-23200, 1050) * mm});
            skLineSegment(sketch, "E625.48", {"start": v(-24400, 1050) * mm, "end": v(-24400, 3250) * mm});
            skLineSegment(sketch, "E625.49", {"start": v(-24400, 3250) * mm, "end": v(-23300, 3250) * mm});
            skLineSegment(sketch, "E625.50", {"start": v(-23300, 3250) * mm, "end": v(-23300, 1050) * mm});
            skLineSegment(sketch, "E625.51", {"start": v(-23350, 3200) * mm, "end": v(-23350, 1100) * mm});
            skLineSegment(sketch, "E625.52", {"start": v(-23350, 3200) * mm, "end": v(-24350, 3200) * mm});
            skLineSegment(sketch, "E625.53", {"start": v(-24350, 3200) * mm, "end": v(-24350, 1100) * mm});
            skLineSegment(sketch, "E625.54", {"start": v(-23350, 1100) * mm, "end": v(-24350, 1100) * mm});
            skPoint(sketch, "E626", {"position": v(-21370, 1100) * mm});
            skPoint(sketch, "E627", {"position": v(-18360, 1100) * mm});
            skPoint(sketch, "E628", {"position": v(-15320, 1100) * mm});
            skPoint(sketch, "E629", {"position": v(-12330, 1100) * mm});
            skLineSegment(sketch, "E630.44", {"start": v(-21520, 3350) * mm, "end": v(-20220, 3350) * mm});
            skLineSegment(sketch, "E630.45", {"start": v(-21520, 1050) * mm, "end": v(-20220, 1050) * mm});
            skLineSegment(sketch, "E630.46", {"start": v(-21520, 3350) * mm, "end": v(-21520, 1050) * mm});
            skLineSegment(sketch, "E630.47", {"start": v(-20220, 3350) * mm, "end": v(-20220, 1050) * mm});
            skLineSegment(sketch, "E630.48", {"start": v(-21420, 1050) * mm, "end": v(-21420, 3250) * mm});
            skLineSegment(sketch, "E630.49", {"start": v(-21420, 3250) * mm, "end": v(-20320, 3250) * mm});
            skLineSegment(sketch, "E630.50", {"start": v(-20320, 3250) * mm, "end": v(-20320, 1050) * mm});
            skLineSegment(sketch, "E630.51", {"start": v(-20370, 3200) * mm, "end": v(-20370, 1100) * mm});
            skLineSegment(sketch, "E630.52", {"start": v(-20370, 3200) * mm, "end": v(-21370, 3200) * mm});
            skLineSegment(sketch, "E630.53", {"start": v(-21370, 3200) * mm, "end": v(-21370, 1100) * mm});
            skLineSegment(sketch, "E630.54", {"start": v(-20370, 1100) * mm, "end": v(-21370, 1100) * mm});
            skLineSegment(sketch, "E631.44", {"start": v(-18510, 3350) * mm, "end": v(-17210, 3350) * mm});
            skLineSegment(sketch, "E631.45", {"start": v(-18510, 1050) * mm, "end": v(-17210, 1050) * mm});
            skLineSegment(sketch, "E631.46", {"start": v(-18510, 3350) * mm, "end": v(-18510, 1050) * mm});
            skLineSegment(sketch, "E631.47", {"start": v(-17210, 3350) * mm, "end": v(-17210, 1050) * mm});
            skLineSegment(sketch, "E631.48", {"start": v(-18410, 1050) * mm, "end": v(-18410, 3250) * mm});
            skLineSegment(sketch, "E631.49", {"start": v(-18410, 3250) * mm, "end": v(-17310, 3250) * mm});
            skLineSegment(sketch, "E631.50", {"start": v(-17310, 3250) * mm, "end": v(-17310, 1050) * mm});
            skLineSegment(sketch, "E631.51", {"start": v(-17360, 3200) * mm, "end": v(-17360, 1100) * mm});
            skLineSegment(sketch, "E631.52", {"start": v(-17360, 3200) * mm, "end": v(-18360, 3200) * mm});
            skLineSegment(sketch, "E631.53", {"start": v(-18360, 3200) * mm, "end": v(-18360, 1100) * mm});
            skLineSegment(sketch, "E631.54", {"start": v(-17360, 1100) * mm, "end": v(-18360, 1100) * mm});
            skLineSegment(sketch, "E632.44", {"start": v(-15470, 3350) * mm, "end": v(-14170, 3350) * mm});
            skLineSegment(sketch, "E632.45", {"start": v(-15470, 1050) * mm, "end": v(-14170, 1050) * mm});
            skLineSegment(sketch, "E632.46", {"start": v(-15470, 3350) * mm, "end": v(-15470, 1050) * mm});
            skLineSegment(sketch, "E632.47", {"start": v(-14170, 3350) * mm, "end": v(-14170, 1050) * mm});
            skLineSegment(sketch, "E632.48", {"start": v(-15370, 1050) * mm, "end": v(-15370, 3250) * mm});
            skLineSegment(sketch, "E632.49", {"start": v(-15370, 3250) * mm, "end": v(-14270, 3250) * mm});
            skLineSegment(sketch, "E632.50", {"start": v(-14270, 3250) * mm, "end": v(-14270, 1050) * mm});
            skLineSegment(sketch, "E632.51", {"start": v(-14320, 3200) * mm, "end": v(-14320, 1100) * mm});
            skLineSegment(sketch, "E632.52", {"start": v(-14320, 3200) * mm, "end": v(-15320, 3200) * mm});
            skLineSegment(sketch, "E632.53", {"start": v(-15320, 3200) * mm, "end": v(-15320, 1100) * mm});
            skLineSegment(sketch, "E632.54", {"start": v(-14320, 1100) * mm, "end": v(-15320, 1100) * mm});
            skLineSegment(sketch, "E633.44", {"start": v(-12480, 3350) * mm, "end": v(-11180, 3350) * mm});
            skLineSegment(sketch, "E633.45", {"start": v(-12480, 1050) * mm, "end": v(-11180, 1050) * mm});
            skLineSegment(sketch, "E633.46", {"start": v(-12480, 3350) * mm, "end": v(-12480, 1050) * mm});
            skLineSegment(sketch, "E633.47", {"start": v(-11180, 3350) * mm, "end": v(-11180, 1050) * mm});
            skLineSegment(sketch, "E633.48", {"start": v(-12380, 1050) * mm, "end": v(-12380, 3250) * mm});
            skLineSegment(sketch, "E633.49", {"start": v(-12380, 3250) * mm, "end": v(-11280, 3250) * mm});
            skLineSegment(sketch, "E633.50", {"start": v(-11280, 3250) * mm, "end": v(-11280, 1050) * mm});
            skLineSegment(sketch, "E633.51", {"start": v(-11330, 3200) * mm, "end": v(-11330, 1100) * mm});
            skLineSegment(sketch, "E633.52", {"start": v(-11330, 3200) * mm, "end": v(-12330, 3200) * mm});
            skLineSegment(sketch, "E633.53", {"start": v(-12330, 3200) * mm, "end": v(-12330, 1100) * mm});
            skLineSegment(sketch, "E633.54", {"start": v(-11330, 1100) * mm, "end": v(-12330, 1100) * mm});
            skSolve(sketch);
        }
        {
            var Q0;
            Q0=qSketchRegion(id+"F76",true);
            extrude(context, id + "F77", {"entities" : qUnion([Q0]), "depth" : 50 * mm, "offsetDistance" : 25 * mm});
        }
        {
            var Q0;
            Q0=makeQuery(id+"F77.opExtrude","CAP_FACE",FACE,{"disambiguationData":[OSD([sQuery(id+"F76.wireOp",EDGE,"E625.44"),sQuery(id+"F76.wireOp",EDGE,"E625.45"),sQuery(id+"F76.wireOp",EDGE,"E625.46"),sQuery(id+"F76.wireOp",EDGE,"E625.47"),sQuery(id+"F76.wireOp",EDGE,"E625.51"),sQuery(id+"F76.wireOp",EDGE,"E625.52"),sQuery(id+"F76.wireOp",EDGE,"E625.53"),sQuery(id+"F76.wireOp",EDGE,"E625.54")])],"isStart":false});
            var sketch = newSketch(context, id + "F78", { "sketchPlane" : qUnion([Q0])});
            skPoint(sketch, "E634.0", {"position": v(-24350, 1100) * mm});
            skLineSegment(sketch, "E634.1", {"start": v(-24500, 3350) * mm, "end": v(-23200, 3350) * mm});
            skLineSegment(sketch, "E634.2", {"start": v(-24500, 1050) * mm, "end": v(-23200, 1050) * mm});
            skLineSegment(sketch, "E634.3", {"start": v(-24500, 3350) * mm, "end": v(-24500, 1050) * mm});
            skLineSegment(sketch, "E634.4", {"start": v(-23200, 3350) * mm, "end": v(-23200, 1050) * mm});
            skLineSegment(sketch, "E634.5", {"start": v(-24400, 1050) * mm, "end": v(-24400, 3250) * mm});
            skLineSegment(sketch, "E634.6", {"start": v(-24400, 3250) * mm, "end": v(-23300, 3250) * mm});
            skLineSegment(sketch, "E634.7", {"start": v(-23300, 3250) * mm, "end": v(-23300, 1050) * mm});
            skLineSegment(sketch, "E634.8", {"start": v(-23350, 3200) * mm, "end": v(-23350, 1100) * mm});
            skLineSegment(sketch, "E634.9", {"start": v(-23350, 3200) * mm, "end": v(-24350, 3200) * mm});
            skLineSegment(sketch, "E634.10", {"start": v(-24350, 3200) * mm, "end": v(-24350, 1100) * mm});
            skLineSegment(sketch, "E634.11", {"start": v(-23350, 1100) * mm, "end": v(-24350, 1100) * mm});
            skPoint(sketch, "E634.12", {"position": v(-21370, 1100) * mm});
            skPoint(sketch, "E634.13", {"position": v(-18360, 1100) * mm});
            skPoint(sketch, "E634.14", {"position": v(-15320, 1100) * mm});
            skPoint(sketch, "E634.15", {"position": v(-12330, 1100) * mm});
            skLineSegment(sketch, "E634.16", {"start": v(-21520, 3350) * mm, "end": v(-20220, 3350) * mm});
            skLineSegment(sketch, "E634.17", {"start": v(-21520, 1050) * mm, "end": v(-20220, 1050) * mm});
            skLineSegment(sketch, "E634.18", {"start": v(-21520, 3350) * mm, "end": v(-21520, 1050) * mm});
            skLineSegment(sketch, "E634.19", {"start": v(-20220, 3350) * mm, "end": v(-20220, 1050) * mm});
            skLineSegment(sketch, "E634.20", {"start": v(-21420, 1050) * mm, "end": v(-21420, 3250) * mm});
            skLineSegment(sketch, "E634.21", {"start": v(-21420, 3250) * mm, "end": v(-20320, 3250) * mm});
            skLineSegment(sketch, "E634.22", {"start": v(-20320, 3250) * mm, "end": v(-20320, 1050) * mm});
            skLineSegment(sketch, "E634.23", {"start": v(-20370, 3200) * mm, "end": v(-20370, 1100) * mm});
            skLineSegment(sketch, "E634.24", {"start": v(-20370, 3200) * mm, "end": v(-21370, 3200) * mm});
            skLineSegment(sketch, "E634.25", {"start": v(-21370, 3200) * mm, "end": v(-21370, 1100) * mm});
            skLineSegment(sketch, "E634.26", {"start": v(-20370, 1100) * mm, "end": v(-21370, 1100) * mm});
            skLineSegment(sketch, "E634.27", {"start": v(-18510, 3350) * mm, "end": v(-17210, 3350) * mm});
            skLineSegment(sketch, "E634.28", {"start": v(-18510, 1050) * mm, "end": v(-17210, 1050) * mm});
            skLineSegment(sketch, "E634.29", {"start": v(-18510, 3350) * mm, "end": v(-18510, 1050) * mm});
            skLineSegment(sketch, "E634.30", {"start": v(-17210, 3350) * mm, "end": v(-17210, 1050) * mm});
            skLineSegment(sketch, "E634.31", {"start": v(-18410, 1050) * mm, "end": v(-18410, 3250) * mm});
            skLineSegment(sketch, "E634.32", {"start": v(-18410, 3250) * mm, "end": v(-17310, 3250) * mm});
            skLineSegment(sketch, "E634.33", {"start": v(-17310, 3250) * mm, "end": v(-17310, 1050) * mm});
            skLineSegment(sketch, "E634.34", {"start": v(-17360, 3200) * mm, "end": v(-17360, 1100) * mm});
            skLineSegment(sketch, "E634.35", {"start": v(-17360, 3200) * mm, "end": v(-18360, 3200) * mm});
            skLineSegment(sketch, "E634.36", {"start": v(-18360, 3200) * mm, "end": v(-18360, 1100) * mm});
            skLineSegment(sketch, "E634.37", {"start": v(-17360, 1100) * mm, "end": v(-18360, 1100) * mm});
            skLineSegment(sketch, "E634.38", {"start": v(-15470, 3350) * mm, "end": v(-14170, 3350) * mm});
            skLineSegment(sketch, "E634.39", {"start": v(-15470, 1050) * mm, "end": v(-14170, 1050) * mm});
            skLineSegment(sketch, "E634.40", {"start": v(-15470, 3350) * mm, "end": v(-15470, 1050) * mm});
            skLineSegment(sketch, "E634.41", {"start": v(-14170, 3350) * mm, "end": v(-14170, 1050) * mm});
            skLineSegment(sketch, "E634.42", {"start": v(-15370, 1050) * mm, "end": v(-15370, 3250) * mm});
            skLineSegment(sketch, "E634.43", {"start": v(-15370, 3250) * mm, "end": v(-14270, 3250) * mm});
            skLineSegment(sketch, "E634.44", {"start": v(-14270, 3250) * mm, "end": v(-14270, 1050) * mm});
            skLineSegment(sketch, "E634.45", {"start": v(-14320, 3200) * mm, "end": v(-14320, 1100) * mm});
            skLineSegment(sketch, "E634.46", {"start": v(-14320, 3200) * mm, "end": v(-15320, 3200) * mm});
            skLineSegment(sketch, "E634.47", {"start": v(-15320, 3200) * mm, "end": v(-15320, 1100) * mm});
            skLineSegment(sketch, "E634.48", {"start": v(-14320, 1100) * mm, "end": v(-15320, 1100) * mm});
            skLineSegment(sketch, "E634.49", {"start": v(-12480, 3350) * mm, "end": v(-11180, 3350) * mm});
            skLineSegment(sketch, "E634.50", {"start": v(-12480, 1050) * mm, "end": v(-11180, 1050) * mm});
            skLineSegment(sketch, "E634.51", {"start": v(-12480, 3350) * mm, "end": v(-12480, 1050) * mm});
            skLineSegment(sketch, "E634.52", {"start": v(-11180, 3350) * mm, "end": v(-11180, 1050) * mm});
            skLineSegment(sketch, "E634.53", {"start": v(-12380, 1050) * mm, "end": v(-12380, 3250) * mm});
            skLineSegment(sketch, "E634.54", {"start": v(-12380, 3250) * mm, "end": v(-11280, 3250) * mm});
            skLineSegment(sketch, "E634.55", {"start": v(-11280, 3250) * mm, "end": v(-11280, 1050) * mm});
            skLineSegment(sketch, "E634.56", {"start": v(-11330, 3200) * mm, "end": v(-11330, 1100) * mm});
            skLineSegment(sketch, "E634.57", {"start": v(-11330, 3200) * mm, "end": v(-12330, 3200) * mm});
            skLineSegment(sketch, "E634.58", {"start": v(-12330, 3200) * mm, "end": v(-12330, 1100) * mm});
            skLineSegment(sketch, "E634.59", {"start": v(-11330, 1100) * mm, "end": v(-12330, 1100) * mm});
            skSolve(sketch);
        }
        {
            var Q0;
            Q0=makeQuery(id+"F78.imprint","IMPRINT",FACE,{"disambiguationData":[TD([[makeQuery(id+"F78.imprint","IMPRINT",EDGE,{"derivedFrom":sQuery(id+"F78.wireOp",EDGE,"E634.1")}),-1.0]])]});
            var Q1;
            Q1=makeQuery(id+"F78.imprint","IMPRINT",FACE,{"disambiguationData":[TD([[makeQuery(id+"F78.imprint","IMPRINT",EDGE,{"derivedFrom":sQuery(id+"F78.wireOp",EDGE,"E634.16")}),-1.0]])]});
            var Q2;
            Q2=makeQuery(id+"F78.imprint","IMPRINT",FACE,{"disambiguationData":[TD([[makeQuery(id+"F78.imprint","IMPRINT",EDGE,{"derivedFrom":sQuery(id+"F78.wireOp",EDGE,"E634.27")}),-1.0]])]});
            var Q3;
            Q3=makeQuery(id+"F78.imprint","IMPRINT",FACE,{"disambiguationData":[TD([[makeQuery(id+"F78.imprint","IMPRINT",EDGE,{"derivedFrom":sQuery(id+"F78.wireOp",EDGE,"E634.38")}),-1.0]])]});
            var Q4;
            Q4=makeQuery(id+"F78.imprint","IMPRINT",FACE,{"disambiguationData":[TD([[makeQuery(id+"F78.imprint","IMPRINT",EDGE,{"derivedFrom":sQuery(id+"F78.wireOp",EDGE,"E634.49")}),-1.0]])]});
            extrude(context, id + "F79", {"entities" : qUnion([Q0, Q1, Q2, Q3, Q4]), "operationType" : NewBodyOperationType.ADD, "depth" : 25 * mm, "offsetDistance" : 25 * mm});
        }
        {
            var Q0;
            Q0=makeQuery(id+"F5.boolean.opBoolean","MERGE",FACE,{"derivedFrom":[makeQuery(id+"F3.boolean.opBoolean","COPY",FACE,{"derivedFrom":makeQuery(id+"F3.opExtrude","SWEPT_FACE",FACE,{"disambiguationData":[OSD([sQuery(id+"F2.wireOp",EDGE,"E19.11")])]})}),makeQuery(id+"F5.opExtrude","SWEPT_FACE",FACE,{"disambiguationData":[OSD([sQuery(id+"F4.wireOp",EDGE,"E32.0")])]})]});
            var sketch = newSketch(context, id + "F80", { "sketchPlane" : qUnion([Q0])});
            skPoint(sketch, "E635", {"position": v(-25660, 1100) * mm});
            skPoint(sketch, "E636", {"position": v(-22100, 1100) * mm});
            skLineSegment(sketch, "E637.66", {"start": v(-24510, 3350) * mm, "end": v(-25810, 3350) * mm});
            skLineSegment(sketch, "E637.67", {"start": v(-24510, 1050) * mm, "end": v(-25810, 1050) * mm});
            skLineSegment(sketch, "E637.68", {"start": v(-24510, 3350) * mm, "end": v(-24510, 1050) * mm});
            skLineSegment(sketch, "E637.69", {"start": v(-25810, 3350) * mm, "end": v(-25810, 1050) * mm});
            skLineSegment(sketch, "E637.70", {"start": v(-24610, 1050) * mm, "end": v(-24610, 3250) * mm});
            skLineSegment(sketch, "E637.71", {"start": v(-24610, 3250) * mm, "end": v(-25710, 3250) * mm});
            skLineSegment(sketch, "E637.72", {"start": v(-25710, 3250) * mm, "end": v(-25710, 1050) * mm});
            skLineSegment(sketch, "E637.73", {"start": v(-25660, 3200) * mm, "end": v(-25660, 1100) * mm});
            skLineSegment(sketch, "E637.75", {"start": v(-24660, 3200) * mm, "end": v(-24660, 1100) * mm});
            skLineSegment(sketch, "E637.76", {"start": v(-25660, 1100) * mm, "end": v(-24660, 1100) * mm});
            skLineSegment(sketch, "E637.77", {"start": v(-27260, 0) * mm, "end": v(-28360, 0) * mm});
            skLineSegment(sketch, "E637.78", {"start": v(-28360, 0) * mm, "end": v(-28360, 2300) * mm});
            skLineSegment(sketch, "E637.79", {"start": v(-28360, 2300) * mm, "end": v(-27260, 2300) * mm});
            skLineSegment(sketch, "E637.80", {"start": v(-27260, 2300) * mm, "end": v(-27260, 0) * mm});
            skLineSegment(sketch, "E637.81", {"start": v(-27110, 2450) * mm, "end": v(-28510, 2450) * mm});
            skLineSegment(sketch, "E637.82", {"start": v(-27110, 2450) * mm, "end": v(-27110, -150) * mm});
            skLineSegment(sketch, "E637.83", {"start": v(-28510, 2450) * mm, "end": v(-28510, -150) * mm});
            skLineSegment(sketch, "E637.84", {"start": v(-27210, -150) * mm, "end": v(-27210, 2350) * mm});
            skLineSegment(sketch, "E637.85", {"start": v(-27210, 2350) * mm, "end": v(-28410, 2350) * mm});
            skLineSegment(sketch, "E637.86", {"start": v(-28410, 2350) * mm, "end": v(-28410, -150) * mm});
            skLineSegment(sketch, "E637.87", {"start": v(-27110, -150) * mm, "end": v(-28510, -150) * mm});
            skPoint(sketch, "E638", {"position": v(-28360, 0) * mm});
            skLineSegment(sketch, "E639.66", {"start": v(-20950, 3350) * mm, "end": v(-22250, 3350) * mm});
            skLineSegment(sketch, "E639.67", {"start": v(-20950, 1050) * mm, "end": v(-22250, 1050) * mm});
            skLineSegment(sketch, "E639.68", {"start": v(-20950, 3350) * mm, "end": v(-20950, 1050) * mm});
            skLineSegment(sketch, "E639.69", {"start": v(-22250, 3350) * mm, "end": v(-22250, 1050) * mm});
            skLineSegment(sketch, "E639.70", {"start": v(-21050, 1050) * mm, "end": v(-21050, 3250) * mm});
            skLineSegment(sketch, "E639.71", {"start": v(-21050, 3250) * mm, "end": v(-22150, 3250) * mm});
            skLineSegment(sketch, "E639.72", {"start": v(-22150, 3250) * mm, "end": v(-22150, 1050) * mm});
            skLineSegment(sketch, "E639.73", {"start": v(-22100, 3200) * mm, "end": v(-22100, 1100) * mm});
            skLineSegment(sketch, "E639.75", {"start": v(-21100, 3200) * mm, "end": v(-21100, 1100) * mm});
            skLineSegment(sketch, "E639.76", {"start": v(-22100, 1100) * mm, "end": v(-21100, 1100) * mm});
            skPoint(sketch, "E640", {"position": v(-4770, 1200) * mm});
            skLineSegment(sketch, "E641.0", {"start": v(-3070, 3800) * mm, "end": v(-3070, 1200) * mm});
            skLineSegment(sketch, "E641.1", {"start": v(-4770, 3800) * mm, "end": v(-3070, 3800) * mm});
            skLineSegment(sketch, "E641.2", {"start": v(-4770, 3800) * mm, "end": v(-4770, 1200) * mm});
            skLineSegment(sketch, "E641.4", {"start": v(-4820, 3850) * mm, "end": v(-4820, 1150) * mm});
            skLineSegment(sketch, "E641.5", {"start": v(-3020, 3850) * mm, "end": v(-4820, 3850) * mm});
            skLineSegment(sketch, "E641.6", {"start": v(-2920, 1150) * mm, "end": v(-2920, 3950) * mm});
            skLineSegment(sketch, "E641.7", {"start": v(-2920, 1150) * mm, "end": v(-4920, 1150) * mm});
            skLineSegment(sketch, "E641.10", {"start": v(-4770, 1200) * mm, "end": v(-3070, 1200) * mm});
            skLineSegment(sketch, "E641.11", {"start": v(-3020, 1150) * mm, "end": v(-3020, 3850) * mm});
            skLineSegment(sketch, "E641.12", {"start": v(-2920, 3950) * mm, "end": v(-2920, 1250) * mm});
            skLineSegment(sketch, "E641.13", {"start": v(-4920, 3950) * mm, "end": v(-4920, 1150) * mm});
            skLineSegment(sketch, "E641.14", {"start": v(-2920, 3950) * mm, "end": v(-4920, 3950) * mm});
            skPoint(sketch, "E642", {"position": v(-18660, 1100) * mm});
            skPoint(sketch, "E643", {"position": v(-15860, 1100) * mm});
            skPoint(sketch, "E644", {"position": v(-13060, 1100) * mm});
            skLineSegment(sketch, "E645.0", {"start": v(-14010, 3950) * mm, "end": v(-16010, 3950) * mm});
            skLineSegment(sketch, "E646.0", {"start": v(-16010, 3950) * mm, "end": v(-16010, 1050) * mm});
            skLineSegment(sketch, "E647.0", {"start": v(-14010, 3950) * mm, "end": v(-14010, 1050) * mm});
            skLineSegment(sketch, "E648.0", {"start": v(-14010, 1050) * mm, "end": v(-16010, 1050) * mm});
            skLineSegment(sketch, "E649.0", {"start": v(-15860, 1100) * mm, "end": v(-14160, 1100) * mm});
            skLineSegment(sketch, "E650.0", {"start": v(-14160, 3800) * mm, "end": v(-14160, 1100) * mm});
            skLineSegment(sketch, "E651.0", {"start": v(-15860, 3800) * mm, "end": v(-14160, 3800) * mm});
            skLineSegment(sketch, "E652.0", {"start": v(-15860, 3800) * mm, "end": v(-15860, 1100) * mm});
            skLineSegment(sketch, "E653.0", {"start": v(-15910, 3850) * mm, "end": v(-15910, 1050) * mm});
            skLineSegment(sketch, "E654.0", {"start": v(-14110, 3850) * mm, "end": v(-15910, 3850) * mm});
            skLineSegment(sketch, "E655.0", {"start": v(-14110, 1050) * mm, "end": v(-14110, 3850) * mm});
            skLineSegment(sketch, "E656.0", {"start": v(-16810, 3950) * mm, "end": v(-18810, 3950) * mm});
            skLineSegment(sketch, "E657.0", {"start": v(-18810, 3950) * mm, "end": v(-18810, 1050) * mm});
            skLineSegment(sketch, "E658.0", {"start": v(-16810, 3950) * mm, "end": v(-16810, 1050) * mm});
            skLineSegment(sketch, "E659.0", {"start": v(-16810, 1050) * mm, "end": v(-18810, 1050) * mm});
            skLineSegment(sketch, "E660.0", {"start": v(-18660, 1100) * mm, "end": v(-16960, 1100) * mm});
            skLineSegment(sketch, "E661.0", {"start": v(-16960, 3800) * mm, "end": v(-16960, 1100) * mm});
            skLineSegment(sketch, "E662.0", {"start": v(-18660, 3800) * mm, "end": v(-16960, 3800) * mm});
            skLineSegment(sketch, "E663.0", {"start": v(-18660, 3800) * mm, "end": v(-18660, 1100) * mm});
            skLineSegment(sketch, "E664.0", {"start": v(-18710, 3850) * mm, "end": v(-18710, 1050) * mm});
            skLineSegment(sketch, "E665.0", {"start": v(-16910, 3850) * mm, "end": v(-18710, 3850) * mm});
            skLineSegment(sketch, "E666.0", {"start": v(-16910, 1050) * mm, "end": v(-16910, 3850) * mm});
            skLineSegment(sketch, "E667.0", {"start": v(-11210, 3950) * mm, "end": v(-13210, 3950) * mm});
            skLineSegment(sketch, "E668.0", {"start": v(-13210, 3950) * mm, "end": v(-13210, 1050) * mm});
            skLineSegment(sketch, "E669.0", {"start": v(-11210, 3950) * mm, "end": v(-11210, 1050) * mm});
            skLineSegment(sketch, "E670.0", {"start": v(-11210, 1050) * mm, "end": v(-13210, 1050) * mm});
            skLineSegment(sketch, "E671.0", {"start": v(-13060, 1100) * mm, "end": v(-11360, 1100) * mm});
            skLineSegment(sketch, "E672.0", {"start": v(-11360, 3800) * mm, "end": v(-11360, 1100) * mm});
            skLineSegment(sketch, "E673.0", {"start": v(-13060, 3800) * mm, "end": v(-11360, 3800) * mm});
            skLineSegment(sketch, "E674.0", {"start": v(-13060, 3800) * mm, "end": v(-13060, 1100) * mm});
            skLineSegment(sketch, "E675.0", {"start": v(-13110, 3850) * mm, "end": v(-13110, 1050) * mm});
            skLineSegment(sketch, "E676.0", {"start": v(-11310, 3850) * mm, "end": v(-13110, 3850) * mm});
            skLineSegment(sketch, "E677.0", {"start": v(-11310, 1050) * mm, "end": v(-11310, 3850) * mm});
            skSolve(sketch);
        }
        {
            var Q0;
            Q0=makeQuery(id+"F80.imprint","IMPRINT",FACE,{"disambiguationData":[TD([[makeQuery(id+"F80.imprint","IMPRINT",EDGE,{"derivedFrom":sQuery(id+"F80.wireOp",EDGE,"E637.81")}),1.0]])]});
            var Q1;
            Q1=makeQuery(id+"F80.imprint","IMPRINT",FACE,{"disambiguationData":[TD([[makeQuery(id+"F80.imprint","IMPRINT",EDGE,{"derivedFrom":sQuery(id+"F80.wireOp",EDGE,"E637.77")}),-1.0]])]});
            var Q2;
            Q2=makeQuery(id+"F80.imprint","IMPRINT",FACE,{"disambiguationData":[TD([[makeQuery(id+"F80.imprint","IMPRINT",EDGE,{"derivedFrom":sQuery(id+"F80.wireOp",EDGE,"E637.66")}),1.0]])]});
            var Q3;
            {var subQ1=sQuery(id+"F80.wireOp",EDGE,"E637.70");Q3=makeQuery(id+"F80.imprint","IMPRINT",FACE,{"disambiguationData":[TD([[makeQuery(id+"F80.imprint","IMPRINT",EDGE,{"derivedFrom":subQ1}),1.0]])]});}
            var Q4;
            Q4=makeQuery(id+"F80.imprint","IMPRINT",FACE,{"disambiguationData":[TD([[makeQuery(id+"F80.imprint","IMPRINT",EDGE,{"derivedFrom":sQuery(id+"F80.wireOp",EDGE,"E639.66")}),1.0]])]});
            var Q5;
            {var subQ1=sQuery(id+"F80.wireOp",EDGE,"E639.70");Q5=makeQuery(id+"F80.imprint","IMPRINT",FACE,{"disambiguationData":[TD([[makeQuery(id+"F80.imprint","IMPRINT",EDGE,{"derivedFrom":subQ1}),1.0]])]});}
            var Q6;
            Q6=makeQuery(id+"F80.imprint","IMPRINT",FACE,{"disambiguationData":[TD([[makeQuery(id+"F80.imprint","IMPRINT",EDGE,{"derivedFrom":sQuery(id+"F80.wireOp",EDGE,"E641.0")}),1.0]])]});
            var Q7;
            {var subQ3=sQuery(id+"F80.wireOp",EDGE,"E641.4");Q7=makeQuery(id+"F80.imprint","IMPRINT",FACE,{"disambiguationData":[TD([[makeQuery(id+"F80.imprint","IMPRINT",EDGE,{"derivedFrom":subQ3}),-1.0]])]});}
            var Q8;
            Q8=makeQuery(id+"F80.imprint","IMPRINT",FACE,{"disambiguationData":[TD([[makeQuery(id+"F80.imprint","IMPRINT",EDGE,{"derivedFrom":sQuery(id+"F80.wireOp",EDGE,"E656.0")}),1.0]])]});
            var Q9;
            {var subQ3=sQuery(id+"F80.wireOp",EDGE,"E663.0");Q9=makeQuery(id+"F80.imprint","IMPRINT",FACE,{"disambiguationData":[TD([[makeQuery(id+"F80.imprint","IMPRINT",EDGE,{"derivedFrom":subQ3}),-1.0]])]});}
            var Q10;
            Q10=makeQuery(id+"F80.imprint","IMPRINT",FACE,{"disambiguationData":[TD([[makeQuery(id+"F80.imprint","IMPRINT",EDGE,{"derivedFrom":sQuery(id+"F80.wireOp",EDGE,"E645.0")}),1.0]])]});
            var Q11;
            {var subQ8=sQuery(id+"F80.wireOp",EDGE,"E652.0");Q11=makeQuery(id+"F80.imprint","IMPRINT",FACE,{"disambiguationData":[TD([[makeQuery(id+"F80.imprint","IMPRINT",EDGE,{"derivedFrom":subQ8}),-1.0]])]});}
            var Q12;
            Q12=makeQuery(id+"F80.imprint","IMPRINT",FACE,{"disambiguationData":[TD([[makeQuery(id+"F80.imprint","IMPRINT",EDGE,{"derivedFrom":sQuery(id+"F80.wireOp",EDGE,"E667.0")}),1.0]])]});
            var Q13;
            {var subQ2=sQuery(id+"F80.wireOp",EDGE,"E674.0");Q13=makeQuery(id+"F80.imprint","IMPRINT",FACE,{"disambiguationData":[TD([[makeQuery(id+"F80.imprint","IMPRINT",EDGE,{"derivedFrom":subQ2}),-1.0]])]});}
            extrude(context, id + "F81", {"entities" : qUnion([Q0, Q1, Q2, Q3, Q4, Q5, Q6, Q7, Q8, Q9, Q10, Q11, Q12, Q13]), "depth" : 25 * mm, "offsetDistance" : 25 * mm});
        }
        {
            var Q0;
            Q0=makeQuery(id+"F81.opExtrude","CAP_FACE",FACE,{"disambiguationData":[OSD([sQuery(id+"F80.wireOp",EDGE,"E637.77"),sQuery(id+"F80.wireOp",EDGE,"E637.78"),sQuery(id+"F80.wireOp",EDGE,"E637.79"),sQuery(id+"F80.wireOp",EDGE,"E637.80"),sQuery(id+"F80.wireOp",EDGE,"E637.81"),sQuery(id+"F80.wireOp",EDGE,"E637.82"),sQuery(id+"F80.wireOp",EDGE,"E637.83"),sQuery(id+"F80.wireOp",EDGE,"E637.87")])],"isStart":false});
            var sketch = newSketch(context, id + "F82", { "sketchPlane" : qUnion([Q0])});
            skPoint(sketch, "E678.0", {"position": v(-25660, 1100) * mm});
            skPoint(sketch, "E678.1", {"position": v(-22100, 1100) * mm});
            skLineSegment(sketch, "E678.2", {"start": v(-24510, 3350) * mm, "end": v(-25810, 3350) * mm});
            skLineSegment(sketch, "E678.3", {"start": v(-24510, 1050) * mm, "end": v(-25810, 1050) * mm});
            skLineSegment(sketch, "E678.4", {"start": v(-24510, 3350) * mm, "end": v(-24510, 1050) * mm});
            skLineSegment(sketch, "E678.5", {"start": v(-25810, 3350) * mm, "end": v(-25810, 1050) * mm});
            skLineSegment(sketch, "E678.6", {"start": v(-24610, 1050) * mm, "end": v(-24610, 3250) * mm});
            skLineSegment(sketch, "E678.7", {"start": v(-24610, 3250) * mm, "end": v(-25710, 3250) * mm});
            skLineSegment(sketch, "E678.8", {"start": v(-25710, 3250) * mm, "end": v(-25710, 1050) * mm});
            skLineSegment(sketch, "E678.9", {"start": v(-25660, 3200) * mm, "end": v(-25660, 1100) * mm});
            skLineSegment(sketch, "E678.10", {"start": v(-24660, 3200) * mm, "end": v(-24660, 1100) * mm});
            skLineSegment(sketch, "E678.11", {"start": v(-25660, 1100) * mm, "end": v(-24660, 1100) * mm});
            skLineSegment(sketch, "E678.12", {"start": v(-27260, 0) * mm, "end": v(-28360, 0) * mm});
            skLineSegment(sketch, "E678.13", {"start": v(-28360, 0) * mm, "end": v(-28360, 2300) * mm});
            skLineSegment(sketch, "E678.14", {"start": v(-28360, 2300) * mm, "end": v(-27260, 2300) * mm});
            skLineSegment(sketch, "E678.15", {"start": v(-27260, 2300) * mm, "end": v(-27260, 0) * mm});
            skLineSegment(sketch, "E678.16", {"start": v(-27110, 2450) * mm, "end": v(-28510, 2450) * mm});
            skLineSegment(sketch, "E678.17", {"start": v(-27110, 2450) * mm, "end": v(-27110, -150) * mm});
            skLineSegment(sketch, "E678.18", {"start": v(-28510, 2450) * mm, "end": v(-28510, -150) * mm});
            skLineSegment(sketch, "E678.19", {"start": v(-27210, -150) * mm, "end": v(-27210, 2350) * mm});
            skLineSegment(sketch, "E678.20", {"start": v(-27210, 2350) * mm, "end": v(-28410, 2350) * mm});
            skLineSegment(sketch, "E678.21", {"start": v(-28410, 2350) * mm, "end": v(-28410, -150) * mm});
            skLineSegment(sketch, "E678.22", {"start": v(-27110, -150) * mm, "end": v(-28510, -150) * mm});
            skPoint(sketch, "E678.23", {"position": v(-28360, 0) * mm});
            skLineSegment(sketch, "E678.24", {"start": v(-20950, 3350) * mm, "end": v(-22250, 3350) * mm});
            skLineSegment(sketch, "E678.25", {"start": v(-20950, 1050) * mm, "end": v(-22250, 1050) * mm});
            skLineSegment(sketch, "E678.26", {"start": v(-20950, 3350) * mm, "end": v(-20950, 1050) * mm});
            skLineSegment(sketch, "E678.27", {"start": v(-22250, 3350) * mm, "end": v(-22250, 1050) * mm});
            skLineSegment(sketch, "E678.28", {"start": v(-21050, 1050) * mm, "end": v(-21050, 3250) * mm});
            skLineSegment(sketch, "E678.29", {"start": v(-21050, 3250) * mm, "end": v(-22150, 3250) * mm});
            skLineSegment(sketch, "E678.30", {"start": v(-22150, 3250) * mm, "end": v(-22150, 1050) * mm});
            skLineSegment(sketch, "E678.31", {"start": v(-22100, 3200) * mm, "end": v(-22100, 1100) * mm});
            skLineSegment(sketch, "E678.32", {"start": v(-21100, 3200) * mm, "end": v(-21100, 1100) * mm});
            skLineSegment(sketch, "E678.33", {"start": v(-22100, 1100) * mm, "end": v(-21100, 1100) * mm});
            skPoint(sketch, "E678.34", {"position": v(-4770, 1200) * mm});
            skLineSegment(sketch, "E678.35", {"start": v(-3070, 3800) * mm, "end": v(-3070, 1200) * mm});
            skLineSegment(sketch, "E678.36", {"start": v(-4770, 3800) * mm, "end": v(-3070, 3800) * mm});
            skLineSegment(sketch, "E678.37", {"start": v(-4770, 3800) * mm, "end": v(-4770, 1200) * mm});
            skLineSegment(sketch, "E678.38", {"start": v(-4820, 3850) * mm, "end": v(-4820, 1150) * mm});
            skLineSegment(sketch, "E678.39", {"start": v(-3020, 3850) * mm, "end": v(-4820, 3850) * mm});
            skLineSegment(sketch, "E678.40", {"start": v(-2920, 1150) * mm, "end": v(-2920, 3950) * mm});
            skLineSegment(sketch, "E678.41", {"start": v(-2920, 1150) * mm, "end": v(-4920, 1150) * mm});
            skLineSegment(sketch, "E678.42", {"start": v(-4770, 1200) * mm, "end": v(-3070, 1200) * mm});
            skLineSegment(sketch, "E678.43", {"start": v(-3020, 1150) * mm, "end": v(-3020, 3850) * mm});
            skLineSegment(sketch, "E678.44", {"start": v(-2920, 3950) * mm, "end": v(-2920, 1250) * mm});
            skLineSegment(sketch, "E678.45", {"start": v(-4920, 3950) * mm, "end": v(-4920, 1150) * mm});
            skLineSegment(sketch, "E678.46", {"start": v(-2920, 3950) * mm, "end": v(-4920, 3950) * mm});
            skPoint(sketch, "E678.47", {"position": v(-18660, 1100) * mm});
            skPoint(sketch, "E678.48", {"position": v(-15860, 1100) * mm});
            skPoint(sketch, "E678.49", {"position": v(-13060, 1100) * mm});
            skLineSegment(sketch, "E678.50", {"start": v(-14010, 3950) * mm, "end": v(-16010, 3950) * mm});
            skLineSegment(sketch, "E678.51", {"start": v(-16010, 3950) * mm, "end": v(-16010, 1050) * mm});
            skLineSegment(sketch, "E678.52", {"start": v(-14010, 3950) * mm, "end": v(-14010, 1050) * mm});
            skLineSegment(sketch, "E678.53", {"start": v(-14010, 1050) * mm, "end": v(-16010, 1050) * mm});
            skLineSegment(sketch, "E678.54", {"start": v(-15860, 1100) * mm, "end": v(-14160, 1100) * mm});
            skLineSegment(sketch, "E678.55", {"start": v(-14160, 3800) * mm, "end": v(-14160, 1100) * mm});
            skLineSegment(sketch, "E678.56", {"start": v(-15860, 3800) * mm, "end": v(-14160, 3800) * mm});
            skLineSegment(sketch, "E678.57", {"start": v(-15860, 3800) * mm, "end": v(-15860, 1100) * mm});
            skLineSegment(sketch, "E678.58", {"start": v(-15910, 3850) * mm, "end": v(-15910, 1050) * mm});
            skLineSegment(sketch, "E678.59", {"start": v(-14110, 3850) * mm, "end": v(-15910, 3850) * mm});
            skLineSegment(sketch, "E678.60", {"start": v(-14110, 1050) * mm, "end": v(-14110, 3850) * mm});
            skPoint(sketch, "E678.61", {"position": v(-18660, 1100) * mm});
            skLineSegment(sketch, "E678.62", {"start": v(-16810, 3950) * mm, "end": v(-18810, 3950) * mm});
            skLineSegment(sketch, "E678.63", {"start": v(-18810, 3950) * mm, "end": v(-18810, 1050) * mm});
            skLineSegment(sketch, "E678.64", {"start": v(-16810, 3950) * mm, "end": v(-16810, 1050) * mm});
            skLineSegment(sketch, "E678.65", {"start": v(-16810, 1050) * mm, "end": v(-18810, 1050) * mm});
            skLineSegment(sketch, "E678.66", {"start": v(-18660, 1100) * mm, "end": v(-16960, 1100) * mm});
            skLineSegment(sketch, "E678.67", {"start": v(-16960, 3800) * mm, "end": v(-16960, 1100) * mm});
            skLineSegment(sketch, "E678.68", {"start": v(-18660, 3800) * mm, "end": v(-16960, 3800) * mm});
            skLineSegment(sketch, "E678.69", {"start": v(-18660, 3800) * mm, "end": v(-18660, 1100) * mm});
            skLineSegment(sketch, "E678.70", {"start": v(-18710, 3850) * mm, "end": v(-18710, 1050) * mm});
            skLineSegment(sketch, "E678.71", {"start": v(-16910, 3850) * mm, "end": v(-18710, 3850) * mm});
            skLineSegment(sketch, "E678.72", {"start": v(-16910, 1050) * mm, "end": v(-16910, 3850) * mm});
            skPoint(sketch, "E678.73", {"position": v(-13060, 1100) * mm});
            skLineSegment(sketch, "E678.74", {"start": v(-11210, 3950) * mm, "end": v(-13210, 3950) * mm});
            skLineSegment(sketch, "E678.75", {"start": v(-13210, 3950) * mm, "end": v(-13210, 1050) * mm});
            skLineSegment(sketch, "E678.76", {"start": v(-11210, 3950) * mm, "end": v(-11210, 1050) * mm});
            skLineSegment(sketch, "E678.77", {"start": v(-11210, 1050) * mm, "end": v(-13210, 1050) * mm});
            skLineSegment(sketch, "E678.78", {"start": v(-13060, 1100) * mm, "end": v(-11360, 1100) * mm});
            skLineSegment(sketch, "E678.79", {"start": v(-11360, 3800) * mm, "end": v(-11360, 1100) * mm});
            skLineSegment(sketch, "E678.80", {"start": v(-13060, 3800) * mm, "end": v(-11360, 3800) * mm});
            skLineSegment(sketch, "E678.81", {"start": v(-13060, 3800) * mm, "end": v(-13060, 1100) * mm});
            skLineSegment(sketch, "E678.82", {"start": v(-13110, 3850) * mm, "end": v(-13110, 1050) * mm});
            skLineSegment(sketch, "E678.83", {"start": v(-11310, 3850) * mm, "end": v(-13110, 3850) * mm});
            skLineSegment(sketch, "E678.84", {"start": v(-11310, 1050) * mm, "end": v(-11310, 3850) * mm});
            skSolve(sketch);
        }
        {
            var Q0;
            Q0=makeQuery(id+"F82.imprint","IMPRINT",FACE,{"disambiguationData":[TD([[makeQuery(id+"F82.imprint","IMPRINT",EDGE,{"derivedFrom":sQuery(id+"F82.wireOp",EDGE,"E678.16")}),1.0]])]});
            var Q1;
            Q1=makeQuery(id+"F82.imprint","IMPRINT",FACE,{"disambiguationData":[TD([[makeQuery(id+"F82.imprint","IMPRINT",EDGE,{"derivedFrom":sQuery(id+"F82.wireOp",EDGE,"E678.2")}),1.0]])]});
            var Q2;
            Q2=makeQuery(id+"F82.imprint","IMPRINT",FACE,{"disambiguationData":[TD([[makeQuery(id+"F82.imprint","IMPRINT",EDGE,{"derivedFrom":sQuery(id+"F82.wireOp",EDGE,"E678.24")}),1.0]])]});
            var Q3;
            Q3=makeQuery(id+"F82.imprint","IMPRINT",FACE,{"disambiguationData":[TD([[makeQuery(id+"F82.imprint","IMPRINT",EDGE,{"derivedFrom":sQuery(id+"F82.wireOp",EDGE,"E678.62")}),1.0]])]});
            var Q4;
            Q4=makeQuery(id+"F82.imprint","IMPRINT",FACE,{"disambiguationData":[TD([[makeQuery(id+"F82.imprint","IMPRINT",EDGE,{"derivedFrom":sQuery(id+"F82.wireOp",EDGE,"E678.50")}),1.0]])]});
            var Q5;
            Q5=makeQuery(id+"F82.imprint","IMPRINT",FACE,{"disambiguationData":[TD([[makeQuery(id+"F82.imprint","IMPRINT",EDGE,{"derivedFrom":sQuery(id+"F82.wireOp",EDGE,"E678.74")}),1.0]])]});
            var Q6;
            {var subQ3=sQuery(id+"F82.wireOp",EDGE,"E678.38");Q6=makeQuery(id+"F82.imprint","IMPRINT",FACE,{"disambiguationData":[TD([[makeQuery(id+"F82.imprint","IMPRINT",EDGE,{"derivedFrom":subQ3}),-1.0]])]});}
            extrude(context, id + "F83", {"entities" : qUnion([Q0, Q1, Q2, Q3, Q4, Q5, Q6]), "operationType" : NewBodyOperationType.ADD, "depth" : 50 * mm, "offsetDistance" : 25 * mm});
        }
    });
